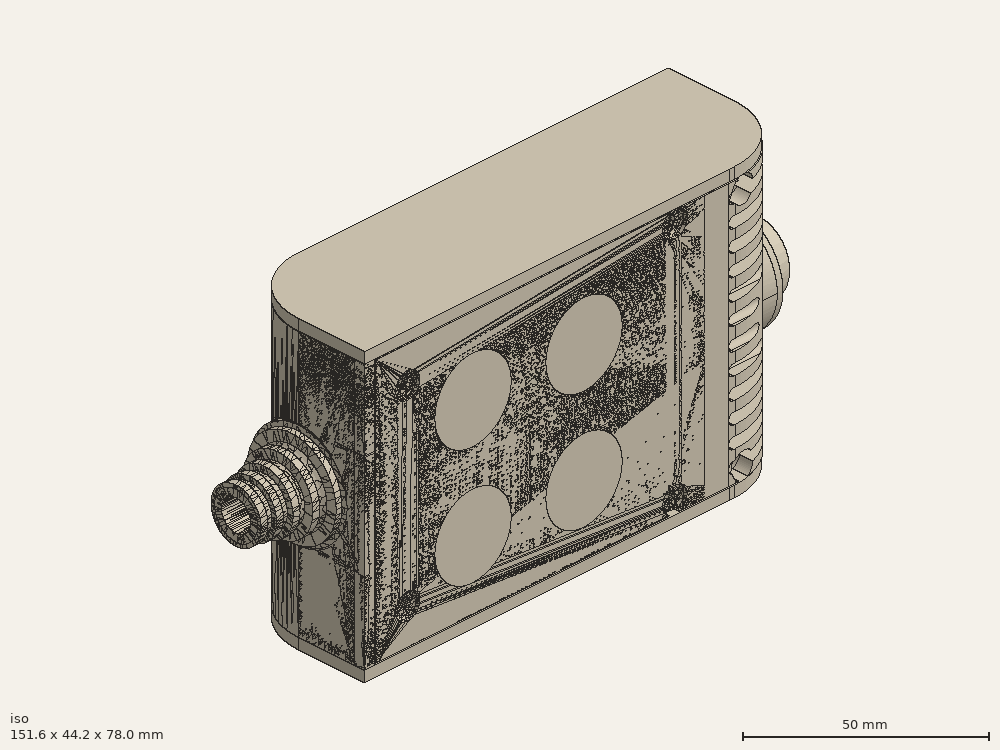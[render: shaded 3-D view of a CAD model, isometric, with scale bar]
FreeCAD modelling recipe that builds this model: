
FCSTD DOCUMENT  (FreeCAD 0.19R0.19.2)
Label: enclosure_196FCStd
License: All rights reserved
LicenseURL: http://en.wikipedia.org/wiki/All_rights_reserved
objects: Part::Revolution×152, Part::MultiFuse×146, Part::Feature×146, Sketcher::SketchObject×84, Part::Cut×70, Part::Cylinder×70, Part::Extrusion×67, Part::Fillet×58, Part::Box×36, App::MeasureDistance×4, PartDesign::Body×2, Image::ImagePlane×1
note: 831 computed .brp shape members not serialized (recipe doc carries the construction recipe); baked Part::Feature solids carry a one-line shape summary decoded from their .brp

FEATURE [Sketcher::SketchObject] Sketch  label="topSketch"
  FullyConstrained = true
  sketch-geometry (20):
    g0: LineSegment StartX=5.21097e-06 StartY=3 StartZ=0 EndX=5.21097e-06 EndY=19 EndZ=0
    g1: ArcOfCircle CenterX=19 CenterY=19 CenterZ=0 NormalX=0 NormalY=0 NormalZ=1 AngleXU=0 Radius=19 StartAngle=1.5708 EndAngle=3.14159
    g2: ArcOfCircle CenterX=19 CenterY=19 CenterZ=0 NormalX=0 NormalY=0 NormalZ=1 AngleXU=0 Radius=16 StartAngle=1.5708 EndAngle=3.14159
    g3: LineSegment StartX=114 StartY=35 StartZ=0 EndX=19 EndY=35 EndZ=0
    g4: LineSegment StartX=5.21097e-06 StartY=3 StartZ=0 EndX=5.21097e-06 EndY=0 EndZ=0
    g5: LineSegment StartX=3 StartY=0 StartZ=0 EndX=5.21097e-06 EndY=0 EndZ=0
    g6: LineSegment StartX=3 StartY=19 StartZ=0 EndX=3 EndY=0 EndZ=0
    g7: LineSegment StartX=19 StartY=38 StartZ=0 EndX=124 EndY=38 EndZ=0
    g8: Circle CenterX=119 CenterY=35 CenterZ=0 NormalX=0 NormalY=0 NormalZ=1 AngleXU=0 Radius=1
    g9: Circle CenterX=121 CenterY=35 CenterZ=0 NormalX=0 NormalY=0 NormalZ=1 AngleXU=0 Radius=1
    g10: Circle CenterX=121 CenterY=33 CenterZ=0 NormalX=0 NormalY=0 NormalZ=1 AngleXU=0 Radius=1
    g11: BSplineCurve PolesCount=3 KnotsCount=2 Degree=2 IsPeriodic=0
    g12: GeomPoint X=119 Y=35 Z=0
    g13: GeomPoint X=121 Y=33 Z=0
    g14: LineSegment StartX=119 StartY=35 StartZ=0 EndX=114 EndY=35 EndZ=0
    g15: ArcOfCircle CenterX=105 CenterY=19 CenterZ=0 NormalX=0 NormalY=0 NormalZ=1 AngleXU=0 Radius=19 StartAngle=5.7297 EndAngle=6.28319
    g16: ArcOfCircle CenterX=105 CenterY=19 CenterZ=0 NormalX=0 NormalY=0 NormalZ=1 AngleXU=0 Radius=16 StartAngle=5.60905 EndAngle=6.28319
    g17: LineSegment StartX=121 StartY=33 StartZ=0 EndX=121 EndY=19 EndZ=0
    g18: LineSegment StartX=124 StartY=38 StartZ=0 EndX=124 EndY=19 EndZ=0
    g19: LineSegment StartX=117.5 StartY=9.01251 StartZ=0 EndX=121.163 EndY=9.0125 EndZ=0
  constraints (46):
    c: Vertical(g0)
    c: Block(g0)
    c: Coincident(g1,g0)
    c: Block(g1)
    c: Coincident(g2,g1)
    c: Block(g2)
    c: Coincident(g3,g2)
    c: Horizontal(g3)
    c: Tangent(g3,g2)
    c: Coincident(g4,g0)
    c: Distance(g4) = 3
    c: Vertical(g4)
    c: Coincident(g5,g4)
    c: Horizontal(g5)
    c: Coincident(g6,g2)
    c: Coincident(g6,g5)
    c: Vertical(g6)
    c: Horizontal(g7)
    c: Distance(g7) = 105
    c: Coincident(g7,g1)
    c: Block(g3)
    c: Weight(g8) = 1
    c: Equal(g8,g9)
    c: Equal(g8,g10)
    c: InternalAlignment(g8,g11)
    c: InternalAlignment(g9,g11)
    c: InternalAlignment(g10,g11)
    c: InternalAlignment(g12,g11)
    c: InternalAlignment(g13,g11)
    c: Block(g11)
    c: Coincident(g14,g11)
    c: Coincident(g14,g3)
    c: Horizontal(g14)
    c: Block(g15)
    c: Coincident(g16,g15)
    c: Block(g16)
    c: Coincident(g17,g11)
    c: Coincident(g17,g16)
    c: Vertical(g17)
    c: Distance(g17) = 14
    c: Coincident(g18,g7)
    c: Coincident(g18,g15)
    c: Vertical(g18)
    c: Distance(g18) = 19
    c: Coincident(g19,g16)
    c: Coincident(g19,g15)
FEATURE [Sketcher::SketchObject] Sketch001  label="bottomSketch"
  FullyConstrained = true
  sketch-geometry (32):
    g0: LineSegment StartX=3.3 StartY=-6.03275e-07 StartZ=0 EndX=98 EndY=-6.03275e-07 EndZ=0
    g1: ArcOfCircle CenterX=98 CenterY=19 CenterZ=0 NormalX=0 NormalY=0 NormalZ=1 AngleXU=0 Radius=19 StartAngle=4.71239 EndAngle=5.71103
    g2: LineSegment StartX=6.3 StartY=8 StartZ=0 EndX=3.3 EndY=8 EndZ=0
    g3: LineSegment StartX=3.3 StartY=8 StartZ=0 EndX=3.3 EndY=-6.03275e-07 EndZ=0
    g4: ArcOfCircle CenterX=8.3 CenterY=5 CenterZ=0 NormalX=0 NormalY=0 NormalZ=1 AngleXU=0 Radius=2 StartAngle=3.14159 EndAngle=4.71239
    g5: LineSegment StartX=6.3 StartY=8 StartZ=0 EndX=6.3 EndY=5 EndZ=0
    g6: ArcOfCircle CenterX=98 CenterY=19 CenterZ=0 NormalX=0 NormalY=0 NormalZ=1 AngleXU=0 Radius=12.7 StartAngle=4.71239 EndAngle=6.28319
    g7: LineSegment StartX=94.7 StartY=3 StartZ=0 EndX=8.3 EndY=3 EndZ=0
    g8-g12: Circle x5 (B-spline internal-alignment scaffolding for g13; pole/knot coordinates omitted)
    g13: BSplineCurve PolesCount=5 KnotsCount=3 Degree=3 IsPeriodic=0
    g14: GeomPoint X=98 Y=6.3 Z=0
    g15: GeomPoint X=96.3938 Y=4.71946 Z=0
    g16: GeomPoint X=94.7 Y=3 Z=0
    g17-g23: Circle x7 (B-spline internal-alignment scaffolding for g24; pole/knot coordinates omitted)
    g24: BSplineCurve PolesCount=7 KnotsCount=5 Degree=3 IsPeriodic=0
    g25-g29: GeomPoint x5 (B-spline internal-alignment scaffolding for g24; pole/knot coordinates omitted)
    g30: ArcOfCircle CenterX=98 CenterY=19 CenterZ=0 NormalX=0 NormalY=0 NormalZ=1 AngleXU=0 Radius=15.7 StartAngle=5.81226 EndAngle=6.28319
    g31: LineSegment StartX=110.7 StartY=19 StartZ=0 EndX=113.7 EndY=19 EndZ=0
  constraints (41):
    c: Horizontal(g0)
    c: Coincident(g1,g0)
    c: Block(g1)
    c: Horizontal(g2)
    c: Distance(g2) = 3
    c: Coincident(g3,g2)
    c: Vertical(g3)
    c: Coincident(g3,g0)
    c: Block(g4)
    c: Block(g2)
    c: Coincident(g5,g2)
    c: Coincident(g5,g4)
    c: Vertical(g5)
    c: Coincident(g6,g1)
    c: Block(g6)
    c: Coincident(g7,g4)
    c: Horizontal(g7)
    c: Block(g0)
    c: Block(g7)
    c: Block(g3)
    c: Coincident(g13,g6)
    c: Weight(g8) = 1
    c: Equal(g8, g9-g12) x4
    c: Coincident(g13,g7)
    c: InternalAlignment(g8-g12 -> g13) x5
    c: InternalAlignment(g14,g13)
    c: InternalAlignment(g15,g13)
    c: InternalAlignment(g16,g13)
    c: Block(g13)
    c: Weight(g17) = 1
    c: Equal(g17, g18-g23) x6
    c: Coincident(g24,g1)
    c: InternalAlignment(g17-g23 -> g24) x7
    c: InternalAlignment(g25-g29 -> g24) x5
    c: Block(g24)
    c: Coincident(g30,g24)
    c: Coincident(g31,g6)
    c: Coincident(g31,g30)
    c: Horizontal(g31)
    c: Block(g31)
    c: Block(g30)
FEATURE [Part::Extrusion] Extrude  label="top"
  Base = -> Sketch
  Dir = (0,0,1)
  DirMode = 2
  FaceMakerClass = Part::FaceMakerBullseye
  LengthFwd = 72
  LengthRev = 0
  Solid = true
  Symmetric = false
FEATURE [Part::Extrusion] Extrude001  label="bottom"
  Base = -> Sketch001
  Dir = (0,0,1)
  DirMode = 2
  FaceMakerClass = Part::FaceMakerBullseye
  LengthFwd = 71.4
  LengthRev = 0
  Placement = pos=(0,0,0.3) rot=(0,0,1;0rad)
  Solid = true
  Symmetric = false
FEATURE [Sketcher::SketchObject] Sketch002  label="topSketch001"
  FullyConstrained = true
  sketch-geometry (8):
    g0: ArcOfCircle CenterX=19 CenterY=19.0975 CenterZ=0 NormalX=0 NormalY=0 NormalZ=1 AngleXU=0 Radius=18.9025 StartAngle=1.5708 EndAngle=3.14674
    g1: LineSegment StartX=0.0977805 StartY=19.0003 StartZ=0 EndX=0.0977805 EndY=0.000251602 EndZ=0
    g2: LineSegment StartX=19 StartY=38 StartZ=0 EndX=124 EndY=38 EndZ=0
    g3: LineSegment StartX=0.0977805 StartY=0.000251602 StartZ=0 EndX=105.098 EndY=0.000251602 EndZ=0
    g4: LineSegment StartX=124 StartY=38 StartZ=0 EndX=125.616 EndY=38 EndZ=0
    g5: LineSegment StartX=105.098 StartY=0.000251602 StartZ=0 EndX=106.713 EndY=0.000251602 EndZ=0
    g6: ArcOfCircle CenterX=106.616 CenterY=19 CenterZ=0 NormalX=0 NormalY=0 NormalZ=1 AngleXU=0 Radius=19 StartAngle=4.71754 EndAngle=6.28319
    g7: LineSegment StartX=125.616 StartY=38 StartZ=0 EndX=125.616 EndY=19 EndZ=0
  constraints (21):
    c: Block(g0)
    c: Coincident(g1,g0)
    c: Vertical(g1)
    c: Horizontal(g2)
    c: Distance(g2) = 105
    c: Coincident(g2,g0)
    c: Distance(g1) = 19
    c: Coincident(g3,g1)
    c: Horizontal(g3)
    c: Distance(g3) = 105
    c: Coincident(g4,g2)
    c: Horizontal(g4)
    c: Distance(g4) = 1.61553
    c: Horizontal(g5)
    c: Equal(g4,g5) = 1.61553
    c: Coincident(g5,g3)
    c: Block(g6)
    c: Coincident(g6,g5)
    c: Coincident(g7,g4)
    c: Coincident(g7,g6)
    c: Vertical(g7)
FEATURE [Part::Extrusion] Extrude002  label="sideA"
  Base = -> Sketch002
  Dir = (0,0,1)
  DirMode = 2
  FaceMakerClass = Part::FaceMakerBullseye
  LengthFwd = 3
  LengthRev = 0
  Placement = pos=(0,0,-3) rot=(0,0,1;0rad)
  Solid = true
  Symmetric = false
FEATURE [Sketcher::SketchObject] Sketch003  label="topSketch002"
  FullyConstrained = true
  sketch-geometry (6):
    g0: LineSegment StartX=19 StartY=38 StartZ=0 EndX=117 EndY=38 EndZ=0
    g1: ArcOfCircle CenterX=19 CenterY=19 CenterZ=0 NormalX=0 NormalY=0 NormalZ=1 AngleXU=0 Radius=19 StartAngle=1.5708 EndAngle=3.14159
    g2: LineSegment StartX=117 StartY=38 StartZ=0 EndX=117 EndY=19 EndZ=0
    g3: LineSegment StartX=98 StartY=1.0161e-12 StartZ=0 EndX=5.22862e-06 EndY=1.0161e-12 EndZ=0
    g4: LineSegment StartX=5.22862e-06 StartY=19 StartZ=0 EndX=5.22862e-06 EndY=1.0161e-12 EndZ=0
    g5: ArcOfCircle CenterX=98 CenterY=19 CenterZ=0 NormalX=0 NormalY=0 NormalZ=1 AngleXU=0 Radius=19 StartAngle=4.71239 EndAngle=6.28319
  constraints (16):
    c: Horizontal(g0)
    c: Distance(g0) = 98
    c: Coincident(g1,g0)
    c: Block(g1)
    c: Coincident(g2,g0)
    c: Vertical(g2)
    c: Distance(g2) = 19
    c: Horizontal(g3)
    c: Coincident(g4,g1)
    c: Vertical(g4)
    c: Coincident(g3,g4)
    c: Block(g3)
    c: Coincident(g5,g2)
    c: Coincident(g5,g3)
    c: Block(g0)
    c: Block(g5)
FEATURE [Sketcher::SketchObject] Sketch004
  FullyConstrained = true
  MapMode = 3
  Placement = pos=(0,0,0) rot=(1,0,0;1.5708rad)
  Support = -> [Extrude]
  sketch-geometry (8):
    g0: Circle CenterX=80.351 CenterY=-67.6202 CenterZ=0 NormalX=0 NormalY=0 NormalZ=1 AngleXU=0 Radius=2
    g1: Circle CenterX=80.351 CenterY=-67.6202 CenterZ=0 NormalX=0 NormalY=0 NormalZ=1 AngleXU=0 Radius=3
    g2: Circle CenterX=80.351 CenterY=-4.92017 CenterZ=0 NormalX=0 NormalY=0 NormalZ=1 AngleXU=0 Radius=2
    g3: Circle CenterX=80.351 CenterY=-4.92017 CenterZ=0 NormalX=0 NormalY=0 NormalZ=1 AngleXU=0 Radius=3
    g4: Circle CenterX=23.851 CenterY=-4.92017 CenterZ=0 NormalX=0 NormalY=0 NormalZ=1 AngleXU=0 Radius=2
    g5: Circle CenterX=23.851 CenterY=-4.92017 CenterZ=0 NormalX=0 NormalY=0 NormalZ=1 AngleXU=0 Radius=3
    g6: Circle CenterX=23.851 CenterY=-67.6202 CenterZ=0 NormalX=0 NormalY=0 NormalZ=1 AngleXU=0 Radius=2
    g7: Circle CenterX=23.851 CenterY=-67.6202 CenterZ=0 NormalX=0 NormalY=0 NormalZ=1 AngleXU=0 Radius=3
  constraints (8):
    c: Block(g3)
    c: Block(g2)
    c: Block(g1)
    c: Block(g0)
    c: Block(g6)
    c: Block(g7)
    c: Block(g4)
    c: Block(g5)
FEATURE [Part::Extrusion] Extrude004
  Base = -> Sketch004
  Dir = (0,-1,2e-16)
  DirMode = 2
  FaceMakerClass = Part::FaceMakerBullseye
  LengthFwd = 6
  LengthRev = 0
  Placement = pos=(0,9,0) rot=(0,0,1;0rad)
  Solid = true
  Symmetric = false
FEATURE [Sketcher::SketchObject] Sketch005
  FullyConstrained = true
  MapMode = 3
  Placement = pos=(0,0,0) rot=(1,0,0;1.5708rad)
  Support = -> [Extrude]
  sketch-geometry (8):
    g0: Circle CenterX=80.351 CenterY=-67.6202 CenterZ=0 NormalX=0 NormalY=0 NormalZ=1 AngleXU=0 Radius=3
    g1: Circle CenterX=80.351 CenterY=-4.92017 CenterZ=0 NormalX=0 NormalY=0 NormalZ=1 AngleXU=0 Radius=3
    g2: Circle CenterX=23.851 CenterY=-4.92017 CenterZ=0 NormalX=0 NormalY=0 NormalZ=1 AngleXU=0 Radius=3
    g3: Circle CenterX=23.851 CenterY=-67.6202 CenterZ=0 NormalX=0 NormalY=0 NormalZ=1 AngleXU=0 Radius=3
    g4: Circle CenterX=23.851 CenterY=-67.6202 CenterZ=0 NormalX=0 NormalY=0 NormalZ=1 AngleXU=0 Radius=5
    g5: Circle CenterX=80.351 CenterY=-67.6202 CenterZ=0 NormalX=0 NormalY=0 NormalZ=1 AngleXU=0 Radius=5
    g6: Circle CenterX=23.851 CenterY=-4.92017 CenterZ=0 NormalX=0 NormalY=0 NormalZ=1 AngleXU=0 Radius=5
    g7: Circle CenterX=80.351 CenterY=-4.92017 CenterZ=0 NormalX=0 NormalY=0 NormalZ=1 AngleXU=0 Radius=5
  constraints (8):
    c: Block(g1)
    c: Block(g0)
    c: Block(g3)
    c: Block(g2)
    c: Block(g5)
    c: Block(g4)
    c: Block(g6)
    c: Block(g7)
FEATURE [Part::Extrusion] Extrude005
  Base = -> Sketch005
  Dir = (0,-1,2e-16)
  DirMode = 2
  FaceMakerClass = Part::FaceMakerBullseye
  LengthFwd = 2
  LengthRev = 0
  Solid = true
  Symmetric = false
FEATURE [Sketcher::SketchObject] Sketch006
  FullyConstrained = true
  MapMode = 3
  Placement = pos=(0,0,0) rot=(1,0,0;1.5708rad)
  sketch-geometry (8):
    g0: Circle CenterX=80.351 CenterY=-67.6202 CenterZ=0 NormalX=0 NormalY=0 NormalZ=1 AngleXU=0 Radius=3
    g1: Circle CenterX=80.351 CenterY=-4.92017 CenterZ=0 NormalX=0 NormalY=0 NormalZ=1 AngleXU=0 Radius=3
    g2: Circle CenterX=23.851 CenterY=-4.92017 CenterZ=0 NormalX=0 NormalY=0 NormalZ=1 AngleXU=0 Radius=3
    g3: Circle CenterX=23.851 CenterY=-67.6202 CenterZ=0 NormalX=0 NormalY=0 NormalZ=1 AngleXU=0 Radius=3
    g4: Circle CenterX=23.851 CenterY=-67.6202 CenterZ=0 NormalX=0 NormalY=0 NormalZ=1 AngleXU=0 Radius=5
    g5: Circle CenterX=80.351 CenterY=-67.6202 CenterZ=0 NormalX=0 NormalY=0 NormalZ=1 AngleXU=0 Radius=5
    g6: Circle CenterX=23.851 CenterY=-4.92017 CenterZ=0 NormalX=0 NormalY=0 NormalZ=1 AngleXU=0 Radius=5
    g7: Circle CenterX=80.351 CenterY=-4.92017 CenterZ=0 NormalX=0 NormalY=0 NormalZ=1 AngleXU=0 Radius=5
  constraints (8):
    c: Block(g1)
    c: Block(g0)
    c: Block(g3)
    c: Block(g2)
    c: Block(g5)
    c: Block(g4)
    c: Block(g6)
    c: Block(g7)
FEATURE [Part::Extrusion] Extrude007
  Base = -> Sketch006
  Dir = (0,-1,2e-16)
  DirMode = 2
  FaceMakerClass = Part::FaceMakerBullseye
  LengthFwd = 2
  LengthRev = 0
  Solid = true
  Symmetric = false
FEATURE [Part::Fillet] Fillet
  Base = -> Extrude007
  Edges = 4 edges r=1.99: [Edge6,Edge12,Edge18,Edge24]
FEATURE [Part::Cut] Cut
  Base = -> Extrude005
  Placement = pos=(0,5,0) rot=(0,0,1;0rad)
  Tool = -> Fillet
FEATURE [Part::MultiFuse] Fusion  label="pCBScrews"
  Placement = pos=(-2.5,0,72.3) rot=(0,0,1;0rad)
  Shapes = -> [Extrude004,Cut]
FEATURE [App::MeasureDistance] Distance  label="Distance: 0.69 mm"
  Distance = 0.685967
  P1 = (24.0138,2.9647,0.3)
  P2 = (23.8901,3,-0.373787)
FEATURE [App::MeasureDistance] Distance001  label="Distance: 0.53 mm"
  Distance = 0.533607
  P1 = (80.2939,3,72.2334)
  P2 = (80.281,2.99661,71.7)
FEATURE [Part::Fillet] Fillet001
  Base = -> Extrude001
  Edges = 1 edges r=2.4: [Edge17]
FEATURE [Part::Fillet] Fillet002  label="bottom001"
  Base = -> Fillet001
  Edges = 1 edges r=2.4: [Edge36]
FEATURE [Part::Fillet] Fillet003  label="top001"
  Base = -> Extrude
  Edges = 1 edges r=2: [Edge1]
FEATURE [Sketcher::SketchObject] Sketch007
  FullyConstrained = true
  sketch-geometry (16):
    g0: LineSegment StartX=4 StartY=0 StartZ=0 EndX=4 EndY=2.4 EndZ=0
    g1: LineSegment StartX=4 StartY=2.4 StartZ=0 EndX=7 EndY=2.4 EndZ=0
    g2: LineSegment StartX=4 StartY=0 StartZ=0 EndX=5.7 EndY=0 EndZ=0
    g3: LineSegment StartX=5.7 StartY=0 StartZ=0 EndX=5.7 EndY=-5.6 EndZ=0
    g4-g8: Circle x5 (B-spline internal-alignment scaffolding for g9; pole/knot coordinates omitted)
    g9: BSplineCurve PolesCount=5 KnotsCount=3 Degree=3 IsPeriodic=0
    g10: GeomPoint X=7 Y=2.4 Z=0
    g11: GeomPoint X=10.4582 Y=-1.55472 Z=0
    g12: GeomPoint X=14 Y=-5.6 Z=0
    g13: LineSegment StartX=14 StartY=-5.6 StartZ=0 EndX=14 EndY=-14.1 EndZ=0
    g14: LineSegment StartX=14 StartY=-14.1 StartZ=0 EndX=6.5 EndY=-14.1 EndZ=0
    g15: LineSegment StartX=5.7 StartY=-5.6 StartZ=0 EndX=6.5 EndY=-14.1 EndZ=0
  constraints (28):
    c: Distance(g0) = 2.4
    c: Vertical(g0)
    c: Block(g0)
    c: Coincident(g1,g0)
    c: Horizontal(g1)
    c: Distance(g1) = 3
    c: Coincident(g2,g0)
    c: Horizontal(g2)
    c: Distance(g2) = 1.7
    c: Coincident(g3,g2)
    c: Vertical(g3)
    c: Distance(g3) = 5.6
    c: Coincident(g9,g1)
    c: Weight(g4) = 1
    c: Equal(g4, g5-g8) x4
    c: InternalAlignment(g4-g8 -> g9) x5
    c: InternalAlignment(g10,g9)
    c: InternalAlignment(g11,g9)
    c: InternalAlignment(g12,g9)
    c: Block(g9)
    c: Coincident(g13,g9)
    c: Vertical(g13)
    c: Distance(g13) = 8.5
    c: Coincident(g14,g13)
    c: Horizontal(g14)
    c: Distance(g14) = 7.5
    c: Coincident(g15,g3)
    c: Coincident(g15,g14)
FEATURE [Part::Feature] Face
  shape: bbox 10 x 16.5 x 2e-07 mm, 1 faces, 0 solids (baked)
FEATURE [Part::Revolution] Revolve  label="plugHousing"
  Angle = 360
  Axis = (0,1,0)
  Base = (0,0,0)
  FaceMakerClass = Part::FaceMakerBullseye
  Placement = pos=(0,0,36.15) rot=(0,0,1;0rad)
  Solid = false
  Source = -> Face
  Symmetric = false
FEATURE [Part::Feature] Face001
  shape: bbox 10 x 16.5 x 2e-07 mm, 1 faces, 0 solids (baked)
FEATURE [Part::Revolution] Revolve001  label="plugHousing001"
  Angle = 360
  Axis = (0,1,0)
  Base = (0,0,0)
  FaceMakerClass = Part::FaceMakerBullseye
  Placement = pos=(0,0,36.15) rot=(0,0,1;0rad)
  Solid = false
  Source = -> Face001
  Symmetric = false
FEATURE [Part::MultiFuse] Fusion001  label="plugHousing002"
  Placement = pos=(0,0,0) rot=(0,0,1;1.5708rad)
  Shapes = -> [Revolve001,Revolve]
FEATURE [Part::Feature] Face002
  shape: bbox 10 x 16.5 x 2e-07 mm, 1 faces, 0 solids (baked)
FEATURE [Part::Revolution] Revolve003  label="plugHousing005"
  Angle = 360
  Axis = (0,1,0)
  Base = (0,0,0)
  FaceMakerClass = Part::FaceMakerBullseye
  Placement = pos=(0,0,36.15) rot=(0,0,1;0rad)
  Solid = false
  Source = -> Face002
  Symmetric = false
FEATURE [Part::Feature] Face003
  shape: bbox 10 x 16.5 x 2e-07 mm, 1 faces, 0 solids (baked)
FEATURE [Part::Revolution] Revolve002  label="plugHousing003"
  Angle = 360
  Axis = (0,1,0)
  Base = (0,0,0)
  FaceMakerClass = Part::FaceMakerBullseye
  Placement = pos=(0,0,36.15) rot=(0,0,1;0rad)
  Solid = false
  Source = -> Face003
  Symmetric = false
FEATURE [Part::MultiFuse] Fusion002  label="plugHousing004"
  Placement = pos=(0,0,0) rot=(0,0,1;1.5708rad)
  Shapes = -> [Revolve002,Revolve003]
FEATURE [Part::MultiFuse] Fusion003  label="plugHousing006"
  Placement = pos=(0,19,0) rot=(0,0,1;3.14159rad)
  Shapes = -> [Fusion002,Fusion001]
FEATURE [Part::Feature] Face004
  shape: bbox 10 x 16.5 x 2e-07 mm, 1 faces, 0 solids (baked)
FEATURE [Part::Revolution] Revolve006  label="plugHousing010"
  Angle = 360
  Axis = (0,1,0)
  Base = (0,0,0)
  FaceMakerClass = Part::FaceMakerBullseye
  Placement = pos=(0,0,36.15) rot=(0,0,1;0rad)
  Solid = false
  Source = -> Face004
  Symmetric = false
FEATURE [Part::Feature] Face005
  shape: bbox 10 x 16.5 x 2e-07 mm, 1 faces, 0 solids (baked)
FEATURE [Part::Revolution] Revolve007  label="plugHousing011"
  Angle = 360
  Axis = (0,1,0)
  Base = (0,0,0)
  FaceMakerClass = Part::FaceMakerBullseye
  Placement = pos=(0,0,36.15) rot=(0,0,1;0rad)
  Solid = false
  Source = -> Face005
  Symmetric = false
FEATURE [Part::Feature] Face006
  shape: bbox 10 x 16.5 x 2e-07 mm, 1 faces, 0 solids (baked)
FEATURE [Part::Revolution] Revolve004  label="plugHousing007"
  Angle = 360
  Axis = (0,1,0)
  Base = (0,0,0)
  FaceMakerClass = Part::FaceMakerBullseye
  Placement = pos=(0,0,36.15) rot=(0,0,1;0rad)
  Solid = false
  Source = -> Face006
  Symmetric = false
FEATURE [Part::MultiFuse] Fusion004  label="plugHousing009"
  Placement = pos=(0,0,0) rot=(0,0,1;1.5708rad)
  Shapes = -> [Revolve004,Revolve007]
FEATURE [Part::Feature] Face007
  shape: bbox 10 x 16.5 x 2e-07 mm, 1 faces, 0 solids (baked)
FEATURE [Part::Revolution] Revolve005  label="plugHousing008"
  Angle = 360
  Axis = (0,1,0)
  Base = (0,0,0)
  FaceMakerClass = Part::FaceMakerBullseye
  Placement = pos=(0,0,36.15) rot=(0,0,1;0rad)
  Solid = false
  Source = -> Face007
  Symmetric = false
FEATURE [Part::MultiFuse] Fusion005  label="plugHousing012"
  Placement = pos=(0,0,0) rot=(0,0,1;1.5708rad)
  Shapes = -> [Revolve006,Revolve005]
FEATURE [Part::MultiFuse] Fusion006  label="plugHousing013"
  Placement = pos=(0,19,0) rot=(0,0,1;3.14159rad)
  Shapes = -> [Fusion005,Fusion004]
FEATURE [Part::MultiFuse] Fusion007  label="plugHousing014"
  Placement = pos=(122.621,0,-0.15) rot=(0,0,1;0rad)
  Shapes = -> [Fusion003,Fusion006]
FEATURE [Part::Cylinder] Cylinder002
  Angle = 360
  AttacherType = Attacher::AttachEngine3D
  Height = 20
  Placement = pos=(0,0,36.15) rot=(0,0,1;0rad)
  Radius = 4
FEATURE [Part::Cylinder] Cylinder003
  Angle = 360
  AttacherType = Attacher::AttachEngine3D
  Height = 10
  Placement = pos=(0,0,36.15) rot=(0,0,1;0rad)
  Radius = 4
FEATURE [Part::MultiFuse] Fusion009  label="removeToCreateHoleForPlugHousing"
  Placement = pos=(70,19,36.15) rot=(0,1,0;1.5708rad)
  Shapes = -> [Cylinder002,Cylinder003]
FEATURE [Part::Cylinder] Cylinder004
  Angle = 360
  AttacherType = Attacher::AttachEngine3D
  Height = 20
  Placement = pos=(0,0,36.15) rot=(0,0,1;0rad)
  Radius = 4
FEATURE [Part::Cylinder] Cylinder005
  Angle = 360
  AttacherType = Attacher::AttachEngine3D
  Height = 10
  Placement = pos=(0,0,36.15) rot=(0,0,1;0rad)
  Radius = 4
FEATURE [Part::MultiFuse] Fusion010  label="removeToCreateHoleForPlugHousing001"
  Placement = pos=(70,19,36.15) rot=(0,1,0;1.5708rad)
  Shapes = -> [Cylinder004,Cylinder005]
FEATURE [Part::Cut] Cut001
  Base = -> Fillet003
  Tool = -> Fusion010
FEATURE [Part::Cut] Cut002  label="Bottom"
  Base = -> Fillet002
  Tool = -> Fusion009
FEATURE [Part::Feature] Face008
  shape: bbox 10 x 16.5 x 2e-07 mm, 1 faces, 0 solids (baked)
FEATURE [Part::Revolution] Revolve011  label="plugHousing021"
  Angle = 360
  Axis = (0,1,0)
  Base = (0,0,0)
  FaceMakerClass = Part::FaceMakerBullseye
  Placement = pos=(0,0,36.15) rot=(0,0,1;0rad)
  Solid = false
  Source = -> Face008
  Symmetric = false
FEATURE [Part::Feature] Face009
  shape: bbox 10 x 16.5 x 2e-07 mm, 1 faces, 0 solids (baked)
FEATURE [Part::Revolution] Revolve012  label="plugHousing022"
  Angle = 360
  Axis = (0,1,0)
  Base = (0,0,0)
  FaceMakerClass = Part::FaceMakerBullseye
  Placement = pos=(0,0,36.15) rot=(0,0,1;0rad)
  Solid = false
  Source = -> Face009
  Symmetric = false
FEATURE [Part::Feature] Face010 .. Face013  x4 (patterned run collapsed; names and placements below)
  shape: bbox 10 x 16.5 x 2e-07 mm, 1 faces, 0 solids (baked)
FEATURE [Part::Revolution] Revolve015  label="plugHousing027"
  Angle = 360
  Axis = (0,1,0)
  Base = (0,0,0)
  FaceMakerClass = Part::FaceMakerBullseye
  Placement = pos=(0,0,36.15) rot=(0,0,1;0rad)
  Solid = false
  Source = -> Face013
  Symmetric = false
FEATURE [Part::Feature] Face014
  shape: bbox 10 x 16.5 x 2e-07 mm, 1 faces, 0 solids (baked)
FEATURE [Part::Feature] Face015
  shape: bbox 10 x 16.5 x 2e-07 mm, 1 faces, 0 solids (baked)
FEATURE [Part::Feature] Face016
  shape: bbox 10 x 16.5 x 2e-07 mm, 1 faces, 0 solids (baked)
FEATURE [Part::Revolution] Revolve019  label="plugHousing033"
  Angle = 360
  Axis = (0,1,0)
  Base = (0,0,0)
  FaceMakerClass = Part::FaceMakerBullseye
  Placement = pos=(0,0,36.15) rot=(0,0,1;0rad)
  Solid = false
  Source = -> Face016
  Symmetric = false
FEATURE [Part::Feature] Face017
  shape: bbox 10 x 16.5 x 2e-07 mm, 1 faces, 0 solids (baked)
FEATURE [Part::Revolution] Revolve020  label="plugHousing034"
  Angle = 360
  Axis = (0,1,0)
  Base = (0,0,0)
  FaceMakerClass = Part::FaceMakerBullseye
  Placement = pos=(0,0,36.15) rot=(0,0,1;0rad)
  Solid = false
  Source = -> Face017
  Symmetric = false
FEATURE [Part::Feature] Face018
  shape: bbox 10 x 16.5 x 2e-07 mm, 1 faces, 0 solids (baked)
FEATURE [Part::Revolution] Revolve016  label="plugHousing030"
  Angle = 360
  Axis = (0,1,0)
  Base = (0,0,0)
  FaceMakerClass = Part::FaceMakerBullseye
  Placement = pos=(0,0,36.15) rot=(0,0,1;0rad)
  Solid = false
  Source = -> Face018
  Symmetric = false
FEATURE [Part::MultiFuse] Fusion020  label="plugHousing038"
  Placement = pos=(0,0,0) rot=(0,0,1;1.5708rad)
  Shapes = -> [Revolve016,Revolve020]
FEATURE [Part::Feature] Face019
  shape: bbox 10 x 16.5 x 2e-07 mm, 1 faces, 0 solids (baked)
FEATURE [Part::Feature] Face020
  shape: bbox 10 x 16.5 x 2e-07 mm, 1 faces, 0 solids (baked)
FEATURE [Part::Revolution] Revolve017  label="plugHousing031"
  Angle = 360
  Axis = (0,1,0)
  Base = (0,0,0)
  FaceMakerClass = Part::FaceMakerBullseye
  Placement = pos=(0,0,36.15) rot=(0,0,1;0rad)
  Solid = false
  Source = -> Face020
  Symmetric = false
FEATURE [Part::MultiFuse] Fusion021  label="plugHousing039"
  Placement = pos=(0,0,0) rot=(0,0,1;1.5708rad)
  Shapes = -> [Revolve019,Revolve017]
FEATURE [Part::MultiFuse] Fusion023  label="plugHousing041"
  Placement = pos=(0,19,0) rot=(0,0,1;3.14159rad)
  Shapes = -> [Fusion021,Fusion020]
FEATURE [Part::Revolution] Revolve022  label="plugHousing043"
  Angle = 360
  Axis = (0,1,0)
  Base = (0,0,0)
  FaceMakerClass = Part::FaceMakerBullseye
  Placement = pos=(0,0,36.15) rot=(0,0,1;0rad)
  Solid = false
  Source = -> Face019
  Symmetric = false
FEATURE [Part::Feature] Face021
  shape: bbox 10 x 16.5 x 2e-07 mm, 1 faces, 0 solids (baked)
FEATURE [Part::Revolution] Revolve023  label="plugHousing044"
  Angle = 360
  Axis = (0,1,0)
  Base = (0,0,0)
  FaceMakerClass = Part::FaceMakerBullseye
  Placement = pos=(0,0,36.15) rot=(0,0,1;0rad)
  Solid = false
  Source = -> Face021
  Symmetric = false
FEATURE [Part::Feature] Face022
  shape: bbox 10 x 16.5 x 2e-07 mm, 1 faces, 0 solids (baked)
FEATURE [Part::Revolution] Revolve018  label="plugHousing032"
  Angle = 360
  Axis = (0,1,0)
  Base = (0,0,0)
  FaceMakerClass = Part::FaceMakerBullseye
  Placement = pos=(0,0,36.15) rot=(0,0,1;0rad)
  Solid = false
  Source = -> Face022
  Symmetric = false
FEATURE [Part::MultiFuse] Fusion022  label="plugHousing040"
  Placement = pos=(0,0,0) rot=(0,0,1;1.5708rad)
  Shapes = -> [Revolve018,Revolve023]
FEATURE [Part::Feature] Face023
  shape: bbox 10 x 16.5 x 2e-07 mm, 1 faces, 0 solids (baked)
FEATURE [Part::Revolution] Revolve021  label="plugHousing035"
  Angle = 360
  Axis = (0,1,0)
  Base = (0,0,0)
  FaceMakerClass = Part::FaceMakerBullseye
  Placement = pos=(0,0,36.15) rot=(0,0,1;0rad)
  Solid = false
  Source = -> Face023
  Symmetric = false
FEATURE [Part::MultiFuse] Fusion018  label="plugHousing036"
  Placement = pos=(0,0,0) rot=(0,0,1;1.5708rad)
  Shapes = -> [Revolve022,Revolve021]
FEATURE [Part::MultiFuse] Fusion019  label="plugHousing037"
  Placement = pos=(0,19,0) rot=(0,0,1;3.14159rad)
  Shapes = -> [Fusion018,Fusion022]
FEATURE [Part::MultiFuse] Fusion024  label="plugHousing042"
  Placement = pos=(122.621,0,-0.15) rot=(0,0,1;0rad)
  Shapes = -> [Fusion023,Fusion019]
FEATURE [Part::Cylinder] Cylinder006
  Angle = 360
  AttacherType = Attacher::AttachEngine3D
  Height = 20
  Placement = pos=(0,0,36.15) rot=(0,0,1;0rad)
  Radius = 14.3
FEATURE [Part::Cylinder] Cylinder007
  Angle = 360
  AttacherType = Attacher::AttachEngine3D
  Height = 10
  Placement = pos=(0,0,36.15) rot=(0,0,1;0rad)
  Radius = 4
FEATURE [Part::MultiFuse] Fusion026  label="removeToCreteHoleForPlugHousing"
  Placement = pos=(70,19,36) rot=(0,1,0;1.5708rad)
  Shapes = -> [Cylinder006,Cylinder007]
FEATURE [Part::Box] Box001  label="Cube001"
  AttacherType = Attacher::AttachEngine3D
  Height = 28
  Length = 3
  Placement = pos=(110.7,19,22) rot=(0,0,1;0rad)
  Width = 15.7
FEATURE [Part::Cut] Cut003  label="top002"
  Base = -> Cut001
  Tool = -> Fusion007
FEATURE [Part::Revolution] Revolve008  label="plugHousing015"
  Angle = 360
  Axis = (0,1,0)
  Base = (0,0,0)
  FaceMakerClass = Part::FaceMakerBullseye
  Placement = pos=(0,0,36.15) rot=(0,0,1;0rad)
  Solid = false
  Source = -> Face010
  Symmetric = false
FEATURE [Part::MultiFuse] Fusion013  label="plugHousing020"
  Placement = pos=(0,0,0) rot=(0,0,1;1.5708rad)
  Shapes = -> [Revolve008,Revolve012]
FEATURE [Part::Cut] Cut004  label="top003"
  Base = -> Cut003
  Placement = pos=(1,0,0) rot=(0,0,1;0rad)
  Tool = -> Fusion026
FEATURE [Part::Cylinder] Cylinder008
  Angle = 360
  AttacherType = Attacher::AttachEngine3D
  Height = 20
  Placement = pos=(0,0,36.15) rot=(0,0,1;0rad)
  Radius = 10.3
FEATURE [Part::Cylinder] Cylinder009
  Angle = 360
  AttacherType = Attacher::AttachEngine3D
  Height = 10
  Placement = pos=(0,0,36.15) rot=(0,0,1;0rad)
  Radius = 4
FEATURE [Part::MultiFuse] Fusion027  label="removeToCreteHoleForPlugHousing001"
  Placement = pos=(70,19,36) rot=(0,1,0;1.5708rad)
  Shapes = -> [Cylinder008,Cylinder009]
FEATURE [Part::Cut] Cut005  label="plugHousingTab"
  Base = -> Box001
  Tool = -> Fusion027
FEATURE [Part::MultiFuse] Fusion028  label="plugHousing045"
  Shapes = -> [Fusion024,Cut005]
FEATURE [Part::Box] Box002  label="Cube002"
  AttacherType = Attacher::AttachEngine3D
  Height = 28.8
  Length = 3
  Placement = pos=(107.3,28,21.6) rot=(0,0,1;0rad)
  Width = 7
FEATURE [Part::Box] Box003  label="Cube003"
  AttacherType = Attacher::AttachEngine3D
  Height = 3
  Length = 6.4
  Placement = pos=(107.3,28,18.6) rot=(0,0,1;0rad)
  Width = 7
FEATURE [Part::Box] Box004  label="Cube004"
  AttacherType = Attacher::AttachEngine3D
  Height = 3
  Length = 6.4
  Placement = pos=(107.3,28,50.4) rot=(0,0,1;0rad)
  Width = 7
FEATURE [Part::MultiFuse] Fusion029  label="plugHousingBracketHolder"
  Shapes = -> [Box004,Box002,Box003]
FEATURE [Part::Cylinder] Cylinder010
  Angle = 360
  AttacherType = Attacher::AttachEngine3D
  Height = 20
  Placement = pos=(0,0,36.15) rot=(0,0,1;0rad)
  Radius = 14.3
FEATURE [Part::Cylinder] Cylinder011
  Angle = 360
  AttacherType = Attacher::AttachEngine3D
  Height = 10
  Placement = pos=(0,0,36.15) rot=(0,0,1;0rad)
  Radius = 4
FEATURE [Part::MultiFuse] Fusion030  label="removeToCreteHoleForPlugHousing002"
  Placement = pos=(70,19,36) rot=(0,1,0;1.5708rad)
  Shapes = -> [Cylinder010,Cylinder011]
FEATURE [Part::Cut] Cut006  label="plugHousingBracketHolder001"
  Base = -> Fusion029
  Tool = -> Fusion030
FEATURE [Part::Cylinder] Cylinder012
  Angle = 360
  AttacherType = Attacher::AttachEngine3D
  Height = 20
  Placement = pos=(0,0,36.15) rot=(0,0,1;0rad)
  Radius = 7
FEATURE [Part::Cylinder] Cylinder013
  Angle = 360
  AttacherType = Attacher::AttachEngine3D
  Height = 10
  Placement = pos=(0,0,36.15) rot=(0,0,1;0rad)
  Radius = 4
FEATURE [Part::MultiFuse] Fusion032  label="removeToCreteHoleForPlugHousing003"
  Placement = pos=(70,19,36) rot=(0,1,0;1.5708rad)
  Shapes = -> [Cylinder012,Cylinder013]
FEATURE [Part::Cut] Cut007  label="bottom002"
  Base = -> Cut002
  Tool = -> Fusion032
FEATURE [Sketcher::SketchObject] Sketch008
  FullyConstrained = true
  sketch-geometry (54):
    g0: LineSegment StartX=-4.2 StartY=0 StartZ=0 EndX=-6.2 EndY=0 EndZ=0
    g1: LineSegment StartX=-14 StartY=-18 StartZ=0 EndX=-14 EndY=-26.5 EndZ=0
    g2: LineSegment StartX=-4.2 StartY=0 StartZ=0 EndX=-4.2 EndY=-13.4877 EndZ=0
    g3: Circle CenterX=-4.2 CenterY=-13.4877 CenterZ=0 NormalX=0 NormalY=0 NormalZ=1 AngleXU=0 Radius=1
    g4: Circle CenterX=-4.2 CenterY=-26.5 CenterZ=0 NormalX=0 NormalY=0 NormalZ=1 AngleXU=0 Radius=1
    g5: Circle CenterX=-8.2 CenterY=-26.5 CenterZ=0 NormalX=0 NormalY=0 NormalZ=1 AngleXU=0 Radius=1
    g6: BSplineCurve PolesCount=3 KnotsCount=2 Degree=2 IsPeriodic=0
    g7: GeomPoint X=-4.2 Y=-13.4877 Z=0
    g8: GeomPoint X=-8.2 Y=-26.5 Z=0
    g9: LineSegment StartX=-14 StartY=-26.5 StartZ=0 EndX=-8.2 EndY=-26.5 EndZ=0
    g10: LineSegment StartX=-10.15 StartY=-12 StartZ=0 EndX=-10.15 EndY=-14 EndZ=0
    g11: LineSegment StartX=-12.8401 StartY=-16 StartZ=0 EndX=-10.1571 EndY=-16 EndZ=0
    g12: LineSegment StartX=-10.15 StartY=-14 StartZ=0 EndX=-8.70761 EndY=-14 EndZ=0
    g13: LineSegment StartX=-12.8401 StartY=-16 StartZ=0 EndX=-12.8401 EndY=-17.6958 EndZ=0
    g14: LineSegment StartX=-10.15 StartY=-12 StartZ=0 EndX=-7.79258 EndY=-12 EndZ=0
    g15: Circle CenterX=-6.2215 CenterY=-2 CenterZ=0 NormalX=0 NormalY=0 NormalZ=1 AngleXU=0 Radius=1
    g16: Circle CenterX=-6.22762 CenterY=-2.58724 CenterZ=0 NormalX=0 NormalY=0 NormalZ=1 AngleXU=0 Radius=1
    g17: Circle CenterX=-6.32538 CenterY=-4 CenterZ=0 NormalX=0 NormalY=0 NormalZ=1 AngleXU=0 Radius=1
    g18: BSplineCurve PolesCount=3 KnotsCount=2 Degree=2 IsPeriodic=0
    g19: GeomPoint X=-6.2215 Y=-2 Z=0
    g20: GeomPoint X=-6.32538 Y=-4 Z=0
    g21: Circle CenterX=-6.48644 CenterY=-5.99526 CenterZ=0 NormalX=0 NormalY=0 NormalZ=1 AngleXU=0 Radius=1
    g22: Circle CenterX=-6.58486 CenterY=-6.99526 CenterZ=0 NormalX=0 NormalY=0 NormalZ=1 AngleXU=0 Radius=1
    g23: Circle CenterX=-6.77343 CenterY=-8 CenterZ=0 NormalX=0 NormalY=0 NormalZ=1 AngleXU=0 Radius=1
    g24: BSplineCurve PolesCount=3 KnotsCount=2 Degree=2 IsPeriodic=0
    g25: GeomPoint X=-6.48644 Y=-5.99526 Z=0
    g26: GeomPoint X=-6.77343 Y=-8 Z=0
    g27: Circle CenterX=-7.19003 CenterY=-10 CenterZ=0 NormalX=0 NormalY=0 NormalZ=1 AngleXU=0 Radius=1
    g28: Circle CenterX=-7.44407 CenterY=-11.0915 CenterZ=0 NormalX=0 NormalY=0 NormalZ=1 AngleXU=0 Radius=1
    g29: Circle CenterX=-7.79258 CenterY=-12 CenterZ=0 NormalX=0 NormalY=0 NormalZ=1 AngleXU=0 Radius=1
    g30: BSplineCurve PolesCount=3 KnotsCount=2 Degree=2 IsPeriodic=0
    g31: GeomPoint X=-7.19003 Y=-10 Z=0
    g32: GeomPoint X=-7.79258 Y=-12 Z=0
    g33: Circle CenterX=-8.70761 CenterY=-14 CenterZ=0 NormalX=0 NormalY=0 NormalZ=1 AngleXU=0 Radius=1
    g34: Circle CenterX=-9.33087 CenterY=-15.1837 CenterZ=0 NormalX=0 NormalY=0 NormalZ=1 AngleXU=0 Radius=1
    g35: Circle CenterX=-10.1571 CenterY=-16 CenterZ=0 NormalX=0 NormalY=0 NormalZ=1 AngleXU=0 Radius=1
    g36: BSplineCurve PolesCount=3 KnotsCount=2 Degree=2 IsPeriodic=0
    g37: GeomPoint X=-8.70761 Y=-14 Z=0
    g38: GeomPoint X=-10.1571 Y=-16 Z=0
    g39: Circle CenterX=-12.8401 CenterY=-17.6958 CenterZ=0 NormalX=0 NormalY=0 NormalZ=1 AngleXU=0 Radius=1
    g40: Circle CenterX=-13.3521 CenterY=-17.9027 CenterZ=0 NormalX=0 NormalY=0 NormalZ=1 AngleXU=0 Radius=1
    g41: Circle CenterX=-14 CenterY=-18 CenterZ=0 NormalX=0 NormalY=0 NormalZ=1 AngleXU=0 Radius=1
    g42: BSplineCurve PolesCount=3 KnotsCount=2 Degree=2 IsPeriodic=0
    g43: GeomPoint X=-12.8401 Y=-17.6958 Z=0
    g44: GeomPoint X=-14 Y=-18 Z=0
    g45: LineSegment StartX=-6.2 StartY=0 StartZ=0 EndX=-7.2 EndY=0 EndZ=0
    g46: LineSegment StartX=-7.2 StartY=0 StartZ=0 EndX=-7.2 EndY=-2 EndZ=0
    g47: LineSegment StartX=-7.2 StartY=-2 StartZ=0 EndX=-6.2215 EndY=-2 EndZ=0
    g48: LineSegment StartX=-6.32538 StartY=-4 StartZ=0 EndX=-7.65538 EndY=-4 EndZ=0
    g49: LineSegment StartX=-7.65538 StartY=-4 StartZ=0 EndX=-7.65538 EndY=-5.99526 EndZ=0
    g50: LineSegment StartX=-7.65538 StartY=-5.99526 StartZ=0 EndX=-6.48644 EndY=-5.99526 EndZ=0
    g51: LineSegment StartX=-6.77343 StartY=-8 StartZ=0 EndX=-8.43343 EndY=-8 EndZ=0
    g52: LineSegment StartX=-8.43343 StartY=-8 StartZ=0 EndX=-8.43343 EndY=-10 EndZ=0
    g53: LineSegment StartX=-8.43343 StartY=-10 StartZ=0 EndX=-7.19003 EndY=-10 EndZ=0
  constraints (112):
    c: Horizontal(g0)
    c: Distance(g0) = 2
    c: Block(g0)
    c: Vertical(g1)
    c: Coincident(g2,g0)
    c: Vertical(g2)
    c: Block(g2)
    c: Coincident(g6,g2)
    c: Weight(g3) = 1
    c: Equal(g3,g4)
    c: Equal(g3,g5)
    c: InternalAlignment(g3,g6)
    c: InternalAlignment(g4,g6)
    c: InternalAlignment(g5,g6)
    c: InternalAlignment(g7,g6)
    c: InternalAlignment(g8,g6)
    c: Block(g6)
    c: Coincident(g9,g1)
    c: Coincident(g9,g6)
    c: Horizontal(g9)
    c: Vertical(g10)
    c: Block(g10)
    c: Horizontal(g11)
    c: Block(g11)
    c: Coincident(g12,g10)
    c: Horizontal(g12)
    c: Block(g12)
    c: Coincident(g13,g11)
    c: Vertical(g13)
    c: Block(g13)
    c: Coincident(g14,g10)
    c: Horizontal(g14)
    c: Block(g14)
    c: Block(g9)
    c: Block(g1)
    c: Weight(g15) = 1
    c: Equal(g15,g16)
    c: Equal(g15,g17)
    c: InternalAlignment(g15,g18)
    c: InternalAlignment(g16,g18)
    c: InternalAlignment(g17,g18)
    c: InternalAlignment(g19,g18)
    c: InternalAlignment(g20,g18)
    c: Weight(g21) = 1
    c: Equal(g21,g22)
    c: Equal(g21,g23)
    c: InternalAlignment(g21,g24)
    c: InternalAlignment(g22,g24)
    c: InternalAlignment(g23,g24)
    c: InternalAlignment(g25,g24)
    c: InternalAlignment(g26,g24)
    c: Weight(g27) = 1
    c: Equal(g27,g28)
    c: Equal(g27,g29)
    c: Coincident(g30,g14)
    c: InternalAlignment(g27,g30)
    c: InternalAlignment(g28,g30)
    c: InternalAlignment(g29,g30)
    c: InternalAlignment(g31,g30)
    c: InternalAlignment(g32,g30)
    c: Coincident(g36,g12)
    c: Weight(g33) = 1
    c: Equal(g33,g34)
    c: Equal(g33,g35)
    c: Coincident(g36,g11)
    c: InternalAlignment(g33,g36)
    c: InternalAlignment(g34,g36)
    c: InternalAlignment(g35,g36)
    c: InternalAlignment(g37,g36)
    c: InternalAlignment(g38,g36)
    c: Coincident(g42,g13)
    c: Weight(g39) = 1
    c: Equal(g39,g40)
    c: Equal(g39,g41)
    c: Coincident(g42,g1)
    c: InternalAlignment(g39,g42)
    c: InternalAlignment(g40,g42)
    c: InternalAlignment(g41,g42)
    c: InternalAlignment(g43,g42)
    c: InternalAlignment(g44,g42)
    c: Block(g18)
    c: Block(g24)
    c: Block(g30)
    c: Block(g36)
    c: Block(g42)
    c: Horizontal(g45)
    c: Coincident(g45,g0)
    c: Vertical(g46)
    c: Coincident(g46,g45)
    c: Coincident(g47,g46)
    c: Coincident(g47,g18)
    c: Horizontal(g47)
    c: Block(g46)
    c: Coincident(g48,g18)
    c: Horizontal(g48)
    c: Distance(g48) = 1.33
    c: Vertical(g49)
    c: Coincident(g49,g48)
    c: Coincident(g50,g49)
    c: Coincident(g50,g24)
    c: Horizontal(g50)
    c: Tangent(g50,g22)
    c: Horizontal(g51)
    c: Coincident(g51,g24)
    c: Block(g51)
    c: Vertical(g52)
    c: Block(g52)
    c: Coincident(g52,g51)
    c: Coincident(g53,g52)
    c: Coincident(g53,g30)
    c: Horizontal(g53)
    c: Distance(g1) = 8.5
FEATURE [Part::Feature] Face024
  shape: bbox 9.8 x 26.5 x 2e-07 mm, 1 faces, 0 solids (baked)
FEATURE [Part::Revolution] Revolve024
  Angle = 360
  Axis = (0,1,0)
  Base = (0,0,0)
  FaceMakerClass = Part::FaceMakerBullseye
  Placement = pos=(0,0,0) rot=(0,0,1;1.5708rad)
  Solid = false
  Source = -> Face024
  Symmetric = false
FEATURE [Part::Feature] Face025
  shape: bbox 9.8 x 26.5 x 2e-07 mm, 1 faces, 0 solids (baked)
FEATURE [Part::Revolution] Revolve025
  Angle = 360
  Axis = (0,1,0)
  Base = (0,0,0)
  FaceMakerClass = Part::FaceMakerBullseye
  Placement = pos=(0,0,0) rot=(0,0,1;1.5708rad)
  Solid = false
  Source = -> Face025
  Symmetric = false
FEATURE [Part::MultiFuse] Fusion033
  Placement = pos=(-18,19,36) rot=(0,0,1;0rad)
  Shapes = -> [Revolve025,Revolve024]
FEATURE [Part::Cylinder] Cylinder014
  Angle = 360
  AttacherType = Attacher::AttachEngine3D
  Height = 20
  Placement = pos=(0,0,36.15) rot=(0,0,1;0rad)
  Radius = 14.3
FEATURE [Part::Cylinder] Cylinder015
  Angle = 360
  AttacherType = Attacher::AttachEngine3D
  Height = 10
  Placement = pos=(0,0,36.15) rot=(0,0,1;0rad)
  Radius = 4
FEATURE [Part::MultiFuse] Fusion034  label="removeToCreteHoleForPlugHousing004"
  Placement = pos=(-42,19,36) rot=(0,1,0;1.5708rad)
  Shapes = -> [Cylinder014,Cylinder015]
FEATURE [Part::Cut] Cut008  label="top004"
  Base = -> Cut004
  Placement = pos=(-1,0,0) rot=(0,0,1;0rad)
  Tool = -> Fusion034
FEATURE [Part::Box] Box005  label="Cube005"
  AttacherType = Attacher::AttachEngine3D
  Height = 28
  Length = 3
  Placement = pos=(110.7,19,22) rot=(0,0,1;0rad)
  Width = 15.7
FEATURE [Part::Cylinder] Cylinder016
  Angle = 360
  AttacherType = Attacher::AttachEngine3D
  Height = 10
  Placement = pos=(0,0,36.15) rot=(0,0,1;0rad)
  Radius = 4
FEATURE [Part::Cylinder] Cylinder017
  Angle = 360
  AttacherType = Attacher::AttachEngine3D
  Height = 20
  Placement = pos=(0,0,36.15) rot=(0,0,1;0rad)
  Radius = 10.3
FEATURE [Part::MultiFuse] Fusion035  label="removeToCreteHoleForPlugHousing005"
  Placement = pos=(70,19,36) rot=(0,1,0;1.5708rad)
  Shapes = -> [Cylinder017,Cylinder016]
FEATURE [Part::Cut] Cut009  label="plugHousingTab001"
  Base = -> Box005
  Placement = pos=(-107.4,-14,0) rot=(0,0,1;0rad)
  Tool = -> Fusion035
FEATURE [Part::Box] Box006  label="Cube006"
  AttacherType = Attacher::AttachEngine3D
  Height = 28
  Length = 3
  Placement = pos=(110.7,19,22) rot=(0,0,1;0rad)
  Width = 15.7
FEATURE [Part::Cylinder] Cylinder018
  Angle = 360
  AttacherType = Attacher::AttachEngine3D
  Height = 10
  Placement = pos=(0,0,36.15) rot=(0,0,1;0rad)
  Radius = 4
FEATURE [Part::Cylinder] Cylinder019
  Angle = 360
  AttacherType = Attacher::AttachEngine3D
  Height = 20
  Placement = pos=(0,0,36.15) rot=(0,0,1;0rad)
  Radius = 10.3
FEATURE [Part::MultiFuse] Fusion036  label="removeToCreteHoleForPlugHousing006"
  Placement = pos=(70,19,36) rot=(0,1,0;1.5708rad)
  Shapes = -> [Cylinder019,Cylinder018]
FEATURE [Part::Cut] Cut010  label="plugHousingTab002"
  Base = -> Box006
  Placement = pos=(-107.4,-14,0) rot=(0,0,1;0rad)
  Tool = -> Fusion036
FEATURE [Part::MultiFuse] Fusion037
  Placement = pos=(9.6,23,0) rot=(0,0,1;3.14159rad)
  Shapes = -> [Cut009,Cut010]
FEATURE [Part::Box] Box  label="Cube"
  AttacherType = Attacher::AttachEngine3D
  Height = 10
  Length = 3
  Placement = pos=(3.3,4,12) rot=(0,0,1;0rad)
  Width = 10
FEATURE [Part::Fillet] Fillet004
  Base = -> Fusion028
  Edges = 1 edges r=2: [Edge25]
FEATURE [Part::Fillet] Fillet005  label="plugHousing046"
  Base = -> Fillet004
  Edges = 1 edges r=2: [Edge8]
FEATURE [Part::Fillet] Fillet006
  Base = -> Box
  Edges = 1 edges r=2: [Edge11]
FEATURE [Part::Box] Box007  label="Cube007"
  AttacherType = Attacher::AttachEngine3D
  Height = 10
  Length = 3
  Placement = pos=(3.3,4,50) rot=(0,0,1;0rad)
  Width = 10
FEATURE [Part::Fillet] Fillet007
  Base = -> Box007
  Edges = 1 edges r=2: [Edge12]
FEATURE [Part::Box] Box008  label="Cube008"
  AttacherType = Attacher::AttachEngine3D
  Height = 28
  Length = 4
  Placement = pos=(5,0,22) rot=(0,0,1;0rad)
  Width = 10
FEATURE [Part::Fillet] Fillet008
  Base = -> Box008
  Edges = 1 edges r=1: [Edge7]
FEATURE [Part::Fillet] Fillet009
  Base = -> Fillet008
  Edges = 1 edges r=2: [Edge5]
FEATURE [Part::Fillet] Fillet010
  Base = -> Fillet009
  Edges = 1 edges r=2: [Edge2]
FEATURE [Sketcher::SketchObject] Sketch009  label="topSketch003"
  FullyConstrained = true
  sketch-geometry (4):
    g0: LineSegment StartX=16.8446 StartY=31.512 StartZ=0 EndX=16.3251 EndY=34.4666 EndZ=0
    g1: ArcOfCircle CenterX=19 CenterY=19.2524 CenterZ=0 NormalX=0 NormalY=0 NormalZ=1 AngleXU=0 Radius=15.4476 StartAngle=1.74483 EndAngle=2.72717
    g2: ArcOfCircle CenterX=19 CenterY=19.2524 CenterZ=0 NormalX=0 NormalY=0 NormalZ=1 AngleXU=0 Radius=12.4476 StartAngle=1.74483 EndAngle=2.73189
    g3: LineSegment StartX=4.86004 StartY=25.4725 StartZ=0 EndX=7.58253 EndY=24.2107 EndZ=0
  constraints (7):
    c: Block(g0)
    c: Coincident(g1,g0)
    c: Coincident(g2,g0)
    c: Coincident(g3,g1)
    c: Coincident(g3,g2)
    c: Block(g1)
    c: Block(g2)
FEATURE [Part::Extrusion] Extrude008
  Base = -> Sketch009
  Dir = (0,0,1)
  DirMode = 2
  FaceMakerClass = Part::FaceMakerBullseye
  LengthFwd = 10
  LengthRev = 0
  Placement = pos=(0,0,31) rot=(0,0,1;0rad)
  Solid = true
  Symmetric = false
FEATURE [Part::Cylinder] Cylinder020
  Angle = 360
  AttacherType = Attacher::AttachEngine3D
  Height = 20
  Placement = pos=(0,0,36.15) rot=(0,0,1;0rad)
  Radius = 8.2
FEATURE [Part::Cylinder] Cylinder021
  Angle = 360
  AttacherType = Attacher::AttachEngine3D
  Height = 10
  Placement = pos=(0,0,36.15) rot=(0,0,1;0rad)
  Radius = 4
FEATURE [Part::MultiFuse] Fusion038  label="removeToCreteHoleForPlugHousing007"
  Placement = pos=(-42,19,36) rot=(0,1,0;1.5708rad)
  Shapes = -> [Cylinder020,Cylinder021]
FEATURE [Part::Cut] Cut011
  Base = -> Extrude008
  Tool = -> Fusion038
FEATURE [Part::Fillet] Fillet011
  Base = -> Cut011
  Edges = 1 edges r=2: [Edge1]
FEATURE [Part::Fillet] Fillet012
  Base = -> Fillet011
  Edges = 1 edges r=2.5: [Edge1]
FEATURE [Part::Fillet] Fillet013
  Base = -> Fillet012
  Edges = 1 edges r=2.5: [Edge2]
FEATURE [Part::Box] Box010  label="Cube010"
  AttacherType = Attacher::AttachEngine3D
  Height = 16
  Length = 8
  Placement = pos=(12.7,31.52,28) rot=(0,0,1;0rad)
  Width = 4
FEATURE [Sketcher::SketchObject] Sketch010  label="topSketch004"
  FullyConstrained = true
  sketch-geometry (4):
    g0: LineSegment StartX=16.8446 StartY=31.512 StartZ=0 EndX=16.3251 EndY=34.4666 EndZ=0
    g1: ArcOfCircle CenterX=19 CenterY=19.2524 CenterZ=0 NormalX=0 NormalY=0 NormalZ=1 AngleXU=0 Radius=15.4476 StartAngle=1.74483 EndAngle=2.72717
    g2: ArcOfCircle CenterX=19 CenterY=19.2524 CenterZ=0 NormalX=0 NormalY=0 NormalZ=1 AngleXU=0 Radius=12.4476 StartAngle=1.74483 EndAngle=2.73189
    g3: LineSegment StartX=4.86004 StartY=25.4725 StartZ=0 EndX=7.58253 EndY=24.2107 EndZ=0
  constraints (7):
    c: Block(g0)
    c: Coincident(g1,g0)
    c: Coincident(g2,g0)
    c: Coincident(g3,g1)
    c: Coincident(g3,g2)
    c: Block(g1)
    c: Block(g2)
FEATURE [Part::Cylinder] Cylinder022
  Angle = 360
  AttacherType = Attacher::AttachEngine3D
  Height = 10
  Placement = pos=(0,0,36.15) rot=(0,0,1;0rad)
  Radius = 4
FEATURE [Sketcher::SketchObject] Sketch011  label="topSketch005"
  FullyConstrained = true
  sketch-geometry (4):
    g0: LineSegment StartX=16.8446 StartY=31.512 StartZ=0 EndX=16.3251 EndY=34.4666 EndZ=0
    g1: ArcOfCircle CenterX=19 CenterY=19.2524 CenterZ=0 NormalX=0 NormalY=0 NormalZ=1 AngleXU=0 Radius=15.4476 StartAngle=1.74483 EndAngle=2.72717
    g2: ArcOfCircle CenterX=19 CenterY=19.2524 CenterZ=0 NormalX=0 NormalY=0 NormalZ=1 AngleXU=0 Radius=12.4476 StartAngle=1.74483 EndAngle=2.73189
    g3: LineSegment StartX=4.86004 StartY=25.4725 StartZ=0 EndX=7.58253 EndY=24.2107 EndZ=0
  constraints (7):
    c: Block(g0)
    c: Coincident(g1,g0)
    c: Coincident(g2,g0)
    c: Coincident(g3,g1)
    c: Coincident(g3,g2)
    c: Block(g1)
    c: Block(g2)
FEATURE [Part::Extrusion] Extrude010
  Base = -> Sketch011
  Dir = (0,0,1)
  DirMode = 2
  FaceMakerClass = Part::FaceMakerBullseye
  LengthFwd = 10.6
  LengthRev = 0
  Placement = pos=(0,0,31) rot=(0,0,1;0rad)
  Solid = true
  Symmetric = false
FEATURE [Part::Cylinder] Cylinder023
  Angle = 360
  AttacherType = Attacher::AttachEngine3D
  Height = 20
  Placement = pos=(0,0,36.15) rot=(0,0,1;0rad)
  Radius = 8.2
FEATURE [Part::MultiFuse] Fusion039  label="removeToCreteHoleForPlugHousing008"
  Placement = pos=(-42,19,36) rot=(0,1,0;1.5708rad)
  Shapes = -> [Cylinder023,Cylinder022]
FEATURE [Part::Cut] Cut012
  Base = -> Extrude010
  Placement = pos=(0,0,-0.3) rot=(0,0,1;0rad)
  Tool = -> Fusion039
FEATURE [Part::Cut] Cut013
  Base = -> Box010
  Tool = -> Cut012
FEATURE [Part::Fillet] Fillet014
  Base = -> Cut013
  Edges = 1 edges r=0.7: [Edge13]
FEATURE [Part::Fillet] Fillet015
  Base = -> Fillet014
  Edges = 1 edges r=0.7: [Edge13]
FEATURE [Part::Fillet] Fillet016
  Base = -> Fillet015
  Edges = 1 edges r=0.7: [Edge16]
FEATURE [Part::Fillet] Fillet017
  Base = -> Fillet016
  Edges = 1 edges r=0.7: [Edge11]
FEATURE [Part::Fillet] Fillet018
  Base = -> Fillet017
  Edges = 1 edges r=0.7: [Edge10]
FEATURE [Part::Fillet] Fillet019
  Base = -> Fillet018
  Edges = 1 edges r=1.2: [Edge5]
FEATURE [Part::Fillet] Fillet020
  Base = -> Fillet019
  Edges = 1 edges r=1.2: [Edge12]
FEATURE [Part::Fillet] Fillet021
  Base = -> Fillet020
  Edges = 1 edges r=2: [Edge1]
  Placement = pos=(0.3,0,0) rot=(0,0,1;0rad)
FEATURE [Part::MultiFuse] Fusion040  label="top005"
  Shapes = -> [Cut008,Fillet021]
FEATURE [Part::MultiFuse] Fusion041  label="wireHolder"
  Shapes = -> [Fusion033,Fillet013]
FEATURE [Part::MultiFuse] Fusion042
  Shapes = -> [Fillet007,Fusion041]
FEATURE [Part::MultiFuse] Fusion043  label="wireHolder001"
  Shapes = -> [Fusion042,Fillet010]
FEATURE [Part::MultiFuse] Fusion044  label="wireHolder002"
  Shapes = -> [Fillet006,Fusion037,Fusion043]
FEATURE [Part::Feature] Face026
  shape: bbox 11 x 6 x 2e-07 mm, 1 faces, 0 solids (baked)
FEATURE [Part::Revolution] Revolve026
  Angle = 360
  Axis = (0,1,0)
  Base = (0,0,0)
  FaceMakerClass = Part::FaceMakerBullseye
  Placement = pos=(30.3,-1,19.7) rot=(0,0,1;0rad)
  Solid = false
  Source = -> Face026
  Symmetric = false
FEATURE [Sketcher::SketchObject] Sketch013  label="topSketch006"
  FullyConstrained = true
  sketch-geometry (13):
    g0: LineSegment StartX=117 StartY=19 StartZ=0 EndX=117 EndY=38 EndZ=0
    g1: ArcOfCircle CenterX=98 CenterY=19 CenterZ=0 NormalX=0 NormalY=0 NormalZ=1 AngleXU=0 Radius=19 StartAngle=5.7297 EndAngle=6.28319
    g2: LineSegment StartX=0 StartY=3 StartZ=0 EndX=0 EndY=19 EndZ=0
    g3: LineSegment StartX=19 StartY=38 StartZ=0 EndX=117 EndY=38 EndZ=0
    g4: ArcOfCircle CenterX=19 CenterY=19 CenterZ=0 NormalX=0 NormalY=0 NormalZ=1 AngleXU=0 Radius=19 StartAngle=1.5708 EndAngle=3.14159
    g5: ArcOfCircle CenterX=19 CenterY=19 CenterZ=0 NormalX=0 NormalY=0 NormalZ=1 AngleXU=0 Radius=16 StartAngle=1.5708 EndAngle=3.14159
    g6: ArcOfCircle CenterX=98 CenterY=19 CenterZ=0 NormalX=0 NormalY=0 NormalZ=1 AngleXU=0 Radius=16 StartAngle=5.60905 EndAngle=6.28319
    g7: LineSegment StartX=114 StartY=19 StartZ=0 EndX=114 EndY=35 EndZ=0
    g8: LineSegment StartX=110.5 StartY=9.01251 StartZ=0 EndX=114.163 EndY=9.01251 EndZ=0
    g9: LineSegment StartX=114 StartY=35 StartZ=0 EndX=19 EndY=35 EndZ=0
    g10: LineSegment StartX=0 StartY=3 StartZ=0 EndX=0 EndY=0 EndZ=0
    g11: LineSegment StartX=3 StartY=0 StartZ=0 EndX=0 EndY=0 EndZ=0
    g12: LineSegment StartX=3 StartY=19 StartZ=0 EndX=3 EndY=0 EndZ=0
  constraints (33):
    c: Vertical(g0)
    c: Distance(g0) = 19
    c: Block(g0)
    c: Coincident(g1,g0)
    c: Block(g1)
    c: Vertical(g2)
    c: Block(g2)
    c: Coincident(g3,g0)
    c: Horizontal(g3)
    c: Distance(g3) = 98
    c: Coincident(g4,g3)
    c: Coincident(g4,g2)
    c: Block(g4)
    c: Coincident(g5,g4)
    c: Coincident(g6,g1)
    c: Block(g6)
    c: Block(g5)
    c: Coincident(g7,g6)
    c: Vertical(g7)
    c: Coincident(g8,g6)
    c: Coincident(g8,g1)
    c: Coincident(g9,g7)
    c: Coincident(g9,g5)
    c: Horizontal(g9)
    c: Tangent(g9,g5)
    c: Coincident(g10,g2)
    c: Distance(g10) = 3
    c: Vertical(g10)
    c: Coincident(g11,g10)
    c: Horizontal(g11)
    c: Coincident(g12,g5)
    c: Coincident(g12,g11)
    c: Vertical(g12)
FEATURE [Part::Extrusion] Extrude011  label="top006"
  Base = -> Sketch013
  Dir = (0,0,1)
  DirMode = 2
  FaceMakerClass = Part::FaceMakerBullseye
  LengthFwd = 72
  LengthRev = 0
  Solid = true
  Symmetric = false
FEATURE [Sketcher::SketchObject] Sketch014
  FullyConstrained = true
  MapMode = 3
  Placement = pos=(0,0,0) rot=(1,0,0;1.5708rad)
  Support = -> [Extrude011]
  sketch-geometry (8):
    g0: Circle CenterX=80.351 CenterY=-67.6202 CenterZ=0 NormalX=0 NormalY=0 NormalZ=1 AngleXU=0 Radius=2
    g1: Circle CenterX=80.351 CenterY=-67.6202 CenterZ=0 NormalX=0 NormalY=0 NormalZ=1 AngleXU=0 Radius=3
    g2: Circle CenterX=80.351 CenterY=-4.92017 CenterZ=0 NormalX=0 NormalY=0 NormalZ=1 AngleXU=0 Radius=2
    g3: Circle CenterX=80.351 CenterY=-4.92017 CenterZ=0 NormalX=0 NormalY=0 NormalZ=1 AngleXU=0 Radius=3
    g4: Circle CenterX=23.851 CenterY=-4.92017 CenterZ=0 NormalX=0 NormalY=0 NormalZ=1 AngleXU=0 Radius=2
    g5: Circle CenterX=23.851 CenterY=-4.92017 CenterZ=0 NormalX=0 NormalY=0 NormalZ=1 AngleXU=0 Radius=3
    g6: Circle CenterX=23.851 CenterY=-67.6202 CenterZ=0 NormalX=0 NormalY=0 NormalZ=1 AngleXU=0 Radius=2
    g7: Circle CenterX=23.851 CenterY=-67.6202 CenterZ=0 NormalX=0 NormalY=0 NormalZ=1 AngleXU=0 Radius=3
  constraints (8):
    c: Block(g3)
    c: Block(g2)
    c: Block(g1)
    c: Block(g0)
    c: Block(g6)
    c: Block(g7)
    c: Block(g4)
    c: Block(g5)
FEATURE [Part::Feature] Face027
  shape: bbox 11 x 6 x 2e-07 mm, 1 faces, 0 solids (baked)
FEATURE [Part::Revolution] Revolve027
  Angle = 360
  Axis = (0,1,0)
  Base = (0,0,0)
  FaceMakerClass = Part::FaceMakerBullseye
  Placement = pos=(30.3,-1,51.7) rot=(0,0,1;0rad)
  Solid = false
  Source = -> Face027
  Symmetric = false
FEATURE [Part::Feature] Face028
  shape: bbox 11 x 6 x 2e-07 mm, 1 faces, 0 solids (baked)
FEATURE [Part::Revolution] Revolve028
  Angle = 360
  Axis = (0,1,0)
  Base = (0,0,0)
  FaceMakerClass = Part::FaceMakerBullseye
  Placement = pos=(62.3,-1,19.7) rot=(0,0,1;0rad)
  Solid = false
  Source = -> Face028
  Symmetric = false
FEATURE [Part::Feature] Face029
  shape: bbox 11 x 6 x 2e-07 mm, 1 faces, 0 solids (baked)
FEATURE [Part::Revolution] Revolve029
  Angle = 360
  Axis = (0,1,0)
  Base = (0,0,0)
  FaceMakerClass = Part::FaceMakerBullseye
  Placement = pos=(62.3,-1,51.7) rot=(0,0,1;0rad)
  Solid = false
  Source = -> Face029
  Symmetric = false
FEATURE [Part::Feature] Wire
  shape: bbox 11 x 5.2 x 2e-07 mm, 0 faces, 0 solids (baked)
FEATURE [Part::Revolution] Revolve030
  Angle = 360
  Axis = (0,1,0)
  Base = (0,0,0)
  FaceMakerClass = Part::FaceMakerBullseye
  Placement = pos=(30.3,38,19.7) rot=(0,0,1;0rad)
  Solid = true
  Source = -> Wire
  Symmetric = false
FEATURE [Part::Feature] Wire001
  shape: bbox 11 x 5.2 x 2e-07 mm, 0 faces, 0 solids (baked)
FEATURE [Part::Revolution] Revolve031
  Angle = 360
  Axis = (0,1,0)
  Base = (0,0,0)
  FaceMakerClass = Part::FaceMakerBullseye
  Placement = pos=(30.3,38,51.7) rot=(0,0,1;0rad)
  Solid = true
  Source = -> Wire001
  Symmetric = false
FEATURE [Part::Feature] Wire002
  shape: bbox 11 x 5.2 x 2e-07 mm, 0 faces, 0 solids (baked)
FEATURE [Part::Revolution] Revolve032
  Angle = 360
  Axis = (0,1,0)
  Base = (0,0,0)
  FaceMakerClass = Part::FaceMakerBullseye
  Placement = pos=(62.3,38,51.7) rot=(0,0,1;0rad)
  Solid = true
  Source = -> Wire002
  Symmetric = false
FEATURE [Part::Feature] Wire003
  shape: bbox 11 x 5.2 x 2e-07 mm, 0 faces, 0 solids (baked)
FEATURE [Part::Revolution] Revolve033
  Angle = 360
  Axis = (0,1,0)
  Base = (0,0,0)
  FaceMakerClass = Part::FaceMakerBullseye
  Placement = pos=(62.3,38,19.7) rot=(0,0,1;0rad)
  Solid = true
  Source = -> Wire003
  Symmetric = false
FEATURE [Part::MultiFuse] Fusion045  label="altRandScrewHousing"
  Shapes = -> [Revolve029,Revolve027,Revolve028,Revolve026]
FEATURE [Part::MultiFuse] Fusion046  label="fanScrewHousing"
  Shapes = -> [Revolve033,Revolve032,Revolve031,Revolve030]
FEATURE [Sketcher::SketchObject] Sketch015
  FullyConstrained = true
  sketch-geometry (17):
    g0: Circle CenterX=-3.5 CenterY=23.5 CenterZ=0 NormalX=0 NormalY=0 NormalZ=1 AngleXU=0 Radius=1
    g1: Circle CenterX=-1 CenterY=15.25 CenterZ=0 NormalX=0 NormalY=0 NormalZ=1 AngleXU=0 Radius=1
    g2: Circle CenterX=-3.5 CenterY=7 CenterZ=0 NormalX=0 NormalY=0 NormalZ=1 AngleXU=0 Radius=1
    g3: BSplineCurve PolesCount=3 KnotsCount=2 Degree=2 IsPeriodic=0
    g4: GeomPoint X=-3.5 Y=23.5 Z=0
    g5: GeomPoint X=-3.5 Y=7 Z=0
    g6: Circle CenterX=-4.8 CenterY=30.5 CenterZ=0 NormalX=0 NormalY=0 NormalZ=1 AngleXU=0 Radius=1
    g7: Circle CenterX=-3.5 CenterY=30.5 CenterZ=0 NormalX=0 NormalY=0 NormalZ=1 AngleXU=0 Radius=1
    g8: Circle CenterX=-3.5 CenterY=29.2 CenterZ=0 NormalX=0 NormalY=0 NormalZ=1 AngleXU=0 Radius=1
    g9: BSplineCurve PolesCount=3 KnotsCount=2 Degree=2 IsPeriodic=0
    g10: GeomPoint X=-4.8 Y=30.5 Z=0
    g11: GeomPoint X=-3.5 Y=29.2 Z=0
    g12: LineSegment StartX=-3.5 StartY=29.2 StartZ=0 EndX=-3.5 EndY=23.5 EndZ=0
    g13: LineSegment StartX=-4.8 StartY=30.5 StartZ=0 EndX=0 EndY=30.5 EndZ=0
    g14: LineSegment StartX=-3.5 StartY=0.3 StartZ=0 EndX=0 EndY=0.3 EndZ=0
    g15: LineSegment StartX=-3.5 StartY=0.3 StartZ=0 EndX=-3.5 EndY=7 EndZ=0
    g16: LineSegment StartX=0 StartY=0.3 StartZ=0 EndX=0 EndY=30.5 EndZ=0
  constraints (33):
    c: Weight(g0) = 1
    c: Equal(g0,g1)
    c: Equal(g0,g2)
    c: InternalAlignment(g0,g3)
    c: InternalAlignment(g1,g3)
    c: InternalAlignment(g2,g3)
    c: InternalAlignment(g4,g3)
    c: InternalAlignment(g5,g3)
    c: Block(g3)
    c: Weight(g6) = 1
    c: Equal(g6,g7)
    c: Equal(g6,g8)
    c: InternalAlignment(g6,g9)
    c: InternalAlignment(g7,g9)
    c: InternalAlignment(g8,g9)
    c: InternalAlignment(g10,g9)
    c: InternalAlignment(g11,g9)
    c: Block(g9)
    c: Coincident(g12,g9)
    c: Coincident(g12,g3)
    c: Vertical(g12)
    c: Coincident(g13,g9)
    c: Horizontal(g13)
    c: Distance(g13) = 4.8
    c: Horizontal(g14)
    c: Block(g14)
    c: Coincident(g15,g14)
    c: Coincident(g15,g3)
    c: Vertical(g15)
    c: Coincident(g16,g14)
    c: Coincident(g16,g13)
    c: Vertical(g16)
    c: Tangent(g16,g1)
FEATURE [Sketcher::SketchObject] Sketch016
  FullyConstrained = true
  sketch-geometry (16):
    g0: Circle CenterX=-3.5 CenterY=23.5 CenterZ=0 NormalX=0 NormalY=0 NormalZ=1 AngleXU=0 Radius=1
    g1: Circle CenterX=-1 CenterY=15.25 CenterZ=0 NormalX=0 NormalY=0 NormalZ=1 AngleXU=0 Radius=1
    g2: Circle CenterX=-3.5 CenterY=7 CenterZ=0 NormalX=0 NormalY=0 NormalZ=1 AngleXU=0 Radius=1
    g3: BSplineCurve PolesCount=3 KnotsCount=2 Degree=2 IsPeriodic=0
    g4: GeomPoint X=-3.5 Y=23.5 Z=0
    g5: GeomPoint X=-3.5 Y=7 Z=0
    g6: LineSegment StartX=-3.5 StartY=28.2 StartZ=0 EndX=-3.5 EndY=23.5 EndZ=0
    g7: LineSegment StartX=0 StartY=29.5 StartZ=0 EndX=0 EndY=30 EndZ=0
    g8: LineSegment StartX=-3.5 StartY=28.2 StartZ=0 EndX=-3.5 EndY=30 EndZ=0
    g9: LineSegment StartX=0 StartY=30 StartZ=0 EndX=0 EndY=30.5 EndZ=0
    g10: LineSegment StartX=0 StartY=30.5 StartZ=0 EndX=-3.5 EndY=30.5 EndZ=0
    g11: LineSegment StartX=-3.5 StartY=30.5 StartZ=0 EndX=-3.5 EndY=30 EndZ=0
    g12: LineSegment StartX=0 StartY=29.5 StartZ=0 EndX=0 EndY=5 EndZ=0
    g13: LineSegment StartX=-3.5 StartY=0.3 StartZ=0 EndX=-3.5 EndY=7 EndZ=0
    g14: LineSegment StartX=-3.5 StartY=0.3 StartZ=0 EndX=0 EndY=0.3 EndZ=0
    g15: LineSegment StartX=0 StartY=5 StartZ=0 EndX=0 EndY=0.3 EndZ=0
  constraints (39):
    c: Weight(g0) = 1
    c: Equal(g0,g1)
    c: Equal(g0,g2)
    c: InternalAlignment(g0,g3)
    c: InternalAlignment(g1,g3)
    c: InternalAlignment(g2,g3)
    c: InternalAlignment(g4,g3)
    c: InternalAlignment(g5,g3)
    c: Block(g3)
    c: Coincident(g6,g3)
    c: Vertical(g6)
    c: Vertical(g7)
    c: Distance(g7) = 0.5
    c: Coincident(g8,g6)
    c: Vertical(g8)
    c: Block(g6)
    c: Block(g7)
    c: Vertical(g9)
    c: Equal(g7,g9) = 0.5
    c: Block(g9)
    c: Coincident(g9,g7)
    c: Horizontal(g10)
    c: Coincident(g10,g9)
    c: Coincident(g11,g10)
    c: Coincident(g11,g8)
    c: Vertical(g11)
    c: Block(g11)
    c: Coincident(g12,g7)
    c: Vertical(g12)
    c: Coincident(g13,g3)
    c: Vertical(g13)
    c: Distance(g13) = 6.7
    c: Coincident(g14,g13)
    c: Horizontal(g14)
    c: Block(g14)
    c: Coincident(g15,g12)
    c: Coincident(g15,g14)
    c: Vertical(g15)
    c: Block(g15)
FEATURE [Sketcher::SketchObject] Sketch017
  FullyConstrained = true
  sketch-geometry (11):
    g0: LineSegment StartX=-3.5 StartY=1e-16 StartZ=0 EndX=-1.6 EndY=1e-16 EndZ=0
    g1: LineSegment StartX=-1.6 StartY=1e-16 StartZ=0 EndX=-1.6 EndY=1.5 EndZ=0
    g2: LineSegment StartX=-3.5 StartY=1.5 StartZ=0 EndX=-1.6 EndY=1.5 EndZ=0
    g3: LineSegment StartX=-3.5 StartY=1e-16 StartZ=0 EndX=-4.8 EndY=1e-16 EndZ=0
    g4: Circle CenterX=-3.5 CenterY=1.3 CenterZ=0 NormalX=0 NormalY=0 NormalZ=1 AngleXU=0 Radius=1
    g5: Circle CenterX=-3.5 CenterY=1e-16 CenterZ=0 NormalX=0 NormalY=0 NormalZ=1 AngleXU=0 Radius=1
    g6: Circle CenterX=-4.8 CenterY=1e-16 CenterZ=0 NormalX=0 NormalY=0 NormalZ=1 AngleXU=0 Radius=1
    g7: BSplineCurve PolesCount=3 KnotsCount=2 Degree=2 IsPeriodic=0
    g8: GeomPoint X=-3.5 Y=1.3 Z=0
    g9: GeomPoint X=-4.8 Y=1e-16 Z=0
    g10: LineSegment StartX=-3.5 StartY=1.3 StartZ=0 EndX=-3.5 EndY=1.5 EndZ=0
  constraints (24):
    c: Horizontal(g0)
    c: Distance(g0) = 1.9
    c: Block(g0)
    c: Coincident(g1,g0)
    c: Vertical(g1)
    c: Coincident(g2,g1)
    c: Horizontal(g2)
    c: Coincident(g3,g0)
    c: Horizontal(g3)
    c: Distance(g3) = 1.3
    c: Weight(g4) = 1
    c: Equal(g4,g5)
    c: Coincident(g5,g0)
    c: Equal(g4,g6)
    c: Coincident(g7,g3)
    c: InternalAlignment(g4,g7)
    c: InternalAlignment(g5,g7)
    c: InternalAlignment(g6,g7)
    c: InternalAlignment(g8,g7)
    c: InternalAlignment(g9,g7)
    c: Coincident(g10,g7)
    c: Coincident(g10,g2)
    c: Vertical(g10)
    c: Block(g10)
FEATURE [Part::Feature] Face035
  shape: bbox 3.2 x 1.5 x 2e-07 mm, 1 faces, 0 solids (baked)
FEATURE [Part::Revolution] Revolve039  label="backCaseScrewRetainer"
  Angle = 360
  Axis = (0,1,0)
  Base = (0,0,0)
  FaceMakerClass = Part::FaceMakerBullseye
  Placement = pos=(12.5,3,62) rot=(0,0,1;0rad)
  Solid = false
  Source = -> Face035
  Symmetric = false
FEATURE [Part::Feature] Face036
  shape: bbox 3.2 x 1.5 x 2e-07 mm, 1 faces, 0 solids (baked)
FEATURE [Part::Feature] Face039
  shape: bbox 4.8 x 30.2 x 2e-07 mm, 1 faces, 0 solids (baked)
FEATURE [Part::Revolution] Revolve043  label="frontCaseScrewPost002"
  Angle = 360
  Axis = (0,1,0)
  Base = (0,0,0)
  FaceMakerClass = Part::FaceMakerBullseye
  Placement = pos=(89.5,4.5,3.5) rot=(0,0,1;0rad)
  Solid = false
  Source = -> Face039
  Symmetric = false
FEATURE [Part::Feature] Face042
  shape: bbox 4.8 x 30.2 x 2e-07 mm, 1 faces, 0 solids (baked)
FEATURE [Part::Revolution] Revolve046  label="frontCaseScrewPost003"
  Angle = 360
  Axis = (0,1,0)
  Base = (0,0,0)
  FaceMakerClass = Part::FaceMakerBullseye
  Placement = pos=(89.5,4.5,68.5) rot=(0,0,1;0rad)
  Solid = false
  Source = -> Face042
  Symmetric = false
FEATURE [Part::Feature] Face043
  shape: bbox 3.2 x 1.5 x 2e-07 mm, 1 faces, 0 solids (baked)
FEATURE [Part::Revolution] Revolve047  label="frontCaseScrewRetainer002"
  Angle = 360
  Axis = (0,1,0)
  Base = (0,0,0)
  FaceMakerClass = Part::FaceMakerBullseye
  Placement = pos=(89.5,3,68.5) rot=(0,0,1;0rad)
  Solid = false
  Source = -> Face043
  Symmetric = false
FEATURE [Part::Feature] Face044
  shape: bbox 3.2 x 1.5 x 2e-07 mm, 1 faces, 0 solids (baked)
FEATURE [Part::Revolution] Revolve048  label="frontCaseScrewRetainer003"
  Angle = 360
  Axis = (0,1,0)
  Base = (0,0,0)
  FaceMakerClass = Part::FaceMakerBullseye
  Placement = pos=(89.5,3,3.5) rot=(0,0,1;0rad)
  Solid = false
  Source = -> Face044
  Symmetric = false
FEATURE [App::MeasureDistance] Distance002  label="Distance: 1.67 mm"
  Distance = 1.66921
  P1 = (99.2361,4.7524,71.7)
  P2 = (99.2347,6.42161,71.7)
FEATURE [Sketcher::SketchObject] Sketch018
  FullyConstrained = true
  sketch-geometry (7):
    g0: LineSegment StartX=0 StartY=0 StartZ=0 EndX=0 EndY=6 EndZ=0
    g1: Circle CenterX=0 CenterY=0 CenterZ=0 NormalX=0 NormalY=0 NormalZ=1 AngleXU=0 Radius=1
    g2: Circle CenterX=8 CenterY=6 CenterZ=0 NormalX=0 NormalY=0 NormalZ=1 AngleXU=0 Radius=1
    g3: BSplineCurve PolesCount=3 KnotsCount=2 Degree=2 IsPeriodic=0
    g4: GeomPoint X=0 Y=0 Z=0
    g5: GeomPoint X=8 Y=6 Z=0
    g6: LineSegment StartX=0 StartY=6 StartZ=0 EndX=8 EndY=6 EndZ=0
  constraints (14):
    c: Coincident(g0,g-1)
    c: Distance(g0) = 6
    c: Vertical(g0)
    c: Coincident(g3,g0)
    c: Weight(g1) = 1
    c: Equal(g1,g2)
    c: InternalAlignment(g1,g3)
    c: InternalAlignment(g2,g3)
    c: InternalAlignment(g4,g3)
    c: InternalAlignment(g5,g3)
    c: Block(g3)
    c: Coincident(g6,g0)
    c: Coincident(g6,g3)
    c: Horizontal(g6)
FEATURE [Part::Extrusion] Extrude012  label="caseScrewPillarBracket"
  Base = -> Sketch018
  Dir = (0,0,1)
  DirMode = 2
  FaceMakerClass = Part::FaceMakerBullseye
  LengthFwd = 2.4
  LengthRev = 0
  Placement = pos=(15.76,29,8.8) rot=(0,1,0;0rad)
  Solid = true
  Symmetric = false
FEATURE [Sketcher::SketchObject] Sketch019
  FullyConstrained = true
  sketch-geometry (7):
    g0: LineSegment StartX=0 StartY=0 StartZ=0 EndX=0 EndY=6 EndZ=0
    g1: Circle CenterX=0 CenterY=0 CenterZ=0 NormalX=0 NormalY=0 NormalZ=1 AngleXU=0 Radius=1
    g2: Circle CenterX=8 CenterY=6 CenterZ=0 NormalX=0 NormalY=0 NormalZ=1 AngleXU=0 Radius=1
    g3: BSplineCurve PolesCount=3 KnotsCount=2 Degree=2 IsPeriodic=0
    g4: GeomPoint X=0 Y=0 Z=0
    g5: GeomPoint X=8 Y=6 Z=0
    g6: LineSegment StartX=0 StartY=6 StartZ=0 EndX=8 EndY=6 EndZ=0
  constraints (14):
    c: Coincident(g0,g-1)
    c: Distance(g0) = 6
    c: Vertical(g0)
    c: Coincident(g3,g0)
    c: Weight(g1) = 1
    c: Equal(g1,g2)
    c: InternalAlignment(g1,g3)
    c: InternalAlignment(g2,g3)
    c: InternalAlignment(g4,g3)
    c: InternalAlignment(g5,g3)
    c: Block(g3)
    c: Coincident(g6,g0)
    c: Coincident(g6,g3)
    c: Horizontal(g6)
FEATURE [Part::Extrusion] Extrude013  label="caseScrewPillarBracket001"
  Base = -> Sketch019
  Dir = (0,0,1)
  DirMode = 2
  FaceMakerClass = Part::FaceMakerBullseye
  LengthFwd = 2.4
  LengthRev = 0
  Placement = pos=(15.76,29,60.8) rot=(0,0,1;0rad)
  Solid = true
  Symmetric = false
FEATURE [Sketcher::SketchObject] Sketch020
  FullyConstrained = true
  sketch-geometry (7):
    g0: LineSegment StartX=0 StartY=0 StartZ=0 EndX=0 EndY=6 EndZ=0
    g1: Circle CenterX=0 CenterY=0 CenterZ=0 NormalX=0 NormalY=0 NormalZ=1 AngleXU=0 Radius=1
    g2: Circle CenterX=8 CenterY=6 CenterZ=0 NormalX=0 NormalY=0 NormalZ=1 AngleXU=0 Radius=1
    g3: BSplineCurve PolesCount=3 KnotsCount=2 Degree=2 IsPeriodic=0
    g4: GeomPoint X=0 Y=0 Z=0
    g5: GeomPoint X=8 Y=6 Z=0
    g6: LineSegment StartX=0 StartY=6 StartZ=0 EndX=8 EndY=6 EndZ=0
  constraints (14):
    c: Coincident(g0,g-1)
    c: Distance(g0) = 6
    c: Vertical(g0)
    c: Coincident(g3,g0)
    c: Weight(g1) = 1
    c: Equal(g1,g2)
    c: InternalAlignment(g1,g3)
    c: InternalAlignment(g2,g3)
    c: InternalAlignment(g4,g3)
    c: InternalAlignment(g5,g3)
    c: Block(g3)
    c: Coincident(g6,g0)
    c: Coincident(g6,g3)
    c: Horizontal(g6)
FEATURE [Part::Extrusion] Extrude014  label="caseScrewPillarBracket002"
  Base = -> Sketch020
  Dir = (0,0,1)
  DirMode = 2
  FaceMakerClass = Part::FaceMakerBullseye
  LengthFwd = 2.4
  LengthRev = 0
  Placement = pos=(13.7,29,13.26) rot=(0,-1,0;1.5708rad)
  Solid = true
  Symmetric = false
FEATURE [Sketcher::SketchObject] Sketch021
  FullyConstrained = true
  sketch-geometry (7):
    g0: LineSegment StartX=0 StartY=0 StartZ=0 EndX=0 EndY=6 EndZ=0
    g1: Circle CenterX=0 CenterY=0 CenterZ=0 NormalX=0 NormalY=0 NormalZ=1 AngleXU=0 Radius=1
    g2: Circle CenterX=8 CenterY=6 CenterZ=0 NormalX=0 NormalY=0 NormalZ=1 AngleXU=0 Radius=1
    g3: BSplineCurve PolesCount=3 KnotsCount=2 Degree=2 IsPeriodic=0
    g4: GeomPoint X=0 Y=0 Z=0
    g5: GeomPoint X=8 Y=6 Z=0
    g6: LineSegment StartX=0 StartY=6 StartZ=0 EndX=8 EndY=6 EndZ=0
  constraints (14):
    c: Coincident(g0,g-1)
    c: Distance(g0) = 6
    c: Vertical(g0)
    c: Coincident(g3,g0)
    c: Weight(g1) = 1
    c: Equal(g1,g2)
    c: InternalAlignment(g1,g3)
    c: InternalAlignment(g2,g3)
    c: InternalAlignment(g4,g3)
    c: InternalAlignment(g5,g3)
    c: Block(g3)
    c: Coincident(g6,g0)
    c: Coincident(g6,g3)
    c: Horizontal(g6)
FEATURE [Part::Extrusion] Extrude015  label="caseScrewPillarBracket003"
  Base = -> Sketch021
  Dir = (0,0,1)
  DirMode = 2
  FaceMakerClass = Part::FaceMakerBullseye
  LengthFwd = 2.4
  LengthRev = 0
  Placement = pos=(11.3,29,58.74) rot=(0,1,0;1.5708rad)
  Solid = true
  Symmetric = false
FEATURE [Sketcher::SketchObject] Sketch022
  FullyConstrained = true
  sketch-geometry (7):
    g0: LineSegment StartX=0 StartY=0 StartZ=0 EndX=0 EndY=6 EndZ=0
    g1: Circle CenterX=0 CenterY=0 CenterZ=0 NormalX=0 NormalY=0 NormalZ=1 AngleXU=0 Radius=1
    g2: Circle CenterX=8 CenterY=6 CenterZ=0 NormalX=0 NormalY=0 NormalZ=1 AngleXU=0 Radius=1
    g3: BSplineCurve PolesCount=3 KnotsCount=2 Degree=2 IsPeriodic=0
    g4: GeomPoint X=0 Y=0 Z=0
    g5: GeomPoint X=8 Y=6 Z=0
    g6: LineSegment StartX=0 StartY=6 StartZ=0 EndX=8 EndY=6 EndZ=0
  constraints (14):
    c: Coincident(g0,g-1)
    c: Distance(g0) = 6
    c: Vertical(g0)
    c: Coincident(g3,g0)
    c: Weight(g1) = 1
    c: Equal(g1,g2)
    c: InternalAlignment(g1,g3)
    c: InternalAlignment(g2,g3)
    c: InternalAlignment(g4,g3)
    c: InternalAlignment(g5,g3)
    c: Block(g3)
    c: Coincident(g6,g0)
    c: Coincident(g6,g3)
    c: Horizontal(g6)
FEATURE [Part::Extrusion] Extrude016  label="caseScrewPillarBracket004"
  Base = -> Sketch022
  Dir = (0,0,1)
  DirMode = 2
  FaceMakerClass = Part::FaceMakerBullseye
  LengthFwd = 2.4
  LengthRev = 0
  Placement = pos=(88.3,29,65.23) rot=(0,1,0;1.5708rad)
  Solid = true
  Symmetric = false
FEATURE [Sketcher::SketchObject] Sketch023
  FullyConstrained = true
  sketch-geometry (7):
    g0: LineSegment StartX=0 StartY=0 StartZ=0 EndX=0 EndY=6 EndZ=0
    g1: Circle CenterX=0 CenterY=0 CenterZ=0 NormalX=0 NormalY=0 NormalZ=1 AngleXU=0 Radius=1
    g2: Circle CenterX=8 CenterY=6 CenterZ=0 NormalX=0 NormalY=0 NormalZ=1 AngleXU=0 Radius=1
    g3: BSplineCurve PolesCount=3 KnotsCount=2 Degree=2 IsPeriodic=0
    g4: GeomPoint X=0 Y=0 Z=0
    g5: GeomPoint X=8 Y=6 Z=0
    g6: LineSegment StartX=0 StartY=6 StartZ=0 EndX=8 EndY=6 EndZ=0
  constraints (14):
    c: Coincident(g0,g-1)
    c: Distance(g0) = 6
    c: Vertical(g0)
    c: Coincident(g3,g0)
    c: Weight(g1) = 1
    c: Equal(g1,g2)
    c: InternalAlignment(g1,g3)
    c: InternalAlignment(g2,g3)
    c: InternalAlignment(g4,g3)
    c: InternalAlignment(g5,g3)
    c: Block(g3)
    c: Coincident(g6,g0)
    c: Coincident(g6,g3)
    c: Horizontal(g6)
FEATURE [Part::Extrusion] Extrude017  label="caseScrewPillarBracket005"
  Base = -> Sketch023
  Dir = (0,0,1)
  DirMode = 2
  FaceMakerClass = Part::FaceMakerBullseye
  LengthFwd = 2.4
  LengthRev = 0
  Placement = pos=(90.7,29,6.77) rot=(0,-1,0;1.5708rad)
  Solid = true
  Symmetric = false
FEATURE [Sketcher::SketchObject] Sketch024
  FullyConstrained = true
  sketch-geometry (7):
    g0: LineSegment StartX=0 StartY=0 StartZ=0 EndX=0 EndY=6 EndZ=0
    g1: Circle CenterX=0 CenterY=0 CenterZ=0 NormalX=0 NormalY=0 NormalZ=1 AngleXU=0 Radius=1
    g2: Circle CenterX=8 CenterY=6 CenterZ=0 NormalX=0 NormalY=0 NormalZ=1 AngleXU=0 Radius=1
    g3: BSplineCurve PolesCount=3 KnotsCount=2 Degree=2 IsPeriodic=0
    g4: GeomPoint X=0 Y=0 Z=0
    g5: GeomPoint X=8 Y=6 Z=0
    g6: LineSegment StartX=0 StartY=6 StartZ=0 EndX=8 EndY=6 EndZ=0
  constraints (14):
    c: Coincident(g0,g-1)
    c: Distance(g0) = 6
    c: Vertical(g0)
    c: Coincident(g3,g0)
    c: Weight(g1) = 1
    c: Equal(g1,g2)
    c: InternalAlignment(g1,g3)
    c: InternalAlignment(g2,g3)
    c: InternalAlignment(g4,g3)
    c: InternalAlignment(g5,g3)
    c: Block(g3)
    c: Coincident(g6,g0)
    c: Coincident(g6,g3)
    c: Horizontal(g6)
FEATURE [Part::Extrusion] Extrude018  label="caseScrewPillarBracket006"
  Base = -> Sketch024
  Dir = (0,0,1)
  DirMode = 2
  FaceMakerClass = Part::FaceMakerBullseye
  LengthFwd = 2.4
  LengthRev = 0
  Placement = pos=(103.7,29,6.77) rot=(0,-1,0;1.5708rad)
  Solid = true
  Symmetric = false
FEATURE [Sketcher::SketchObject] Sketch025
  FullyConstrained = true
  sketch-geometry (7):
    g0: LineSegment StartX=0 StartY=0 StartZ=0 EndX=0 EndY=6 EndZ=0
    g1: Circle CenterX=0 CenterY=0 CenterZ=0 NormalX=0 NormalY=0 NormalZ=1 AngleXU=0 Radius=1
    g2: Circle CenterX=8 CenterY=6 CenterZ=0 NormalX=0 NormalY=0 NormalZ=1 AngleXU=0 Radius=1
    g3: BSplineCurve PolesCount=3 KnotsCount=2 Degree=2 IsPeriodic=0
    g4: GeomPoint X=0 Y=0 Z=0
    g5: GeomPoint X=8 Y=6 Z=0
    g6: LineSegment StartX=0 StartY=6 StartZ=0 EndX=8 EndY=6 EndZ=0
  constraints (14):
    c: Coincident(g0,g-1)
    c: Distance(g0) = 6
    c: Vertical(g0)
    c: Coincident(g3,g0)
    c: Weight(g1) = 1
    c: Equal(g1,g2)
    c: InternalAlignment(g1,g3)
    c: InternalAlignment(g2,g3)
    c: InternalAlignment(g4,g3)
    c: InternalAlignment(g5,g3)
    c: Block(g3)
    c: Coincident(g6,g0)
    c: Coincident(g6,g3)
    c: Horizontal(g6)
FEATURE [Part::Extrusion] Extrude019  label="caseScrewPillarBracket007"
  Base = -> Sketch025
  Dir = (0,0,1)
  DirMode = 2
  FaceMakerClass = Part::FaceMakerBullseye
  LengthFwd = 2.4
  LengthRev = 0
  Placement = pos=(101.3,29,65.23) rot=(0,1,0;1.5708rad)
  Solid = true
  Symmetric = false
FEATURE [Part::Box] Box011  label="frontCaseScrewPillarBracket"
  AttacherType = Attacher::AttachEngine3D
  Height = 2.4
  Length = 16
  Placement = pos=(87,28,2.3) rot=(0,0,1;0rad)
  Width = 7
FEATURE [Part::Box] Box012  label="frontCaseScrewPillarBracket001"
  AttacherType = Attacher::AttachEngine3D
  Height = 2.4
  Length = 16
  Placement = pos=(87,28,67.3) rot=(0,0,1;0rad)
  Width = 7
FEATURE [Sketcher::SketchObject] Sketch026
  FullyConstrained = true
  sketch-geometry (17):
    g0: Circle CenterX=-3.5 CenterY=23.5 CenterZ=0 NormalX=0 NormalY=0 NormalZ=1 AngleXU=0 Radius=1
    g1: Circle CenterX=-1 CenterY=15.25 CenterZ=0 NormalX=0 NormalY=0 NormalZ=1 AngleXU=0 Radius=1
    g2: Circle CenterX=-3.5 CenterY=7 CenterZ=0 NormalX=0 NormalY=0 NormalZ=1 AngleXU=0 Radius=1
    g3: BSplineCurve PolesCount=3 KnotsCount=2 Degree=2 IsPeriodic=0
    g4: GeomPoint X=-3.5 Y=23.5 Z=0
    g5: GeomPoint X=-3.5 Y=7 Z=0
    g6: Circle CenterX=-4.8 CenterY=30.5 CenterZ=0 NormalX=0 NormalY=0 NormalZ=1 AngleXU=0 Radius=1
    g7: Circle CenterX=-3.5 CenterY=30.5 CenterZ=0 NormalX=0 NormalY=0 NormalZ=1 AngleXU=0 Radius=1
    g8: Circle CenterX=-3.5 CenterY=29.2 CenterZ=0 NormalX=0 NormalY=0 NormalZ=1 AngleXU=0 Radius=1
    g9: BSplineCurve PolesCount=3 KnotsCount=2 Degree=2 IsPeriodic=0
    g10: GeomPoint X=-4.8 Y=30.5 Z=0
    g11: GeomPoint X=-3.5 Y=29.2 Z=0
    g12: LineSegment StartX=-3.5 StartY=29.2 StartZ=0 EndX=-3.5 EndY=23.5 EndZ=0
    g13: LineSegment StartX=-4.8 StartY=30.5 StartZ=0 EndX=0 EndY=30.5 EndZ=0
    g14: LineSegment StartX=-3.5 StartY=5 StartZ=0 EndX=-3.5 EndY=7 EndZ=0
    g15: LineSegment StartX=0 StartY=5 StartZ=0 EndX=0 EndY=30.5 EndZ=0
    g16: LineSegment StartX=-3.5 StartY=5 StartZ=0 EndX=0 EndY=5 EndZ=0
  constraints (33):
    c: Weight(g0) = 1
    c: Equal(g0,g1)
    c: Equal(g0,g2)
    c: InternalAlignment(g0,g3)
    c: InternalAlignment(g1,g3)
    c: InternalAlignment(g2,g3)
    c: InternalAlignment(g4,g3)
    c: InternalAlignment(g5,g3)
    c: Block(g3)
    c: Weight(g6) = 1
    c: Equal(g6,g7)
    c: Equal(g6,g8)
    c: InternalAlignment(g6,g9)
    c: InternalAlignment(g7,g9)
    c: InternalAlignment(g8,g9)
    c: InternalAlignment(g10,g9)
    c: InternalAlignment(g11,g9)
    c: Block(g9)
    c: Coincident(g12,g9)
    c: Coincident(g12,g3)
    c: Vertical(g12)
    c: Coincident(g13,g9)
    c: Horizontal(g13)
    c: Distance(g13) = 4.8
    c: Coincident(g14,g3)
    c: Vertical(g14)
    c: Coincident(g15,g13)
    c: Vertical(g15)
    c: Tangent(g15,g1)
    c: Distance(g14) = 2
    c: Coincident(g16,g14)
    c: Horizontal(g16)
    c: Coincident(g15,g16)
FEATURE [Part::Feature] Face050
  shape: bbox 4.8 x 25.5 x 2e-07 mm, 1 faces, 0 solids (baked)
FEATURE [Part::Revolution] Revolve054  label="moreFrontCaseScrewPost001"
  Angle = 360
  Axis = (0,1,0)
  Base = (0,0,0)
  FaceMakerClass = Part::FaceMakerBullseye
  Placement = pos=(102.5,4.5,3.5) rot=(0,0,1;0rad)
  Solid = false
  Source = -> Face050
  Symmetric = false
FEATURE [Part::Feature] Face051
  shape: bbox 4.8 x 25.5 x 2e-07 mm, 1 faces, 0 solids (baked)
FEATURE [Part::Revolution] Revolve055  label="moreFrontCaseScrewPost002"
  Angle = 360
  Axis = (0,1,0)
  Base = (0,0,0)
  FaceMakerClass = Part::FaceMakerBullseye
  Placement = pos=(102.5,4.5,68.5) rot=(0,0,1;0rad)
  Solid = false
  Source = -> Face051
  Symmetric = false
FEATURE [Sketcher::SketchObject] Sketch027
  FullyConstrained = true
  sketch-geometry (10):
    g0: LineSegment StartX=-1.6 StartY=4.7 StartZ=0 EndX=-1.6 EndY=1.7 EndZ=0
    g1: LineSegment StartX=-3.5 StartY=4.7 StartZ=0 EndX=-1.6 EndY=4.7 EndZ=0
    g2: LineSegment StartX=-1.6 StartY=1.7 StartZ=0 EndX=-1.6 EndY=1.5 EndZ=0
    g3: LineSegment StartX=-1.6 StartY=1.5 StartZ=0 EndX=-5.2 EndY=1.5 EndZ=0
    g4: Circle CenterX=-3.5 CenterY=4.7 CenterZ=0 NormalX=0 NormalY=0 NormalZ=1 AngleXU=0 Radius=1
    g5: Circle CenterX=-3.59627 CenterY=2.99743 CenterZ=0 NormalX=0 NormalY=0 NormalZ=1 AngleXU=0 Radius=1
    g6: Circle CenterX=-5.2 CenterY=1.5 CenterZ=0 NormalX=0 NormalY=0 NormalZ=1 AngleXU=0 Radius=1
    g7: BSplineCurve PolesCount=3 KnotsCount=2 Degree=2 IsPeriodic=0
    g8: GeomPoint X=-3.5 Y=4.7 Z=0
    g9: GeomPoint X=-5.2 Y=1.5 Z=0
  constraints (23):
    c: Vertical(g0)
    c: Distance(g0) = 3
    c: Coincident(g1,g0)
    c: Horizontal(g1)
    c: Block(g0)
    c: Block(g1)
    c: Coincident(g2,g0)
    c: Vertical(g2)
    c: Distance(g2) = 0.2
    c: Coincident(g3,g2)
    c: Horizontal(g3)
    c: Block(g3)
    c: Coincident(g7,g1)
    c: Weight(g4) = 1
    c: Equal(g4,g5)
    c: Equal(g4,g6)
    c: Coincident(g7,g3)
    c: InternalAlignment(g4,g7)
    c: InternalAlignment(g5,g7)
    c: InternalAlignment(g6,g7)
    c: InternalAlignment(g8,g7)
    c: InternalAlignment(g9,g7)
    c: Block(g7)
FEATURE [Sketcher::SketchObject] Sketch028
  FullyConstrained = true
  sketch-geometry (18):
    g0: LineSegment StartX=0 StartY=3e-16 StartZ=0 EndX=0 EndY=1.7 EndZ=0
    g1: LineSegment StartX=-3.5 StartY=0 StartZ=0 EndX=-3.5 EndY=0.9 EndZ=0
    g2: Circle CenterX=-2.7 CenterY=1.7 CenterZ=0 NormalX=0 NormalY=0 NormalZ=1 AngleXU=0 Radius=1
    g3: Circle CenterX=-3.5 CenterY=1.7 CenterZ=0 NormalX=0 NormalY=0 NormalZ=1 AngleXU=0 Radius=1
    g4: Circle CenterX=-3.5 CenterY=0.9 CenterZ=0 NormalX=0 NormalY=0 NormalZ=1 AngleXU=0 Radius=1
    g5: BSplineCurve PolesCount=3 KnotsCount=2 Degree=2 IsPeriodic=0
    g6: GeomPoint X=-2.7 Y=1.7 Z=0
    g7: GeomPoint X=-3.5 Y=0.9 Z=0
    g8: LineSegment StartX=-3.5 StartY=0 StartZ=0 EndX=-3.5 EndY=-7 EndZ=0
    g9: LineSegment StartX=0 StartY=3e-16 StartZ=0 EndX=0 EndY=-7 EndZ=0
    g10: LineSegment StartX=-3.5 StartY=-7 StartZ=0 EndX=0 EndY=-7 EndZ=0
    g11: LineSegment StartX=-2.7 StartY=1.7 StartZ=0 EndX=-1.6 EndY=1.7 EndZ=0
    g12: LineSegment StartX=0 StartY=1.7 StartZ=0 EndX=0 EndY=4.5 EndZ=0
    g13: LineSegment StartX=0 StartY=4.5 StartZ=0 EndX=0 EndY=10.8 EndZ=0
    g14: LineSegment StartX=0 StartY=10.8 StartZ=0 EndX=-2 EndY=10.8 EndZ=0
    g15: LineSegment StartX=-1.6 StartY=4.7 StartZ=0 EndX=-1.6 EndY=1.7 EndZ=0
    g16: LineSegment StartX=-1.6 StartY=4.7 StartZ=0 EndX=-2 EndY=4.7 EndZ=0
    g17: LineSegment StartX=-2 StartY=4.7 StartZ=0 EndX=-2 EndY=10.8 EndZ=0
  constraints (44):
    c: Vertical(g0)
    c: Vertical(g1)
    c: Distance(g1) = 0.9
    c: Block(g0)
    c: Distance(g0) = 1.7
    c: Weight(g2) = 1
    c: Equal(g2,g3)
    c: Equal(g2,g4)
    c: Coincident(g5,g1)
    c: InternalAlignment(g2,g5)
    c: InternalAlignment(g3,g5)
    c: InternalAlignment(g4,g5)
    c: InternalAlignment(g6,g5)
    c: InternalAlignment(g7,g5)
    c: Block(g5)
    c: Coincident(g8,g1)
    c: Vertical(g8)
    c: Distance(g8) = 7
    c: Vertical(g9)
    c: Equal(g8,g9) = 7
    c: Coincident(g9,g0)
    c: Coincident(g10,g8)
    c: Coincident(g10,g9)
    c: Horizontal(g10)
    c: Coincident(g11,g5)
    c: Horizontal(g11)
    c: Coincident(g12,g0)
    c: Vertical(g12)
    c: Distance(g12) = 2.8
    c: Coincident(g13,g12)
    c: Vertical(g13)
    c: Distance(g13) = 6.3
    c: Coincident(g14,g13)
    c: Horizontal(g14)
    c: Distance(g14) = 2
    c: Vertical(g15)
    c: Distance(g15) = 3
    c: Block(g11)
    c: Coincident(g15,g11)
    c: Coincident(g16,g15)
    c: Horizontal(g16)
    c: Coincident(g17,g16)
    c: Coincident(g17,g14)
    c: Vertical(g17)
FEATURE [Part::Revolution] Revolve040  label="backCaseScrewRetainer001"
  Angle = 360
  Axis = (0,1,0)
  Base = (0,0,0)
  FaceMakerClass = Part::FaceMakerBullseye
  Placement = pos=(12.5,3,10) rot=(0,0,1;0rad)
  Solid = false
  Source = -> Face036
  Symmetric = false
FEATURE [Part::Feature] Face055
  shape: bbox 3.5 x 30.2 x 2e-07 mm, 1 faces, 0 solids (baked)
FEATURE [Part::Revolution] Revolve059  label="backCaseScrewPost"
  Angle = 360
  Axis = (0,1,0)
  Base = (0,0,0)
  FaceMakerClass = Part::FaceMakerBullseye
  Placement = pos=(12.5,4.5,10) rot=(0,0,1;0rad)
  Solid = false
  Source = -> Face055
  Symmetric = false
FEATURE [Part::Feature] Face056
  shape: bbox 3.5 x 30.2 x 2e-07 mm, 1 faces, 0 solids (baked)
FEATURE [Part::Revolution] Revolve060  label="backCaseScrewPost001"
  Angle = 360
  Axis = (0,1,0)
  Base = (0,0,0)
  FaceMakerClass = Part::FaceMakerBullseye
  Placement = pos=(12.5,4.5,62) rot=(0,0,1;0rad)
  Solid = false
  Source = -> Face056
  Symmetric = false
FEATURE [Part::Feature] Face057
  shape: bbox 3.5 x 17.8 x 2e-07 mm, 1 faces, 0 solids (baked)
FEATURE [Part::Revolution] Revolve061  label="removeToCreateScrewAndThreadedInsertHole"
  Angle = 360
  Axis = (0,1,0)
  Base = (0,0,0)
  FaceMakerClass = Part::FaceMakerBullseye
  Placement = pos=(12.5,0,10) rot=(0,0,1;0rad)
  Solid = false
  Source = -> Face057
  Symmetric = false
FEATURE [Part::Feature] Face058
  shape: bbox 3.5 x 17.8 x 2e-07 mm, 1 faces, 0 solids (baked)
FEATURE [Part::Revolution] Revolve062  label="removeToCreateScrewAndThreadedInsertHole001"
  Angle = 360
  Axis = (0,1,0)
  Base = (0,0,0)
  FaceMakerClass = Part::FaceMakerBullseye
  Placement = pos=(12.5,0,62) rot=(0,0,1;0rad)
  Solid = false
  Source = -> Face058
  Symmetric = false
FEATURE [Part::Feature] Face059
  shape: bbox 3.5 x 17.8 x 2e-07 mm, 1 faces, 0 solids (baked)
FEATURE [Part::Revolution] Revolve063  label="removeToCreateScrewAndThreadedInsertHole002"
  Angle = 360
  Axis = (0,1,0)
  Base = (0,0,0)
  FaceMakerClass = Part::FaceMakerBullseye
  Placement = pos=(89.5,0,68.5) rot=(0,0,1;0rad)
  Solid = false
  Source = -> Face059
  Symmetric = false
FEATURE [Part::Feature] Face060
  shape: bbox 3.5 x 17.8 x 2e-07 mm, 1 faces, 0 solids (baked)
FEATURE [Part::Revolution] Revolve064  label="removeToCreateScrewAndThreadedInsertHole003"
  Angle = 360
  Axis = (0,1,0)
  Base = (0,0,0)
  FaceMakerClass = Part::FaceMakerBullseye
  Placement = pos=(89.5,0,3.5) rot=(0,0,1;0rad)
  Solid = false
  Source = -> Face060
  Symmetric = false
FEATURE [Part::Feature] Face061
  shape: bbox 3.5 x 17.8 x 2e-07 mm, 1 faces, 0 solids (baked)
FEATURE [Part::Revolution] Revolve065  label="removeToCreateScrewAndThreadedInsertHole004"
  Angle = 360
  Axis = (0,1,0)
  Base = (0,0,0)
  FaceMakerClass = Part::FaceMakerBullseye
  Placement = pos=(102.5,4.7,3.5) rot=(0,0,1;0rad)
  Solid = false
  Source = -> Face061
  Symmetric = false
FEATURE [Part::Feature] Face062
  shape: bbox 3.5 x 17.8 x 2e-07 mm, 1 faces, 0 solids (baked)
FEATURE [Part::Revolution] Revolve066  label="removeToCreateScrewAndThreadedInsertHole005"
  Angle = 360
  Axis = (0,1,0)
  Base = (0,0,0)
  FaceMakerClass = Part::FaceMakerBullseye
  Placement = pos=(102.5,4.7,68.5) rot=(0,0,1;0rad)
  Solid = false
  Source = -> Face062
  Symmetric = false
FEATURE [Part::MultiFuse] Fusion047  label="makeHoles"
  Shapes = -> [Revolve066,Revolve065,Revolve064,Revolve063,Revolve062,Revolve061]
FEATURE [Part::Feature] Face063
  shape: bbox 3.6 x 3.2 x 2e-07 mm, 1 faces, 0 solids (baked)
FEATURE [Part::Revolution] Revolve067  label="moreFrontCaseScrewRetainer002"
  Angle = 360
  Axis = (0,1,0)
  Base = (0,0,0)
  FaceMakerClass = Part::FaceMakerBullseye
  Placement = pos=(102.5,4.5,68.5) rot=(0,0,1;0rad)
  Solid = false
  Source = -> Face063
  Symmetric = false
FEATURE [Part::Feature] Face064
  shape: bbox 3.6 x 3.2 x 2e-07 mm, 1 faces, 0 solids (baked)
FEATURE [Part::Revolution] Revolve068  label="moreFrontCaseScrewRetainer003"
  Angle = 360
  Axis = (0,1,0)
  Base = (0,0,0)
  FaceMakerClass = Part::FaceMakerBullseye
  Placement = pos=(102.5,4.5,3.5) rot=(0,0,1;0rad)
  Solid = false
  Source = -> Face064
  Symmetric = false
FEATURE [Part::Feature] Face065
  shape: bbox 3.5 x 17.8 x 2e-07 mm, 1 faces, 0 solids (baked)
FEATURE [Part::Revolution] Revolve069  label="removeToCreateScrewAndThreadedInsertHole006"
  Angle = 360
  Axis = (0,1,0)
  Base = (0,0,0)
  FaceMakerClass = Part::FaceMakerBullseye
  Placement = pos=(12.5,0,10) rot=(0,0,1;0rad)
  Solid = false
  Source = -> Face065
  Symmetric = false
FEATURE [Part::Feature] Face066
  shape: bbox 3.5 x 17.8 x 2e-07 mm, 1 faces, 0 solids (baked)
FEATURE [Part::Revolution] Revolve070  label="removeToCreateScrewAndThreadedInsertHole007"
  Angle = 360
  Axis = (0,1,0)
  Base = (0,0,0)
  FaceMakerClass = Part::FaceMakerBullseye
  Placement = pos=(12.5,0,62) rot=(0,0,1;0rad)
  Solid = false
  Source = -> Face066
  Symmetric = false
FEATURE [Part::Feature] Face067
  shape: bbox 3.5 x 17.8 x 2e-07 mm, 1 faces, 0 solids (baked)
FEATURE [Part::Revolution] Revolve071  label="removeToCreateScrewAndThreadedInsertHole008"
  Angle = 360
  Axis = (0,1,0)
  Base = (0,0,0)
  FaceMakerClass = Part::FaceMakerBullseye
  Placement = pos=(89.5,0,68.5) rot=(0,0,1;0rad)
  Solid = false
  Source = -> Face067
  Symmetric = false
FEATURE [Part::Feature] Face068
  shape: bbox 3.5 x 17.8 x 2e-07 mm, 1 faces, 0 solids (baked)
FEATURE [Part::Revolution] Revolve072  label="removeToCreateScrewAndThreadedInsertHole009"
  Angle = 360
  Axis = (0,1,0)
  Base = (0,0,0)
  FaceMakerClass = Part::FaceMakerBullseye
  Placement = pos=(89.5,0,3.5) rot=(0,0,1;0rad)
  Solid = false
  Source = -> Face068
  Symmetric = false
FEATURE [Part::Feature] Face069
  shape: bbox 3.5 x 17.8 x 2e-07 mm, 1 faces, 0 solids (baked)
FEATURE [Part::Feature] Face070
  shape: bbox 3.5 x 17.8 x 2e-07 mm, 1 faces, 0 solids (baked)
FEATURE [Part::Revolution] Revolve073  label="removeToCreateScrewAndThreadedInsertHole010"
  Angle = 360
  Axis = (0,1,0)
  Base = (0,0,0)
  FaceMakerClass = Part::FaceMakerBullseye
  Placement = pos=(102.5,4.7,3.5) rot=(0,0,1;0rad)
  Solid = false
  Source = -> Face069
  Symmetric = false
FEATURE [Part::Revolution] Revolve074  label="removeToCreateScrewAndThreadedInsertHole011"
  Angle = 360
  Axis = (0,1,0)
  Base = (0,0,0)
  FaceMakerClass = Part::FaceMakerBullseye
  Placement = pos=(102.5,4.7,68.5) rot=(0,0,1;0rad)
  Solid = false
  Source = -> Face070
  Symmetric = false
FEATURE [Part::MultiFuse] Fusion048  label="makeHoles001"
  Shapes = -> [Revolve074,Revolve073,Revolve072,Revolve071,Revolve070,Revolve069]
FEATURE [Part::MultiFuse] Fusion049  label="caseScrewRetainers"
  Shapes = -> [Revolve067,Revolve068,Revolve048,Revolve047,Revolve039,Revolve040]
FEATURE [Part::Cut] Cut015  label="caseScrewRetainers001"
  Base = -> Fusion049
  Tool = -> Fusion048
FEATURE [Part::MultiFuse] Fusion050  label="casePillars"
  Shapes = -> [Revolve055,Revolve054,Revolve043,Revolve046,Revolve059,Revolve060]
FEATURE [Part::Feature] Face071 .. Face076  x6 (patterned run collapsed; names and placements below)
  shape: bbox 3.5 x 17.8 x 2e-07 mm, 1 faces, 0 solids (baked)
FEATURE [Part::Revolution] Revolve075  label="removeToCreateScrewAndThreadedInsertHole012"
  Angle = 360
  Axis = (0,1,0)
  Base = (0,0,0)
  FaceMakerClass = Part::FaceMakerBullseye
  Placement = pos=(12.5,0,10) rot=(0,0,1;0rad)
  Solid = false
  Source = -> Face071
  Symmetric = false
FEATURE [Part::Revolution] Revolve076  label="removeToCreateScrewAndThreadedInsertHole013"
  Angle = 360
  Axis = (0,1,0)
  Base = (0,0,0)
  FaceMakerClass = Part::FaceMakerBullseye
  Placement = pos=(12.5,0,62) rot=(0,0,1;0rad)
  Solid = false
  Source = -> Face072
  Symmetric = false
FEATURE [Part::Revolution] Revolve077  label="removeToCreateScrewAndThreadedInsertHole014"
  Angle = 360
  Axis = (0,1,0)
  Base = (0,0,0)
  FaceMakerClass = Part::FaceMakerBullseye
  Placement = pos=(89.5,0,68.5) rot=(0,0,1;0rad)
  Solid = false
  Source = -> Face073
  Symmetric = false
FEATURE [Part::Revolution] Revolve078  label="removeToCreateScrewAndThreadedInsertHole015"
  Angle = 360
  Axis = (0,1,0)
  Base = (0,0,0)
  FaceMakerClass = Part::FaceMakerBullseye
  Placement = pos=(89.5,0,3.5) rot=(0,0,1;0rad)
  Solid = false
  Source = -> Face074
  Symmetric = false
FEATURE [Part::Revolution] Revolve079  label="removeToCreateScrewAndThreadedInsertHole016"
  Angle = 360
  Axis = (0,1,0)
  Base = (0,0,0)
  FaceMakerClass = Part::FaceMakerBullseye
  Placement = pos=(102.5,4.7,3.5) rot=(0,0,1;0rad)
  Solid = false
  Source = -> Face075
  Symmetric = false
FEATURE [Part::Revolution] Revolve080  label="removeToCreateScrewAndThreadedInsertHole017"
  Angle = 360
  Axis = (0,1,0)
  Base = (0,0,0)
  FaceMakerClass = Part::FaceMakerBullseye
  Placement = pos=(102.5,4.7,68.5) rot=(0,0,1;0rad)
  Solid = false
  Source = -> Face076
  Symmetric = false
FEATURE [Part::MultiFuse] Fusion051  label="makeHoles002"
  Shapes = -> [Revolve080,Revolve079,Revolve078,Revolve077,Revolve076,Revolve075]
FEATURE [Part::Cut] Cut016  label="caesPillars"
  Base = -> Fusion050
  Tool = -> Fusion051
FEATURE [Part::Revolution] Revolve009  label="plugHousing016"
  Angle = 360
  Axis = (0,1,0)
  Base = (0,0,0)
  FaceMakerClass = Part::FaceMakerBullseye
  Placement = pos=(0,0,36.15) rot=(0,0,1;0rad)
  Solid = false
  Source = -> Face012
  Symmetric = false
FEATURE [Part::MultiFuse] Fusion014  label="plugHousing023"
  Placement = pos=(0,0,0) rot=(0,0,1;1.5708rad)
  Shapes = -> [Revolve011,Revolve009]
FEATURE [Part::Revolution] Revolve010  label="plugHousing017"
  Angle = 360
  Axis = (0,1,0)
  Base = (0,0,0)
  FaceMakerClass = Part::FaceMakerBullseye
  Placement = pos=(0,0,36.15) rot=(0,0,1;0rad)
  Solid = false
  Source = -> Face014
  Symmetric = false
FEATURE [Part::MultiFuse] Fusion015  label="plugHousing024"
  Placement = pos=(0,0,0) rot=(0,0,1;1.5708rad)
  Shapes = -> [Revolve010,Revolve015]
FEATURE [Part::Revolution] Revolve014  label="plugHousing026"
  Angle = 360
  Axis = (0,1,0)
  Base = (0,0,0)
  FaceMakerClass = Part::FaceMakerBullseye
  Placement = pos=(0,0,36.15) rot=(0,0,1;0rad)
  Solid = false
  Source = -> Face011
  Symmetric = false
FEATURE [Part::Revolution] Revolve013  label="plugHousing025"
  Angle = 360
  Axis = (0,1,0)
  Base = (0,0,0)
  FaceMakerClass = Part::FaceMakerBullseye
  Placement = pos=(0,0,36.15) rot=(0,0,1;0rad)
  Solid = false
  Source = -> Face015
  Symmetric = false
FEATURE [Part::MultiFuse] Fusion016  label="plugHousing028"
  Placement = pos=(0,19,0) rot=(0,0,1;3.14159rad)
  Shapes = -> [Fusion014,Fusion013]
FEATURE [Part::MultiFuse] Fusion011  label="plugHousing018"
  Placement = pos=(0,0,0) rot=(0,0,1;1.5708rad)
  Shapes = -> [Revolve014,Revolve013]
FEATURE [Part::MultiFuse] Fusion012  label="plugHousing019"
  Placement = pos=(0,19,0) rot=(0,0,1;3.14159rad)
  Shapes = -> [Fusion011,Fusion015]
FEATURE [Part::MultiFuse] Fusion017  label="plugHousing029"
  Placement = pos=(122.621,0,-0.15) rot=(0,0,1;0rad)
  Shapes = -> [Fusion016,Fusion012]
FEATURE [Part::MultiFuse] Fusion052  label="casePillarRetainers"
  Shapes = -> [Extrude012,Extrude013,Extrude014,Extrude015,Extrude016,Extrude017,Extrude018,Extrude019,Box011,Box012]
FEATURE [Part::Feature] Face077
  shape: bbox 3.5 x 17.8 x 2e-07 mm, 1 faces, 0 solids (baked)
FEATURE [Part::Revolution] Revolve081  label="removeToCreateScrewAndThreadedInsertHole018"
  Angle = 360
  Axis = (0,1,0)
  Base = (0,0,0)
  FaceMakerClass = Part::FaceMakerBullseye
  Placement = pos=(62.3,30.3,19.7) rot=(0,0,1;0rad)
  Solid = false
  Source = -> Face077
  Symmetric = false
FEATURE [Part::Feature] Face078
  shape: bbox 3.5 x 17.8 x 2e-07 mm, 1 faces, 0 solids (baked)
FEATURE [Part::Revolution] Revolve082  label="removeToCreateScrewAndThreadedInsertHole019"
  Angle = 360
  Axis = (0,1,0)
  Base = (0,0,0)
  FaceMakerClass = Part::FaceMakerBullseye
  Placement = pos=(62.3,30.3,51.7) rot=(0,0,1;0rad)
  Solid = false
  Source = -> Face078
  Symmetric = false
FEATURE [Part::Feature] Face079
  shape: bbox 3.5 x 17.8 x 2e-07 mm, 1 faces, 0 solids (baked)
FEATURE [Part::Revolution] Revolve083  label="removeToCreateScrewAndThreadedInsertHole020"
  Angle = 360
  Axis = (0,1,0)
  Base = (0,0,0)
  FaceMakerClass = Part::FaceMakerBullseye
  Placement = pos=(30.3,30.3,19.7) rot=(0,0,1;0rad)
  Solid = false
  Source = -> Face079
  Symmetric = false
FEATURE [Part::Feature] Face080
  shape: bbox 3.5 x 17.8 x 2e-07 mm, 1 faces, 0 solids (baked)
FEATURE [Part::Revolution] Revolve084  label="removeToCreateScrewAndThreadedInsertHole021"
  Angle = 360
  Axis = (0,1,0)
  Base = (0,0,0)
  FaceMakerClass = Part::FaceMakerBullseye
  Placement = pos=(30.3,30.3,51.7) rot=(0,0,1;0rad)
  Solid = false
  Source = -> Face080
  Symmetric = false
FEATURE [Part::MultiFuse] Fusion053  label="createThreadedInsertHolesForFan"
  Shapes = -> [Revolve081,Revolve082,Revolve083,Revolve084]
FEATURE [Part::Cut] Cut017  label="fanScrewHousing001"
  Base = -> Fusion046
  Tool = -> Fusion053
FEATURE [Part::Feature] Face081
  shape: bbox 3.5 x 17.8 x 2e-07 mm, 1 faces, 0 solids (baked)
FEATURE [Part::Revolution] Revolve085  label="removeToCreateScrewAndThreadedInsertHole022"
  Angle = 360
  Axis = (0,1,0)
  Base = (0,0,0)
  FaceMakerClass = Part::FaceMakerBullseye
  Placement = pos=(62.3,30.3,19.7) rot=(0,0,1;0rad)
  Solid = false
  Source = -> Face081
  Symmetric = false
FEATURE [Part::Feature] Face082
  shape: bbox 3.5 x 17.8 x 2e-07 mm, 1 faces, 0 solids (baked)
FEATURE [Part::Revolution] Revolve086  label="removeToCreateScrewAndThreadedInsertHole023"
  Angle = 360
  Axis = (0,1,0)
  Base = (0,0,0)
  FaceMakerClass = Part::FaceMakerBullseye
  Placement = pos=(62.3,30.3,51.7) rot=(0,0,1;0rad)
  Solid = false
  Source = -> Face082
  Symmetric = false
FEATURE [Part::Feature] Face083
  shape: bbox 3.5 x 17.8 x 2e-07 mm, 1 faces, 0 solids (baked)
FEATURE [Part::Revolution] Revolve087  label="removeToCreateScrewAndThreadedInsertHole024"
  Angle = 360
  Axis = (0,1,0)
  Base = (0,0,0)
  FaceMakerClass = Part::FaceMakerBullseye
  Placement = pos=(30.3,30.3,19.7) rot=(0,0,1;0rad)
  Solid = false
  Source = -> Face083
  Symmetric = false
FEATURE [Part::Feature] Face084
  shape: bbox 3.5 x 17.8 x 2e-07 mm, 1 faces, 0 solids (baked)
FEATURE [Part::Revolution] Revolve088  label="removeToCreateScrewAndThreadedInsertHole025"
  Angle = 360
  Axis = (0,1,0)
  Base = (0,0,0)
  FaceMakerClass = Part::FaceMakerBullseye
  Placement = pos=(30.3,30.3,51.7) rot=(0,0,1;0rad)
  Solid = false
  Source = -> Face084
  Symmetric = false
FEATURE [Part::MultiFuse] Fusion054  label="createThreadedInsertHolesForFan001"
  Shapes = -> [Revolve085,Revolve086,Revolve087,Revolve088]
FEATURE [Part::Cut] Cut018  label="top007"
  Base = -> Fusion040
  Tool = -> Fusion054
FEATURE [Sketcher::SketchObject] Sketch029
  FullyConstrained = false
  Placement = pos=(0,0,0) rot=(1,0,0;1.5708rad)
  sketch-geometry (24):
    g0: ArcOfCircle CenterX=-4 CenterY=-10.5 CenterZ=0 NormalX=0 NormalY=0 NormalZ=1 AngleXU=0 Radius=1.5 StartAngle=6e-16 EndAngle=3.14159
    g1: ArcOfCircle CenterX=-34.2 CenterY=-10.5 CenterZ=0 NormalX=0 NormalY=0 NormalZ=1 AngleXU=0 Radius=1.5 StartAngle=0 EndAngle=3.14159
    g2: ArcOfCircle CenterX=-34.2 CenterY=-27.7 CenterZ=0 NormalX=0 NormalY=0 NormalZ=1 AngleXU=0 Radius=1.5 StartAngle=3.14159 EndAngle=6.28319
    g3: ArcOfCircle CenterX=-4 CenterY=-27.7 CenterZ=0 NormalX=0 NormalY=0 NormalZ=1 AngleXU=0 Radius=1.5 StartAngle=3.1416 EndAngle=6.28319
    g4: ArcOfCircle CenterX=-10 CenterY=-4.3 CenterZ=0 NormalX=0 NormalY=0 NormalZ=1 AngleXU=0 Radius=1.5 StartAngle=2e-16 EndAngle=3.14159
    g5: ArcOfCircle CenterX=-16.1 CenterY=-1.8 CenterZ=0 NormalX=0 NormalY=0 NormalZ=1 AngleXU=0 Radius=1.5 StartAngle=5e-16 EndAngle=3.14159
    g6: ArcOfCircle CenterX=-22.1 CenterY=-1.8 CenterZ=0 NormalX=0 NormalY=0 NormalZ=1 AngleXU=0 Radius=1.5 StartAngle=5e-16 EndAngle=3.14159
    g7: ArcOfCircle CenterX=-28.2 CenterY=-4.3 CenterZ=0 NormalX=0 NormalY=0 NormalZ=1 AngleXU=0 Radius=1.5 StartAngle=2e-16 EndAngle=3.14159
    g8: ArcOfCircle CenterX=-10 CenterY=-33.9 CenterZ=0 NormalX=0 NormalY=0 NormalZ=1 AngleXU=0 Radius=1.5 StartAngle=3.14159 EndAngle=6.28319
    g9: ArcOfCircle CenterX=-16.1 CenterY=-36.4 CenterZ=0 NormalX=0 NormalY=0 NormalZ=1 AngleXU=0 Radius=1.5 StartAngle=3.14159 EndAngle=6.28319
    g10: ArcOfCircle CenterX=-22.1 CenterY=-36.4 CenterZ=0 NormalX=0 NormalY=0 NormalZ=1 AngleXU=0 Radius=1.5 StartAngle=3.14159 EndAngle=6.28319
    g11: ArcOfCircle CenterX=-28.2 CenterY=-33.9 CenterZ=0 NormalX=0 NormalY=0 NormalZ=1 AngleXU=0 Radius=1.5 StartAngle=3.14159 EndAngle=6.28319
    g12: LineSegment StartX=-35.7 StartY=-10.5 StartZ=0 EndX=-35.7 EndY=-27.7 EndZ=0
    g13: LineSegment StartX=-32.7 StartY=-10.5 StartZ=0 EndX=-32.7 EndY=-27.7 EndZ=0
    g14: LineSegment StartX=-29.7 StartY=-33.9 StartZ=0 EndX=-29.7 EndY=-4.3 EndZ=0
    g15: LineSegment StartX=-26.7 StartY=-33.9 StartZ=0 EndX=-26.7 EndY=-4.3 EndZ=0
    g16: LineSegment StartX=-2.5 StartY=-10.5 StartZ=0 EndX=-2.5 EndY=-27.7 EndZ=0
    g17: LineSegment StartX=-8.5 StartY=-4.3 StartZ=0 EndX=-8.5 EndY=-33.9 EndZ=0
    g18: LineSegment StartX=-5.5 StartY=-10.5 StartZ=0 EndX=-5.5 EndY=-27.7 EndZ=0
    g19: LineSegment StartX=-11.5 StartY=-4.3 StartZ=0 EndX=-11.5 EndY=-33.9 EndZ=0
    g20: LineSegment StartX=-14.6 StartY=-1.8 StartZ=0 EndX=-14.6 EndY=-36.4 EndZ=0
    g21: LineSegment StartX=-17.6 StartY=-1.8 StartZ=0 EndX=-17.6 EndY=-36.4 EndZ=0
    g22: LineSegment StartX=-20.6 StartY=-36.4 StartZ=0 EndX=-20.6 EndY=-1.8 EndZ=0
    g23: LineSegment StartX=-23.6 StartY=-1.8 StartZ=0 EndX=-23.6 EndY=-36.4 EndZ=0
  constraints (48):
    c: Block(g0)
    c: Block(g1)
    c: Block(g2)
    c: Block(g3)
    c: Block(g4)
    c: Block(g5)
    c: Block(g6)
    c: Block(g7)
    c: Block(g8)
    c: Block(g9)
    c: Block(g10)
    c: Block(g11)
    c: Coincident(g12,g1)
    c: Coincident(g12,g2)
    c: Vertical(g12)
    c: Coincident(g13,g1)
    c: Coincident(g13,g2)
    c: Vertical(g13)
    c: Coincident(g14,g11)
    c: Coincident(g14,g7)
    c: Vertical(g14)
    c: Coincident(g15,g11)
    c: Coincident(g15,g7)
    c: Vertical(g15)
    c: Coincident(g16,g0)
    c: Coincident(g16,g3)
    c: Vertical(g16)
    c: Coincident(g17,g4)
    c: Coincident(g17,g8)
    c: Vertical(g17)
    c: Coincident(g18,g0)
    c: Coincident(g18,g3)
    c: Vertical(g18)
    c: Coincident(g19,g4)
    c: Coincident(g19,g8)
    c: Vertical(g19)
    c: Coincident(g20,g5)
    c: Coincident(g20,g9)
    c: Vertical(g20)
    c: Coincident(g21,g5)
    c: Coincident(g21,g9)
    c: Vertical(g21)
    c: Coincident(g22,g10)
    c: Coincident(g22,g6)
    c: Vertical(g22)
    c: Coincident(g23,g6)
    c: Coincident(g23,g10)
    c: Vertical(g23)
FEATURE [Part::Extrusion] Extrude020  label="removeToCreateFanGrillHoles"
  Base = -> Sketch029
  Dir = (0,-1,6e-16)
  DirMode = 2
  FaceMakerClass = Part::FaceMakerBullseye
  LengthFwd = 10
  LengthRev = 0
  Placement = pos=(65.4,44,54.82) rot=(0,0,1;0rad)
  Solid = true
  Symmetric = false
FEATURE [Part::MultiFuse] Fusion055  label="top008"
  Shapes = -> [Cut017,Cut018]
FEATURE [Part::Cut] Cut019  label="top009"
  Base = -> Fusion055
  Tool = -> Extrude020
FEATURE [App::MeasureDistance] Distance003  label="Distance: 71.95 mm"
  Distance = 71.9513
  P1 = (117,38,72)
  P2 = (117,38,0.0487319)
FEATURE [Sketcher::SketchObject] Sketch030
  FullyConstrained = true
  Placement = pos=(117,19,0) rot=(0.57735,0.57735,0.57735;2.0944rad)
  sketch-geometry (48):
    g0: LineSegment StartX=-49.19 StartY=69.25 StartZ=0 EndX=-49.19 EndY=66.25 EndZ=0
    g1: LineSegment StartX=-49.19 StartY=63.5 StartZ=0 EndX=-49.19 EndY=60.5 EndZ=0
    g2: LineSegment StartX=-49.19 StartY=57.75 StartZ=0 EndX=-49.19 EndY=54.75 EndZ=0
    g3: LineSegment StartX=-49.19 StartY=52 StartZ=0 EndX=-49.19 EndY=49 EndZ=0
    g4: LineSegment StartX=-49.19 StartY=46.25 StartZ=0 EndX=-49.19 EndY=43.25 EndZ=0
    g5: LineSegment StartX=-49.19 StartY=40.5 StartZ=0 EndX=-49.19 EndY=37.5 EndZ=0
    g6: LineSegment StartX=-49.19 StartY=34.5 StartZ=0 EndX=-49.19 EndY=31.5 EndZ=0
    g7: LineSegment StartX=-49.19 StartY=28.75 StartZ=0 EndX=-49.19 EndY=25.75 EndZ=0
    g8: LineSegment StartX=-49.19 StartY=23 StartZ=0 EndX=-49.19 EndY=20 EndZ=0
    g9: LineSegment StartX=-49.19 StartY=17.25 StartZ=0 EndX=-49.19 EndY=14.25 EndZ=0
    g10: LineSegment StartX=-49.19 StartY=11.5 StartZ=0 EndX=-49.19 EndY=8.5 EndZ=0
    g11: LineSegment StartX=-49.19 StartY=5.75 StartZ=0 EndX=-49.19 EndY=2.75 EndZ=0
    g12: ArcOfCircle CenterX=-1.5 CenterY=67.75 CenterZ=0 NormalX=0 NormalY=0 NormalZ=1 AngleXU=0 Radius=1.5 StartAngle=4.71239 EndAngle=7.85398
    g13: ArcOfCircle CenterX=-1.5 CenterY=62 CenterZ=0 NormalX=0 NormalY=0 NormalZ=1 AngleXU=0 Radius=1.5 StartAngle=4.71239 EndAngle=7.85398
    g14: ArcOfCircle CenterX=-1.5 CenterY=56.25 CenterZ=0 NormalX=0 NormalY=0 NormalZ=1 AngleXU=0 Radius=1.5 StartAngle=4.71239 EndAngle=7.85398
    g15: ArcOfCircle CenterX=-11.49 CenterY=50.5 CenterZ=0 NormalX=0 NormalY=0 NormalZ=1 AngleXU=0 Radius=1.5 StartAngle=4.71239 EndAngle=7.85398
    g16: ArcOfCircle CenterX=-16.28 CenterY=44.75 CenterZ=0 NormalX=0 NormalY=0 NormalZ=1 AngleXU=0 Radius=1.5 StartAngle=4.71239 EndAngle=7.85398
    g17: ArcOfCircle CenterX=-18.2337 CenterY=39 CenterZ=0 NormalX=0 NormalY=0 NormalZ=1 AngleXU=0 Radius=1.5 StartAngle=4.71485 EndAngle=7.85398
    g18: ArcOfCircle CenterX=-16.2837 CenterY=27.25 CenterZ=0 NormalX=0 NormalY=0 NormalZ=1 AngleXU=0 Radius=1.5 StartAngle=4.71485 EndAngle=7.85398
    g19: ArcOfCircle CenterX=-18.2337 CenterY=33 CenterZ=0 NormalX=0 NormalY=0 NormalZ=1 AngleXU=0 Radius=1.5 StartAngle=4.71485 EndAngle=7.85398
    g20: ArcOfCircle CenterX=-11.49 CenterY=21.5 CenterZ=0 NormalX=0 NormalY=0 NormalZ=1 AngleXU=0 Radius=1.5 StartAngle=4.71239 EndAngle=7.85398
    g21: ArcOfCircle CenterX=-1.5 CenterY=4.25 CenterZ=0 NormalX=0 NormalY=0 NormalZ=1 AngleXU=0 Radius=1.5 StartAngle=4.71239 EndAngle=7.85398
    g22: ArcOfCircle CenterX=-1.5 CenterY=10 CenterZ=0 NormalX=0 NormalY=0 NormalZ=1 AngleXU=0 Radius=1.5 StartAngle=4.71239 EndAngle=7.85398
    g23: ArcOfCircle CenterX=-1.5 CenterY=15.75 CenterZ=0 NormalX=0 NormalY=0 NormalZ=1 AngleXU=0 Radius=1.5 StartAngle=4.71239 EndAngle=7.85398
    g24: LineSegment StartX=-49.19 StartY=69.25 StartZ=0 EndX=-1.5 EndY=69.25 EndZ=0
    g25: LineSegment StartX=-49.19 StartY=66.25 StartZ=0 EndX=-1.5 EndY=66.25 EndZ=0
    g26: LineSegment StartX=-49.19 StartY=63.5 StartZ=0 EndX=-1.5 EndY=63.5 EndZ=0
    g27: LineSegment StartX=-49.19 StartY=60.5 StartZ=0 EndX=-1.5 EndY=60.5 EndZ=0
    g28: LineSegment StartX=-49.19 StartY=57.75 StartZ=0 EndX=-1.5 EndY=57.75 EndZ=0
    g29: LineSegment StartX=-49.19 StartY=54.75 StartZ=0 EndX=-1.5 EndY=54.75 EndZ=0
    g30: LineSegment StartX=-49.19 StartY=52 StartZ=0 EndX=-11.49 EndY=52 EndZ=0
    g31: LineSegment StartX=-49.19 StartY=49 StartZ=0 EndX=-11.49 EndY=49 EndZ=0
    g32: LineSegment StartX=-49.19 StartY=46.25 StartZ=0 EndX=-16.28 EndY=46.25 EndZ=0
    g33: LineSegment StartX=-49.19 StartY=43.25 StartZ=0 EndX=-16.28 EndY=43.25 EndZ=0
    g34: LineSegment StartX=-49.19 StartY=40.5 StartZ=0 EndX=-18.2337 EndY=40.5 EndZ=0
    g35: LineSegment StartX=-49.19 StartY=37.5 StartZ=0 EndX=-18.23 EndY=37.5 EndZ=0
    g36: LineSegment StartX=-49.19 StartY=34.5 StartZ=0 EndX=-18.2337 EndY=34.5 EndZ=0
    g37: LineSegment StartX=-49.19 StartY=31.5 StartZ=0 EndX=-18.23 EndY=31.5 EndZ=0
    g38: LineSegment StartX=-49.19 StartY=28.75 StartZ=0 EndX=-16.2837 EndY=28.75 EndZ=0
    g39: LineSegment StartX=-49.19 StartY=25.75 StartZ=0 EndX=-16.28 EndY=25.75 EndZ=0
    g40: LineSegment StartX=-49.19 StartY=23 StartZ=0 EndX=-11.49 EndY=23 EndZ=0
    g41: LineSegment StartX=-49.19 StartY=20 StartZ=0 EndX=-11.49 EndY=20 EndZ=0
    g42: LineSegment StartX=-49.19 StartY=17.25 StartZ=0 EndX=-1.5 EndY=17.25 EndZ=0
    g43: LineSegment StartX=-49.19 StartY=14.25 StartZ=0 EndX=-1.5 EndY=14.25 EndZ=0
    g44: LineSegment StartX=-49.19 StartY=11.5 StartZ=0 EndX=-1.5 EndY=11.5 EndZ=0
    g45: LineSegment StartX=-49.19 StartY=8.5 StartZ=0 EndX=-1.5 EndY=8.5 EndZ=0
    g46: LineSegment StartX=-49.19 StartY=5.75 StartZ=0 EndX=-1.5 EndY=5.75 EndZ=0
    g47: LineSegment StartX=-49.19 StartY=2.75 StartZ=0 EndX=-1.5 EndY=2.75 EndZ=0
  constraints (120):
    c: Vertical(g0)
    c: Distance(g0) = 3
    c: Block(g0)
    c: Vertical(g1)
    c: Distance(g1) = 3
    c: Vertical(g2)
    c: Equal(g0,g2) = 3
    c: Block(g2)
    c: Vertical(g3)
    c: Equal(g1,g3) = 3
    c: Vertical(g4)
    c: Equal(g0,g4) = 3
    c: Block(g4)
    c: Vertical(g5)
    c: Equal(g1,g5) = 3
    c: Vertical(g6)
    c: Equal(g0,g6) = 3
    c: Block(g6)
    c: Vertical(g7)
    c: Equal(g1,g7) = 3
    c: Vertical(g8)
    c: Equal(g0,g8) = 3
    c: Block(g8)
    c: Vertical(g9)
    c: Equal(g1,g9) = 3
    c: Vertical(g10)
    c: Equal(g0,g10) = 3
    c: Block(g10)
    c: Vertical(g11)
    c: Equal(g1,g11) = 3
    c: Block(g12)
    c: Block(g13)
    c: Block(g14)
    c: Block(g15)
    c: Block(g16)
    c: Block(g17)
    c: Block(g18)
    c: Block(g19)
    c: Block(g20)
    c: Block(g21)
    c: Block(g22)
    c: Block(g23)
    c: Block(g11)
    c: Block(g9)
    c: Block(g7)
    c: Block(g5)
    c: Block(g3)
    c: Block(g1)
    c: Coincident(g24,g0)
    c: Coincident(g24,g12)
    c: Horizontal(g24)
    c: Coincident(g25,g0)
    c: Coincident(g25,g12)
    c: Horizontal(g25)
    c: Coincident(g26,g1)
    c: Coincident(g26,g13)
    c: Horizontal(g26)
    c: Coincident(g27,g1)
    c: Coincident(g27,g13)
    c: Horizontal(g27)
    c: Coincident(g28,g2)
    c: Coincident(g28,g14)
    c: Horizontal(g28)
    c: Coincident(g29,g2)
    c: Coincident(g29,g14)
    c: Horizontal(g29)
    c: Coincident(g30,g3)
    c: Coincident(g30,g15)
    c: Horizontal(g30)
    c: Coincident(g31,g3)
    c: Coincident(g31,g15)
    c: Horizontal(g31)
    c: Coincident(g32,g4)
    c: Coincident(g32,g16)
    c: Horizontal(g32)
    c: Coincident(g33,g4)
    c: Coincident(g33,g16)
    c: Horizontal(g33)
    c: Coincident(g34,g5)
    c: Coincident(g34,g17)
    c: Horizontal(g34)
    c: Coincident(g35,g5)
    c: Coincident(g35,g17)
    c: Horizontal(g35)
    c: Coincident(g36,g6)
    c: Coincident(g36,g19)
    c: Horizontal(g36)
    c: Coincident(g37,g6)
    c: Coincident(g37,g19)
    c: Horizontal(g37)
    c: Coincident(g38,g7)
    c: Coincident(g38,g18)
    c: Horizontal(g38)
    c: Coincident(g39,g7)
    c: Coincident(g39,g18)
    c: Horizontal(g39)
    c: Coincident(g40,g8)
    c: Coincident(g40,g20)
    c: Horizontal(g40)
    c: Coincident(g41,g8)
    c: Coincident(g41,g20)
    c: Horizontal(g41)
    c: Coincident(g42,g9)
    c: Coincident(g42,g23)
    c: Horizontal(g42)
    c: Coincident(g43,g9)
    c: Coincident(g43,g23)
    c: Horizontal(g43)
    c: Coincident(g44,g10)
    c: Coincident(g44,g22)
    c: Horizontal(g44)
    c: Coincident(g45,g10)
    c: Coincident(g45,g22)
    c: Horizontal(g45)
    c: Coincident(g46,g11)
    c: Coincident(g46,g21)
    c: Horizontal(g46)
    c: Coincident(g47,g11)
    c: Coincident(g47,g21)
    c: Horizontal(g47)
FEATURE [Sketcher::SketchObject] Sketch031
  FullyConstrained = true
  Placement = pos=(117,19,0) rot=(0.57735,0.57735,0.57735;2.0944rad)
  sketch-geometry (24):
    g0: ArcOfCircle CenterX=-49.19 CenterY=67.75 CenterZ=0 NormalX=0 NormalY=0 NormalZ=1 AngleXU=0 Radius=1.5 StartAngle=1.5708 EndAngle=4.71239
    g1: ArcOfCircle CenterX=-49.19 CenterY=62 CenterZ=0 NormalX=0 NormalY=0 NormalZ=1 AngleXU=0 Radius=1.5 StartAngle=1.5708 EndAngle=4.71239
    g2: ArcOfCircle CenterX=-49.19 CenterY=56.25 CenterZ=0 NormalX=0 NormalY=0 NormalZ=1 AngleXU=0 Radius=1.5 StartAngle=1.5708 EndAngle=4.71239
    g3: ArcOfCircle CenterX=-49.19 CenterY=50.5 CenterZ=0 NormalX=0 NormalY=0 NormalZ=1 AngleXU=0 Radius=1.5 StartAngle=1.5708 EndAngle=4.71239
    g4: ArcOfCircle CenterX=-49.19 CenterY=44.75 CenterZ=0 NormalX=0 NormalY=0 NormalZ=1 AngleXU=0 Radius=1.5 StartAngle=1.5708 EndAngle=4.71239
    g5: ArcOfCircle CenterX=-49.19 CenterY=39 CenterZ=0 NormalX=0 NormalY=0 NormalZ=1 AngleXU=0 Radius=1.5 StartAngle=1.5708 EndAngle=4.71239
    g6: ArcOfCircle CenterX=-49.19 CenterY=33 CenterZ=0 NormalX=0 NormalY=0 NormalZ=1 AngleXU=0 Radius=1.5 StartAngle=1.5708 EndAngle=4.71239
    g7: ArcOfCircle CenterX=-49.19 CenterY=27.25 CenterZ=0 NormalX=0 NormalY=0 NormalZ=1 AngleXU=0 Radius=1.5 StartAngle=1.5708 EndAngle=4.71239
    g8: ArcOfCircle CenterX=-49.19 CenterY=21.5 CenterZ=0 NormalX=0 NormalY=0 NormalZ=1 AngleXU=0 Radius=1.5 StartAngle=1.5708 EndAngle=4.71239
    g9: ArcOfCircle CenterX=-49.19 CenterY=15.75 CenterZ=0 NormalX=0 NormalY=0 NormalZ=1 AngleXU=0 Radius=1.5 StartAngle=1.5708 EndAngle=4.71239
    g10: ArcOfCircle CenterX=-49.19 CenterY=10 CenterZ=0 NormalX=0 NormalY=0 NormalZ=1 AngleXU=0 Radius=1.5 StartAngle=1.5708 EndAngle=4.71239
    g11: ArcOfCircle CenterX=-49.19 CenterY=4.25 CenterZ=0 NormalX=0 NormalY=0 NormalZ=1 AngleXU=0 Radius=1.5 StartAngle=1.5708 EndAngle=4.71239
    g12: LineSegment StartX=-49.19 StartY=69.25 StartZ=0 EndX=-49.19 EndY=66.25 EndZ=0
    g13: LineSegment StartX=-49.19 StartY=63.5 StartZ=0 EndX=-49.19 EndY=60.5 EndZ=0
    g14: LineSegment StartX=-49.19 StartY=57.75 StartZ=0 EndX=-49.19 EndY=54.75 EndZ=0
    g15: LineSegment StartX=-49.19 StartY=52 StartZ=0 EndX=-49.19 EndY=49 EndZ=0
    g16: LineSegment StartX=-49.19 StartY=46.25 StartZ=0 EndX=-49.19 EndY=43.25 EndZ=0
    g17: LineSegment StartX=-49.19 StartY=40.5 StartZ=0 EndX=-49.19 EndY=37.5 EndZ=0
    g18: LineSegment StartX=-49.19 StartY=34.5 StartZ=0 EndX=-49.19 EndY=31.5 EndZ=0
    g19: LineSegment StartX=-49.19 StartY=28.75 StartZ=0 EndX=-49.19 EndY=25.75 EndZ=0
    g20: LineSegment StartX=-49.19 StartY=23 StartZ=0 EndX=-49.19 EndY=20 EndZ=0
    g21: LineSegment StartX=-49.19 StartY=17.25 StartZ=0 EndX=-49.19 EndY=14.25 EndZ=0
    g22: LineSegment StartX=-49.19 StartY=11.5 StartZ=0 EndX=-49.19 EndY=8.5 EndZ=0
    g23: LineSegment StartX=-49.19 StartY=5.75 StartZ=0 EndX=-49.19 EndY=2.75 EndZ=0
  constraints (48):
    c: Block(g0)
    c: Block(g1)
    c: Block(g2)
    c: Block(g3)
    c: Block(g4)
    c: Block(g5)
    c: Block(g6)
    c: Block(g7)
    c: Block(g8)
    c: Block(g9)
    c: Block(g10)
    c: Block(g11)
    c: Coincident(g12,g0)
    c: Coincident(g12,g0)
    c: Vertical(g12)
    c: Vertical(g13)
    c: Coincident(g13,g1)
    c: Vertical(g14)
    c: Coincident(g14,g2)
    c: Vertical(g15)
    c: Coincident(g15,g3)
    c: Vertical(g16)
    c: Coincident(g16,g4)
    c: Vertical(g17)
    c: Coincident(g17,g5)
    c: Vertical(g18)
    c: Coincident(g18,g6)
    c: Vertical(g19)
    c: Coincident(g19,g7)
    c: Vertical(g20)
    c: Coincident(g20,g8)
    c: Vertical(g21)
    c: Coincident(g21,g9)
    c: Vertical(g22)
    c: Coincident(g22,g10)
    c: Vertical(g23)
    c: Coincident(g23,g11)
    c: Block(g23)
    c: Block(g22)
    c: Block(g21)
    c: Block(g20)
    c: Block(g13)
    c: Block(g14)
    c: Block(g15)
    c: Block(g16)
    c: Block(g17)
    c: Block(g18)
    c: Block(g19)
FEATURE [Part::Extrusion] Extrude022
  Base = -> Sketch030
  Dir = (1,-2e-16,2e-16)
  DirMode = 2
  FaceMakerClass = Part::FaceMakerBullseye
  LengthFwd = 19
  LengthRev = 0
  Placement = pos=(-19,0,0) rot=(0,0,1;0rad)
  Solid = true
  Symmetric = false
FEATURE [Part::Fillet] Fillet022
  Base = -> Extrude022
  Edges = 24 edges r=1.49: [Edge6,Edge11,Edge18,Edge23,Edge30,Edge35,Edge42,Edge47,Edge54,Edge59,Edge66,Edge71,Edge78,Edge83,Edge90,Edge95,Edge102,Edge107,Edge114,Edge119,Edge126,Edge131,Edge138,Edge143]
FEATURE [Part::Cut] Cut020  label="top010"
  Base = -> Cut019
  Tool = -> Fillet022
FEATURE [Sketcher::SketchObject] Sketch032
  FullyConstrained = true
  Placement = pos=(117,19,0) rot=(0.57735,0.57735,0.57735;2.0944rad)
  sketch-geometry (48):
    g0: LineSegment StartX=-49.19 StartY=69.25 StartZ=0 EndX=-49.19 EndY=66.25 EndZ=0
    g1: LineSegment StartX=-49.19 StartY=63.5 StartZ=0 EndX=-49.19 EndY=60.5 EndZ=0
    g2: LineSegment StartX=-49.19 StartY=57.75 StartZ=0 EndX=-49.19 EndY=54.75 EndZ=0
    g3: LineSegment StartX=-49.19 StartY=52 StartZ=0 EndX=-49.19 EndY=49 EndZ=0
    g4: LineSegment StartX=-49.19 StartY=46.25 StartZ=0 EndX=-49.19 EndY=43.25 EndZ=0
    g5: LineSegment StartX=-49.19 StartY=40.5 StartZ=0 EndX=-49.19 EndY=37.5 EndZ=0
    g6: LineSegment StartX=-49.19 StartY=34.5 StartZ=0 EndX=-49.19 EndY=31.5 EndZ=0
    g7: LineSegment StartX=-49.19 StartY=28.75 StartZ=0 EndX=-49.19 EndY=25.75 EndZ=0
    g8: LineSegment StartX=-49.19 StartY=23 StartZ=0 EndX=-49.19 EndY=20 EndZ=0
    g9: LineSegment StartX=-49.19 StartY=17.25 StartZ=0 EndX=-49.19 EndY=14.25 EndZ=0
    g10: LineSegment StartX=-49.19 StartY=11.5 StartZ=0 EndX=-49.19 EndY=8.5 EndZ=0
    g11: LineSegment StartX=-49.19 StartY=5.75 StartZ=0 EndX=-49.19 EndY=2.75 EndZ=0
    g12: ArcOfCircle CenterX=-1.5 CenterY=67.75 CenterZ=0 NormalX=0 NormalY=0 NormalZ=1 AngleXU=0 Radius=1.5 StartAngle=4.71239 EndAngle=7.85398
    g13: ArcOfCircle CenterX=-1.5 CenterY=62 CenterZ=0 NormalX=0 NormalY=0 NormalZ=1 AngleXU=0 Radius=1.5 StartAngle=4.71239 EndAngle=7.85398
    g14: ArcOfCircle CenterX=-1.5 CenterY=56.25 CenterZ=0 NormalX=0 NormalY=0 NormalZ=1 AngleXU=0 Radius=1.5 StartAngle=4.71239 EndAngle=7.85398
    g15: ArcOfCircle CenterX=-11.49 CenterY=50.5 CenterZ=0 NormalX=0 NormalY=0 NormalZ=1 AngleXU=0 Radius=1.5 StartAngle=4.71239 EndAngle=7.85398
    g16: ArcOfCircle CenterX=-16.28 CenterY=44.75 CenterZ=0 NormalX=0 NormalY=0 NormalZ=1 AngleXU=0 Radius=1.5 StartAngle=4.71239 EndAngle=7.85398
    g17: ArcOfCircle CenterX=-18.2337 CenterY=39 CenterZ=0 NormalX=0 NormalY=0 NormalZ=1 AngleXU=0 Radius=1.5 StartAngle=4.71485 EndAngle=7.85398
    g18: ArcOfCircle CenterX=-16.2837 CenterY=27.25 CenterZ=0 NormalX=0 NormalY=0 NormalZ=1 AngleXU=0 Radius=1.5 StartAngle=4.71485 EndAngle=7.85398
    g19: ArcOfCircle CenterX=-18.2337 CenterY=33 CenterZ=0 NormalX=0 NormalY=0 NormalZ=1 AngleXU=0 Radius=1.5 StartAngle=4.71485 EndAngle=7.85398
    g20: ArcOfCircle CenterX=-11.49 CenterY=21.5 CenterZ=0 NormalX=0 NormalY=0 NormalZ=1 AngleXU=0 Radius=1.5 StartAngle=4.71239 EndAngle=7.85398
    g21: ArcOfCircle CenterX=-1.5 CenterY=4.25 CenterZ=0 NormalX=0 NormalY=0 NormalZ=1 AngleXU=0 Radius=1.5 StartAngle=4.71239 EndAngle=7.85398
    g22: ArcOfCircle CenterX=-1.5 CenterY=10 CenterZ=0 NormalX=0 NormalY=0 NormalZ=1 AngleXU=0 Radius=1.5 StartAngle=4.71239 EndAngle=7.85398
    g23: ArcOfCircle CenterX=-1.5 CenterY=15.75 CenterZ=0 NormalX=0 NormalY=0 NormalZ=1 AngleXU=0 Radius=1.5 StartAngle=4.71239 EndAngle=7.85398
    g24: LineSegment StartX=-49.19 StartY=69.25 StartZ=0 EndX=-1.5 EndY=69.25 EndZ=0
    g25: LineSegment StartX=-49.19 StartY=66.25 StartZ=0 EndX=-1.5 EndY=66.25 EndZ=0
    g26: LineSegment StartX=-49.19 StartY=63.5 StartZ=0 EndX=-1.5 EndY=63.5 EndZ=0
    g27: LineSegment StartX=-49.19 StartY=60.5 StartZ=0 EndX=-1.5 EndY=60.5 EndZ=0
    g28: LineSegment StartX=-49.19 StartY=57.75 StartZ=0 EndX=-1.5 EndY=57.75 EndZ=0
    g29: LineSegment StartX=-49.19 StartY=54.75 StartZ=0 EndX=-1.5 EndY=54.75 EndZ=0
    g30: LineSegment StartX=-49.19 StartY=52 StartZ=0 EndX=-11.49 EndY=52 EndZ=0
    g31: LineSegment StartX=-49.19 StartY=49 StartZ=0 EndX=-11.49 EndY=49 EndZ=0
    g32: LineSegment StartX=-49.19 StartY=46.25 StartZ=0 EndX=-16.28 EndY=46.25 EndZ=0
    g33: LineSegment StartX=-49.19 StartY=43.25 StartZ=0 EndX=-16.28 EndY=43.25 EndZ=0
    g34: LineSegment StartX=-49.19 StartY=40.5 StartZ=0 EndX=-18.2337 EndY=40.5 EndZ=0
    g35: LineSegment StartX=-49.19 StartY=37.5 StartZ=0 EndX=-18.23 EndY=37.5 EndZ=0
    g36: LineSegment StartX=-49.19 StartY=34.5 StartZ=0 EndX=-18.2337 EndY=34.5 EndZ=0
    g37: LineSegment StartX=-49.19 StartY=31.5 StartZ=0 EndX=-18.23 EndY=31.5 EndZ=0
    g38: LineSegment StartX=-49.19 StartY=28.75 StartZ=0 EndX=-16.2837 EndY=28.75 EndZ=0
    g39: LineSegment StartX=-49.19 StartY=25.75 StartZ=0 EndX=-16.28 EndY=25.75 EndZ=0
    g40: LineSegment StartX=-49.19 StartY=23 StartZ=0 EndX=-11.49 EndY=23 EndZ=0
    g41: LineSegment StartX=-49.19 StartY=20 StartZ=0 EndX=-11.49 EndY=20 EndZ=0
    g42: LineSegment StartX=-49.19 StartY=17.25 StartZ=0 EndX=-1.5 EndY=17.25 EndZ=0
    g43: LineSegment StartX=-49.19 StartY=14.25 StartZ=0 EndX=-1.5 EndY=14.25 EndZ=0
    g44: LineSegment StartX=-49.19 StartY=11.5 StartZ=0 EndX=-1.5 EndY=11.5 EndZ=0
    g45: LineSegment StartX=-49.19 StartY=8.5 StartZ=0 EndX=-1.5 EndY=8.5 EndZ=0
    g46: LineSegment StartX=-49.19 StartY=5.75 StartZ=0 EndX=-1.5 EndY=5.75 EndZ=0
    g47: LineSegment StartX=-49.19 StartY=2.75 StartZ=0 EndX=-1.5 EndY=2.75 EndZ=0
  constraints (120):
    c: Vertical(g0)
    c: Distance(g0) = 3
    c: Block(g0)
    c: Vertical(g1)
    c: Distance(g1) = 3
    c: Vertical(g2)
    c: Equal(g0,g2) = 3
    c: Block(g2)
    c: Vertical(g3)
    c: Equal(g1,g3) = 3
    c: Vertical(g4)
    c: Equal(g0,g4) = 3
    c: Block(g4)
    c: Vertical(g5)
    c: Equal(g1,g5) = 3
    c: Vertical(g6)
    c: Equal(g0,g6) = 3
    c: Block(g6)
    c: Vertical(g7)
    c: Equal(g1,g7) = 3
    c: Vertical(g8)
    c: Equal(g0,g8) = 3
    c: Block(g8)
    c: Vertical(g9)
    c: Equal(g1,g9) = 3
    c: Vertical(g10)
    c: Equal(g0,g10) = 3
    c: Block(g10)
    c: Vertical(g11)
    c: Equal(g1,g11) = 3
    c: Block(g12)
    c: Block(g13)
    c: Block(g14)
    c: Block(g15)
    c: Block(g16)
    c: Block(g17)
    c: Block(g18)
    c: Block(g19)
    c: Block(g20)
    c: Block(g21)
    c: Block(g22)
    c: Block(g23)
    c: Block(g11)
    c: Block(g9)
    c: Block(g7)
    c: Block(g5)
    c: Block(g3)
    c: Block(g1)
    c: Coincident(g24,g0)
    c: Coincident(g24,g12)
    c: Horizontal(g24)
    c: Coincident(g25,g0)
    c: Coincident(g25,g12)
    c: Horizontal(g25)
    c: Coincident(g26,g1)
    c: Coincident(g26,g13)
    c: Horizontal(g26)
    c: Coincident(g27,g1)
    c: Coincident(g27,g13)
    c: Horizontal(g27)
    c: Coincident(g28,g2)
    c: Coincident(g28,g14)
    c: Horizontal(g28)
    c: Coincident(g29,g2)
    c: Coincident(g29,g14)
    c: Horizontal(g29)
    c: Coincident(g30,g3)
    c: Coincident(g30,g15)
    c: Horizontal(g30)
    c: Coincident(g31,g3)
    c: Coincident(g31,g15)
    c: Horizontal(g31)
    c: Coincident(g32,g4)
    c: Coincident(g32,g16)
    c: Horizontal(g32)
    c: Coincident(g33,g4)
    c: Coincident(g33,g16)
    c: Horizontal(g33)
    c: Coincident(g34,g5)
    c: Coincident(g34,g17)
    c: Horizontal(g34)
    c: Coincident(g35,g5)
    c: Coincident(g35,g17)
    c: Horizontal(g35)
    c: Coincident(g36,g6)
    c: Coincident(g36,g19)
    c: Horizontal(g36)
    c: Coincident(g37,g6)
    c: Coincident(g37,g19)
    c: Horizontal(g37)
    c: Coincident(g38,g7)
    c: Coincident(g38,g18)
    c: Horizontal(g38)
    c: Coincident(g39,g7)
    c: Coincident(g39,g18)
    c: Horizontal(g39)
    c: Coincident(g40,g8)
    c: Coincident(g40,g20)
    c: Horizontal(g40)
    c: Coincident(g41,g8)
    c: Coincident(g41,g20)
    c: Horizontal(g41)
    c: Coincident(g42,g9)
    c: Coincident(g42,g23)
    c: Horizontal(g42)
    c: Coincident(g43,g9)
    c: Coincident(g43,g23)
    c: Horizontal(g43)
    c: Coincident(g44,g10)
    c: Coincident(g44,g22)
    c: Horizontal(g44)
    c: Coincident(g45,g10)
    c: Coincident(g45,g22)
    c: Horizontal(g45)
    c: Coincident(g46,g11)
    c: Coincident(g46,g21)
    c: Horizontal(g46)
    c: Coincident(g47,g11)
    c: Coincident(g47,g21)
    c: Horizontal(g47)
FEATURE [Part::Extrusion] Extrude023
  Base = -> Sketch032
  Dir = (1,-2e-16,2e-16)
  DirMode = 2
  FaceMakerClass = Part::FaceMakerBullseye
  LengthFwd = 19
  LengthRev = 0
  Placement = pos=(-19,0,0) rot=(0,0,1;0rad)
  Solid = true
  Symmetric = false
FEATURE [Part::Fillet] Fillet023
  Base = -> Extrude023
  Edges = <same value as first occurrence — deduplicated (x6 in doc)>
  Placement = pos=(0,0.05,0) rot=(0,0,1;0rad)
FEATURE [Part::Cut] Cut014  label="bottom003"
  Base = -> Cut007
  Tool = -> Fusion047
FEATURE [Part::Cut] Cut021  label="bottom004"
  Base = -> Cut014
  Tool = -> Fillet023
FEATURE [Sketcher::SketchObject] Sketch033
  FullyConstrained = true
  Placement = pos=(117,19,0) rot=(0.57735,0.57735,0.57735;2.0944rad)
  sketch-geometry (8):
    g0: LineSegment StartX=-49.19 StartY=69.25 StartZ=0 EndX=-49.19 EndY=66.25 EndZ=0
    g1: LineSegment StartX=-49.19 StartY=5.75 StartZ=0 EndX=-49.19 EndY=2.75 EndZ=0
    g2: ArcOfCircle CenterX=-1.5 CenterY=67.75 CenterZ=0 NormalX=0 NormalY=0 NormalZ=1 AngleXU=0 Radius=1.5 StartAngle=4.71239 EndAngle=7.85398
    g3: ArcOfCircle CenterX=-1.5 CenterY=4.25 CenterZ=0 NormalX=0 NormalY=0 NormalZ=1 AngleXU=0 Radius=1.5 StartAngle=4.71239 EndAngle=7.85398
    g4: LineSegment StartX=-49.19 StartY=69.25 StartZ=0 EndX=-1.5 EndY=69.25 EndZ=0
    g5: LineSegment StartX=-49.19 StartY=66.25 StartZ=0 EndX=-1.5 EndY=66.25 EndZ=0
    g6: LineSegment StartX=-49.19 StartY=5.75 StartZ=0 EndX=-1.5 EndY=5.75 EndZ=0
    g7: LineSegment StartX=-49.19 StartY=2.75 StartZ=0 EndX=-1.5 EndY=2.75 EndZ=0
  constraints (19):
    c: Vertical(g0)
    c: Distance(g0) = 3
    c: Block(g0)
    c: Vertical(g1)
    c: Block(g2)
    c: Block(g3)
    c: Block(g1)
    c: Coincident(g4,g0)
    c: Coincident(g4,g2)
    c: Horizontal(g4)
    c: Coincident(g5,g0)
    c: Coincident(g5,g2)
    c: Horizontal(g5)
    c: Coincident(g6,g1)
    c: Coincident(g6,g3)
    c: Horizontal(g6)
    c: Coincident(g7,g1)
    c: Coincident(g7,g3)
    c: Horizontal(g7)
FEATURE [Sketcher::SketchObject] Sketch034
  FullyConstrained = true
  Placement = pos=(117,19,0) rot=(0.57735,0.57735,0.57735;2.0944rad)
  sketch-geometry (8):
    g0: LineSegment StartX=-49.19 StartY=63.5 StartZ=0 EndX=-49.19 EndY=60.5 EndZ=0
    g1: LineSegment StartX=-49.19 StartY=11.5 StartZ=0 EndX=-49.19 EndY=8.5 EndZ=0
    g2: ArcOfCircle CenterX=-1.5 CenterY=62 CenterZ=0 NormalX=0 NormalY=0 NormalZ=1 AngleXU=0 Radius=1.5 StartAngle=4.71239 EndAngle=7.85398
    g3: ArcOfCircle CenterX=-1.5 CenterY=10 CenterZ=0 NormalX=0 NormalY=0 NormalZ=1 AngleXU=0 Radius=1.5 StartAngle=4.71239 EndAngle=7.85398
    g4: LineSegment StartX=-49.19 StartY=63.5 StartZ=0 EndX=-1.5 EndY=63.5 EndZ=0
    g5: LineSegment StartX=-49.19 StartY=60.5 StartZ=0 EndX=-1.5 EndY=60.5 EndZ=0
    g6: LineSegment StartX=-49.19 StartY=11.5 StartZ=0 EndX=-1.5 EndY=11.5 EndZ=0
    g7: LineSegment StartX=-49.19 StartY=8.5 StartZ=0 EndX=-1.5 EndY=8.5 EndZ=0
  constraints (19):
    c: Vertical(g0)
    c: Distance(g0) = 3
    c: Vertical(g1)
    c: Block(g1)
    c: Block(g2)
    c: Block(g3)
    c: Block(g0)
    c: Coincident(g4,g0)
    c: Coincident(g4,g2)
    c: Horizontal(g4)
    c: Coincident(g5,g0)
    c: Coincident(g5,g2)
    c: Horizontal(g5)
    c: Coincident(g6,g1)
    c: Coincident(g6,g3)
    c: Horizontal(g6)
    c: Coincident(g7,g1)
    c: Coincident(g7,g3)
    c: Horizontal(g7)
FEATURE [Part::Extrusion] Extrude024
  Base = -> Sketch033
  Dir = (1,0,0)
  DirMode = 2
  FaceMakerClass = Part::FaceMakerBullseye
  LengthFwd = 10
  LengthRev = 0
  Solid = true
  Symmetric = false
FEATURE [Part::Extrusion] Extrude025
  Base = -> Sketch034
  Dir = (1,0,0)
  DirMode = 2
  FaceMakerClass = Part::FaceMakerBullseye
  LengthFwd = 10
  LengthRev = 0
  Solid = true
  Symmetric = false
FEATURE [Part::Fillet] Fillet024  label="removeFromtMoreFrontCaseScrewRetainers"
  Base = -> Extrude024
  Edges = 4 edges r=1.49: [Edge6,Edge11,Edge18,Edge23]
  Placement = pos=(-11,0,0) rot=(0,0,1;0rad)
FEATURE [Part::Fillet] Fillet025  label="removeFromtMoreFrontCaseScrewRetainers001"
  Base = -> Extrude025
  Edges = 4 edges r=1.49: [Edge6,Edge11,Edge18,Edge23]
  Placement = pos=(-19,0,0) rot=(0,0,1;0rad)
FEATURE [Part::Cut] Cut022
  Base = -> Cut015
  Tool = -> Fillet025
FEATURE [Part::Cut] Cut023  label="screwRetainers"
  Base = -> Cut022
  Tool = -> Fillet024
FEATURE [Part::MultiFuse] Fusion056  label="bottom005"
  Shapes = -> [Fusion044,Cut021]
FEATURE [Part::MultiFuse] Fusion057  label="casePillars001"
  Shapes = -> [Cut016,Fusion052]
FEATURE [Part::MultiFuse] Fusion058  label="bottom006"
  Shapes = -> [Fusion056,Cut023]
FEATURE [Part::MultiFuse] Fusion059  label="bottom007"
  Shapes = -> [Fusion058,Fillet005]
FEATURE [Part::MultiFuse] Fusion060  label="bottom008"
  Shapes = -> [Fusion059,Fusion]
FEATURE [Part::MultiFuse] Fusion061  label="top011"
  Shapes = -> [Cut006,Cut020]
FEATURE [Part::MultiFuse] Fusion062  label="top012"
  Shapes = -> [Fusion057,Fusion061]
FEATURE [Sketcher::SketchObject] Sketch035  label="topSketch007"
  FullyConstrained = true
  sketch-geometry (6):
    g0: LineSegment StartX=19 StartY=38 StartZ=0 EndX=117 EndY=38 EndZ=0
    g1: ArcOfCircle CenterX=19 CenterY=19 CenterZ=0 NormalX=0 NormalY=0 NormalZ=1 AngleXU=0 Radius=19 StartAngle=1.5708 EndAngle=3.14159
    g2: LineSegment StartX=117 StartY=38 StartZ=0 EndX=117 EndY=19 EndZ=0
    g3: LineSegment StartX=98 StartY=1.0161e-12 StartZ=0 EndX=5.22862e-06 EndY=1.0161e-12 EndZ=0
    g4: LineSegment StartX=5.22862e-06 StartY=19 StartZ=0 EndX=5.22862e-06 EndY=1.0161e-12 EndZ=0
    g5: ArcOfCircle CenterX=98 CenterY=19 CenterZ=0 NormalX=0 NormalY=0 NormalZ=1 AngleXU=0 Radius=19 StartAngle=4.71239 EndAngle=6.28319
  constraints (16):
    c: Horizontal(g0)
    c: Distance(g0) = 98
    c: Coincident(g1,g0)
    c: Block(g1)
    c: Coincident(g2,g0)
    c: Vertical(g2)
    c: Distance(g2) = 19
    c: Horizontal(g3)
    c: Coincident(g4,g1)
    c: Vertical(g4)
    c: Coincident(g3,g4)
    c: Block(g3)
    c: Coincident(g5,g2)
    c: Coincident(g5,g3)
    c: Block(g0)
    c: Block(g5)
FEATURE [Part::Extrusion] Extrude026  label="sideA001"
  Base = -> Sketch035
  Dir = (0,0,1)
  DirMode = 2
  FaceMakerClass = Part::FaceMakerBullseye
  LengthFwd = 3
  LengthRev = 0
  Placement = pos=(0,0,-2.7) rot=(0,0,1;0rad)
  Solid = true
  Symmetric = false
FEATURE [Sketcher::SketchObject] Sketch036  label="topSketch008"
  FullyConstrained = true
  sketch-geometry (6):
    g0: LineSegment StartX=19 StartY=38 StartZ=0 EndX=117 EndY=38 EndZ=0
    g1: ArcOfCircle CenterX=19 CenterY=19 CenterZ=0 NormalX=0 NormalY=0 NormalZ=1 AngleXU=0 Radius=19 StartAngle=1.5708 EndAngle=3.14159
    g2: LineSegment StartX=117 StartY=38 StartZ=0 EndX=117 EndY=19 EndZ=0
    g3: LineSegment StartX=98 StartY=1.0161e-12 StartZ=0 EndX=5.22862e-06 EndY=1.0161e-12 EndZ=0
    g4: LineSegment StartX=5.22862e-06 StartY=19 StartZ=0 EndX=5.22862e-06 EndY=1.0161e-12 EndZ=0
    g5: ArcOfCircle CenterX=98 CenterY=19 CenterZ=0 NormalX=0 NormalY=0 NormalZ=1 AngleXU=0 Radius=19 StartAngle=4.71239 EndAngle=6.28319
  constraints (16):
    c: Horizontal(g0)
    c: Distance(g0) = 98
    c: Coincident(g1,g0)
    c: Block(g1)
    c: Coincident(g2,g0)
    c: Vertical(g2)
    c: Distance(g2) = 19
    c: Horizontal(g3)
    c: Coincident(g4,g1)
    c: Vertical(g4)
    c: Coincident(g3,g4)
    c: Block(g3)
    c: Coincident(g5,g2)
    c: Coincident(g5,g3)
    c: Block(g0)
    c: Block(g5)
FEATURE [Part::Extrusion] Extrude027  label="sideB001"
  Base = -> Sketch036
  Dir = (0,0,1)
  DirMode = 2
  FaceMakerClass = Part::FaceMakerBullseye
  LengthFwd = 3
  LengthRev = 0
  Placement = pos=(0,0,71.7) rot=(0,0,1;0rad)
  Solid = true
  Symmetric = false
FEATURE [Part::MultiFuse] Fusion064  label="removeFromBottom"
  Shapes = -> [Extrude026,Extrude027]
FEATURE [Part::Cut] Cut024  label="bottom009"
  Base = -> Fusion060
  Tool = -> Fusion064
FEATURE [Sketcher::SketchObject] Sketch037  label="topSketch009"
  FullyConstrained = true
  sketch-geometry (8):
    g0: ArcOfCircle CenterX=19 CenterY=19.1201 CenterZ=0 NormalX=0 NormalY=0 NormalZ=1 AngleXU=0 Radius=18.8799 StartAngle=1.5708 EndAngle=3.14793
    g1: LineSegment StartX=0.120501 StartY=19.0004 StartZ=0 EndX=0.120501 EndY=0.000382114 EndZ=0
    g2: LineSegment StartX=19 StartY=38 StartZ=0 EndX=124 EndY=38 EndZ=0
    g3: LineSegment StartX=0.120501 StartY=0.000382114 StartZ=0 EndX=105.121 EndY=0.000382114 EndZ=0
    g4: LineSegment StartX=124 StartY=38 StartZ=0 EndX=125.616 EndY=38 EndZ=0
    g5: LineSegment StartX=105.121 StartY=0.000382114 StartZ=0 EndX=106.736 EndY=0.000382114 EndZ=0
    g6: ArcOfCircle CenterX=106.616 CenterY=19 CenterZ=0 NormalX=0 NormalY=0 NormalZ=1 AngleXU=0 Radius=19 StartAngle=4.71873 EndAngle=6.28319
    g7: LineSegment StartX=125.616 StartY=38 StartZ=0 EndX=125.616 EndY=19 EndZ=0
  constraints (21):
    c: Block(g0)
    c: Coincident(g1,g0)
    c: Vertical(g1)
    c: Horizontal(g2)
    c: Distance(g2) = 105
    c: Coincident(g2,g0)
    c: Distance(g1) = 19
    c: Coincident(g3,g1)
    c: Horizontal(g3)
    c: Distance(g3) = 105
    c: Coincident(g4,g2)
    c: Horizontal(g4)
    c: Distance(g4) = 1.61553
    c: Horizontal(g5)
    c: Equal(g4,g5) = 1.61553
    c: Coincident(g5,g3)
    c: Block(g6)
    c: Coincident(g6,g5)
    c: Coincident(g7,g4)
    c: Coincident(g7,g6)
    c: Vertical(g7)
FEATURE [Part::Extrusion] Extrude028  label="sideB"
  Base = -> Sketch037
  Dir = (0,0,1)
  DirMode = 2
  FaceMakerClass = Part::FaceMakerBullseye
  LengthFwd = 3
  LengthRev = 0
  Placement = pos=(0,0,72) rot=(0,0,1;0rad)
  Solid = true
  Symmetric = false
FEATURE [Sketcher::SketchObject] Sketch038  label="topSketch010"
  FullyConstrained = true
  sketch-geometry (22):
    g0: LineSegment StartX=5.21097e-06 StartY=3 StartZ=0 EndX=5.21097e-06 EndY=19 EndZ=0
    g1: ArcOfCircle CenterX=19 CenterY=19 CenterZ=0 NormalX=0 NormalY=0 NormalZ=1 AngleXU=0 Radius=19 StartAngle=1.5708 EndAngle=3.14159
    g2: ArcOfCircle CenterX=19 CenterY=19 CenterZ=0 NormalX=0 NormalY=0 NormalZ=1 AngleXU=0 Radius=16 StartAngle=1.5708 EndAngle=3.14159
    g3: LineSegment StartX=114 StartY=35 StartZ=0 EndX=19 EndY=35 EndZ=0
    g4: LineSegment StartX=5.21097e-06 StartY=3 StartZ=0 EndX=5.21097e-06 EndY=0 EndZ=0
    g5: LineSegment StartX=3 StartY=0 StartZ=0 EndX=5.21097e-06 EndY=0 EndZ=0
    g6: LineSegment StartX=3 StartY=19 StartZ=0 EndX=3 EndY=0 EndZ=0
    g7: LineSegment StartX=19 StartY=38 StartZ=0 EndX=124 EndY=38 EndZ=0
    g8: Circle CenterX=119 CenterY=35 CenterZ=0 NormalX=0 NormalY=0 NormalZ=1 AngleXU=0 Radius=1
    g9: Circle CenterX=121 CenterY=35 CenterZ=0 NormalX=0 NormalY=0 NormalZ=1 AngleXU=0 Radius=1
    g10: Circle CenterX=121 CenterY=33 CenterZ=0 NormalX=0 NormalY=0 NormalZ=1 AngleXU=0 Radius=1
    g11: BSplineCurve PolesCount=3 KnotsCount=2 Degree=2 IsPeriodic=0
    g12: GeomPoint X=119 Y=35 Z=0
    g13: GeomPoint X=121 Y=33 Z=0
    g14: LineSegment StartX=119 StartY=35 StartZ=0 EndX=114 EndY=35 EndZ=0
    g15: ArcOfCircle CenterX=105 CenterY=19 CenterZ=0 NormalX=0 NormalY=0 NormalZ=1 AngleXU=0 Radius=16 StartAngle=5.60905 EndAngle=6.28319
    g16: LineSegment StartX=121 StartY=33 StartZ=0 EndX=121 EndY=19 EndZ=0
    g17: LineSegment StartX=117.5 StartY=9.01251 StartZ=0 EndX=121.163 EndY=9.0125 EndZ=0
    g18: ArcOfCircle CenterX=105 CenterY=19 CenterZ=0 NormalX=0 NormalY=0 NormalZ=1 AngleXU=0 Radius=20.6155 StartAngle=5.7297 EndAngle=6.28319
    g19: LineSegment StartX=121.163 StartY=9.0125 StartZ=0 EndX=122.538 EndY=8.16329 EndZ=0
    g20: LineSegment StartX=124 StartY=38 StartZ=0 EndX=125.616 EndY=38 EndZ=0
    g21: LineSegment StartX=125.616 StartY=19 StartZ=0 EndX=125.616 EndY=38 EndZ=0
  constraints (49):
    c: Vertical(g0)
    c: Block(g0)
    c: Coincident(g1,g0)
    c: Block(g1)
    c: Coincident(g2,g1)
    c: Block(g2)
    c: Coincident(g3,g2)
    c: Horizontal(g3)
    c: Tangent(g3,g2)
    c: Coincident(g4,g0)
    c: Distance(g4) = 3
    c: Vertical(g4)
    c: Coincident(g5,g4)
    c: Horizontal(g5)
    c: Coincident(g6,g2)
    c: Coincident(g6,g5)
    c: Vertical(g6)
    c: Horizontal(g7)
    c: Distance(g7) = 105
    c: Coincident(g7,g1)
    c: Block(g3)
    c: Weight(g8) = 1
    c: Equal(g8,g9)
    c: Equal(g8,g10)
    c: InternalAlignment(g8,g11)
    c: InternalAlignment(g9,g11)
    c: InternalAlignment(g10,g11)
    c: InternalAlignment(g12,g11)
    c: InternalAlignment(g13,g11)
    c: Block(g11)
    c: Coincident(g14,g11)
    c: Coincident(g14,g3)
    c: Horizontal(g14)
    c: Block(g15)
    c: Coincident(g16,g11)
    c: Coincident(g16,g15)
    c: Vertical(g16)
    c: Distance(g16) = 14
    c: Coincident(g17,g15)
    c: Block(g18)
    c: Coincident(g19,g18)
    c: Coincident(g20,g7)
    c: Horizontal(g20)
    c: Vertical(g21)
    c: Coincident(g20,g21)
    c: Block(g20)
    c: Block(g21)
    c: Block(g19)
    c: Block(g17)
FEATURE [Part::Extrusion] Extrude029
  Base = -> Sketch038
  Dir = (0,0,1)
  DirMode = 2
  FaceMakerClass = Part::FaceMakerBullseye
  LengthFwd = 72
  LengthRev = 0
  Solid = true
  Symmetric = false
FEATURE [Part::Feature] Face085
  shape: bbox 4.8 x 25.5 x 2e-07 mm, 1 faces, 0 solids (baked)
FEATURE [Part::Revolution] Revolve089  label="moreFrontCaseScrewPost003"
  Angle = 360
  Axis = (0,1,0)
  Base = (0,0,0)
  FaceMakerClass = Part::FaceMakerBullseye
  Placement = pos=(109.5,4.5,3.5) rot=(0,0,1;0rad)
  Solid = false
  Source = -> Face085
  Symmetric = false
FEATURE [Part::Feature] Face086
  shape: bbox 4.8 x 25.5 x 2e-07 mm, 1 faces, 0 solids (baked)
FEATURE [Part::Revolution] Revolve090  label="moreFrontCaseScrewPost004"
  Angle = 360
  Axis = (0,1,0)
  Base = (0,0,0)
  FaceMakerClass = Part::FaceMakerBullseye
  Placement = pos=(109.5,4.5,68.5) rot=(0,0,1;0rad)
  Solid = false
  Source = -> Face086
  Symmetric = false
FEATURE [Part::Fillet] Fillet026  label="top013"
  Base = -> Extrude029
  Edges = 1 edges r=2: [Edge35]
FEATURE [Sketcher::SketchObject] Sketch039
  FullyConstrained = true
  sketch-geometry (7):
    g0: LineSegment StartX=0 StartY=0 StartZ=0 EndX=0 EndY=6 EndZ=0
    g1: Circle CenterX=0 CenterY=0 CenterZ=0 NormalX=0 NormalY=0 NormalZ=1 AngleXU=0 Radius=1
    g2: Circle CenterX=8 CenterY=6 CenterZ=0 NormalX=0 NormalY=0 NormalZ=1 AngleXU=0 Radius=1
    g3: BSplineCurve PolesCount=3 KnotsCount=2 Degree=2 IsPeriodic=0
    g4: GeomPoint X=0 Y=0 Z=0
    g5: GeomPoint X=8 Y=6 Z=0
    g6: LineSegment StartX=0 StartY=6 StartZ=0 EndX=8 EndY=6 EndZ=0
  constraints (14):
    c: Coincident(g0,g-1)
    c: Distance(g0) = 6
    c: Vertical(g0)
    c: Coincident(g3,g0)
    c: Weight(g1) = 1
    c: Equal(g1,g2)
    c: InternalAlignment(g1,g3)
    c: InternalAlignment(g2,g3)
    c: InternalAlignment(g4,g3)
    c: InternalAlignment(g5,g3)
    c: Block(g3)
    c: Coincident(g6,g0)
    c: Coincident(g6,g3)
    c: Horizontal(g6)
FEATURE [Sketcher::SketchObject] Sketch040
  FullyConstrained = true
  sketch-geometry (7):
    g0: LineSegment StartX=0 StartY=0 StartZ=0 EndX=0 EndY=6 EndZ=0
    g1: Circle CenterX=0 CenterY=0 CenterZ=0 NormalX=0 NormalY=0 NormalZ=1 AngleXU=0 Radius=1
    g2: Circle CenterX=8 CenterY=6 CenterZ=0 NormalX=0 NormalY=0 NormalZ=1 AngleXU=0 Radius=1
    g3: BSplineCurve PolesCount=3 KnotsCount=2 Degree=2 IsPeriodic=0
    g4: GeomPoint X=0 Y=0 Z=0
    g5: GeomPoint X=8 Y=6 Z=0
    g6: LineSegment StartX=0 StartY=6 StartZ=0 EndX=8 EndY=6 EndZ=0
  constraints (14):
    c: Coincident(g0,g-1)
    c: Distance(g0) = 6
    c: Vertical(g0)
    c: Coincident(g3,g0)
    c: Weight(g1) = 1
    c: Equal(g1,g2)
    c: InternalAlignment(g1,g3)
    c: InternalAlignment(g2,g3)
    c: InternalAlignment(g4,g3)
    c: InternalAlignment(g5,g3)
    c: Block(g3)
    c: Coincident(g6,g0)
    c: Coincident(g6,g3)
    c: Horizontal(g6)
FEATURE [Sketcher::SketchObject] Sketch041
  FullyConstrained = true
  sketch-geometry (7):
    g0: LineSegment StartX=0 StartY=0 StartZ=0 EndX=0 EndY=6 EndZ=0
    g1: Circle CenterX=0 CenterY=0 CenterZ=0 NormalX=0 NormalY=0 NormalZ=1 AngleXU=0 Radius=1
    g2: Circle CenterX=8 CenterY=6 CenterZ=0 NormalX=0 NormalY=0 NormalZ=1 AngleXU=0 Radius=1
    g3: BSplineCurve PolesCount=3 KnotsCount=2 Degree=2 IsPeriodic=0
    g4: GeomPoint X=0 Y=0 Z=0
    g5: GeomPoint X=8 Y=6 Z=0
    g6: LineSegment StartX=0 StartY=6 StartZ=0 EndX=8 EndY=6 EndZ=0
  constraints (14):
    c: Coincident(g0,g-1)
    c: Distance(g0) = 6
    c: Vertical(g0)
    c: Coincident(g3,g0)
    c: Weight(g1) = 1
    c: Equal(g1,g2)
    c: InternalAlignment(g1,g3)
    c: InternalAlignment(g2,g3)
    c: InternalAlignment(g4,g3)
    c: InternalAlignment(g5,g3)
    c: Block(g3)
    c: Coincident(g6,g0)
    c: Coincident(g6,g3)
    c: Horizontal(g6)
FEATURE [Sketcher::SketchObject] Sketch042
  FullyConstrained = true
  sketch-geometry (7):
    g0: LineSegment StartX=0 StartY=0 StartZ=0 EndX=0 EndY=6 EndZ=0
    g1: Circle CenterX=0 CenterY=0 CenterZ=0 NormalX=0 NormalY=0 NormalZ=1 AngleXU=0 Radius=1
    g2: Circle CenterX=8 CenterY=6 CenterZ=0 NormalX=0 NormalY=0 NormalZ=1 AngleXU=0 Radius=1
    g3: BSplineCurve PolesCount=3 KnotsCount=2 Degree=2 IsPeriodic=0
    g4: GeomPoint X=0 Y=0 Z=0
    g5: GeomPoint X=8 Y=6 Z=0
    g6: LineSegment StartX=0 StartY=6 StartZ=0 EndX=8 EndY=6 EndZ=0
  constraints (14):
    c: Coincident(g0,g-1)
    c: Distance(g0) = 6
    c: Vertical(g0)
    c: Coincident(g3,g0)
    c: Weight(g1) = 1
    c: Equal(g1,g2)
    c: InternalAlignment(g1,g3)
    c: InternalAlignment(g2,g3)
    c: InternalAlignment(g4,g3)
    c: InternalAlignment(g5,g3)
    c: Block(g3)
    c: Coincident(g6,g0)
    c: Coincident(g6,g3)
    c: Horizontal(g6)
FEATURE [Part::Extrusion] Extrude030  label="caseScrewPillarBracket008"
  Base = -> Sketch039
  Dir = (0,0,1)
  DirMode = 2
  FaceMakerClass = Part::FaceMakerBullseye
  LengthFwd = 2.4
  LengthRev = 0
  Placement = pos=(15.76,29,8.8) rot=(0,1,0;0rad)
  Solid = true
  Symmetric = false
FEATURE [Part::Extrusion] Extrude031  label="caseScrewPillarBracket009"
  Base = -> Sketch040
  Dir = (0,0,1)
  DirMode = 2
  FaceMakerClass = Part::FaceMakerBullseye
  LengthFwd = 2.4
  LengthRev = 0
  Placement = pos=(15.76,29,60.8) rot=(0,0,1;0rad)
  Solid = true
  Symmetric = false
FEATURE [Part::Extrusion] Extrude032  label="caseScrewPillarBracket010"
  Base = -> Sketch041
  Dir = (0,0,1)
  DirMode = 2
  FaceMakerClass = Part::FaceMakerBullseye
  LengthFwd = 2.4
  LengthRev = 0
  Placement = pos=(13.7,29,13.26) rot=(0,-1,0;1.5708rad)
  Solid = true
  Symmetric = false
FEATURE [Part::Extrusion] Extrude033  label="caseScrewPillarBracket011"
  Base = -> Sketch042
  Dir = (0,0,1)
  DirMode = 2
  FaceMakerClass = Part::FaceMakerBullseye
  LengthFwd = 2.4
  LengthRev = 0
  Placement = pos=(11.3,29,58.74) rot=(0,1,0;1.5708rad)
  Solid = true
  Symmetric = false
FEATURE [Sketcher::SketchObject] Sketch043
  FullyConstrained = true
  sketch-geometry (7):
    g0: LineSegment StartX=0 StartY=0 StartZ=0 EndX=0 EndY=6 EndZ=0
    g1: Circle CenterX=0 CenterY=0 CenterZ=0 NormalX=0 NormalY=0 NormalZ=1 AngleXU=0 Radius=1
    g2: Circle CenterX=8 CenterY=6 CenterZ=0 NormalX=0 NormalY=0 NormalZ=1 AngleXU=0 Radius=1
    g3: BSplineCurve PolesCount=3 KnotsCount=2 Degree=2 IsPeriodic=0
    g4: GeomPoint X=0 Y=0 Z=0
    g5: GeomPoint X=8 Y=6 Z=0
    g6: LineSegment StartX=0 StartY=6 StartZ=0 EndX=8 EndY=6 EndZ=0
  constraints (14):
    c: Coincident(g0,g-1)
    c: Distance(g0) = 6
    c: Vertical(g0)
    c: Coincident(g3,g0)
    c: Weight(g1) = 1
    c: Equal(g1,g2)
    c: InternalAlignment(g1,g3)
    c: InternalAlignment(g2,g3)
    c: InternalAlignment(g4,g3)
    c: InternalAlignment(g5,g3)
    c: Block(g3)
    c: Coincident(g6,g0)
    c: Coincident(g6,g3)
    c: Horizontal(g6)
FEATURE [Part::Extrusion] Extrude034  label="caseScrewPillarBracket012"
  Base = -> Sketch043
  Dir = (0,0,1)
  DirMode = 2
  FaceMakerClass = Part::FaceMakerBullseye
  LengthFwd = 2.4
  LengthRev = 0
  Placement = pos=(88.3,29,65.23) rot=(0,1,0;1.5708rad)
  Solid = true
  Symmetric = false
FEATURE [Sketcher::SketchObject] Sketch044
  FullyConstrained = true
  sketch-geometry (7):
    g0: LineSegment StartX=0 StartY=0 StartZ=0 EndX=0 EndY=6 EndZ=0
    g1: Circle CenterX=0 CenterY=0 CenterZ=0 NormalX=0 NormalY=0 NormalZ=1 AngleXU=0 Radius=1
    g2: Circle CenterX=8 CenterY=6 CenterZ=0 NormalX=0 NormalY=0 NormalZ=1 AngleXU=0 Radius=1
    g3: BSplineCurve PolesCount=3 KnotsCount=2 Degree=2 IsPeriodic=0
    g4: GeomPoint X=0 Y=0 Z=0
    g5: GeomPoint X=8 Y=6 Z=0
    g6: LineSegment StartX=0 StartY=6 StartZ=0 EndX=8 EndY=6 EndZ=0
  constraints (14):
    c: Coincident(g0,g-1)
    c: Distance(g0) = 6
    c: Vertical(g0)
    c: Coincident(g3,g0)
    c: Weight(g1) = 1
    c: Equal(g1,g2)
    c: InternalAlignment(g1,g3)
    c: InternalAlignment(g2,g3)
    c: InternalAlignment(g4,g3)
    c: InternalAlignment(g5,g3)
    c: Block(g3)
    c: Coincident(g6,g0)
    c: Coincident(g6,g3)
    c: Horizontal(g6)
FEATURE [Part::Extrusion] Extrude035  label="caseScrewPillarBracket013"
  Base = -> Sketch044
  Dir = (0,0,1)
  DirMode = 2
  FaceMakerClass = Part::FaceMakerBullseye
  LengthFwd = 2.4
  LengthRev = 0
  Placement = pos=(90.7,29,6.77) rot=(0,-1,0;1.5708rad)
  Solid = true
  Symmetric = false
FEATURE [Sketcher::SketchObject] Sketch045
  FullyConstrained = true
  sketch-geometry (7):
    g0: LineSegment StartX=0 StartY=0 StartZ=0 EndX=0 EndY=6 EndZ=0
    g1: Circle CenterX=0 CenterY=0 CenterZ=0 NormalX=0 NormalY=0 NormalZ=1 AngleXU=0 Radius=1
    g2: Circle CenterX=8 CenterY=6 CenterZ=0 NormalX=0 NormalY=0 NormalZ=1 AngleXU=0 Radius=1
    g3: BSplineCurve PolesCount=3 KnotsCount=2 Degree=2 IsPeriodic=0
    g4: GeomPoint X=0 Y=0 Z=0
    g5: GeomPoint X=8 Y=6 Z=0
    g6: LineSegment StartX=0 StartY=6 StartZ=0 EndX=8 EndY=6 EndZ=0
  constraints (14):
    c: Coincident(g0,g-1)
    c: Distance(g0) = 6
    c: Vertical(g0)
    c: Coincident(g3,g0)
    c: Weight(g1) = 1
    c: Equal(g1,g2)
    c: InternalAlignment(g1,g3)
    c: InternalAlignment(g2,g3)
    c: InternalAlignment(g4,g3)
    c: InternalAlignment(g5,g3)
    c: Block(g3)
    c: Coincident(g6,g0)
    c: Coincident(g6,g3)
    c: Horizontal(g6)
FEATURE [Sketcher::SketchObject] Sketch046
  FullyConstrained = true
  sketch-geometry (7):
    g0: LineSegment StartX=0 StartY=0 StartZ=0 EndX=0 EndY=6 EndZ=0
    g1: Circle CenterX=0 CenterY=0 CenterZ=0 NormalX=0 NormalY=0 NormalZ=1 AngleXU=0 Radius=1
    g2: Circle CenterX=8 CenterY=6 CenterZ=0 NormalX=0 NormalY=0 NormalZ=1 AngleXU=0 Radius=1
    g3: BSplineCurve PolesCount=3 KnotsCount=2 Degree=2 IsPeriodic=0
    g4: GeomPoint X=0 Y=0 Z=0
    g5: GeomPoint X=8 Y=6 Z=0
    g6: LineSegment StartX=0 StartY=6 StartZ=0 EndX=8 EndY=6 EndZ=0
  constraints (14):
    c: Coincident(g0,g-1)
    c: Distance(g0) = 6
    c: Vertical(g0)
    c: Coincident(g3,g0)
    c: Weight(g1) = 1
    c: Equal(g1,g2)
    c: InternalAlignment(g1,g3)
    c: InternalAlignment(g2,g3)
    c: InternalAlignment(g4,g3)
    c: InternalAlignment(g5,g3)
    c: Block(g3)
    c: Coincident(g6,g0)
    c: Coincident(g6,g3)
    c: Horizontal(g6)
FEATURE [Part::Extrusion] Extrude036  label="caseScrewPillarBracket014"
  Base = -> Sketch045
  Dir = (0,0,1)
  DirMode = 2
  FaceMakerClass = Part::FaceMakerBullseye
  LengthFwd = 2.4
  LengthRev = 0
  Placement = pos=(110.7,29,6.77) rot=(0,-1,0;1.5708rad)
  Solid = true
  Symmetric = false
FEATURE [Part::Extrusion] Extrude037  label="caseScrewPillarBracket015"
  Base = -> Sketch046
  Dir = (0,0,1)
  DirMode = 2
  FaceMakerClass = Part::FaceMakerBullseye
  LengthFwd = 2.4
  LengthRev = 0
  Placement = pos=(108.3,29,65.23) rot=(0,1,0;1.5708rad)
  Solid = true
  Symmetric = false
FEATURE [Part::Box] Box013  label="frontCaseScrewPillarBracket002"
  AttacherType = Attacher::AttachEngine3D
  Height = 2.4
  Length = 22
  Placement = pos=(87,28,2.3) rot=(0,0,1;0rad)
  Width = 7
FEATURE [Part::Box] Box014  label="frontCaseScrewPillarBracket003"
  AttacherType = Attacher::AttachEngine3D
  Height = 2.4
  Length = 22
  Placement = pos=(87,28,67.3) rot=(0,0,1;0rad)
  Width = 7
FEATURE [Part::Feature] Face087
  shape: bbox 4.8 x 30.2 x 2e-07 mm, 1 faces, 0 solids (baked)
FEATURE [Part::Revolution] Revolve091  label="frontCaseScrewPost004"
  Angle = 360
  Axis = (0,1,0)
  Base = (0,0,0)
  FaceMakerClass = Part::FaceMakerBullseye
  Placement = pos=(89.5,4.5,3.5) rot=(0,0,1;0rad)
  Solid = false
  Source = -> Face087
  Symmetric = false
FEATURE [Part::Feature] Face088
  shape: bbox 4.8 x 30.2 x 2e-07 mm, 1 faces, 0 solids (baked)
FEATURE [Part::Revolution] Revolve092  label="frontCaseScrewPost005"
  Angle = 360
  Axis = (0,1,0)
  Base = (0,0,0)
  FaceMakerClass = Part::FaceMakerBullseye
  Placement = pos=(89.5,4.5,68.5) rot=(0,0,1;0rad)
  Solid = false
  Source = -> Face088
  Symmetric = false
FEATURE [Part::Feature] Face089
  shape: bbox 3.5 x 30.2 x 2e-07 mm, 1 faces, 0 solids (baked)
FEATURE [Part::Revolution] Revolve093  label="backCaseScrewPost002"
  Angle = 360
  Axis = (0,1,0)
  Base = (0,0,0)
  FaceMakerClass = Part::FaceMakerBullseye
  Placement = pos=(12.5,4.5,10) rot=(0,0,1;0rad)
  Solid = false
  Source = -> Face089
  Symmetric = false
FEATURE [Part::Feature] Face090
  shape: bbox 3.5 x 30.2 x 2e-07 mm, 1 faces, 0 solids (baked)
FEATURE [Part::Revolution] Revolve094  label="backCaseScrewPost003"
  Angle = 360
  Axis = (0,1,0)
  Base = (0,0,0)
  FaceMakerClass = Part::FaceMakerBullseye
  Placement = pos=(12.5,4.5,62) rot=(0,0,1;0rad)
  Solid = false
  Source = -> Face090
  Symmetric = false
FEATURE [Part::Box] Box015  label="Cube011"
  AttacherType = Attacher::AttachEngine3D
  Height = 28.8
  Length = 3
  Placement = pos=(107.3,28,21.6) rot=(0,0,1;0rad)
  Width = 7
FEATURE [Part::Box] Box016  label="Cube012"
  AttacherType = Attacher::AttachEngine3D
  Height = 3
  Length = 7.4
  Placement = pos=(107.3,28,18.6) rot=(0,0,1;0rad)
  Width = 7
FEATURE [Part::Box] Box017  label="Cube013"
  AttacherType = Attacher::AttachEngine3D
  Height = 3
  Length = 7.4
  Placement = pos=(107.3,28,50.4) rot=(0,0,1;0rad)
  Width = 7
FEATURE [Part::Cylinder] Cylinder024
  Angle = 360
  AttacherType = Attacher::AttachEngine3D
  Height = 20
  Placement = pos=(0,0,36.15) rot=(0,0,1;0rad)
  Radius = 14.3
FEATURE [Part::Cylinder] Cylinder025
  Angle = 360
  AttacherType = Attacher::AttachEngine3D
  Height = 10
  Placement = pos=(0,0,36.15) rot=(0,0,1;0rad)
  Radius = 4
FEATURE [Part::MultiFuse] Fusion066  label="removeToCreteHoleForPlugHousing009"
  Placement = pos=(70,19,36) rot=(0,1,0;1.5708rad)
  Shapes = -> [Cylinder024,Cylinder025]
FEATURE [Part::MultiFuse] Fusion065  label="plugHousingBracketHolder002"
  Shapes = -> [Box017,Box015,Box016]
FEATURE [Part::Cut] Cut025  label="plugHousingBracketHolder003"
  Base = -> Fusion065
  Placement = pos=(7,0,0) rot=(0,0,1;0rad)
  Tool = -> Fusion066
FEATURE [Sketcher::SketchObject] Sketch047
  FullyConstrained = false
  Placement = pos=(0,0,0) rot=(1,0,0;1.5708rad)
  sketch-geometry (24):
    g0: ArcOfCircle CenterX=-4 CenterY=-10.5 CenterZ=0 NormalX=0 NormalY=0 NormalZ=1 AngleXU=0 Radius=1.5 StartAngle=6e-16 EndAngle=3.14159
    g1: ArcOfCircle CenterX=-34.2 CenterY=-10.5 CenterZ=0 NormalX=0 NormalY=0 NormalZ=1 AngleXU=0 Radius=1.5 StartAngle=0 EndAngle=3.14159
    g2: ArcOfCircle CenterX=-34.2 CenterY=-27.7 CenterZ=0 NormalX=0 NormalY=0 NormalZ=1 AngleXU=0 Radius=1.5 StartAngle=3.14159 EndAngle=6.28319
    g3: ArcOfCircle CenterX=-4 CenterY=-27.7 CenterZ=0 NormalX=0 NormalY=0 NormalZ=1 AngleXU=0 Radius=1.5 StartAngle=3.1416 EndAngle=6.28319
    g4: ArcOfCircle CenterX=-10 CenterY=-4.3 CenterZ=0 NormalX=0 NormalY=0 NormalZ=1 AngleXU=0 Radius=1.5 StartAngle=2e-16 EndAngle=3.14159
    g5: ArcOfCircle CenterX=-16.1 CenterY=-1.8 CenterZ=0 NormalX=0 NormalY=0 NormalZ=1 AngleXU=0 Radius=1.5 StartAngle=5e-16 EndAngle=3.14159
    g6: ArcOfCircle CenterX=-22.1 CenterY=-1.8 CenterZ=0 NormalX=0 NormalY=0 NormalZ=1 AngleXU=0 Radius=1.5 StartAngle=5e-16 EndAngle=3.14159
    g7: ArcOfCircle CenterX=-28.2 CenterY=-4.3 CenterZ=0 NormalX=0 NormalY=0 NormalZ=1 AngleXU=0 Radius=1.5 StartAngle=2e-16 EndAngle=3.14159
    g8: ArcOfCircle CenterX=-10 CenterY=-33.9 CenterZ=0 NormalX=0 NormalY=0 NormalZ=1 AngleXU=0 Radius=1.5 StartAngle=3.14159 EndAngle=6.28319
    g9: ArcOfCircle CenterX=-16.1 CenterY=-36.4 CenterZ=0 NormalX=0 NormalY=0 NormalZ=1 AngleXU=0 Radius=1.5 StartAngle=3.14159 EndAngle=6.28319
    g10: ArcOfCircle CenterX=-22.1 CenterY=-36.4 CenterZ=0 NormalX=0 NormalY=0 NormalZ=1 AngleXU=0 Radius=1.5 StartAngle=3.14159 EndAngle=6.28319
    g11: ArcOfCircle CenterX=-28.2 CenterY=-33.9 CenterZ=0 NormalX=0 NormalY=0 NormalZ=1 AngleXU=0 Radius=1.5 StartAngle=3.14159 EndAngle=6.28319
    g12: LineSegment StartX=-35.7 StartY=-10.5 StartZ=0 EndX=-35.7 EndY=-27.7 EndZ=0
    g13: LineSegment StartX=-32.7 StartY=-10.5 StartZ=0 EndX=-32.7 EndY=-27.7 EndZ=0
    g14: LineSegment StartX=-29.7 StartY=-33.9 StartZ=0 EndX=-29.7 EndY=-4.3 EndZ=0
    g15: LineSegment StartX=-26.7 StartY=-33.9 StartZ=0 EndX=-26.7 EndY=-4.3 EndZ=0
    g16: LineSegment StartX=-2.5 StartY=-10.5 StartZ=0 EndX=-2.5 EndY=-27.7 EndZ=0
    g17: LineSegment StartX=-8.5 StartY=-4.3 StartZ=0 EndX=-8.5 EndY=-33.9 EndZ=0
    g18: LineSegment StartX=-5.5 StartY=-10.5 StartZ=0 EndX=-5.5 EndY=-27.7 EndZ=0
    g19: LineSegment StartX=-11.5 StartY=-4.3 StartZ=0 EndX=-11.5 EndY=-33.9 EndZ=0
    g20: LineSegment StartX=-14.6 StartY=-1.8 StartZ=0 EndX=-14.6 EndY=-36.4 EndZ=0
    g21: LineSegment StartX=-17.6 StartY=-1.8 StartZ=0 EndX=-17.6 EndY=-36.4 EndZ=0
    g22: LineSegment StartX=-20.6 StartY=-36.4 StartZ=0 EndX=-20.6 EndY=-1.8 EndZ=0
    g23: LineSegment StartX=-23.6 StartY=-1.8 StartZ=0 EndX=-23.6 EndY=-36.4 EndZ=0
  constraints (48):
    c: Block(g0)
    c: Block(g1)
    c: Block(g2)
    c: Block(g3)
    c: Block(g4)
    c: Block(g5)
    c: Block(g6)
    c: Block(g7)
    c: Block(g8)
    c: Block(g9)
    c: Block(g10)
    c: Block(g11)
    c: Coincident(g12,g1)
    c: Coincident(g12,g2)
    c: Vertical(g12)
    c: Coincident(g13,g1)
    c: Coincident(g13,g2)
    c: Vertical(g13)
    c: Coincident(g14,g11)
    c: Coincident(g14,g7)
    c: Vertical(g14)
    c: Coincident(g15,g11)
    c: Coincident(g15,g7)
    c: Vertical(g15)
    c: Coincident(g16,g0)
    c: Coincident(g16,g3)
    c: Vertical(g16)
    c: Coincident(g17,g4)
    c: Coincident(g17,g8)
    c: Vertical(g17)
    c: Coincident(g18,g0)
    c: Coincident(g18,g3)
    c: Vertical(g18)
    c: Coincident(g19,g4)
    c: Coincident(g19,g8)
    c: Vertical(g19)
    c: Coincident(g20,g5)
    c: Coincident(g20,g9)
    c: Vertical(g20)
    c: Coincident(g21,g5)
    c: Coincident(g21,g9)
    c: Vertical(g21)
    c: Coincident(g22,g10)
    c: Coincident(g22,g6)
    c: Vertical(g22)
    c: Coincident(g23,g6)
    c: Coincident(g23,g10)
    c: Vertical(g23)
FEATURE [Part::Extrusion] Extrude038  label="removeToCreateFanGrillHoles001"
  Base = -> Sketch047
  Dir = (0,-1,6e-16)
  DirMode = 2
  FaceMakerClass = Part::FaceMakerBullseye
  LengthFwd = 10
  LengthRev = 0
  Placement = pos=(65.4,44,54.82) rot=(0,0,1;0rad)
  Solid = true
  Symmetric = false
FEATURE [Part::Feature] Wire004
  shape: bbox 11 x 5.2 x 2e-07 mm, 0 faces, 0 solids (baked)
FEATURE [Part::Revolution] Revolve095
  Angle = 360
  Axis = (0,1,0)
  Base = (0,0,0)
  FaceMakerClass = Part::FaceMakerBullseye
  Placement = pos=(30.3,38,19.7) rot=(0,0,1;0rad)
  Solid = true
  Source = -> Wire004
  Symmetric = false
FEATURE [Part::Feature] Wire005
  shape: bbox 11 x 5.2 x 2e-07 mm, 0 faces, 0 solids (baked)
FEATURE [Part::Revolution] Revolve096
  Angle = 360
  Axis = (0,1,0)
  Base = (0,0,0)
  FaceMakerClass = Part::FaceMakerBullseye
  Placement = pos=(30.3,38,51.7) rot=(0,0,1;0rad)
  Solid = true
  Source = -> Wire005
  Symmetric = false
FEATURE [Part::Feature] Wire006
  shape: bbox 11 x 5.2 x 2e-07 mm, 0 faces, 0 solids (baked)
FEATURE [Part::Revolution] Revolve097
  Angle = 360
  Axis = (0,1,0)
  Base = (0,0,0)
  FaceMakerClass = Part::FaceMakerBullseye
  Placement = pos=(62.3,38,51.7) rot=(0,0,1;0rad)
  Solid = true
  Source = -> Wire006
  Symmetric = false
FEATURE [Part::Feature] Wire007
  shape: bbox 11 x 5.2 x 2e-07 mm, 0 faces, 0 solids (baked)
FEATURE [Part::Revolution] Revolve098
  Angle = 360
  Axis = (0,1,0)
  Base = (0,0,0)
  FaceMakerClass = Part::FaceMakerBullseye
  Placement = pos=(62.3,38,19.7) rot=(0,0,1;0rad)
  Solid = true
  Source = -> Wire007
  Symmetric = false
FEATURE [Part::MultiFuse] Fusion067  label="fanScrewHousing002"
  Shapes = -> [Revolve098,Revolve097,Revolve096,Revolve095]
FEATURE [Part::Feature] Face091 .. Face094  x4 (patterned run collapsed; names and placements below)
  shape: bbox 3.5 x 17.8 x 2e-07 mm, 1 faces, 0 solids (baked)
FEATURE [Part::Revolution] Revolve099  label="removeToCreateScrewAndThreadedInsertHole026"
  Angle = 360
  Axis = (0,1,0)
  Base = (0,0,0)
  FaceMakerClass = Part::FaceMakerBullseye
  Placement = pos=(62.3,30.3,19.7) rot=(0,0,1;0rad)
  Solid = false
  Source = -> Face091
  Symmetric = false
FEATURE [Part::Revolution] Revolve100  label="removeToCreateScrewAndThreadedInsertHole027"
  Angle = 360
  Axis = (0,1,0)
  Base = (0,0,0)
  FaceMakerClass = Part::FaceMakerBullseye
  Placement = pos=(62.3,30.3,51.7) rot=(0,0,1;0rad)
  Solid = false
  Source = -> Face092
  Symmetric = false
FEATURE [Part::Revolution] Revolve101  label="removeToCreateScrewAndThreadedInsertHole028"
  Angle = 360
  Axis = (0,1,0)
  Base = (0,0,0)
  FaceMakerClass = Part::FaceMakerBullseye
  Placement = pos=(30.3,30.3,19.7) rot=(0,0,1;0rad)
  Solid = false
  Source = -> Face093
  Symmetric = false
FEATURE [Part::Revolution] Revolve102  label="removeToCreateScrewAndThreadedInsertHole029"
  Angle = 360
  Axis = (0,1,0)
  Base = (0,0,0)
  FaceMakerClass = Part::FaceMakerBullseye
  Placement = pos=(30.3,30.3,51.7) rot=(0,0,1;0rad)
  Solid = false
  Source = -> Face094
  Symmetric = false
FEATURE [Part::MultiFuse] Fusion068  label="createThreadedInsertHolesForFan002"
  Shapes = -> [Revolve099,Revolve100,Revolve101,Revolve102]
FEATURE [Part::Cut] Cut026  label="fanScrewHousing003"
  Base = -> Fusion067
  Tool = -> Fusion068
FEATURE [Sketcher::SketchObject] Sketch048
  FullyConstrained = false
  Placement = pos=(0,0,0) rot=(1,0,0;1.5708rad)
  sketch-geometry (24):
    g0: ArcOfCircle CenterX=-4 CenterY=-10.5 CenterZ=0 NormalX=0 NormalY=0 NormalZ=1 AngleXU=0 Radius=1.5 StartAngle=6e-16 EndAngle=3.14159
    g1: ArcOfCircle CenterX=-34.2 CenterY=-10.5 CenterZ=0 NormalX=0 NormalY=0 NormalZ=1 AngleXU=0 Radius=1.5 StartAngle=0 EndAngle=3.14159
    g2: ArcOfCircle CenterX=-34.2 CenterY=-27.7 CenterZ=0 NormalX=0 NormalY=0 NormalZ=1 AngleXU=0 Radius=1.5 StartAngle=3.14159 EndAngle=6.28319
    g3: ArcOfCircle CenterX=-4 CenterY=-27.7 CenterZ=0 NormalX=0 NormalY=0 NormalZ=1 AngleXU=0 Radius=1.5 StartAngle=3.1416 EndAngle=6.28319
    g4: ArcOfCircle CenterX=-10 CenterY=-4.3 CenterZ=0 NormalX=0 NormalY=0 NormalZ=1 AngleXU=0 Radius=1.5 StartAngle=2e-16 EndAngle=3.14159
    g5: ArcOfCircle CenterX=-16.1 CenterY=-1.8 CenterZ=0 NormalX=0 NormalY=0 NormalZ=1 AngleXU=0 Radius=1.5 StartAngle=5e-16 EndAngle=3.14159
    g6: ArcOfCircle CenterX=-22.1 CenterY=-1.8 CenterZ=0 NormalX=0 NormalY=0 NormalZ=1 AngleXU=0 Radius=1.5 StartAngle=5e-16 EndAngle=3.14159
    g7: ArcOfCircle CenterX=-28.2 CenterY=-4.3 CenterZ=0 NormalX=0 NormalY=0 NormalZ=1 AngleXU=0 Radius=1.5 StartAngle=2e-16 EndAngle=3.14159
    g8: ArcOfCircle CenterX=-10 CenterY=-33.9 CenterZ=0 NormalX=0 NormalY=0 NormalZ=1 AngleXU=0 Radius=1.5 StartAngle=3.14159 EndAngle=6.28319
    g9: ArcOfCircle CenterX=-16.1 CenterY=-36.4 CenterZ=0 NormalX=0 NormalY=0 NormalZ=1 AngleXU=0 Radius=1.5 StartAngle=3.14159 EndAngle=6.28319
    g10: ArcOfCircle CenterX=-22.1 CenterY=-36.4 CenterZ=0 NormalX=0 NormalY=0 NormalZ=1 AngleXU=0 Radius=1.5 StartAngle=3.14159 EndAngle=6.28319
    g11: ArcOfCircle CenterX=-28.2 CenterY=-33.9 CenterZ=0 NormalX=0 NormalY=0 NormalZ=1 AngleXU=0 Radius=1.5 StartAngle=3.14159 EndAngle=6.28319
    g12: LineSegment StartX=-35.7 StartY=-10.5 StartZ=0 EndX=-35.7 EndY=-27.7 EndZ=0
    g13: LineSegment StartX=-32.7 StartY=-10.5 StartZ=0 EndX=-32.7 EndY=-27.7 EndZ=0
    g14: LineSegment StartX=-29.7 StartY=-33.9 StartZ=0 EndX=-29.7 EndY=-4.3 EndZ=0
    g15: LineSegment StartX=-26.7 StartY=-33.9 StartZ=0 EndX=-26.7 EndY=-4.3 EndZ=0
    g16: LineSegment StartX=-2.5 StartY=-10.5 StartZ=0 EndX=-2.5 EndY=-27.7 EndZ=0
    g17: LineSegment StartX=-8.5 StartY=-4.3 StartZ=0 EndX=-8.5 EndY=-33.9 EndZ=0
    g18: LineSegment StartX=-5.5 StartY=-10.5 StartZ=0 EndX=-5.5 EndY=-27.7 EndZ=0
    g19: LineSegment StartX=-11.5 StartY=-4.3 StartZ=0 EndX=-11.5 EndY=-33.9 EndZ=0
    g20: LineSegment StartX=-14.6 StartY=-1.8 StartZ=0 EndX=-14.6 EndY=-36.4 EndZ=0
    g21: LineSegment StartX=-17.6 StartY=-1.8 StartZ=0 EndX=-17.6 EndY=-36.4 EndZ=0
    g22: LineSegment StartX=-20.6 StartY=-36.4 StartZ=0 EndX=-20.6 EndY=-1.8 EndZ=0
    g23: LineSegment StartX=-23.6 StartY=-1.8 StartZ=0 EndX=-23.6 EndY=-36.4 EndZ=0
  constraints (48):
    c: Block(g0)
    c: Block(g1)
    c: Block(g2)
    c: Block(g3)
    c: Block(g4)
    c: Block(g5)
    c: Block(g6)
    c: Block(g7)
    c: Block(g8)
    c: Block(g9)
    c: Block(g10)
    c: Block(g11)
    c: Coincident(g12,g1)
    c: Coincident(g12,g2)
    c: Vertical(g12)
    c: Coincident(g13,g1)
    c: Coincident(g13,g2)
    c: Vertical(g13)
    c: Coincident(g14,g11)
    c: Coincident(g14,g7)
    c: Vertical(g14)
    c: Coincident(g15,g11)
    c: Coincident(g15,g7)
    c: Vertical(g15)
    c: Coincident(g16,g0)
    c: Coincident(g16,g3)
    c: Vertical(g16)
    c: Coincident(g17,g4)
    c: Coincident(g17,g8)
    c: Vertical(g17)
    c: Coincident(g18,g0)
    c: Coincident(g18,g3)
    c: Vertical(g18)
    c: Coincident(g19,g4)
    c: Coincident(g19,g8)
    c: Vertical(g19)
    c: Coincident(g20,g5)
    c: Coincident(g20,g9)
    c: Vertical(g20)
    c: Coincident(g21,g5)
    c: Coincident(g21,g9)
    c: Vertical(g21)
    c: Coincident(g22,g10)
    c: Coincident(g22,g6)
    c: Vertical(g22)
    c: Coincident(g23,g6)
    c: Coincident(g23,g10)
    c: Vertical(g23)
FEATURE [Part::Extrusion] Extrude039  label="removeToCreateFanGrillHoles002"
  Base = -> Sketch048
  Dir = (0,-1,6e-16)
  DirMode = 2
  FaceMakerClass = Part::FaceMakerBullseye
  LengthFwd = 10
  LengthRev = 0
  Placement = pos=(65.4,44,54.82) rot=(0,0,1;0rad)
  Solid = true
  Symmetric = false
FEATURE [Part::Cut] Cut027  label="fanScrewHousing004"
  Base = -> Cut026
  Tool = -> Extrude038
FEATURE [Part::Cut] Cut028  label="top014"
  Base = -> Fillet026
  Tool = -> Extrude039
FEATURE [Part::Feature] Face095 .. Face098  x4 (patterned run collapsed; names and placements below)
  shape: bbox 3.5 x 17.8 x 2e-07 mm, 1 faces, 0 solids (baked)
FEATURE [Part::Revolution] Revolve103  label="removeToCreateScrewAndThreadedInsertHole030"
  Angle = 360
  Axis = (0,1,0)
  Base = (0,0,0)
  FaceMakerClass = Part::FaceMakerBullseye
  Placement = pos=(62.3,30.3,19.7) rot=(0,0,1;0rad)
  Solid = false
  Source = -> Face095
  Symmetric = false
FEATURE [Part::Revolution] Revolve104  label="removeToCreateScrewAndThreadedInsertHole031"
  Angle = 360
  Axis = (0,1,0)
  Base = (0,0,0)
  FaceMakerClass = Part::FaceMakerBullseye
  Placement = pos=(62.3,30.3,51.7) rot=(0,0,1;0rad)
  Solid = false
  Source = -> Face096
  Symmetric = false
FEATURE [Part::Revolution] Revolve105  label="removeToCreateScrewAndThreadedInsertHole032"
  Angle = 360
  Axis = (0,1,0)
  Base = (0,0,0)
  FaceMakerClass = Part::FaceMakerBullseye
  Placement = pos=(30.3,30.3,19.7) rot=(0,0,1;0rad)
  Solid = false
  Source = -> Face097
  Symmetric = false
FEATURE [Part::Revolution] Revolve106  label="removeToCreateScrewAndThreadedInsertHole033"
  Angle = 360
  Axis = (0,1,0)
  Base = (0,0,0)
  FaceMakerClass = Part::FaceMakerBullseye
  Placement = pos=(30.3,30.3,51.7) rot=(0,0,1;0rad)
  Solid = false
  Source = -> Face098
  Symmetric = false
FEATURE [Part::MultiFuse] Fusion069  label="createThreadedInsertHolesForFan003"
  Shapes = -> [Revolve103,Revolve104,Revolve105,Revolve106]
FEATURE [Part::Cut] Cut029  label="top015"
  Base = -> Cut028
  Tool = -> Fusion054
FEATURE [Part::Cut] Cut030  label="fanScrewHousing005"
  Base = -> Cut027
  Tool = -> Fusion069
FEATURE [Part::Cylinder] Cylinder026  label="removeToCreteHoleForPlugHousing010"
  Angle = 360
  AttacherType = Attacher::AttachEngine3D
  Height = 20
  Placement = pos=(-2,19,36) rot=(0,1,0;1.5708rad)
  Radius = 14.3
FEATURE [Part::Box] Box018  label="removeToCreteHoleForPlugHousing011"
  AttacherType = Attacher::AttachEngine3D
  Height = 28.6
  Length = 10
  Placement = pos=(-2,0,21.7) rot=(0,0,1;0rad)
  Width = 19
FEATURE [Part::Box] Box019  label="wireHolderBottomCaseBit"
  AttacherType = Attacher::AttachEngine3D
  Height = 28
  Length = 3
  Placement = pos=(0,0,22) rot=(0,0,1;0rad)
  Width = 21
FEATURE [Part::Cylinder] Cylinder027  label="removeToCreteHoleForPlugHousing012"
  Angle = 360
  AttacherType = Attacher::AttachEngine3D
  Height = 20
  Placement = pos=(-2,19,36) rot=(0,1,0;1.5708rad)
  Radius = 14.3
FEATURE [Part::Cut] Cut031  label="wireHolderBottomCaseBit001"
  Base = -> Box019
  Tool = -> Cylinder027
FEATURE [Part::MultiFuse] Fusion070  label="removeToCreteHoleForPlugHousing013"
  Shapes = -> [Box018,Cylinder026]
FEATURE [Part::Cut] Cut032  label="top016"
  Base = -> Cut029
  Tool = -> Fusion070
FEATURE [Part::Cylinder] Cylinder028
  Angle = 360
  AttacherType = Attacher::AttachEngine3D
  Height = 20
  Placement = pos=(0,0,36.15) rot=(0,0,1;0rad)
  Radius = 14.3
FEATURE [Part::Cylinder] Cylinder029
  Angle = 360
  AttacherType = Attacher::AttachEngine3D
  Height = 10
  Placement = pos=(0,0,36.15) rot=(0,0,1;0rad)
  Radius = 4
FEATURE [Part::MultiFuse] Fusion071  label="removeToCreteHoleForPlugHousing014"
  Placement = pos=(70,19,36) rot=(0,1,0;1.5708rad)
  Shapes = -> [Cylinder028,Cylinder029]
FEATURE [Sketcher::SketchObject] Sketch049  label="topSketch011"
  FullyConstrained = true
  sketch-geometry (4):
    g0: ArcOfCircle CenterX=105 CenterY=19 CenterZ=0 NormalX=0 NormalY=0 NormalZ=1 AngleXU=0 Radius=20.6155 StartAngle=5.54125 EndAngle=6.28319
    g1: ArcOfCircle CenterX=105 CenterY=19 CenterZ=0 NormalX=0 NormalY=0 NormalZ=1 AngleXU=0 Radius=13 StartAngle=5.54125 EndAngle=6.28319
    g2: LineSegment StartX=118 StartY=19 StartZ=0 EndX=125.616 EndY=19 EndZ=0
    g3: LineSegment StartX=114.583 StartY=10.2157 StartZ=0 EndX=120.197 EndY=5.06982 EndZ=0
  constraints (7):
    c: Block(g0)
    c: Block(g1)
    c: Coincident(g2,g1)
    c: Coincident(g2,g0)
    c: Horizontal(g2)
    c: Coincident(g3,g1)
    c: Coincident(g3,g0)
FEATURE [Part::Box] Box020  label="removeToCreteHoleForPlugHousing015"
  AttacherType = Attacher::AttachEngine3D
  Height = 28.6
  Length = 20
  Placement = pos=(106.15,0,21.7) rot=(0,0,1;0rad)
  Width = 19
FEATURE [Part::MultiFuse] Fusion072  label="removeToCreteHoleForPlugHousing016"
  Shapes = -> [Box020,Fusion071]
FEATURE [Part::Cut] Cut033  label="removeToCreteHoleForPlugHousing017"
  Base = -> Cut032
  Tool = -> Fusion072
FEATURE [Part::Cylinder] Cylinder030
  Angle = 360
  AttacherType = Attacher::AttachEngine3D
  Height = 20
  Placement = pos=(0,0,36.15) rot=(0,0,1;0rad)
  Radius = 14.3
FEATURE [Part::Cylinder] Cylinder031
  Angle = 360
  AttacherType = Attacher::AttachEngine3D
  Height = 10
  Placement = pos=(0,0,36.15) rot=(0,0,1;0rad)
  Radius = 4
FEATURE [Part::Box] Box021  label="removeToCreteHoleForPlugHousing019"
  AttacherType = Attacher::AttachEngine3D
  Height = 28.6
  Length = 20
  Placement = pos=(106.15,0,21.7) rot=(0,0,1;0rad)
  Width = 19
FEATURE [Part::MultiFuse] Fusion074  label="removeToCreteHoleForPlugHousing020"
  Placement = pos=(70,19,36) rot=(0,1,0;1.5708rad)
  Shapes = -> [Cylinder030,Cylinder031]
FEATURE [Part::MultiFuse] Fusion073  label="removeToCreteHoleForPlugHousing018"
  Placement = pos=(0,0,28.3) rot=(0,0,1;0rad)
  Shapes = -> [Box021,Fusion074]
FEATURE [Part::Cylinder] Cylinder032
  Angle = 360
  AttacherType = Attacher::AttachEngine3D
  Height = 20
  Placement = pos=(0,0,36.15) rot=(0,0,1;0rad)
  Radius = 14.3
FEATURE [Part::Cylinder] Cylinder033
  Angle = 360
  AttacherType = Attacher::AttachEngine3D
  Height = 10
  Placement = pos=(0,0,36.15) rot=(0,0,1;0rad)
  Radius = 4
FEATURE [Part::Box] Box022  label="removeToCreteHoleForPlugHousing021"
  AttacherType = Attacher::AttachEngine3D
  Height = 28.6
  Length = 20
  Placement = pos=(106.15,0,21.7) rot=(0,0,1;0rad)
  Width = 19
FEATURE [Part::MultiFuse] Fusion076  label="removeToCreteHoleForPlugHousing023"
  Placement = pos=(70,19,36) rot=(0,1,0;1.5708rad)
  Shapes = -> [Cylinder032,Cylinder033]
FEATURE [Part::MultiFuse] Fusion075  label="removeToCreteHoleForPlugHousing022"
  Placement = pos=(0,0,-28.3) rot=(0,0,1;0rad)
  Shapes = -> [Box022,Fusion076]
FEATURE [Part::MultiFuse] Fusion077  label="removeToCreatePlugHousingBottomBit"
  Shapes = -> [Fusion075,Fusion073]
FEATURE [Part::Cylinder] Cylinder034
  Angle = 360
  AttacherType = Attacher::AttachEngine3D
  Height = 20
  Placement = pos=(0,0,36.15) rot=(0,0,1;0rad)
  Radius = 14
FEATURE [Part::Cylinder] Cylinder035
  Angle = 360
  AttacherType = Attacher::AttachEngine3D
  Height = 10
  Placement = pos=(0,0,36.15) rot=(0,0,1;0rad)
  Radius = 4
FEATURE [Part::MultiFuse] Fusion078  label="removeToCreteHoleForPlugHousing024"
  Placement = pos=(70,19,36) rot=(0,1,0;1.5708rad)
  Shapes = -> [Cylinder034,Cylinder035]
FEATURE [Part::MultiFuse] Fusion079  label="removeToCreatePlugHousingBottomBit001"
  Shapes = -> [Fusion078,Fusion077]
FEATURE [Part::Extrusion] Extrude040  label="bottomPlugHousingBit"
  Base = -> Sketch049
  Dir = (0,0,1)
  DirMode = 2
  FaceMakerClass = Part::FaceMakerBullseye
  LengthFwd = 72
  LengthRev = 0
  Solid = true
  Symmetric = false
FEATURE [Part::Cut] Cut034  label="bottomPlugHousingBit001"
  Base = -> Extrude040
  Placement = pos=(-0.09,0,0) rot=(0,0,1;0rad)
  Tool = -> Fusion079
FEATURE [Part::Box] Box023  label="Cube014"
  AttacherType = Attacher::AttachEngine3D
  Height = 16
  Length = 8
  Placement = pos=(12.7,31.52,28) rot=(0,0,1;0rad)
  Width = 4
FEATURE [Part::Cylinder] Cylinder036
  Angle = 360
  AttacherType = Attacher::AttachEngine3D
  Height = 10
  Placement = pos=(0,0,36.15) rot=(0,0,1;0rad)
  Radius = 4
FEATURE [Part::Cylinder] Cylinder037
  Angle = 360
  AttacherType = Attacher::AttachEngine3D
  Height = 20
  Placement = pos=(0,0,36.15) rot=(0,0,1;0rad)
  Radius = 8.2
FEATURE [Part::MultiFuse] Fusion080  label="removeToCreteHoleForPlugHousing025"
  Placement = pos=(-42,19,36) rot=(0,1,0;1.5708rad)
  Shapes = -> [Cylinder037,Cylinder036]
FEATURE [Sketcher::SketchObject] Sketch050  label="topSketch012"
  FullyConstrained = true
  sketch-geometry (4):
    g0: LineSegment StartX=16.8446 StartY=31.512 StartZ=0 EndX=16.3251 EndY=34.4666 EndZ=0
    g1: ArcOfCircle CenterX=19 CenterY=19.2524 CenterZ=0 NormalX=0 NormalY=0 NormalZ=1 AngleXU=0 Radius=15.4476 StartAngle=1.74483 EndAngle=2.72717
    g2: ArcOfCircle CenterX=19 CenterY=19.2524 CenterZ=0 NormalX=0 NormalY=0 NormalZ=1 AngleXU=0 Radius=12.4476 StartAngle=1.74483 EndAngle=2.73189
    g3: LineSegment StartX=4.86004 StartY=25.4725 StartZ=0 EndX=7.58253 EndY=24.2107 EndZ=0
  constraints (7):
    c: Block(g0)
    c: Coincident(g1,g0)
    c: Coincident(g2,g0)
    c: Coincident(g3,g1)
    c: Coincident(g3,g2)
    c: Block(g1)
    c: Block(g2)
FEATURE [Part::Extrusion] Extrude041
  Base = -> Sketch050
  Dir = (0,0,1)
  DirMode = 2
  FaceMakerClass = Part::FaceMakerBullseye
  LengthFwd = 10.6
  LengthRev = 0
  Placement = pos=(0,0,31) rot=(0,0,1;0rad)
  Solid = true
  Symmetric = false
FEATURE [Part::Cut] Cut035
  Base = -> Extrude041
  Placement = pos=(0,0,-0.3) rot=(0,0,1;0rad)
  Tool = -> Fusion080
FEATURE [Part::Cut] Cut036
  Base = -> Box023
  Tool = -> Cut035
FEATURE [Part::Fillet] Fillet027
  Base = -> Cut036
  Edges = 1 edges r=0.7: [Edge13]
FEATURE [Part::Fillet] Fillet028
  Base = -> Fillet027
  Edges = 1 edges r=0.7: [Edge13]
FEATURE [Part::Fillet] Fillet029
  Base = -> Fillet028
  Edges = 1 edges r=0.7: [Edge16]
FEATURE [Part::Fillet] Fillet030
  Base = -> Fillet029
  Edges = 1 edges r=0.7: [Edge11]
FEATURE [Part::Fillet] Fillet031
  Base = -> Fillet030
  Edges = 1 edges r=0.7: [Edge10]
FEATURE [Part::Fillet] Fillet032
  Base = -> Fillet031
  Edges = 1 edges r=1.2: [Edge5]
FEATURE [Part::Fillet] Fillet033
  Base = -> Fillet032
  Edges = 1 edges r=1.2: [Edge12]
FEATURE [Part::Fillet] Fillet034  label="wireHousingRetainer"
  Base = -> Fillet033
  Edges = 1 edges r=2: [Edge1]
  Placement = pos=(0.3,0,0) rot=(0,0,1;0rad)
FEATURE [Part::Feature] Face099
  shape: bbox 3.5 x 17.8 x 2e-07 mm, 1 faces, 0 solids (baked)
FEATURE [Part::Revolution] Revolve107  label="removeToCreateScrewAndThreadedInsertHole034"
  Angle = 360
  Axis = (0,1,0)
  Base = (0,0,0)
  FaceMakerClass = Part::FaceMakerBullseye
  Placement = pos=(12.5,0,10) rot=(0,0,1;0rad)
  Solid = false
  Source = -> Face099
  Symmetric = false
FEATURE [Part::Feature] Face100
  shape: bbox 3.5 x 17.8 x 2e-07 mm, 1 faces, 0 solids (baked)
FEATURE [Part::Revolution] Revolve108  label="removeToCreateScrewAndThreadedInsertHole035"
  Angle = 360
  Axis = (0,1,0)
  Base = (0,0,0)
  FaceMakerClass = Part::FaceMakerBullseye
  Placement = pos=(12.5,0,62) rot=(0,0,1;0rad)
  Solid = false
  Source = -> Face100
  Symmetric = false
FEATURE [Part::Feature] Face101
  shape: bbox 3.5 x 17.8 x 2e-07 mm, 1 faces, 0 solids (baked)
FEATURE [Part::Revolution] Revolve109  label="removeToCreateScrewAndThreadedInsertHole036"
  Angle = 360
  Axis = (0,1,0)
  Base = (0,0,0)
  FaceMakerClass = Part::FaceMakerBullseye
  Placement = pos=(89.5,0,68.5) rot=(0,0,1;0rad)
  Solid = false
  Source = -> Face101
  Symmetric = false
FEATURE [Part::Feature] Face102
  shape: bbox 3.5 x 17.8 x 2e-07 mm, 1 faces, 0 solids (baked)
FEATURE [Part::Revolution] Revolve110  label="removeToCreateScrewAndThreadedInsertHole037"
  Angle = 360
  Axis = (0,1,0)
  Base = (0,0,0)
  FaceMakerClass = Part::FaceMakerBullseye
  Placement = pos=(89.5,0,3.5) rot=(0,0,1;0rad)
  Solid = false
  Source = -> Face102
  Symmetric = false
FEATURE [Part::Feature] Face103
  shape: bbox 3.5 x 17.8 x 2e-07 mm, 1 faces, 0 solids (baked)
FEATURE [Part::Revolution] Revolve111  label="removeToCreateScrewAndThreadedInsertHole038"
  Angle = 360
  Axis = (0,1,0)
  Base = (0,0,0)
  FaceMakerClass = Part::FaceMakerBullseye
  Placement = pos=(109.5,4.7,3.5) rot=(0,0,1;0rad)
  Solid = false
  Source = -> Face103
  Symmetric = false
FEATURE [Part::Feature] Face104
  shape: bbox 3.5 x 17.8 x 2e-07 mm, 1 faces, 0 solids (baked)
FEATURE [Part::Revolution] Revolve112  label="removeToCreateScrewAndThreadedInsertHole039"
  Angle = 360
  Axis = (0,1,0)
  Base = (0,0,0)
  FaceMakerClass = Part::FaceMakerBullseye
  Placement = pos=(109.5,4.7,68.5) rot=(0,0,1;0rad)
  Solid = false
  Source = -> Face104
  Symmetric = false
FEATURE [Part::MultiFuse] Fusion081  label="removeToCreateScrewAndThreadedInsertHole040"
  Shapes = -> [Revolve107,Revolve108,Revolve109,Revolve110,Revolve111,Revolve112]
FEATURE [Part::MultiFuse] Fusion082  label="casePillars002"
  Shapes = -> [Revolve094,Revolve092,Revolve090,Revolve089,Revolve091,Revolve093]
FEATURE [Part::Cut] Cut037  label="casePillars003"
  Base = -> Fusion082
  Tool = -> Fusion081
FEATURE [Sketcher::SketchObject] Sketch051
  FullyConstrained = true
  Placement = pos=(117,19,0) rot=(0.57735,0.57735,0.57735;2.0944rad)
  sketch-geometry (48):
    g0: LineSegment StartX=-49.19 StartY=69.25 StartZ=0 EndX=-49.19 EndY=66.25 EndZ=0
    g1: LineSegment StartX=-49.19 StartY=63.5 StartZ=0 EndX=-49.19 EndY=60.5 EndZ=0
    g2: LineSegment StartX=-49.19 StartY=57.75 StartZ=0 EndX=-49.19 EndY=54.75 EndZ=0
    g3: LineSegment StartX=-49.19 StartY=52 StartZ=0 EndX=-49.19 EndY=49 EndZ=0
    g4: LineSegment StartX=-49.19 StartY=46.25 StartZ=0 EndX=-49.19 EndY=43.25 EndZ=0
    g5: LineSegment StartX=-49.19 StartY=40.5 StartZ=0 EndX=-49.19 EndY=37.5 EndZ=0
    g6: LineSegment StartX=-49.19 StartY=34.5 StartZ=0 EndX=-49.19 EndY=31.5 EndZ=0
    g7: LineSegment StartX=-49.19 StartY=28.75 StartZ=0 EndX=-49.19 EndY=25.75 EndZ=0
    g8: LineSegment StartX=-49.19 StartY=23 StartZ=0 EndX=-49.19 EndY=20 EndZ=0
    g9: LineSegment StartX=-49.19 StartY=17.25 StartZ=0 EndX=-49.19 EndY=14.25 EndZ=0
    g10: LineSegment StartX=-49.19 StartY=11.5 StartZ=0 EndX=-49.19 EndY=8.5 EndZ=0
    g11: LineSegment StartX=-49.19 StartY=5.75 StartZ=0 EndX=-49.19 EndY=2.75 EndZ=0
    g12: ArcOfCircle CenterX=-1.5 CenterY=67.75 CenterZ=0 NormalX=0 NormalY=0 NormalZ=1 AngleXU=0 Radius=1.5 StartAngle=4.71239 EndAngle=7.85398
    g13: ArcOfCircle CenterX=-1.5 CenterY=62 CenterZ=0 NormalX=0 NormalY=0 NormalZ=1 AngleXU=0 Radius=1.5 StartAngle=4.71239 EndAngle=7.85398
    g14: ArcOfCircle CenterX=-1.5 CenterY=56.25 CenterZ=0 NormalX=0 NormalY=0 NormalZ=1 AngleXU=0 Radius=1.5 StartAngle=4.71239 EndAngle=7.85398
    g15: ArcOfCircle CenterX=-11.49 CenterY=50.5 CenterZ=0 NormalX=0 NormalY=0 NormalZ=1 AngleXU=0 Radius=1.5 StartAngle=4.71239 EndAngle=7.85398
    g16: ArcOfCircle CenterX=-16.28 CenterY=44.75 CenterZ=0 NormalX=0 NormalY=0 NormalZ=1 AngleXU=0 Radius=1.5 StartAngle=4.71239 EndAngle=7.85398
    g17: ArcOfCircle CenterX=-18.2337 CenterY=39 CenterZ=0 NormalX=0 NormalY=0 NormalZ=1 AngleXU=0 Radius=1.5 StartAngle=4.71485 EndAngle=7.85398
    g18: ArcOfCircle CenterX=-16.2837 CenterY=27.25 CenterZ=0 NormalX=0 NormalY=0 NormalZ=1 AngleXU=0 Radius=1.5 StartAngle=4.71485 EndAngle=7.85398
    g19: ArcOfCircle CenterX=-18.2337 CenterY=33 CenterZ=0 NormalX=0 NormalY=0 NormalZ=1 AngleXU=0 Radius=1.5 StartAngle=4.71485 EndAngle=7.85398
    g20: ArcOfCircle CenterX=-11.49 CenterY=21.5 CenterZ=0 NormalX=0 NormalY=0 NormalZ=1 AngleXU=0 Radius=1.5 StartAngle=4.71239 EndAngle=7.85398
    g21: ArcOfCircle CenterX=-1.5 CenterY=4.25 CenterZ=0 NormalX=0 NormalY=0 NormalZ=1 AngleXU=0 Radius=1.5 StartAngle=4.71239 EndAngle=7.85398
    g22: ArcOfCircle CenterX=-1.5 CenterY=10 CenterZ=0 NormalX=0 NormalY=0 NormalZ=1 AngleXU=0 Radius=1.5 StartAngle=4.71239 EndAngle=7.85398
    g23: ArcOfCircle CenterX=-1.5 CenterY=15.75 CenterZ=0 NormalX=0 NormalY=0 NormalZ=1 AngleXU=0 Radius=1.5 StartAngle=4.71239 EndAngle=7.85398
    g24: LineSegment StartX=-49.19 StartY=69.25 StartZ=0 EndX=-1.5 EndY=69.25 EndZ=0
    g25: LineSegment StartX=-49.19 StartY=66.25 StartZ=0 EndX=-1.5 EndY=66.25 EndZ=0
    g26: LineSegment StartX=-49.19 StartY=63.5 StartZ=0 EndX=-1.5 EndY=63.5 EndZ=0
    g27: LineSegment StartX=-49.19 StartY=60.5 StartZ=0 EndX=-1.5 EndY=60.5 EndZ=0
    g28: LineSegment StartX=-49.19 StartY=57.75 StartZ=0 EndX=-1.5 EndY=57.75 EndZ=0
    g29: LineSegment StartX=-49.19 StartY=54.75 StartZ=0 EndX=-1.5 EndY=54.75 EndZ=0
    g30: LineSegment StartX=-49.19 StartY=52 StartZ=0 EndX=-11.49 EndY=52 EndZ=0
    g31: LineSegment StartX=-49.19 StartY=49 StartZ=0 EndX=-11.49 EndY=49 EndZ=0
    g32: LineSegment StartX=-49.19 StartY=46.25 StartZ=0 EndX=-16.28 EndY=46.25 EndZ=0
    g33: LineSegment StartX=-49.19 StartY=43.25 StartZ=0 EndX=-16.28 EndY=43.25 EndZ=0
    g34: LineSegment StartX=-49.19 StartY=40.5 StartZ=0 EndX=-18.2337 EndY=40.5 EndZ=0
    g35: LineSegment StartX=-49.19 StartY=37.5 StartZ=0 EndX=-18.23 EndY=37.5 EndZ=0
    g36: LineSegment StartX=-49.19 StartY=34.5 StartZ=0 EndX=-18.2337 EndY=34.5 EndZ=0
    g37: LineSegment StartX=-49.19 StartY=31.5 StartZ=0 EndX=-18.23 EndY=31.5 EndZ=0
    g38: LineSegment StartX=-49.19 StartY=28.75 StartZ=0 EndX=-16.2837 EndY=28.75 EndZ=0
    g39: LineSegment StartX=-49.19 StartY=25.75 StartZ=0 EndX=-16.28 EndY=25.75 EndZ=0
    g40: LineSegment StartX=-49.19 StartY=23 StartZ=0 EndX=-11.49 EndY=23 EndZ=0
    g41: LineSegment StartX=-49.19 StartY=20 StartZ=0 EndX=-11.49 EndY=20 EndZ=0
    g42: LineSegment StartX=-49.19 StartY=17.25 StartZ=0 EndX=-1.5 EndY=17.25 EndZ=0
    g43: LineSegment StartX=-49.19 StartY=14.25 StartZ=0 EndX=-1.5 EndY=14.25 EndZ=0
    g44: LineSegment StartX=-49.19 StartY=11.5 StartZ=0 EndX=-1.5 EndY=11.5 EndZ=0
    g45: LineSegment StartX=-49.19 StartY=8.5 StartZ=0 EndX=-1.5 EndY=8.5 EndZ=0
    g46: LineSegment StartX=-49.19 StartY=5.75 StartZ=0 EndX=-1.5 EndY=5.75 EndZ=0
    g47: LineSegment StartX=-49.19 StartY=2.75 StartZ=0 EndX=-1.5 EndY=2.75 EndZ=0
  constraints (120):
    c: Vertical(g0)
    c: Distance(g0) = 3
    c: Block(g0)
    c: Vertical(g1)
    c: Distance(g1) = 3
    c: Vertical(g2)
    c: Equal(g0,g2) = 3
    c: Block(g2)
    c: Vertical(g3)
    c: Equal(g1,g3) = 3
    c: Vertical(g4)
    c: Equal(g0,g4) = 3
    c: Block(g4)
    c: Vertical(g5)
    c: Equal(g1,g5) = 3
    c: Vertical(g6)
    c: Equal(g0,g6) = 3
    c: Block(g6)
    c: Vertical(g7)
    c: Equal(g1,g7) = 3
    c: Vertical(g8)
    c: Equal(g0,g8) = 3
    c: Block(g8)
    c: Vertical(g9)
    c: Equal(g1,g9) = 3
    c: Vertical(g10)
    c: Equal(g0,g10) = 3
    c: Block(g10)
    c: Vertical(g11)
    c: Equal(g1,g11) = 3
    c: Block(g12)
    c: Block(g13)
    c: Block(g14)
    c: Block(g15)
    c: Block(g16)
    c: Block(g17)
    c: Block(g18)
    c: Block(g19)
    c: Block(g20)
    c: Block(g21)
    c: Block(g22)
    c: Block(g23)
    c: Block(g11)
    c: Block(g9)
    c: Block(g7)
    c: Block(g5)
    c: Block(g3)
    c: Block(g1)
    c: Coincident(g24,g0)
    c: Coincident(g24,g12)
    c: Horizontal(g24)
    c: Coincident(g25,g0)
    c: Coincident(g25,g12)
    c: Horizontal(g25)
    c: Coincident(g26,g1)
    c: Coincident(g26,g13)
    c: Horizontal(g26)
    c: Coincident(g27,g1)
    c: Coincident(g27,g13)
    c: Horizontal(g27)
    c: Coincident(g28,g2)
    c: Coincident(g28,g14)
    c: Horizontal(g28)
    c: Coincident(g29,g2)
    c: Coincident(g29,g14)
    c: Horizontal(g29)
    c: Coincident(g30,g3)
    c: Coincident(g30,g15)
    c: Horizontal(g30)
    c: Coincident(g31,g3)
    c: Coincident(g31,g15)
    c: Horizontal(g31)
    c: Coincident(g32,g4)
    c: Coincident(g32,g16)
    c: Horizontal(g32)
    c: Coincident(g33,g4)
    c: Coincident(g33,g16)
    c: Horizontal(g33)
    c: Coincident(g34,g5)
    c: Coincident(g34,g17)
    c: Horizontal(g34)
    c: Coincident(g35,g5)
    c: Coincident(g35,g17)
    c: Horizontal(g35)
    c: Coincident(g36,g6)
    c: Coincident(g36,g19)
    c: Horizontal(g36)
    c: Coincident(g37,g6)
    c: Coincident(g37,g19)
    c: Horizontal(g37)
    c: Coincident(g38,g7)
    c: Coincident(g38,g18)
    c: Horizontal(g38)
    c: Coincident(g39,g7)
    c: Coincident(g39,g18)
    c: Horizontal(g39)
    c: Coincident(g40,g8)
    c: Coincident(g40,g20)
    c: Horizontal(g40)
    c: Coincident(g41,g8)
    c: Coincident(g41,g20)
    c: Horizontal(g41)
    c: Coincident(g42,g9)
    c: Coincident(g42,g23)
    c: Horizontal(g42)
    c: Coincident(g43,g9)
    c: Coincident(g43,g23)
    c: Horizontal(g43)
    c: Coincident(g44,g10)
    c: Coincident(g44,g22)
    c: Horizontal(g44)
    c: Coincident(g45,g10)
    c: Coincident(g45,g22)
    c: Horizontal(g45)
    c: Coincident(g46,g11)
    c: Coincident(g46,g21)
    c: Horizontal(g46)
    c: Coincident(g47,g11)
    c: Coincident(g47,g21)
    c: Horizontal(g47)
FEATURE [Part::Extrusion] Extrude042
  Base = -> Sketch051
  Dir = (1,-2e-16,2e-16)
  DirMode = 2
  FaceMakerClass = Part::FaceMakerBullseye
  LengthFwd = 19
  LengthRev = 0
  Placement = pos=(-19,0,0) rot=(0,0,1;0rad)
  Solid = true
  Symmetric = false
FEATURE [Part::Fillet] Fillet035  label="removeToCreateVentalationHoles"
  Base = -> Extrude042
  Edges = <same value as first occurrence — deduplicated (x6 in doc)>
  Placement = pos=(7,0,0) rot=(0,0,1;0rad)
FEATURE [Part::Cut] Cut038  label="top017"
  Base = -> Cut033
  Tool = -> Fillet035
FEATURE [Sketcher::SketchObject] Sketch052  label="bottomSketch001"
  FullyConstrained = true
  sketch-geometry (45):
    g0: LineSegment StartX=6.29999 StartY=8 StartZ=0 EndX=3.29999 EndY=8 EndZ=0
    g1: LineSegment StartX=3.29999 StartY=8 StartZ=0 EndX=3.29999 EndY=-6.03275e-07 EndZ=0
    g2: ArcOfCircle CenterX=8.29999 CenterY=5 CenterZ=0 NormalX=0 NormalY=0 NormalZ=1 AngleXU=0 Radius=2 StartAngle=3.14159 EndAngle=4.71239
    g3: LineSegment StartX=6.29999 StartY=8 StartZ=0 EndX=6.29999 EndY=5 EndZ=0
    g4: ArcOfCircle CenterX=105 CenterY=19 CenterZ=0 NormalX=0 NormalY=0 NormalZ=1 AngleXU=0 Radius=12.7 StartAngle=4.71239 EndAngle=5.94289
    g5-g11: Circle x7 (B-spline internal-alignment scaffolding for g12; pole/knot coordinates omitted)
    g12: BSplineCurve PolesCount=7 KnotsCount=5 Degree=3 IsPeriodic=0
    g13-g17: GeomPoint x5 (B-spline internal-alignment scaffolding for g12; pole/knot coordinates omitted)
    g18: ArcOfCircle CenterX=105 CenterY=19 CenterZ=0 NormalX=0 NormalY=0 NormalZ=1 AngleXU=0 Radius=15.7 StartAngle=5.81226 EndAngle=6.28319
    g19: BSplineCurve PolesCount=5 KnotsCount=3 Degree=3 IsPeriodic=0
    g20: LineSegment StartX=8.29999 StartY=3 StartZ=0 EndX=101.7 EndY=3 EndZ=0
    g21: LineSegment StartX=3.29999 StartY=-6.03275e-07 StartZ=0 EndX=105 EndY=-6.03275e-07 EndZ=0
    g22: LineSegment StartX=120.974 StartY=8.71251 StartZ=0 EndX=122.332 EndY=7.83778 EndZ=0
    g23: LineSegment StartX=105 StartY=-6.03274e-07 StartZ=0 EndX=113 EndY=-6.03274e-07 EndZ=0
    g24: ArcOfCircle CenterX=105 CenterY=19 CenterZ=0 NormalX=0 NormalY=0 NormalZ=1 AngleXU=0 Radius=20.6155 StartAngle=5.11091 EndAngle=5.71103
    g25: ArcOfCircle CenterX=117.7 CenterY=19 CenterZ=0 NormalX=0 NormalY=0 NormalZ=1 AngleXU=0 Radius=3 StartAngle=1.2e-15 EndAngle=2.10468
    g26: Circle CenterX=116.345 CenterY=16.3232 CenterZ=0 NormalX=0 NormalY=0 NormalZ=1 AngleXU=0 Radius=1
    g27: Circle CenterX=117.24 CenterY=15.7584 CenterZ=0 NormalX=0 NormalY=0 NormalZ=1 AngleXU=0 Radius=1
    g28: Circle CenterX=116.972 CenterY=14.7612 CenterZ=0 NormalX=0 NormalY=0 NormalZ=1 AngleXU=0 Radius=1
    g29: BSplineCurve PolesCount=3 KnotsCount=2 Degree=2 IsPeriodic=0
    g30: GeomPoint X=116.345 Y=16.3232 Z=0
    g31: GeomPoint X=116.972 Y=14.7612 Z=0
    g32: Circle CenterX=115.828 CenterY=17.157 CenterZ=0 NormalX=0 NormalY=0 NormalZ=1 AngleXU=0 Radius=1
    g33: Circle CenterX=115.841 CenterY=16.639 CenterZ=0 NormalX=0 NormalY=0 NormalZ=1 AngleXU=0 Radius=1
    g34: Circle CenterX=116.345 CenterY=16.3232 CenterZ=0 NormalX=0 NormalY=0 NormalZ=1 AngleXU=0 Radius=1
    g35: BSplineCurve PolesCount=3 KnotsCount=2 Degree=2 IsPeriodic=0
    g36: GeomPoint X=115.828 Y=17.157 Z=0
    g37: GeomPoint X=116.345 Y=16.3232 Z=0
    g38: LineSegment StartX=115.828 StartY=17.157 StartZ=0 EndX=115.828 EndY=20.8307 EndZ=0
    g39: Circle CenterX=115.828 CenterY=20.8307 CenterZ=0 NormalX=0 NormalY=0 NormalZ=1 AngleXU=0 Radius=1
    g40: Circle CenterX=115.831 CenterY=21.3396 CenterZ=0 NormalX=0 NormalY=0 NormalZ=1 AngleXU=0 Radius=1
    g41: Circle CenterX=116.173 CenterY=21.5825 CenterZ=0 NormalX=0 NormalY=0 NormalZ=1 AngleXU=0 Radius=1
    g42: BSplineCurve PolesCount=3 KnotsCount=2 Degree=2 IsPeriodic=0
    g43: GeomPoint X=115.828 Y=20.8307 Z=0
    g44: GeomPoint X=116.173 Y=21.5825 Z=0
  constraints (70):
    c: Horizontal(g0)
    c: Distance(g0) = 3
    c: Coincident(g1,g0)
    c: Vertical(g1)
    c: Block(g2)
    c: Block(g0)
    c: Coincident(g3,g0)
    c: Coincident(g3,g2)
    c: Vertical(g3)
    c: Block(g1)
    c: Block(g4)
    c: Coincident(g19,g4)
    c: Block(g19)
    c: Equal(g5, g6-g11) x6
    c: InternalAlignment(g5-g11 -> g12) x7
    c: InternalAlignment(g13-g17 -> g12) x5
    c: Block(g12)
    c: Coincident(g18,g12)
    c: Block(g18)
    c: Coincident(g20,g2)
    c: Coincident(g20,g19)
    c: Horizontal(g20)
    c: Distance(g20) = 93.4
    c: Coincident(g21,g1)
    c: Horizontal(g21)
    c: Distance(g21) = 101.7
    c: Horizontal(g23)
    c: Distance(g23) = 8
    c: Coincident(g24,g23)
    c: Block(g23)
    c: Coincident(g22,g24)
    c: Block(g24)
    c: Block(g22)
    c: Distance(g22) = 1.61553
    c: Coincident(g25,g18)
    c: Block(g25)
    c: Weight(g26) = 1
    c: Equal(g26,g27)
    c: Equal(g26,g28)
    c: Coincident(g29,g4)
    c: InternalAlignment(g26,g29)
    c: InternalAlignment(g27,g29)
    c: InternalAlignment(g28,g29)
    c: InternalAlignment(g30,g29)
    c: InternalAlignment(g31,g29)
    c: Block(g29)
    c: Weight(g32) = 1
    c: Equal(g32,g33)
    c: Equal(g32,g34)
    c: Coincident(g35,g29)
    c: InternalAlignment(g32,g35)
    c: InternalAlignment(g33,g35)
    c: InternalAlignment(g34,g35)
    c: InternalAlignment(g36,g35)
    c: InternalAlignment(g37,g35)
    c: Block(g35)
    c: Coincident(g38,g35)
    c: Vertical(g38)
    c: Block(g38)
    c: Coincident(g42,g38)
    c: Weight(g39) = 1
    c: Equal(g39,g40)
    c: Equal(g39,g41)
    c: Coincident(g42,g25)
    c: InternalAlignment(g39,g42)
    c: InternalAlignment(g40,g42)
    c: InternalAlignment(g41,g42)
    c: InternalAlignment(g43,g42)
    c: InternalAlignment(g44,g42)
    c: Block(g42)
FEATURE [Part::Extrusion] Extrude043  label="bottom010"
  Base = -> Sketch052
  Dir = (0,0,1)
  DirMode = 2
  FaceMakerClass = Part::FaceMakerBullseye
  LengthFwd = 71.4
  LengthRev = 0
  Placement = pos=(0,0,0.3) rot=(0,0,1;0rad)
  Solid = true
  Symmetric = false
FEATURE [Sketcher::SketchObject] Sketch053  label="topSketch013"
  FullyConstrained = true
  sketch-geometry (22):
    g0: LineSegment StartX=5.21097e-06 StartY=3 StartZ=0 EndX=5.21097e-06 EndY=19 EndZ=0
    g1: ArcOfCircle CenterX=19 CenterY=19 CenterZ=0 NormalX=0 NormalY=0 NormalZ=1 AngleXU=0 Radius=19 StartAngle=1.5708 EndAngle=3.14159
    g2: ArcOfCircle CenterX=19 CenterY=19 CenterZ=0 NormalX=0 NormalY=0 NormalZ=1 AngleXU=0 Radius=16 StartAngle=1.5708 EndAngle=3.14159
    g3: LineSegment StartX=114 StartY=35 StartZ=0 EndX=19 EndY=35 EndZ=0
    g4: LineSegment StartX=5.21097e-06 StartY=3 StartZ=0 EndX=5.21097e-06 EndY=0 EndZ=0
    g5: LineSegment StartX=3 StartY=0 StartZ=0 EndX=5.21097e-06 EndY=0 EndZ=0
    g6: LineSegment StartX=3 StartY=19 StartZ=0 EndX=3 EndY=0 EndZ=0
    g7: LineSegment StartX=19 StartY=38 StartZ=0 EndX=124 EndY=38 EndZ=0
    g8: Circle CenterX=119 CenterY=35 CenterZ=0 NormalX=0 NormalY=0 NormalZ=1 AngleXU=0 Radius=1
    g9: Circle CenterX=121 CenterY=35 CenterZ=0 NormalX=0 NormalY=0 NormalZ=1 AngleXU=0 Radius=1
    g10: Circle CenterX=121 CenterY=33 CenterZ=0 NormalX=0 NormalY=0 NormalZ=1 AngleXU=0 Radius=1
    g11: BSplineCurve PolesCount=3 KnotsCount=2 Degree=2 IsPeriodic=0
    g12: GeomPoint X=119 Y=35 Z=0
    g13: GeomPoint X=121 Y=33 Z=0
    g14: LineSegment StartX=119 StartY=35 StartZ=0 EndX=114 EndY=35 EndZ=0
    g15: ArcOfCircle CenterX=105 CenterY=19 CenterZ=0 NormalX=0 NormalY=0 NormalZ=1 AngleXU=0 Radius=16 StartAngle=5.60905 EndAngle=6.28319
    g16: LineSegment StartX=121 StartY=33 StartZ=0 EndX=121 EndY=19 EndZ=0
    g17: LineSegment StartX=117.5 StartY=9.01251 StartZ=0 EndX=121.163 EndY=9.0125 EndZ=0
    g18: ArcOfCircle CenterX=105 CenterY=19 CenterZ=0 NormalX=0 NormalY=0 NormalZ=1 AngleXU=0 Radius=20.6155 StartAngle=5.7297 EndAngle=6.28319
    g19: LineSegment StartX=121.163 StartY=9.0125 StartZ=0 EndX=122.538 EndY=8.16329 EndZ=0
    g20: LineSegment StartX=124 StartY=38 StartZ=0 EndX=125.616 EndY=38 EndZ=0
    g21: LineSegment StartX=125.616 StartY=19 StartZ=0 EndX=125.616 EndY=38 EndZ=0
  constraints (50):
    c: Vertical(g0)
    c: Block(g0)
    c: Coincident(g1,g0)
    c: Block(g1)
    c: Coincident(g2,g1)
    c: Block(g2)
    c: Coincident(g3,g2)
    c: Horizontal(g3)
    c: Tangent(g3,g2)
    c: Coincident(g4,g0)
    c: Distance(g4) = 3
    c: Vertical(g4)
    c: Coincident(g5,g4)
    c: Horizontal(g5)
    c: Coincident(g6,g2)
    c: Coincident(g6,g5)
    c: Vertical(g6)
    c: Horizontal(g7)
    c: Distance(g7) = 105
    c: Coincident(g7,g1)
    c: Block(g3)
    c: Weight(g8) = 1
    c: Equal(g8,g9)
    c: Equal(g8,g10)
    c: InternalAlignment(g8,g11)
    c: InternalAlignment(g9,g11)
    c: InternalAlignment(g10,g11)
    c: InternalAlignment(g12,g11)
    c: InternalAlignment(g13,g11)
    c: Block(g11)
    c: Coincident(g14,g11)
    c: Coincident(g14,g3)
    c: Horizontal(g14)
    c: Block(g15)
    c: Coincident(g16,g11)
    c: Coincident(g16,g15)
    c: Vertical(g16)
    c: Distance(g16) = 14
    c: Coincident(g17,g15)
    c: Block(g18)
    c: Coincident(g19,g18)
    c: Coincident(g20,g7)
    c: Horizontal(g20)
    c: Vertical(g21)
    c: Coincident(g20,g21)
    c: Block(g20)
    c: Block(g21)
    c: Block(g19)
    c: Block(g17)
    c: Distance(g20) = 1.61553
FEATURE [Part::Extrusion] Extrude044
  Base = -> Sketch053
  Dir = (0,0,1)
  DirMode = 2
  FaceMakerClass = Part::FaceMakerBullseye
  LengthFwd = 72
  LengthRev = 0
  Solid = true
  Symmetric = false
FEATURE [Part::Fillet] Fillet036  label="top018"
  Base = -> Extrude044
  Edges = 1 edges r=2: [Edge41]
FEATURE [Sketcher::SketchObject] Sketch054
  FullyConstrained = false
  Placement = pos=(0,0,0) rot=(1,0,0;1.5708rad)
  sketch-geometry (24):
    g0: ArcOfCircle CenterX=-4 CenterY=-10.5 CenterZ=0 NormalX=0 NormalY=0 NormalZ=1 AngleXU=0 Radius=1.5 StartAngle=6e-16 EndAngle=3.14159
    g1: ArcOfCircle CenterX=-34.2 CenterY=-10.5 CenterZ=0 NormalX=0 NormalY=0 NormalZ=1 AngleXU=0 Radius=1.5 StartAngle=0 EndAngle=3.14159
    g2: ArcOfCircle CenterX=-34.2 CenterY=-27.7 CenterZ=0 NormalX=0 NormalY=0 NormalZ=1 AngleXU=0 Radius=1.5 StartAngle=3.14159 EndAngle=6.28319
    g3: ArcOfCircle CenterX=-4 CenterY=-27.7 CenterZ=0 NormalX=0 NormalY=0 NormalZ=1 AngleXU=0 Radius=1.5 StartAngle=3.1416 EndAngle=6.28319
    g4: ArcOfCircle CenterX=-10 CenterY=-4.3 CenterZ=0 NormalX=0 NormalY=0 NormalZ=1 AngleXU=0 Radius=1.5 StartAngle=2e-16 EndAngle=3.14159
    g5: ArcOfCircle CenterX=-16.1 CenterY=-1.8 CenterZ=0 NormalX=0 NormalY=0 NormalZ=1 AngleXU=0 Radius=1.5 StartAngle=5e-16 EndAngle=3.14159
    g6: ArcOfCircle CenterX=-22.1 CenterY=-1.8 CenterZ=0 NormalX=0 NormalY=0 NormalZ=1 AngleXU=0 Radius=1.5 StartAngle=5e-16 EndAngle=3.14159
    g7: ArcOfCircle CenterX=-28.2 CenterY=-4.3 CenterZ=0 NormalX=0 NormalY=0 NormalZ=1 AngleXU=0 Radius=1.5 StartAngle=2e-16 EndAngle=3.14159
    g8: ArcOfCircle CenterX=-10 CenterY=-33.9 CenterZ=0 NormalX=0 NormalY=0 NormalZ=1 AngleXU=0 Radius=1.5 StartAngle=3.14159 EndAngle=6.28319
    g9: ArcOfCircle CenterX=-16.1 CenterY=-36.4 CenterZ=0 NormalX=0 NormalY=0 NormalZ=1 AngleXU=0 Radius=1.5 StartAngle=3.14159 EndAngle=6.28319
    g10: ArcOfCircle CenterX=-22.1 CenterY=-36.4 CenterZ=0 NormalX=0 NormalY=0 NormalZ=1 AngleXU=0 Radius=1.5 StartAngle=3.14159 EndAngle=6.28319
    g11: ArcOfCircle CenterX=-28.2 CenterY=-33.9 CenterZ=0 NormalX=0 NormalY=0 NormalZ=1 AngleXU=0 Radius=1.5 StartAngle=3.14159 EndAngle=6.28319
    g12: LineSegment StartX=-35.7 StartY=-10.5 StartZ=0 EndX=-35.7 EndY=-27.7 EndZ=0
    g13: LineSegment StartX=-32.7 StartY=-10.5 StartZ=0 EndX=-32.7 EndY=-27.7 EndZ=0
    g14: LineSegment StartX=-29.7 StartY=-33.9 StartZ=0 EndX=-29.7 EndY=-4.3 EndZ=0
    g15: LineSegment StartX=-26.7 StartY=-33.9 StartZ=0 EndX=-26.7 EndY=-4.3 EndZ=0
    g16: LineSegment StartX=-2.5 StartY=-10.5 StartZ=0 EndX=-2.5 EndY=-27.7 EndZ=0
    g17: LineSegment StartX=-8.5 StartY=-4.3 StartZ=0 EndX=-8.5 EndY=-33.9 EndZ=0
    g18: LineSegment StartX=-5.5 StartY=-10.5 StartZ=0 EndX=-5.5 EndY=-27.7 EndZ=0
    g19: LineSegment StartX=-11.5 StartY=-4.3 StartZ=0 EndX=-11.5 EndY=-33.9 EndZ=0
    g20: LineSegment StartX=-14.6 StartY=-1.8 StartZ=0 EndX=-14.6 EndY=-36.4 EndZ=0
    g21: LineSegment StartX=-17.6 StartY=-1.8 StartZ=0 EndX=-17.6 EndY=-36.4 EndZ=0
    g22: LineSegment StartX=-20.6 StartY=-36.4 StartZ=0 EndX=-20.6 EndY=-1.8 EndZ=0
    g23: LineSegment StartX=-23.6 StartY=-1.8 StartZ=0 EndX=-23.6 EndY=-36.4 EndZ=0
  constraints (48):
    c: Block(g0)
    c: Block(g1)
    c: Block(g2)
    c: Block(g3)
    c: Block(g4)
    c: Block(g5)
    c: Block(g6)
    c: Block(g7)
    c: Block(g8)
    c: Block(g9)
    c: Block(g10)
    c: Block(g11)
    c: Coincident(g12,g1)
    c: Coincident(g12,g2)
    c: Vertical(g12)
    c: Coincident(g13,g1)
    c: Coincident(g13,g2)
    c: Vertical(g13)
    c: Coincident(g14,g11)
    c: Coincident(g14,g7)
    c: Vertical(g14)
    c: Coincident(g15,g11)
    c: Coincident(g15,g7)
    c: Vertical(g15)
    c: Coincident(g16,g0)
    c: Coincident(g16,g3)
    c: Vertical(g16)
    c: Coincident(g17,g4)
    c: Coincident(g17,g8)
    c: Vertical(g17)
    c: Coincident(g18,g0)
    c: Coincident(g18,g3)
    c: Vertical(g18)
    c: Coincident(g19,g4)
    c: Coincident(g19,g8)
    c: Vertical(g19)
    c: Coincident(g20,g5)
    c: Coincident(g20,g9)
    c: Vertical(g20)
    c: Coincident(g21,g5)
    c: Coincident(g21,g9)
    c: Vertical(g21)
    c: Coincident(g22,g10)
    c: Coincident(g22,g6)
    c: Vertical(g22)
    c: Coincident(g23,g6)
    c: Coincident(g23,g10)
    c: Vertical(g23)
FEATURE [Part::Extrusion] Extrude045  label="removeToCreateFanGrillHoles003"
  Base = -> Sketch054
  Dir = (0,-1,6e-16)
  DirMode = 2
  FaceMakerClass = Part::FaceMakerBullseye
  LengthFwd = 10
  LengthRev = 0
  Placement = pos=(65.4,44,54.82) rot=(0,0,1;0rad)
  Solid = true
  Symmetric = false
FEATURE [Part::Feature] Face105 .. Face108  x4 (patterned run collapsed; names and placements below)
  shape: bbox 3.5 x 17.8 x 2e-07 mm, 1 faces, 0 solids (baked)
FEATURE [Part::Revolution] Revolve113  label="removeToCreateScrewAndThreadedInsertHole041"
  Angle = 360
  Axis = (0,1,0)
  Base = (0,0,0)
  FaceMakerClass = Part::FaceMakerBullseye
  Placement = pos=(62.3,30.3,19.7) rot=(0,0,1;0rad)
  Solid = false
  Source = -> Face105
  Symmetric = false
FEATURE [Part::Revolution] Revolve114  label="removeToCreateScrewAndThreadedInsertHole042"
  Angle = 360
  Axis = (0,1,0)
  Base = (0,0,0)
  FaceMakerClass = Part::FaceMakerBullseye
  Placement = pos=(62.3,30.3,51.7) rot=(0,0,1;0rad)
  Solid = false
  Source = -> Face106
  Symmetric = false
FEATURE [Part::Revolution] Revolve115  label="removeToCreateScrewAndThreadedInsertHole043"
  Angle = 360
  Axis = (0,1,0)
  Base = (0,0,0)
  FaceMakerClass = Part::FaceMakerBullseye
  Placement = pos=(30.3,30.3,19.7) rot=(0,0,1;0rad)
  Solid = false
  Source = -> Face107
  Symmetric = false
FEATURE [Part::Revolution] Revolve116  label="removeToCreateScrewAndThreadedInsertHole044"
  Angle = 360
  Axis = (0,1,0)
  Base = (0,0,0)
  FaceMakerClass = Part::FaceMakerBullseye
  Placement = pos=(30.3,30.3,51.7) rot=(0,0,1;0rad)
  Solid = false
  Source = -> Face108
  Symmetric = false
FEATURE [Part::MultiFuse] Fusion083  label="createThreadedInsertHolesForFan004"
  Shapes = -> [Revolve113,Revolve114,Revolve115,Revolve116]
FEATURE [Part::Box] Box024  label="removeToCreteHoleForPlugHousing026"
  AttacherType = Attacher::AttachEngine3D
  Height = 28.6
  Length = 10
  Placement = pos=(-2,0,21.7) rot=(0,0,1;0rad)
  Width = 19
FEATURE [Part::Cylinder] Cylinder038  label="removeToCreteHoleForPlugHousing027"
  Angle = 360
  AttacherType = Attacher::AttachEngine3D
  Height = 20
  Placement = pos=(-2,19,36) rot=(0,1,0;1.5708rad)
  Radius = 14.3
FEATURE [Part::MultiFuse] Fusion084  label="removeToCreteHoleForPlugHousing028"
  Shapes = -> [Box024,Cylinder038]
FEATURE [Part::Cylinder] Cylinder039
  Angle = 360
  AttacherType = Attacher::AttachEngine3D
  Height = 20
  Placement = pos=(0,0,36.15) rot=(0,0,1;0rad)
  Radius = 14.3
FEATURE [Part::Cylinder] Cylinder040
  Angle = 360
  AttacherType = Attacher::AttachEngine3D
  Height = 10
  Placement = pos=(0,0,36.15) rot=(0,0,1;0rad)
  Radius = 4
FEATURE [Part::Box] Box025  label="removeToCreteHoleForPlugHousing030"
  AttacherType = Attacher::AttachEngine3D
  Height = 28.6
  Length = 20
  Placement = pos=(106.15,0,21.7) rot=(0,0,1;0rad)
  Width = 19
FEATURE [Part::MultiFuse] Fusion086  label="removeToCreteHoleForPlugHousing031"
  Placement = pos=(70,19,36) rot=(0,1,0;1.5708rad)
  Shapes = -> [Cylinder039,Cylinder040]
FEATURE [Part::MultiFuse] Fusion085  label="removeToCreteHoleForPlugHousing029"
  Shapes = -> [Box025,Fusion086]
FEATURE [Sketcher::SketchObject] Sketch055
  FullyConstrained = true
  Placement = pos=(117,19,0) rot=(0.57735,0.57735,0.57735;2.0944rad)
  sketch-geometry (48):
    g0: LineSegment StartX=-49.19 StartY=69.25 StartZ=0 EndX=-49.19 EndY=66.25 EndZ=0
    g1: LineSegment StartX=-49.19 StartY=63.5 StartZ=0 EndX=-49.19 EndY=60.5 EndZ=0
    g2: LineSegment StartX=-49.19 StartY=57.75 StartZ=0 EndX=-49.19 EndY=54.75 EndZ=0
    g3: LineSegment StartX=-49.19 StartY=52 StartZ=0 EndX=-49.19 EndY=49 EndZ=0
    g4: LineSegment StartX=-49.19 StartY=46.25 StartZ=0 EndX=-49.19 EndY=43.25 EndZ=0
    g5: LineSegment StartX=-49.19 StartY=40.5 StartZ=0 EndX=-49.19 EndY=37.5 EndZ=0
    g6: LineSegment StartX=-49.19 StartY=34.5 StartZ=0 EndX=-49.19 EndY=31.5 EndZ=0
    g7: LineSegment StartX=-49.19 StartY=28.75 StartZ=0 EndX=-49.19 EndY=25.75 EndZ=0
    g8: LineSegment StartX=-49.19 StartY=23 StartZ=0 EndX=-49.19 EndY=20 EndZ=0
    g9: LineSegment StartX=-49.19 StartY=17.25 StartZ=0 EndX=-49.19 EndY=14.25 EndZ=0
    g10: LineSegment StartX=-49.19 StartY=11.5 StartZ=0 EndX=-49.19 EndY=8.5 EndZ=0
    g11: LineSegment StartX=-49.19 StartY=5.75 StartZ=0 EndX=-49.19 EndY=2.75 EndZ=0
    g12: ArcOfCircle CenterX=-1.5 CenterY=67.75 CenterZ=0 NormalX=0 NormalY=0 NormalZ=1 AngleXU=0 Radius=1.5 StartAngle=4.71239 EndAngle=7.85398
    g13: ArcOfCircle CenterX=-1.5 CenterY=62 CenterZ=0 NormalX=0 NormalY=0 NormalZ=1 AngleXU=0 Radius=1.5 StartAngle=4.71239 EndAngle=7.85398
    g14: ArcOfCircle CenterX=-1.5 CenterY=56.25 CenterZ=0 NormalX=0 NormalY=0 NormalZ=1 AngleXU=0 Radius=1.5 StartAngle=4.71239 EndAngle=7.85398
    g15: ArcOfCircle CenterX=-11.49 CenterY=50.5 CenterZ=0 NormalX=0 NormalY=0 NormalZ=1 AngleXU=0 Radius=1.5 StartAngle=4.71239 EndAngle=7.85398
    g16: ArcOfCircle CenterX=-16.28 CenterY=44.75 CenterZ=0 NormalX=0 NormalY=0 NormalZ=1 AngleXU=0 Radius=1.5 StartAngle=4.71239 EndAngle=7.85398
    g17: ArcOfCircle CenterX=-18.2337 CenterY=39 CenterZ=0 NormalX=0 NormalY=0 NormalZ=1 AngleXU=0 Radius=1.5 StartAngle=4.71485 EndAngle=7.85398
    g18: ArcOfCircle CenterX=-16.2837 CenterY=27.25 CenterZ=0 NormalX=0 NormalY=0 NormalZ=1 AngleXU=0 Radius=1.5 StartAngle=4.71485 EndAngle=7.85398
    g19: ArcOfCircle CenterX=-18.2337 CenterY=33 CenterZ=0 NormalX=0 NormalY=0 NormalZ=1 AngleXU=0 Radius=1.5 StartAngle=4.71485 EndAngle=7.85398
    g20: ArcOfCircle CenterX=-11.49 CenterY=21.5 CenterZ=0 NormalX=0 NormalY=0 NormalZ=1 AngleXU=0 Radius=1.5 StartAngle=4.71239 EndAngle=7.85398
    g21: ArcOfCircle CenterX=-1.5 CenterY=4.25 CenterZ=0 NormalX=0 NormalY=0 NormalZ=1 AngleXU=0 Radius=1.5 StartAngle=4.71239 EndAngle=7.85398
    g22: ArcOfCircle CenterX=-1.5 CenterY=10 CenterZ=0 NormalX=0 NormalY=0 NormalZ=1 AngleXU=0 Radius=1.5 StartAngle=4.71239 EndAngle=7.85398
    g23: ArcOfCircle CenterX=-1.5 CenterY=15.75 CenterZ=0 NormalX=0 NormalY=0 NormalZ=1 AngleXU=0 Radius=1.5 StartAngle=4.71239 EndAngle=7.85398
    g24: LineSegment StartX=-49.19 StartY=69.25 StartZ=0 EndX=-1.5 EndY=69.25 EndZ=0
    g25: LineSegment StartX=-49.19 StartY=66.25 StartZ=0 EndX=-1.5 EndY=66.25 EndZ=0
    g26: LineSegment StartX=-49.19 StartY=63.5 StartZ=0 EndX=-1.5 EndY=63.5 EndZ=0
    g27: LineSegment StartX=-49.19 StartY=60.5 StartZ=0 EndX=-1.5 EndY=60.5 EndZ=0
    g28: LineSegment StartX=-49.19 StartY=57.75 StartZ=0 EndX=-1.5 EndY=57.75 EndZ=0
    g29: LineSegment StartX=-49.19 StartY=54.75 StartZ=0 EndX=-1.5 EndY=54.75 EndZ=0
    g30: LineSegment StartX=-49.19 StartY=52 StartZ=0 EndX=-11.49 EndY=52 EndZ=0
    g31: LineSegment StartX=-49.19 StartY=49 StartZ=0 EndX=-11.49 EndY=49 EndZ=0
    g32: LineSegment StartX=-49.19 StartY=46.25 StartZ=0 EndX=-16.28 EndY=46.25 EndZ=0
    g33: LineSegment StartX=-49.19 StartY=43.25 StartZ=0 EndX=-16.28 EndY=43.25 EndZ=0
    g34: LineSegment StartX=-49.19 StartY=40.5 StartZ=0 EndX=-18.2337 EndY=40.5 EndZ=0
    g35: LineSegment StartX=-49.19 StartY=37.5 StartZ=0 EndX=-18.23 EndY=37.5 EndZ=0
    g36: LineSegment StartX=-49.19 StartY=34.5 StartZ=0 EndX=-18.2337 EndY=34.5 EndZ=0
    g37: LineSegment StartX=-49.19 StartY=31.5 StartZ=0 EndX=-18.23 EndY=31.5 EndZ=0
    g38: LineSegment StartX=-49.19 StartY=28.75 StartZ=0 EndX=-16.2837 EndY=28.75 EndZ=0
    g39: LineSegment StartX=-49.19 StartY=25.75 StartZ=0 EndX=-16.28 EndY=25.75 EndZ=0
    g40: LineSegment StartX=-49.19 StartY=23 StartZ=0 EndX=-11.49 EndY=23 EndZ=0
    g41: LineSegment StartX=-49.19 StartY=20 StartZ=0 EndX=-11.49 EndY=20 EndZ=0
    g42: LineSegment StartX=-49.19 StartY=17.25 StartZ=0 EndX=-1.5 EndY=17.25 EndZ=0
    g43: LineSegment StartX=-49.19 StartY=14.25 StartZ=0 EndX=-1.5 EndY=14.25 EndZ=0
    g44: LineSegment StartX=-49.19 StartY=11.5 StartZ=0 EndX=-1.5 EndY=11.5 EndZ=0
    g45: LineSegment StartX=-49.19 StartY=8.5 StartZ=0 EndX=-1.5 EndY=8.5 EndZ=0
    g46: LineSegment StartX=-49.19 StartY=5.75 StartZ=0 EndX=-1.5 EndY=5.75 EndZ=0
    g47: LineSegment StartX=-49.19 StartY=2.75 StartZ=0 EndX=-1.5 EndY=2.75 EndZ=0
  constraints (120):
    c: Vertical(g0)
    c: Distance(g0) = 3
    c: Block(g0)
    c: Vertical(g1)
    c: Distance(g1) = 3
    c: Vertical(g2)
    c: Equal(g0,g2) = 3
    c: Block(g2)
    c: Vertical(g3)
    c: Equal(g1,g3) = 3
    c: Vertical(g4)
    c: Equal(g0,g4) = 3
    c: Block(g4)
    c: Vertical(g5)
    c: Equal(g1,g5) = 3
    c: Vertical(g6)
    c: Equal(g0,g6) = 3
    c: Block(g6)
    c: Vertical(g7)
    c: Equal(g1,g7) = 3
    c: Vertical(g8)
    c: Equal(g0,g8) = 3
    c: Block(g8)
    c: Vertical(g9)
    c: Equal(g1,g9) = 3
    c: Vertical(g10)
    c: Equal(g0,g10) = 3
    c: Block(g10)
    c: Vertical(g11)
    c: Equal(g1,g11) = 3
    c: Block(g12)
    c: Block(g13)
    c: Block(g14)
    c: Block(g15)
    c: Block(g16)
    c: Block(g17)
    c: Block(g18)
    c: Block(g19)
    c: Block(g20)
    c: Block(g21)
    c: Block(g22)
    c: Block(g23)
    c: Block(g11)
    c: Block(g9)
    c: Block(g7)
    c: Block(g5)
    c: Block(g3)
    c: Block(g1)
    c: Coincident(g24,g0)
    c: Coincident(g24,g12)
    c: Horizontal(g24)
    c: Coincident(g25,g0)
    c: Coincident(g25,g12)
    c: Horizontal(g25)
    c: Coincident(g26,g1)
    c: Coincident(g26,g13)
    c: Horizontal(g26)
    c: Coincident(g27,g1)
    c: Coincident(g27,g13)
    c: Horizontal(g27)
    c: Coincident(g28,g2)
    c: Coincident(g28,g14)
    c: Horizontal(g28)
    c: Coincident(g29,g2)
    c: Coincident(g29,g14)
    c: Horizontal(g29)
    c: Coincident(g30,g3)
    c: Coincident(g30,g15)
    c: Horizontal(g30)
    c: Coincident(g31,g3)
    c: Coincident(g31,g15)
    c: Horizontal(g31)
    c: Coincident(g32,g4)
    c: Coincident(g32,g16)
    c: Horizontal(g32)
    c: Coincident(g33,g4)
    c: Coincident(g33,g16)
    c: Horizontal(g33)
    c: Coincident(g34,g5)
    c: Coincident(g34,g17)
    c: Horizontal(g34)
    c: Coincident(g35,g5)
    c: Coincident(g35,g17)
    c: Horizontal(g35)
    c: Coincident(g36,g6)
    c: Coincident(g36,g19)
    c: Horizontal(g36)
    c: Coincident(g37,g6)
    c: Coincident(g37,g19)
    c: Horizontal(g37)
    c: Coincident(g38,g7)
    c: Coincident(g38,g18)
    c: Horizontal(g38)
    c: Coincident(g39,g7)
    c: Coincident(g39,g18)
    c: Horizontal(g39)
    c: Coincident(g40,g8)
    c: Coincident(g40,g20)
    c: Horizontal(g40)
    c: Coincident(g41,g8)
    c: Coincident(g41,g20)
    c: Horizontal(g41)
    c: Coincident(g42,g9)
    c: Coincident(g42,g23)
    c: Horizontal(g42)
    c: Coincident(g43,g9)
    c: Coincident(g43,g23)
    c: Horizontal(g43)
    c: Coincident(g44,g10)
    c: Coincident(g44,g22)
    c: Horizontal(g44)
    c: Coincident(g45,g10)
    c: Coincident(g45,g22)
    c: Horizontal(g45)
    c: Coincident(g46,g11)
    c: Coincident(g46,g21)
    c: Horizontal(g46)
    c: Coincident(g47,g11)
    c: Coincident(g47,g21)
    c: Horizontal(g47)
FEATURE [Part::Extrusion] Extrude046
  Base = -> Sketch055
  Dir = (1,0,0)
  DirMode = 2
  FaceMakerClass = Part::FaceMakerBullseye
  LengthFwd = 23
  LengthRev = 0
  Placement = pos=(-19,0,0) rot=(0,0,1;0rad)
  Solid = true
  Symmetric = false
FEATURE [Part::Fillet] Fillet038  label="removeToCreateVentalationHoles001"
  Base = -> Extrude046
  Edges = <same value as first occurrence — deduplicated (x6 in doc)>
  Placement = pos=(7,0,0) rot=(0,0,1;0rad)
FEATURE [Sketcher::SketchObject] Sketch056  label="topSketch014"
  FullyConstrained = true
  sketch-geometry (22):
    g0: LineSegment StartX=5.21097e-06 StartY=3 StartZ=0 EndX=5.21097e-06 EndY=19 EndZ=0
    g1: ArcOfCircle CenterX=19 CenterY=19 CenterZ=0 NormalX=0 NormalY=0 NormalZ=1 AngleXU=0 Radius=19 StartAngle=1.5708 EndAngle=3.14159
    g2: ArcOfCircle CenterX=19 CenterY=19 CenterZ=0 NormalX=0 NormalY=0 NormalZ=1 AngleXU=0 Radius=16 StartAngle=1.5708 EndAngle=3.14159
    g3: LineSegment StartX=114 StartY=35 StartZ=0 EndX=19 EndY=35 EndZ=0
    g4: LineSegment StartX=5.21097e-06 StartY=3 StartZ=0 EndX=5.21097e-06 EndY=0 EndZ=0
    g5: LineSegment StartX=3 StartY=0 StartZ=0 EndX=5.21097e-06 EndY=0 EndZ=0
    g6: LineSegment StartX=3 StartY=19 StartZ=0 EndX=3 EndY=0 EndZ=0
    g7: LineSegment StartX=19 StartY=38 StartZ=0 EndX=124 EndY=38 EndZ=0
    g8: Circle CenterX=119 CenterY=35 CenterZ=0 NormalX=0 NormalY=0 NormalZ=1 AngleXU=0 Radius=1
    g9: Circle CenterX=121 CenterY=35 CenterZ=0 NormalX=0 NormalY=0 NormalZ=1 AngleXU=0 Radius=1
    g10: Circle CenterX=121 CenterY=33 CenterZ=0 NormalX=0 NormalY=0 NormalZ=1 AngleXU=0 Radius=1
    g11: BSplineCurve PolesCount=3 KnotsCount=2 Degree=2 IsPeriodic=0
    g12: GeomPoint X=119 Y=35 Z=0
    g13: GeomPoint X=121 Y=33 Z=0
    g14: LineSegment StartX=119 StartY=35 StartZ=0 EndX=114 EndY=35 EndZ=0
    g15: ArcOfCircle CenterX=105 CenterY=19 CenterZ=0 NormalX=0 NormalY=0 NormalZ=1 AngleXU=0 Radius=16 StartAngle=5.60905 EndAngle=6.28319
    g16: LineSegment StartX=121 StartY=33 StartZ=0 EndX=121 EndY=19 EndZ=0
    g17: LineSegment StartX=117.5 StartY=9.01251 StartZ=0 EndX=121.163 EndY=9.0125 EndZ=0
    g18: ArcOfCircle CenterX=105 CenterY=19 CenterZ=0 NormalX=0 NormalY=0 NormalZ=1 AngleXU=0 Radius=20.6155 StartAngle=5.7297 EndAngle=6.28319
    g19: LineSegment StartX=121.163 StartY=9.0125 StartZ=0 EndX=122.538 EndY=8.16329 EndZ=0
    g20: LineSegment StartX=124 StartY=38 StartZ=0 EndX=125.616 EndY=38 EndZ=0
    g21: LineSegment StartX=125.616 StartY=19 StartZ=0 EndX=125.616 EndY=38 EndZ=0
  constraints (49):
    c: Vertical(g0)
    c: Block(g0)
    c: Coincident(g1,g0)
    c: Block(g1)
    c: Coincident(g2,g1)
    c: Block(g2)
    c: Coincident(g3,g2)
    c: Horizontal(g3)
    c: Tangent(g3,g2)
    c: Coincident(g4,g0)
    c: Distance(g4) = 3
    c: Vertical(g4)
    c: Coincident(g5,g4)
    c: Horizontal(g5)
    c: Coincident(g6,g2)
    c: Coincident(g6,g5)
    c: Vertical(g6)
    c: Horizontal(g7)
    c: Distance(g7) = 105
    c: Coincident(g7,g1)
    c: Block(g3)
    c: Weight(g8) = 1
    c: Equal(g8,g9)
    c: Equal(g8,g10)
    c: InternalAlignment(g8,g11)
    c: InternalAlignment(g9,g11)
    c: InternalAlignment(g10,g11)
    c: InternalAlignment(g12,g11)
    c: InternalAlignment(g13,g11)
    c: Block(g11)
    c: Coincident(g14,g11)
    c: Coincident(g14,g3)
    c: Horizontal(g14)
    c: Block(g15)
    c: Coincident(g16,g11)
    c: Coincident(g16,g15)
    c: Vertical(g16)
    c: Distance(g16) = 14
    c: Coincident(g17,g15)
    c: Block(g18)
    c: Coincident(g19,g18)
    c: Coincident(g20,g7)
    c: Horizontal(g20)
    c: Vertical(g21)
    c: Coincident(g20,g21)
    c: Block(g20)
    c: Block(g21)
    c: Block(g19)
    c: Block(g17)
FEATURE [Part::Box] Box026  label="removeToCreteHoleForPlugHousing032"
  AttacherType = Attacher::AttachEngine3D
  Height = 28.6
  Length = 10
  Placement = pos=(-2,0,21.7) rot=(0,0,1;0rad)
  Width = 19
FEATURE [Part::Feature] Face109 .. Face112  x4 (patterned run collapsed; names and placements below)
  shape: bbox 3.5 x 17.8 x 2e-07 mm, 1 faces, 0 solids (baked)
FEATURE [Part::Revolution] Revolve117  label="removeToCreateScrewAndThreadedInsertHole045"
  Angle = 360
  Axis = (0,1,0)
  Base = (0,0,0)
  FaceMakerClass = Part::FaceMakerBullseye
  Placement = pos=(62.3,30.3,19.7) rot=(0,0,1;0rad)
  Solid = false
  Source = -> Face109
  Symmetric = false
FEATURE [Part::Revolution] Revolve118  label="removeToCreateScrewAndThreadedInsertHole046"
  Angle = 360
  Axis = (0,1,0)
  Base = (0,0,0)
  FaceMakerClass = Part::FaceMakerBullseye
  Placement = pos=(62.3,30.3,51.7) rot=(0,0,1;0rad)
  Solid = false
  Source = -> Face110
  Symmetric = false
FEATURE [Part::Revolution] Revolve119  label="removeToCreateScrewAndThreadedInsertHole047"
  Angle = 360
  Axis = (0,1,0)
  Base = (0,0,0)
  FaceMakerClass = Part::FaceMakerBullseye
  Placement = pos=(30.3,30.3,19.7) rot=(0,0,1;0rad)
  Solid = false
  Source = -> Face111
  Symmetric = false
FEATURE [Part::Revolution] Revolve120  label="removeToCreateScrewAndThreadedInsertHole048"
  Angle = 360
  Axis = (0,1,0)
  Base = (0,0,0)
  FaceMakerClass = Part::FaceMakerBullseye
  Placement = pos=(30.3,30.3,51.7) rot=(0,0,1;0rad)
  Solid = false
  Source = -> Face112
  Symmetric = false
FEATURE [Part::MultiFuse] Fusion087  label="createThreadedInsertHolesForFan005"
  Shapes = -> [Revolve117,Revolve118,Revolve119,Revolve120]
FEATURE [Part::Extrusion] Extrude047
  Base = -> Sketch056
  Dir = (0,0,1)
  DirMode = 2
  FaceMakerClass = Part::FaceMakerBullseye
  LengthFwd = 72
  LengthRev = 0
  Solid = true
  Symmetric = false
FEATURE [Part::Fillet] Fillet039  label="top019"
  Base = -> Extrude047
  Edges = 1 edges r=2: [Edge35]
FEATURE [Sketcher::SketchObject] Sketch057
  FullyConstrained = false
  Placement = pos=(0,0,0) rot=(1,0,0;1.5708rad)
  sketch-geometry (24):
    g0: ArcOfCircle CenterX=-4 CenterY=-10.5 CenterZ=0 NormalX=0 NormalY=0 NormalZ=1 AngleXU=0 Radius=1.5 StartAngle=6e-16 EndAngle=3.14159
    g1: ArcOfCircle CenterX=-34.2 CenterY=-10.5 CenterZ=0 NormalX=0 NormalY=0 NormalZ=1 AngleXU=0 Radius=1.5 StartAngle=0 EndAngle=3.14159
    g2: ArcOfCircle CenterX=-34.2 CenterY=-27.7 CenterZ=0 NormalX=0 NormalY=0 NormalZ=1 AngleXU=0 Radius=1.5 StartAngle=3.14159 EndAngle=6.28319
    g3: ArcOfCircle CenterX=-4 CenterY=-27.7 CenterZ=0 NormalX=0 NormalY=0 NormalZ=1 AngleXU=0 Radius=1.5 StartAngle=3.1416 EndAngle=6.28319
    g4: ArcOfCircle CenterX=-10 CenterY=-4.3 CenterZ=0 NormalX=0 NormalY=0 NormalZ=1 AngleXU=0 Radius=1.5 StartAngle=2e-16 EndAngle=3.14159
    g5: ArcOfCircle CenterX=-16.1 CenterY=-1.8 CenterZ=0 NormalX=0 NormalY=0 NormalZ=1 AngleXU=0 Radius=1.5 StartAngle=5e-16 EndAngle=3.14159
    g6: ArcOfCircle CenterX=-22.1 CenterY=-1.8 CenterZ=0 NormalX=0 NormalY=0 NormalZ=1 AngleXU=0 Radius=1.5 StartAngle=5e-16 EndAngle=3.14159
    g7: ArcOfCircle CenterX=-28.2 CenterY=-4.3 CenterZ=0 NormalX=0 NormalY=0 NormalZ=1 AngleXU=0 Radius=1.5 StartAngle=2e-16 EndAngle=3.14159
    g8: ArcOfCircle CenterX=-10 CenterY=-33.9 CenterZ=0 NormalX=0 NormalY=0 NormalZ=1 AngleXU=0 Radius=1.5 StartAngle=3.14159 EndAngle=6.28319
    g9: ArcOfCircle CenterX=-16.1 CenterY=-36.4 CenterZ=0 NormalX=0 NormalY=0 NormalZ=1 AngleXU=0 Radius=1.5 StartAngle=3.14159 EndAngle=6.28319
    g10: ArcOfCircle CenterX=-22.1 CenterY=-36.4 CenterZ=0 NormalX=0 NormalY=0 NormalZ=1 AngleXU=0 Radius=1.5 StartAngle=3.14159 EndAngle=6.28319
    g11: ArcOfCircle CenterX=-28.2 CenterY=-33.9 CenterZ=0 NormalX=0 NormalY=0 NormalZ=1 AngleXU=0 Radius=1.5 StartAngle=3.14159 EndAngle=6.28319
    g12: LineSegment StartX=-35.7 StartY=-10.5 StartZ=0 EndX=-35.7 EndY=-27.7 EndZ=0
    g13: LineSegment StartX=-32.7 StartY=-10.5 StartZ=0 EndX=-32.7 EndY=-27.7 EndZ=0
    g14: LineSegment StartX=-29.7 StartY=-33.9 StartZ=0 EndX=-29.7 EndY=-4.3 EndZ=0
    g15: LineSegment StartX=-26.7 StartY=-33.9 StartZ=0 EndX=-26.7 EndY=-4.3 EndZ=0
    g16: LineSegment StartX=-2.5 StartY=-10.5 StartZ=0 EndX=-2.5 EndY=-27.7 EndZ=0
    g17: LineSegment StartX=-8.5 StartY=-4.3 StartZ=0 EndX=-8.5 EndY=-33.9 EndZ=0
    g18: LineSegment StartX=-5.5 StartY=-10.5 StartZ=0 EndX=-5.5 EndY=-27.7 EndZ=0
    g19: LineSegment StartX=-11.5 StartY=-4.3 StartZ=0 EndX=-11.5 EndY=-33.9 EndZ=0
    g20: LineSegment StartX=-14.6 StartY=-1.8 StartZ=0 EndX=-14.6 EndY=-36.4 EndZ=0
    g21: LineSegment StartX=-17.6 StartY=-1.8 StartZ=0 EndX=-17.6 EndY=-36.4 EndZ=0
    g22: LineSegment StartX=-20.6 StartY=-36.4 StartZ=0 EndX=-20.6 EndY=-1.8 EndZ=0
    g23: LineSegment StartX=-23.6 StartY=-1.8 StartZ=0 EndX=-23.6 EndY=-36.4 EndZ=0
  constraints (48):
    c: Block(g0)
    c: Block(g1)
    c: Block(g2)
    c: Block(g3)
    c: Block(g4)
    c: Block(g5)
    c: Block(g6)
    c: Block(g7)
    c: Block(g8)
    c: Block(g9)
    c: Block(g10)
    c: Block(g11)
    c: Coincident(g12,g1)
    c: Coincident(g12,g2)
    c: Vertical(g12)
    c: Coincident(g13,g1)
    c: Coincident(g13,g2)
    c: Vertical(g13)
    c: Coincident(g14,g11)
    c: Coincident(g14,g7)
    c: Vertical(g14)
    c: Coincident(g15,g11)
    c: Coincident(g15,g7)
    c: Vertical(g15)
    c: Coincident(g16,g0)
    c: Coincident(g16,g3)
    c: Vertical(g16)
    c: Coincident(g17,g4)
    c: Coincident(g17,g8)
    c: Vertical(g17)
    c: Coincident(g18,g0)
    c: Coincident(g18,g3)
    c: Vertical(g18)
    c: Coincident(g19,g4)
    c: Coincident(g19,g8)
    c: Vertical(g19)
    c: Coincident(g20,g5)
    c: Coincident(g20,g9)
    c: Vertical(g20)
    c: Coincident(g21,g5)
    c: Coincident(g21,g9)
    c: Vertical(g21)
    c: Coincident(g22,g10)
    c: Coincident(g22,g6)
    c: Vertical(g22)
    c: Coincident(g23,g6)
    c: Coincident(g23,g10)
    c: Vertical(g23)
FEATURE [Part::Extrusion] Extrude048  label="removeToCreateFanGrillHoles004"
  Base = -> Sketch057
  Dir = (0,-1,6e-16)
  DirMode = 2
  FaceMakerClass = Part::FaceMakerBullseye
  LengthFwd = 10
  LengthRev = 0
  Placement = pos=(65.4,44,54.82) rot=(0,0,1;0rad)
  Solid = true
  Symmetric = false
FEATURE [Part::Cut] Cut040  label="top021"
  Base = -> Fillet039
  Tool = -> Extrude048
FEATURE [Part::Cylinder] Cylinder041  label="removeToCreteHoleForPlugHousing034"
  Angle = 360
  AttacherType = Attacher::AttachEngine3D
  Height = 20
  Placement = pos=(-2,19,36) rot=(0,1,0;1.5708rad)
  Radius = 14.3
FEATURE [Part::MultiFuse] Fusion089  label="removeToCreteHoleForPlugHousing035"
  Shapes = -> [Box026,Cylinder041]
FEATURE [Part::Cylinder] Cylinder042
  Angle = 360
  AttacherType = Attacher::AttachEngine3D
  Height = 20
  Placement = pos=(0,0,36.15) rot=(0,0,1;0rad)
  Radius = 14.3
FEATURE [Part::Cylinder] Cylinder043
  Angle = 360
  AttacherType = Attacher::AttachEngine3D
  Height = 10
  Placement = pos=(0,0,36.15) rot=(0,0,1;0rad)
  Radius = 4
FEATURE [Part::Box] Box027  label="removeToCreteHoleForPlugHousing036"
  AttacherType = Attacher::AttachEngine3D
  Height = 28.6
  Length = 20
  Placement = pos=(106.15,0,21.7) rot=(0,0,1;0rad)
  Width = 19
FEATURE [Part::Cut] Cut041  label="top022"
  Base = -> Cut040
  Tool = -> Fusion087
FEATURE [Part::Cut] Cut039  label="top020"
  Base = -> Cut041
  Tool = -> Fusion089
FEATURE [Part::MultiFuse] Fusion090  label="removeToCreteHoleForPlugHousing037"
  Placement = pos=(70,19,36) rot=(0,1,0;1.5708rad)
  Shapes = -> [Cylinder042,Cylinder043]
FEATURE [Part::MultiFuse] Fusion088  label="removeToCreteHoleForPlugHousing033"
  Shapes = -> [Box027,Fusion090]
FEATURE [Part::Cut] Cut042  label="removeToCreteHoleForPlugHousing038"
  Base = -> Cut039
  Tool = -> Fusion088
FEATURE [Part::MultiFuse] Fusion091  label="removeFromTop"
  Shapes = -> [Fillet038,Fusion085,Fusion084,Fusion083,Extrude045]
FEATURE [Part::Cut] Cut043  label="REAL TOP ====="
  Base = -> Fillet036
  Tool = -> Fusion091
FEATURE [Part::MultiFuse] Fusion092  label="caseScrewPillarBracket016"
  Shapes = -> [Extrude030,Extrude031,Extrude032,Extrude033,Extrude034,Extrude035,Extrude036,Extrude037,Box013,Box014]
FEATURE [Sketcher::SketchObject] Sketch058  label="topSketch015"
  FullyConstrained = true
  sketch-geometry (20):
    g0: LineSegment StartX=5.21097e-06 StartY=3 StartZ=0 EndX=5.21097e-06 EndY=19 EndZ=0
    g1: ArcOfCircle CenterX=19 CenterY=19 CenterZ=0 NormalX=0 NormalY=0 NormalZ=1 AngleXU=0 Radius=19 StartAngle=1.5708 EndAngle=3.14159
    g2: ArcOfCircle CenterX=19 CenterY=19 CenterZ=0 NormalX=0 NormalY=0 NormalZ=1 AngleXU=0 Radius=16 StartAngle=1.5708 EndAngle=3.14159
    g3: LineSegment StartX=114 StartY=35 StartZ=0 EndX=19 EndY=35 EndZ=0
    g4: LineSegment StartX=5.21097e-06 StartY=3 StartZ=0 EndX=5.21097e-06 EndY=0 EndZ=0
    g5: LineSegment StartX=3 StartY=0 StartZ=0 EndX=5.21097e-06 EndY=0 EndZ=0
    g6: LineSegment StartX=3 StartY=19 StartZ=0 EndX=3 EndY=0 EndZ=0
    g7: LineSegment StartX=19 StartY=38 StartZ=0 EndX=124 EndY=38 EndZ=0
    g8: Circle CenterX=119 CenterY=35 CenterZ=0 NormalX=0 NormalY=0 NormalZ=1 AngleXU=0 Radius=1
    g9: Circle CenterX=121 CenterY=35 CenterZ=0 NormalX=0 NormalY=0 NormalZ=1 AngleXU=0 Radius=1
    g10: Circle CenterX=121 CenterY=33 CenterZ=0 NormalX=0 NormalY=0 NormalZ=1 AngleXU=0 Radius=1
    g11: BSplineCurve PolesCount=3 KnotsCount=2 Degree=2 IsPeriodic=0
    g12: GeomPoint X=119 Y=35 Z=0
    g13: GeomPoint X=121 Y=33 Z=0
    g14: LineSegment StartX=119 StartY=35 StartZ=0 EndX=114 EndY=35 EndZ=0
    g15: ArcOfCircle CenterX=105 CenterY=19 CenterZ=0 NormalX=0 NormalY=0 NormalZ=1 AngleXU=0 Radius=19 StartAngle=5.7297 EndAngle=6.28319
    g16: ArcOfCircle CenterX=105 CenterY=19 CenterZ=0 NormalX=0 NormalY=0 NormalZ=1 AngleXU=0 Radius=16 StartAngle=5.60905 EndAngle=6.28319
    g17: LineSegment StartX=121 StartY=33 StartZ=0 EndX=121 EndY=19 EndZ=0
    g18: LineSegment StartX=124 StartY=38 StartZ=0 EndX=124 EndY=19 EndZ=0
    g19: LineSegment StartX=117.5 StartY=9.01251 StartZ=0 EndX=121.163 EndY=9.0125 EndZ=0
  constraints (46):
    c: Vertical(g0)
    c: Block(g0)
    c: Coincident(g1,g0)
    c: Block(g1)
    c: Coincident(g2,g1)
    c: Block(g2)
    c: Coincident(g3,g2)
    c: Horizontal(g3)
    c: Tangent(g3,g2)
    c: Coincident(g4,g0)
    c: Distance(g4) = 3
    c: Vertical(g4)
    c: Coincident(g5,g4)
    c: Horizontal(g5)
    c: Coincident(g6,g2)
    c: Coincident(g6,g5)
    c: Vertical(g6)
    c: Horizontal(g7)
    c: Distance(g7) = 105
    c: Coincident(g7,g1)
    c: Block(g3)
    c: Weight(g8) = 1
    c: Equal(g8,g9)
    c: Equal(g8,g10)
    c: InternalAlignment(g8,g11)
    c: InternalAlignment(g9,g11)
    c: InternalAlignment(g10,g11)
    c: InternalAlignment(g12,g11)
    c: InternalAlignment(g13,g11)
    c: Block(g11)
    c: Coincident(g14,g11)
    c: Coincident(g14,g3)
    c: Horizontal(g14)
    c: Block(g15)
    c: Coincident(g16,g15)
    c: Block(g16)
    c: Coincident(g17,g11)
    c: Coincident(g17,g16)
    c: Vertical(g17)
    c: Distance(g17) = 14
    c: Coincident(g18,g7)
    c: Coincident(g18,g15)
    c: Vertical(g18)
    c: Distance(g18) = 19
    c: Coincident(g19,g16)
    c: Coincident(g19,g15)
FEATURE [Part::Extrusion] Extrude049  label="top023"
  Base = -> Sketch058
  Dir = (0,0,1)
  DirMode = 2
  FaceMakerClass = Part::FaceMakerBullseye
  LengthFwd = 72
  LengthRev = 0
  Solid = true
  Symmetric = false
FEATURE [Sketcher::SketchObject] Sketch059
  FullyConstrained = true
  MapMode = 3
  Placement = pos=(0,0,0) rot=(1,0,0;1.5708rad)
  Support = -> [Extrude049]
  sketch-geometry (8):
    g0: Circle CenterX=80.351 CenterY=-67.6202 CenterZ=0 NormalX=0 NormalY=0 NormalZ=1 AngleXU=0 Radius=2
    g1: Circle CenterX=80.351 CenterY=-67.6202 CenterZ=0 NormalX=0 NormalY=0 NormalZ=1 AngleXU=0 Radius=3
    g2: Circle CenterX=80.351 CenterY=-4.92017 CenterZ=0 NormalX=0 NormalY=0 NormalZ=1 AngleXU=0 Radius=2
    g3: Circle CenterX=80.351 CenterY=-4.92017 CenterZ=0 NormalX=0 NormalY=0 NormalZ=1 AngleXU=0 Radius=3
    g4: Circle CenterX=23.851 CenterY=-4.92017 CenterZ=0 NormalX=0 NormalY=0 NormalZ=1 AngleXU=0 Radius=2
    g5: Circle CenterX=23.851 CenterY=-4.92017 CenterZ=0 NormalX=0 NormalY=0 NormalZ=1 AngleXU=0 Radius=3
    g6: Circle CenterX=23.851 CenterY=-67.6202 CenterZ=0 NormalX=0 NormalY=0 NormalZ=1 AngleXU=0 Radius=2
    g7: Circle CenterX=23.851 CenterY=-67.6202 CenterZ=0 NormalX=0 NormalY=0 NormalZ=1 AngleXU=0 Radius=3
  constraints (8):
    c: Block(g3)
    c: Block(g2)
    c: Block(g1)
    c: Block(g0)
    c: Block(g6)
    c: Block(g7)
    c: Block(g4)
    c: Block(g5)
FEATURE [Sketcher::SketchObject] Sketch060
  FullyConstrained = true
  MapMode = 3
  Placement = pos=(0,0,0) rot=(1,0,0;1.5708rad)
  Support = -> [Extrude049]
  sketch-geometry (8):
    g0: Circle CenterX=80.351 CenterY=-67.6202 CenterZ=0 NormalX=0 NormalY=0 NormalZ=1 AngleXU=0 Radius=3
    g1: Circle CenterX=80.351 CenterY=-4.92017 CenterZ=0 NormalX=0 NormalY=0 NormalZ=1 AngleXU=0 Radius=3
    g2: Circle CenterX=23.851 CenterY=-4.92017 CenterZ=0 NormalX=0 NormalY=0 NormalZ=1 AngleXU=0 Radius=3
    g3: Circle CenterX=23.851 CenterY=-67.6202 CenterZ=0 NormalX=0 NormalY=0 NormalZ=1 AngleXU=0 Radius=3
    g4: Circle CenterX=23.851 CenterY=-67.6202 CenterZ=0 NormalX=0 NormalY=0 NormalZ=1 AngleXU=0 Radius=5
    g5: Circle CenterX=80.351 CenterY=-67.6202 CenterZ=0 NormalX=0 NormalY=0 NormalZ=1 AngleXU=0 Radius=5
    g6: Circle CenterX=23.851 CenterY=-4.92017 CenterZ=0 NormalX=0 NormalY=0 NormalZ=1 AngleXU=0 Radius=5
    g7: Circle CenterX=80.351 CenterY=-4.92017 CenterZ=0 NormalX=0 NormalY=0 NormalZ=1 AngleXU=0 Radius=5
  constraints (8):
    c: Block(g1)
    c: Block(g0)
    c: Block(g3)
    c: Block(g2)
    c: Block(g5)
    c: Block(g4)
    c: Block(g6)
    c: Block(g7)
FEATURE [Sketcher::SketchObject] Sketch061
  FullyConstrained = true
  MapMode = 3
  Placement = pos=(0,0,0) rot=(1,0,0;1.5708rad)
  sketch-geometry (8):
    g0: Circle CenterX=80.351 CenterY=-67.6202 CenterZ=0 NormalX=0 NormalY=0 NormalZ=1 AngleXU=0 Radius=3
    g1: Circle CenterX=80.351 CenterY=-4.92017 CenterZ=0 NormalX=0 NormalY=0 NormalZ=1 AngleXU=0 Radius=3
    g2: Circle CenterX=23.851 CenterY=-4.92017 CenterZ=0 NormalX=0 NormalY=0 NormalZ=1 AngleXU=0 Radius=3
    g3: Circle CenterX=23.851 CenterY=-67.6202 CenterZ=0 NormalX=0 NormalY=0 NormalZ=1 AngleXU=0 Radius=3
    g4: Circle CenterX=23.851 CenterY=-67.6202 CenterZ=0 NormalX=0 NormalY=0 NormalZ=1 AngleXU=0 Radius=5
    g5: Circle CenterX=80.351 CenterY=-67.6202 CenterZ=0 NormalX=0 NormalY=0 NormalZ=1 AngleXU=0 Radius=5
    g6: Circle CenterX=23.851 CenterY=-4.92017 CenterZ=0 NormalX=0 NormalY=0 NormalZ=1 AngleXU=0 Radius=5
    g7: Circle CenterX=80.351 CenterY=-4.92017 CenterZ=0 NormalX=0 NormalY=0 NormalZ=1 AngleXU=0 Radius=5
  constraints (8):
    c: Block(g1)
    c: Block(g0)
    c: Block(g3)
    c: Block(g2)
    c: Block(g5)
    c: Block(g4)
    c: Block(g6)
    c: Block(g7)
FEATURE [Sketcher::SketchObject] Sketch062  label="topSketch016"
  FullyConstrained = true
  sketch-geometry (20):
    g0: LineSegment StartX=5.21097e-06 StartY=3 StartZ=0 EndX=5.21097e-06 EndY=19 EndZ=0
    g1: ArcOfCircle CenterX=19 CenterY=19 CenterZ=0 NormalX=0 NormalY=0 NormalZ=1 AngleXU=0 Radius=19 StartAngle=1.5708 EndAngle=3.14159
    g2: ArcOfCircle CenterX=19 CenterY=19 CenterZ=0 NormalX=0 NormalY=0 NormalZ=1 AngleXU=0 Radius=16 StartAngle=1.5708 EndAngle=3.14159
    g3: LineSegment StartX=114 StartY=35 StartZ=0 EndX=19 EndY=35 EndZ=0
    g4: LineSegment StartX=5.21097e-06 StartY=3 StartZ=0 EndX=5.21097e-06 EndY=0 EndZ=0
    g5: LineSegment StartX=3 StartY=0 StartZ=0 EndX=5.21097e-06 EndY=0 EndZ=0
    g6: LineSegment StartX=3 StartY=19 StartZ=0 EndX=3 EndY=0 EndZ=0
    g7: LineSegment StartX=19 StartY=38 StartZ=0 EndX=124 EndY=38 EndZ=0
    g8: Circle CenterX=119 CenterY=35 CenterZ=0 NormalX=0 NormalY=0 NormalZ=1 AngleXU=0 Radius=1
    g9: Circle CenterX=121 CenterY=35 CenterZ=0 NormalX=0 NormalY=0 NormalZ=1 AngleXU=0 Radius=1
    g10: Circle CenterX=121 CenterY=33 CenterZ=0 NormalX=0 NormalY=0 NormalZ=1 AngleXU=0 Radius=1
    g11: BSplineCurve PolesCount=3 KnotsCount=2 Degree=2 IsPeriodic=0
    g12: GeomPoint X=119 Y=35 Z=0
    g13: GeomPoint X=121 Y=33 Z=0
    g14: LineSegment StartX=119 StartY=35 StartZ=0 EndX=114 EndY=35 EndZ=0
    g15: ArcOfCircle CenterX=105 CenterY=19 CenterZ=0 NormalX=0 NormalY=0 NormalZ=1 AngleXU=0 Radius=19 StartAngle=5.7297 EndAngle=6.28319
    g16: ArcOfCircle CenterX=105 CenterY=19 CenterZ=0 NormalX=0 NormalY=0 NormalZ=1 AngleXU=0 Radius=16 StartAngle=5.60905 EndAngle=6.28319
    g17: LineSegment StartX=121 StartY=33 StartZ=0 EndX=121 EndY=19 EndZ=0
    g18: LineSegment StartX=124 StartY=38 StartZ=0 EndX=124 EndY=19 EndZ=0
    g19: LineSegment StartX=117.5 StartY=9.01251 StartZ=0 EndX=121.163 EndY=9.0125 EndZ=0
  constraints (46):
    c: Vertical(g0)
    c: Block(g0)
    c: Coincident(g1,g0)
    c: Block(g1)
    c: Coincident(g2,g1)
    c: Block(g2)
    c: Coincident(g3,g2)
    c: Horizontal(g3)
    c: Tangent(g3,g2)
    c: Coincident(g4,g0)
    c: Distance(g4) = 3
    c: Vertical(g4)
    c: Coincident(g5,g4)
    c: Horizontal(g5)
    c: Coincident(g6,g2)
    c: Coincident(g6,g5)
    c: Vertical(g6)
    c: Horizontal(g7)
    c: Distance(g7) = 105
    c: Coincident(g7,g1)
    c: Block(g3)
    c: Weight(g8) = 1
    c: Equal(g8,g9)
    c: Equal(g8,g10)
    c: InternalAlignment(g8,g11)
    c: InternalAlignment(g9,g11)
    c: InternalAlignment(g10,g11)
    c: InternalAlignment(g12,g11)
    c: InternalAlignment(g13,g11)
    c: Block(g11)
    c: Coincident(g14,g11)
    c: Coincident(g14,g3)
    c: Horizontal(g14)
    c: Block(g15)
    c: Coincident(g16,g15)
    c: Block(g16)
    c: Coincident(g17,g11)
    c: Coincident(g17,g16)
    c: Vertical(g17)
    c: Distance(g17) = 14
    c: Coincident(g18,g7)
    c: Coincident(g18,g15)
    c: Vertical(g18)
    c: Distance(g18) = 19
    c: Coincident(g19,g16)
    c: Coincident(g19,g15)
FEATURE [Part::Extrusion] Extrude053  label="top024"
  Base = -> Sketch062
  Dir = (0,0,1)
  DirMode = 2
  FaceMakerClass = Part::FaceMakerBullseye
  LengthFwd = 72
  LengthRev = 0
  Solid = true
  Symmetric = false
FEATURE [Sketcher::SketchObject] Sketch063
  FullyConstrained = true
  MapMode = 3
  Placement = pos=(0,0,0) rot=(1,0,0;1.5708rad)
  Support = -> [Extrude053]
  sketch-geometry (8):
    g0: Circle CenterX=80.351 CenterY=-67.6202 CenterZ=0 NormalX=0 NormalY=0 NormalZ=1 AngleXU=0 Radius=2
    g1: Circle CenterX=80.351 CenterY=-67.6202 CenterZ=0 NormalX=0 NormalY=0 NormalZ=1 AngleXU=0 Radius=3
    g2: Circle CenterX=80.351 CenterY=-4.92017 CenterZ=0 NormalX=0 NormalY=0 NormalZ=1 AngleXU=0 Radius=2
    g3: Circle CenterX=80.351 CenterY=-4.92017 CenterZ=0 NormalX=0 NormalY=0 NormalZ=1 AngleXU=0 Radius=3
    g4: Circle CenterX=23.851 CenterY=-4.92017 CenterZ=0 NormalX=0 NormalY=0 NormalZ=1 AngleXU=0 Radius=2
    g5: Circle CenterX=23.851 CenterY=-4.92017 CenterZ=0 NormalX=0 NormalY=0 NormalZ=1 AngleXU=0 Radius=3
    g6: Circle CenterX=23.851 CenterY=-67.6202 CenterZ=0 NormalX=0 NormalY=0 NormalZ=1 AngleXU=0 Radius=2
    g7: Circle CenterX=23.851 CenterY=-67.6202 CenterZ=0 NormalX=0 NormalY=0 NormalZ=1 AngleXU=0 Radius=3
  constraints (8):
    c: Block(g3)
    c: Block(g2)
    c: Block(g1)
    c: Block(g0)
    c: Block(g6)
    c: Block(g7)
    c: Block(g4)
    c: Block(g5)
FEATURE [Part::Extrusion] Extrude054
  Base = -> Sketch063
  Dir = (0,-1,2e-16)
  DirMode = 2
  FaceMakerClass = Part::FaceMakerBullseye
  LengthFwd = 6
  LengthRev = 0
  Placement = pos=(0,9,0) rot=(0,0,1;0rad)
  Solid = true
  Symmetric = false
FEATURE [Sketcher::SketchObject] Sketch064  label="topSketch017"
  FullyConstrained = true
  sketch-geometry (20):
    g0: LineSegment StartX=5.21097e-06 StartY=3 StartZ=0 EndX=5.21097e-06 EndY=19 EndZ=0
    g1: ArcOfCircle CenterX=19 CenterY=19 CenterZ=0 NormalX=0 NormalY=0 NormalZ=1 AngleXU=0 Radius=19 StartAngle=1.5708 EndAngle=3.14159
    g2: ArcOfCircle CenterX=19 CenterY=19 CenterZ=0 NormalX=0 NormalY=0 NormalZ=1 AngleXU=0 Radius=16 StartAngle=1.5708 EndAngle=3.14159
    g3: LineSegment StartX=114 StartY=35 StartZ=0 EndX=19 EndY=35 EndZ=0
    g4: LineSegment StartX=5.21097e-06 StartY=3 StartZ=0 EndX=5.21097e-06 EndY=0 EndZ=0
    g5: LineSegment StartX=3 StartY=0 StartZ=0 EndX=5.21097e-06 EndY=0 EndZ=0
    g6: LineSegment StartX=3 StartY=19 StartZ=0 EndX=3 EndY=0 EndZ=0
    g7: LineSegment StartX=19 StartY=38 StartZ=0 EndX=124 EndY=38 EndZ=0
    g8: Circle CenterX=119 CenterY=35 CenterZ=0 NormalX=0 NormalY=0 NormalZ=1 AngleXU=0 Radius=1
    g9: Circle CenterX=121 CenterY=35 CenterZ=0 NormalX=0 NormalY=0 NormalZ=1 AngleXU=0 Radius=1
    g10: Circle CenterX=121 CenterY=33 CenterZ=0 NormalX=0 NormalY=0 NormalZ=1 AngleXU=0 Radius=1
    g11: BSplineCurve PolesCount=3 KnotsCount=2 Degree=2 IsPeriodic=0
    g12: GeomPoint X=119 Y=35 Z=0
    g13: GeomPoint X=121 Y=33 Z=0
    g14: LineSegment StartX=119 StartY=35 StartZ=0 EndX=114 EndY=35 EndZ=0
    g15: ArcOfCircle CenterX=105 CenterY=19 CenterZ=0 NormalX=0 NormalY=0 NormalZ=1 AngleXU=0 Radius=19 StartAngle=5.7297 EndAngle=6.28319
    g16: ArcOfCircle CenterX=105 CenterY=19 CenterZ=0 NormalX=0 NormalY=0 NormalZ=1 AngleXU=0 Radius=16 StartAngle=5.60905 EndAngle=6.28319
    g17: LineSegment StartX=121 StartY=33 StartZ=0 EndX=121 EndY=19 EndZ=0
    g18: LineSegment StartX=124 StartY=38 StartZ=0 EndX=124 EndY=19 EndZ=0
    g19: LineSegment StartX=117.5 StartY=9.01251 StartZ=0 EndX=121.163 EndY=9.0125 EndZ=0
  constraints (46):
    c: Vertical(g0)
    c: Block(g0)
    c: Coincident(g1,g0)
    c: Block(g1)
    c: Coincident(g2,g1)
    c: Block(g2)
    c: Coincident(g3,g2)
    c: Horizontal(g3)
    c: Tangent(g3,g2)
    c: Coincident(g4,g0)
    c: Distance(g4) = 3
    c: Vertical(g4)
    c: Coincident(g5,g4)
    c: Horizontal(g5)
    c: Coincident(g6,g2)
    c: Coincident(g6,g5)
    c: Vertical(g6)
    c: Horizontal(g7)
    c: Distance(g7) = 105
    c: Coincident(g7,g1)
    c: Block(g3)
    c: Weight(g8) = 1
    c: Equal(g8,g9)
    c: Equal(g8,g10)
    c: InternalAlignment(g8,g11)
    c: InternalAlignment(g9,g11)
    c: InternalAlignment(g10,g11)
    c: InternalAlignment(g12,g11)
    c: InternalAlignment(g13,g11)
    c: Block(g11)
    c: Coincident(g14,g11)
    c: Coincident(g14,g3)
    c: Horizontal(g14)
    c: Block(g15)
    c: Coincident(g16,g15)
    c: Block(g16)
    c: Coincident(g17,g11)
    c: Coincident(g17,g16)
    c: Vertical(g17)
    c: Distance(g17) = 14
    c: Coincident(g18,g7)
    c: Coincident(g18,g15)
    c: Vertical(g18)
    c: Distance(g18) = 19
    c: Coincident(g19,g16)
    c: Coincident(g19,g15)
FEATURE [Sketcher::SketchObject] Sketch065
  FullyConstrained = true
  MapMode = 3
  Placement = pos=(0,0,0) rot=(1,0,0;1.5708rad)
  sketch-geometry (8):
    g0: Circle CenterX=80.351 CenterY=-67.6202 CenterZ=0 NormalX=0 NormalY=0 NormalZ=1 AngleXU=0 Radius=3
    g1: Circle CenterX=80.351 CenterY=-4.92017 CenterZ=0 NormalX=0 NormalY=0 NormalZ=1 AngleXU=0 Radius=3
    g2: Circle CenterX=23.851 CenterY=-4.92017 CenterZ=0 NormalX=0 NormalY=0 NormalZ=1 AngleXU=0 Radius=3
    g3: Circle CenterX=23.851 CenterY=-67.6202 CenterZ=0 NormalX=0 NormalY=0 NormalZ=1 AngleXU=0 Radius=3
    g4: Circle CenterX=23.851 CenterY=-67.6202 CenterZ=0 NormalX=0 NormalY=0 NormalZ=1 AngleXU=0 Radius=5
    g5: Circle CenterX=80.351 CenterY=-67.6202 CenterZ=0 NormalX=0 NormalY=0 NormalZ=1 AngleXU=0 Radius=5
    g6: Circle CenterX=23.851 CenterY=-4.92017 CenterZ=0 NormalX=0 NormalY=0 NormalZ=1 AngleXU=0 Radius=5
    g7: Circle CenterX=80.351 CenterY=-4.92017 CenterZ=0 NormalX=0 NormalY=0 NormalZ=1 AngleXU=0 Radius=5
  constraints (8):
    c: Block(g1)
    c: Block(g0)
    c: Block(g3)
    c: Block(g2)
    c: Block(g5)
    c: Block(g4)
    c: Block(g6)
    c: Block(g7)
FEATURE [Part::Extrusion] Extrude056
  Base = -> Sketch065
  Dir = (0,-1,2e-16)
  DirMode = 2
  FaceMakerClass = Part::FaceMakerBullseye
  LengthFwd = 2
  LengthRev = 0
  Solid = true
  Symmetric = false
FEATURE [Part::Extrusion] Extrude057  label="top025"
  Base = -> Sketch064
  Dir = (0,0,1)
  DirMode = 2
  FaceMakerClass = Part::FaceMakerBullseye
  LengthFwd = 72
  LengthRev = 0
  Solid = true
  Symmetric = false
FEATURE [Sketcher::SketchObject] Sketch066
  FullyConstrained = true
  MapMode = 3
  Placement = pos=(0,0,0) rot=(1,0,0;1.5708rad)
  Support = -> [Extrude057]
  sketch-geometry (8):
    g0: Circle CenterX=80.351 CenterY=-67.6202 CenterZ=0 NormalX=0 NormalY=0 NormalZ=1 AngleXU=0 Radius=3
    g1: Circle CenterX=80.351 CenterY=-4.92017 CenterZ=0 NormalX=0 NormalY=0 NormalZ=1 AngleXU=0 Radius=3
    g2: Circle CenterX=23.851 CenterY=-4.92017 CenterZ=0 NormalX=0 NormalY=0 NormalZ=1 AngleXU=0 Radius=3
    g3: Circle CenterX=23.851 CenterY=-67.6202 CenterZ=0 NormalX=0 NormalY=0 NormalZ=1 AngleXU=0 Radius=3
    g4: Circle CenterX=23.851 CenterY=-67.6202 CenterZ=0 NormalX=0 NormalY=0 NormalZ=1 AngleXU=0 Radius=5
    g5: Circle CenterX=80.351 CenterY=-67.6202 CenterZ=0 NormalX=0 NormalY=0 NormalZ=1 AngleXU=0 Radius=5
    g6: Circle CenterX=23.851 CenterY=-4.92017 CenterZ=0 NormalX=0 NormalY=0 NormalZ=1 AngleXU=0 Radius=5
    g7: Circle CenterX=80.351 CenterY=-4.92017 CenterZ=0 NormalX=0 NormalY=0 NormalZ=1 AngleXU=0 Radius=5
  constraints (8):
    c: Block(g1)
    c: Block(g0)
    c: Block(g3)
    c: Block(g2)
    c: Block(g5)
    c: Block(g4)
    c: Block(g6)
    c: Block(g7)
FEATURE [Part::Extrusion] Extrude055
  Base = -> Sketch066
  Dir = (0,-1,2e-16)
  DirMode = 2
  FaceMakerClass = Part::FaceMakerBullseye
  LengthFwd = 2
  LengthRev = 0
  Solid = true
  Symmetric = false
FEATURE [Part::Fillet] Fillet041
  Base = -> Extrude056
  Edges = 4 edges r=1.99: [Edge6,Edge12,Edge18,Edge24]
FEATURE [Part::Cut] Cut045
  Base = -> Extrude055
  Placement = pos=(0,6,0) rot=(0,0,1;0rad)
  Tool = -> Fillet041
FEATURE [Part::MultiFuse] Fusion095  label="pcbScrewPillars"
  Placement = pos=(-3.2,-1,72.3) rot=(0,0,1;0rad)
  Shapes = -> [Cut045,Extrude054]
FEATURE [Part::Feature] Face113
  shape: bbox 3.2 x 1.5 x 2e-07 mm, 1 faces, 0 solids (baked)
FEATURE [Part::Revolution] Revolve121  label="backCaseScrewRetainer002"
  Angle = 360
  Axis = (0,1,0)
  Base = (0,0,0)
  FaceMakerClass = Part::FaceMakerBullseye
  Placement = pos=(12.5,3,62) rot=(0,0,1;0rad)
  Solid = false
  Source = -> Face113
  Symmetric = false
FEATURE [Part::Feature] Face114
  shape: bbox 3.2 x 1.5 x 2e-07 mm, 1 faces, 0 solids (baked)
FEATURE [Part::Feature] Face115
  shape: bbox 3.2 x 1.5 x 2e-07 mm, 1 faces, 0 solids (baked)
FEATURE [Part::Feature] Face116
  shape: bbox 3.2 x 1.5 x 2e-07 mm, 1 faces, 0 solids (baked)
FEATURE [Part::Revolution] Revolve122  label="frontCaseScrewRetainer004"
  Angle = 360
  Axis = (0,1,0)
  Base = (0,0,0)
  FaceMakerClass = Part::FaceMakerBullseye
  Placement = pos=(89.5,3,68.5) rot=(0,0,1;0rad)
  Solid = false
  Source = -> Face115
  Symmetric = false
FEATURE [Part::Revolution] Revolve123  label="frontCaseScrewRetainer005"
  Angle = 360
  Axis = (0,1,0)
  Base = (0,0,0)
  FaceMakerClass = Part::FaceMakerBullseye
  Placement = pos=(89.5,3,3.5) rot=(0,0,1;0rad)
  Solid = false
  Source = -> Face116
  Symmetric = false
FEATURE [Part::Revolution] Revolve124  label="backCaseScrewRetainer003"
  Angle = 360
  Axis = (0,1,0)
  Base = (0,0,0)
  FaceMakerClass = Part::FaceMakerBullseye
  Placement = pos=(12.5,3,10) rot=(0,0,1;0rad)
  Solid = false
  Source = -> Face114
  Symmetric = false
FEATURE [Part::Feature] Face117
  shape: bbox 3.6 x 3.2 x 2e-07 mm, 1 faces, 0 solids (baked)
FEATURE [Part::Revolution] Revolve125  label="moreFrontCaseScrewRetainer004"
  Angle = 360
  Axis = (0,1,0)
  Base = (0,0,0)
  FaceMakerClass = Part::FaceMakerBullseye
  Placement = pos=(109.5,4.5,68.5) rot=(0,0,1;0rad)
  Solid = false
  Source = -> Face117
  Symmetric = false
FEATURE [Part::Feature] Face118
  shape: bbox 3.6 x 3.2 x 2e-07 mm, 1 faces, 0 solids (baked)
FEATURE [Part::Revolution] Revolve126  label="moreFrontCaseScrewRetainer005"
  Angle = 360
  Axis = (0,1,0)
  Base = (0,0,0)
  FaceMakerClass = Part::FaceMakerBullseye
  Placement = pos=(109.5,4.5,3.5) rot=(0,0,1;0rad)
  Solid = false
  Source = -> Face118
  Symmetric = false
FEATURE [Part::MultiFuse] Fusion096  label="screwRetainers001"
  Shapes = -> [Revolve126,Revolve125,Revolve124,Revolve123,Revolve122,Revolve121]
FEATURE [Part::Feature] Face119
  shape: bbox 10 x 16.5 x 2e-07 mm, 1 faces, 0 solids (baked)
FEATURE [Part::Revolution] Revolve130  label="plugHousing050"
  Angle = 360
  Axis = (0,1,0)
  Base = (0,0,0)
  FaceMakerClass = Part::FaceMakerBullseye
  Placement = pos=(0,0,36.15) rot=(0,0,1;0rad)
  Solid = false
  Source = -> Face119
  Symmetric = false
FEATURE [Part::Feature] Face120
  shape: bbox 10 x 16.5 x 2e-07 mm, 1 faces, 0 solids (baked)
FEATURE [Part::Feature] Face121
  shape: bbox 10 x 16.5 x 2e-07 mm, 1 faces, 0 solids (baked)
FEATURE [Part::Revolution] Revolve127  label="plugHousing047"
  Angle = 360
  Axis = (0,1,0)
  Base = (0,0,0)
  FaceMakerClass = Part::FaceMakerBullseye
  Placement = pos=(0,0,36.15) rot=(0,0,1;0rad)
  Solid = false
  Source = -> Face121
  Symmetric = false
FEATURE [Part::Feature] Face122
  shape: bbox 10 x 16.5 x 2e-07 mm, 1 faces, 0 solids (baked)
FEATURE [Part::Feature] Face123
  shape: bbox 10 x 16.5 x 2e-07 mm, 1 faces, 0 solids (baked)
FEATURE [Part::Revolution] Revolve128  label="plugHousing048"
  Angle = 360
  Axis = (0,1,0)
  Base = (0,0,0)
  FaceMakerClass = Part::FaceMakerBullseye
  Placement = pos=(0,0,36.15) rot=(0,0,1;0rad)
  Solid = false
  Source = -> Face123
  Symmetric = false
FEATURE [Part::MultiFuse] Fusion100  label="plugHousing054"
  Placement = pos=(0,0,0) rot=(0,0,1;1.5708rad)
  Shapes = -> [Revolve130,Revolve128]
FEATURE [Part::Feature] Face124
  shape: bbox 10 x 16.5 x 2e-07 mm, 1 faces, 0 solids (baked)
FEATURE [Part::Feature] Face125
  shape: bbox 10 x 16.5 x 2e-07 mm, 1 faces, 0 solids (baked)
FEATURE [Part::Revolution] Revolve129  label="plugHousing049"
  Angle = 360
  Axis = (0,1,0)
  Base = (0,0,0)
  FaceMakerClass = Part::FaceMakerBullseye
  Placement = pos=(0,0,36.15) rot=(0,0,1;0rad)
  Solid = false
  Source = -> Face125
  Symmetric = false
FEATURE [Part::Feature] Face126
  shape: bbox 10 x 16.5 x 2e-07 mm, 1 faces, 0 solids (baked)
FEATURE [Part::Revolution] Revolve131  label="plugHousing058"
  Angle = 360
  Axis = (0,1,0)
  Base = (0,0,0)
  FaceMakerClass = Part::FaceMakerBullseye
  Placement = pos=(0,0,36.15) rot=(0,0,1;0rad)
  Solid = false
  Source = -> Face120
  Symmetric = false
FEATURE [Part::MultiFuse] Fusion099  label="plugHousing053"
  Placement = pos=(0,0,0) rot=(0,0,1;1.5708rad)
  Shapes = -> [Revolve127,Revolve131]
FEATURE [Part::MultiFuse] Fusion102  label="plugHousing056"
  Placement = pos=(0,19,0) rot=(0,0,1;3.14159rad)
  Shapes = -> [Fusion100,Fusion099]
FEATURE [Part::Revolution] Revolve132  label="plugHousing059"
  Angle = 360
  Axis = (0,1,0)
  Base = (0,0,0)
  FaceMakerClass = Part::FaceMakerBullseye
  Placement = pos=(0,0,36.15) rot=(0,0,1;0rad)
  Solid = false
  Source = -> Face126
  Symmetric = false
FEATURE [Part::Revolution] Revolve133  label="plugHousing060"
  Angle = 360
  Axis = (0,1,0)
  Base = (0,0,0)
  FaceMakerClass = Part::FaceMakerBullseye
  Placement = pos=(0,0,36.15) rot=(0,0,1;0rad)
  Solid = false
  Source = -> Face122
  Symmetric = false
FEATURE [Part::MultiFuse] Fusion097  label="plugHousing051"
  Placement = pos=(0,0,0) rot=(0,0,1;1.5708rad)
  Shapes = -> [Revolve133,Revolve132]
FEATURE [Part::Revolution] Revolve134  label="plugHousing061"
  Angle = 360
  Axis = (0,1,0)
  Base = (0,0,0)
  FaceMakerClass = Part::FaceMakerBullseye
  Placement = pos=(0,0,36.15) rot=(0,0,1;0rad)
  Solid = false
  Source = -> Face124
  Symmetric = false
FEATURE [Part::MultiFuse] Fusion101  label="plugHousing055"
  Placement = pos=(0,0,0) rot=(0,0,1;1.5708rad)
  Shapes = -> [Revolve129,Revolve134]
FEATURE [Part::MultiFuse] Fusion098  label="plugHousing052"
  Placement = pos=(0,19,0) rot=(0,0,1;3.14159rad)
  Shapes = -> [Fusion097,Fusion101]
FEATURE [Part::MultiFuse] Fusion103  label="plugHousing057"
  Placement = pos=(122.621,0,-0.15) rot=(0,0,1;0rad)
  Shapes = -> [Fusion102,Fusion098]
FEATURE [Part::Box] Box028  label="Cube015"
  AttacherType = Attacher::AttachEngine3D
  Height = 28
  Length = 3
  Placement = pos=(110.7,19,22) rot=(0,0,1;0rad)
  Width = 15.7
FEATURE [Part::Cylinder] Cylinder044
  Angle = 360
  AttacherType = Attacher::AttachEngine3D
  Height = 20
  Placement = pos=(0,0,36.15) rot=(0,0,1;0rad)
  Radius = 10.3
FEATURE [Part::Cylinder] Cylinder045
  Angle = 360
  AttacherType = Attacher::AttachEngine3D
  Height = 10
  Placement = pos=(0,0,36.15) rot=(0,0,1;0rad)
  Radius = 4
FEATURE [Part::MultiFuse] Fusion104  label="removeToCreteHoleForPlugHousing040"
  Placement = pos=(70,19,36) rot=(0,1,0;1.5708rad)
  Shapes = -> [Cylinder044,Cylinder045]
FEATURE [Part::Cut] Cut046  label="plugHousingTab003"
  Base = -> Box028
  Tool = -> Fusion104
FEATURE [Part::MultiFuse] Fusion105  label="plugHousing062"
  Shapes = -> [Fusion103,Cut046]
FEATURE [Part::Fillet] Fillet042
  Base = -> Fusion105
  Edges = 1 edges r=2: [Edge25]
FEATURE [Part::Fillet] Fillet043  label="plugHousing063"
  Base = -> Fillet042
  Edges = 1 edges r=2: [Edge8]
  Placement = pos=(7,0,0) rot=(0,0,1;0rad)
FEATURE [Part::Feature] Face127
  shape: bbox 10 x 16.5 x 2e-07 mm, 1 faces, 0 solids (baked)
FEATURE [Part::Feature] Face128
  shape: bbox 10 x 16.5 x 2e-07 mm, 1 faces, 0 solids (baked)
FEATURE [Part::Revolution] Revolve137  label="plugHousing070"
  Angle = 360
  Axis = (0,1,0)
  Base = (0,0,0)
  FaceMakerClass = Part::FaceMakerBullseye
  Placement = pos=(0,0,36.15) rot=(0,0,1;0rad)
  Solid = false
  Source = -> Face127
  Symmetric = false
FEATURE [Part::Revolution] Revolve140  label="plugHousing073"
  Angle = 360
  Axis = (0,1,0)
  Base = (0,0,0)
  FaceMakerClass = Part::FaceMakerBullseye
  Placement = pos=(0,0,36.15) rot=(0,0,1;0rad)
  Solid = false
  Source = -> Face128
  Symmetric = false
FEATURE [Part::Feature] Face129
  shape: bbox 10 x 16.5 x 2e-07 mm, 1 faces, 0 solids (baked)
FEATURE [Part::Revolution] Revolve138  label="plugHousing071"
  Angle = 360
  Axis = (0,1,0)
  Base = (0,0,0)
  FaceMakerClass = Part::FaceMakerBullseye
  Placement = pos=(0,0,36.15) rot=(0,0,1;0rad)
  Solid = false
  Source = -> Face129
  Symmetric = false
FEATURE [Part::Feature] Face130
  shape: bbox 10 x 16.5 x 2e-07 mm, 1 faces, 0 solids (baked)
FEATURE [Part::Revolution] Revolve139  label="plugHousing072"
  Angle = 360
  Axis = (0,1,0)
  Base = (0,0,0)
  FaceMakerClass = Part::FaceMakerBullseye
  Placement = pos=(0,0,36.15) rot=(0,0,1;0rad)
  Solid = false
  Source = -> Face130
  Symmetric = false
FEATURE [Part::Feature] Face131
  shape: bbox 10 x 16.5 x 2e-07 mm, 1 faces, 0 solids (baked)
FEATURE [Part::Revolution] Revolve135  label="plugHousing068"
  Angle = 360
  Axis = (0,1,0)
  Base = (0,0,0)
  FaceMakerClass = Part::FaceMakerBullseye
  Placement = pos=(0,0,36.15) rot=(0,0,1;0rad)
  Solid = false
  Source = -> Face131
  Symmetric = false
FEATURE [Part::MultiFuse] Fusion112  label="plugHousing078"
  Placement = pos=(0,0,0) rot=(0,0,1;1.5708rad)
  Shapes = -> [Revolve135,Revolve139]
FEATURE [Part::Feature] Face132
  shape: bbox 10 x 16.5 x 2e-07 mm, 1 faces, 0 solids (baked)
FEATURE [Part::Revolution] Revolve141  label="plugHousing074"
  Angle = 360
  Axis = (0,1,0)
  Base = (0,0,0)
  FaceMakerClass = Part::FaceMakerBullseye
  Placement = pos=(0,0,36.15) rot=(0,0,1;0rad)
  Solid = false
  Source = -> Face132
  Symmetric = false
FEATURE [Part::MultiFuse] Fusion110  label="plugHousing076"
  Placement = pos=(0,0,0) rot=(0,0,1;1.5708rad)
  Shapes = -> [Revolve141,Revolve140]
FEATURE [Part::Feature] Face133
  shape: bbox 10 x 16.5 x 2e-07 mm, 1 faces, 0 solids (baked)
FEATURE [Part::Revolution] Revolve136  label="plugHousing069"
  Angle = 360
  Axis = (0,1,0)
  Base = (0,0,0)
  FaceMakerClass = Part::FaceMakerBullseye
  Placement = pos=(0,0,36.15) rot=(0,0,1;0rad)
  Solid = false
  Source = -> Face133
  Symmetric = false
FEATURE [Part::MultiFuse] Fusion106  label="plugHousing064"
  Placement = pos=(0,0,0) rot=(0,0,1;1.5708rad)
  Shapes = -> [Revolve138,Revolve136]
FEATURE [Part::MultiFuse] Fusion108  label="plugHousing066"
  Placement = pos=(0,19,0) rot=(0,0,1;3.14159rad)
  Shapes = -> [Fusion106,Fusion112]
FEATURE [Part::Feature] Face134
  shape: bbox 10 x 16.5 x 2e-07 mm, 1 faces, 0 solids (baked)
FEATURE [Part::Revolution] Revolve142  label="plugHousing075"
  Angle = 360
  Axis = (0,1,0)
  Base = (0,0,0)
  FaceMakerClass = Part::FaceMakerBullseye
  Placement = pos=(0,0,36.15) rot=(0,0,1;0rad)
  Solid = false
  Source = -> Face134
  Symmetric = false
FEATURE [Part::MultiFuse] Fusion107  label="plugHousing065"
  Placement = pos=(0,0,0) rot=(0,0,1;1.5708rad)
  Shapes = -> [Revolve137,Revolve142]
FEATURE [Part::MultiFuse] Fusion111  label="plugHousing077"
  Placement = pos=(0,19,0) rot=(0,0,1;3.14159rad)
  Shapes = -> [Fusion110,Fusion107]
FEATURE [Part::MultiFuse] Fusion109  label="plugHousing067"
  Placement = pos=(131.236,0,-0.15) rot=(0,0,1;0rad)
  Shapes = -> [Fusion108,Fusion111]
FEATURE [Part::MultiFuse] Fusion113  label="plugHousing079"
  Shapes = -> [Fillet043,Fusion109]
FEATURE [Part::Feature] Face135
  shape: bbox 3.5 x 17.8 x 2e-07 mm, 1 faces, 0 solids (baked)
FEATURE [Part::Revolution] Revolve143  label="removeToCreateScrewAndThreadedInsertHole049"
  Angle = 360
  Axis = (0,1,0)
  Base = (0,0,0)
  FaceMakerClass = Part::FaceMakerBullseye
  Placement = pos=(12.5,0,10) rot=(0,0,1;0rad)
  Solid = false
  Source = -> Face135
  Symmetric = false
FEATURE [Part::Feature] Face136
  shape: bbox 3.5 x 17.8 x 2e-07 mm, 1 faces, 0 solids (baked)
FEATURE [Part::Revolution] Revolve144  label="removeToCreateScrewAndThreadedInsertHole050"
  Angle = 360
  Axis = (0,1,0)
  Base = (0,0,0)
  FaceMakerClass = Part::FaceMakerBullseye
  Placement = pos=(12.5,0,62) rot=(0,0,1;0rad)
  Solid = false
  Source = -> Face136
  Symmetric = false
FEATURE [Part::Feature] Face137
  shape: bbox 3.5 x 17.8 x 2e-07 mm, 1 faces, 0 solids (baked)
FEATURE [Part::Revolution] Revolve145  label="removeToCreateScrewAndThreadedInsertHole051"
  Angle = 360
  Axis = (0,1,0)
  Base = (0,0,0)
  FaceMakerClass = Part::FaceMakerBullseye
  Placement = pos=(89.5,0,68.5) rot=(0,0,1;0rad)
  Solid = false
  Source = -> Face137
  Symmetric = false
FEATURE [Part::Feature] Face138
  shape: bbox 3.5 x 17.8 x 2e-07 mm, 1 faces, 0 solids (baked)
FEATURE [Part::Revolution] Revolve146  label="removeToCreateScrewAndThreadedInsertHole052"
  Angle = 360
  Axis = (0,1,0)
  Base = (0,0,0)
  FaceMakerClass = Part::FaceMakerBullseye
  Placement = pos=(89.5,0,3.5) rot=(0,0,1;0rad)
  Solid = false
  Source = -> Face138
  Symmetric = false
FEATURE [Part::Feature] Face139
  shape: bbox 3.5 x 17.8 x 2e-07 mm, 1 faces, 0 solids (baked)
FEATURE [Part::Revolution] Revolve147  label="removeToCreateScrewAndThreadedInsertHole053"
  Angle = 360
  Axis = (0,1,0)
  Base = (0,0,0)
  FaceMakerClass = Part::FaceMakerBullseye
  Placement = pos=(109.5,4.7,3.5) rot=(0,0,1;0rad)
  Solid = false
  Source = -> Face139
  Symmetric = false
FEATURE [Part::Feature] Face140
  shape: bbox 3.5 x 17.8 x 2e-07 mm, 1 faces, 0 solids (baked)
FEATURE [Part::Revolution] Revolve148  label="removeToCreateScrewAndThreadedInsertHole054"
  Angle = 360
  Axis = (0,1,0)
  Base = (0,0,0)
  FaceMakerClass = Part::FaceMakerBullseye
  Placement = pos=(109.5,4.7,68.5) rot=(0,0,1;0rad)
  Solid = false
  Source = -> Face140
  Symmetric = false
FEATURE [Part::MultiFuse] Fusion114  label="removeToCreateScrewAndThreadedInsertHole055"
  Shapes = -> [Revolve148,Revolve147,Revolve146,Revolve145,Revolve144,Revolve143]
FEATURE [Part::Cut] Cut047  label="casePillars004"
  Base = -> Cut037
  Tool = -> Fusion114
FEATURE [Part::Feature] Face141
  shape: bbox 3.5 x 17.8 x 2e-07 mm, 1 faces, 0 solids (baked)
FEATURE [Part::Feature] Face142
  shape: bbox 3.5 x 17.8 x 2e-07 mm, 1 faces, 0 solids (baked)
FEATURE [Part::Feature] Face143
  shape: bbox 3.5 x 17.8 x 2e-07 mm, 1 faces, 0 solids (baked)
FEATURE [Part::Revolution] Revolve149  label="removeToCreateScrewAndThreadedInsertHole057"
  Angle = 360
  Axis = (0,1,0)
  Base = (0,0,0)
  FaceMakerClass = Part::FaceMakerBullseye
  Placement = pos=(12.5,0,10) rot=(0,0,1;0rad)
  Solid = false
  Source = -> Face141
  Symmetric = false
FEATURE [Part::Feature] Face144
  shape: bbox 3.5 x 17.8 x 2e-07 mm, 1 faces, 0 solids (baked)
FEATURE [Part::Feature] Face145
  shape: bbox 3.5 x 17.8 x 2e-07 mm, 1 faces, 0 solids (baked)
FEATURE [Part::Feature] Face146
  shape: bbox 3.5 x 17.8 x 2e-07 mm, 1 faces, 0 solids (baked)
FEATURE [Part::Revolution] Revolve150  label="removeToCreateScrewAndThreadedInsertHole058"
  Angle = 360
  Axis = (0,1,0)
  Base = (0,0,0)
  FaceMakerClass = Part::FaceMakerBullseye
  Placement = pos=(12.5,0,62) rot=(0,0,1;0rad)
  Solid = false
  Source = -> Face146
  Symmetric = false
FEATURE [Part::Revolution] Revolve151  label="removeToCreateScrewAndThreadedInsertHole059"
  Angle = 360
  Axis = (0,1,0)
  Base = (0,0,0)
  FaceMakerClass = Part::FaceMakerBullseye
  Placement = pos=(89.5,0,68.5) rot=(0,0,1;0rad)
  Solid = false
  Source = -> Face143
  Symmetric = false
FEATURE [Part::Revolution] Revolve152  label="removeToCreateScrewAndThreadedInsertHole060"
  Angle = 360
  Axis = (0,1,0)
  Base = (0,0,0)
  FaceMakerClass = Part::FaceMakerBullseye
  Placement = pos=(89.5,0,3.5) rot=(0,0,1;0rad)
  Solid = false
  Source = -> Face142
  Symmetric = false
FEATURE [Part::Revolution] Revolve153  label="removeToCreateScrewAndThreadedInsertHole061"
  Angle = 360
  Axis = (0,1,0)
  Base = (0,0,0)
  FaceMakerClass = Part::FaceMakerBullseye
  Placement = pos=(109.5,4.7,3.5) rot=(0,0,1;0rad)
  Solid = false
  Source = -> Face145
  Symmetric = false
FEATURE [Part::Revolution] Revolve154  label="removeToCreateScrewAndThreadedInsertHole062"
  Angle = 360
  Axis = (0,1,0)
  Base = (0,0,0)
  FaceMakerClass = Part::FaceMakerBullseye
  Placement = pos=(109.5,4.7,68.5) rot=(0,0,1;0rad)
  Solid = false
  Source = -> Face144
  Symmetric = false
FEATURE [Part::MultiFuse] Fusion115  label="removeToCreateScrewAndThreadedInsertHole056"
  Shapes = -> [Revolve154,Revolve153,Revolve152,Revolve151,Revolve150,Revolve149]
FEATURE [Part::Feature] Face147
  shape: bbox 9.8 x 26.5 x 2e-07 mm, 1 faces, 0 solids (baked)
FEATURE [Part::Revolution] Revolve155
  Angle = 360
  Axis = (0,1,0)
  Base = (0,0,0)
  FaceMakerClass = Part::FaceMakerBullseye
  Placement = pos=(0,0,0) rot=(0,0,1;1.5708rad)
  Solid = false
  Source = -> Face147
  Symmetric = false
FEATURE [Part::Feature] Face148
  shape: bbox 9.8 x 26.5 x 2e-07 mm, 1 faces, 0 solids (baked)
FEATURE [Part::Revolution] Revolve156
  Angle = 360
  Axis = (0,1,0)
  Base = (0,0,0)
  FaceMakerClass = Part::FaceMakerBullseye
  Placement = pos=(0,0,0) rot=(0,0,1;1.5708rad)
  Solid = false
  Source = -> Face148
  Symmetric = false
FEATURE [Part::MultiFuse] Fusion116
  Placement = pos=(-18,19,36) rot=(0,0,1;0rad)
  Shapes = -> [Revolve156,Revolve155]
FEATURE [Part::Box] Box029  label="Cube016"
  AttacherType = Attacher::AttachEngine3D
  Height = 28
  Length = 3
  Placement = pos=(110.7,19,22) rot=(0,0,1;0rad)
  Width = 15.7
FEATURE [Part::Cylinder] Cylinder046
  Angle = 360
  AttacherType = Attacher::AttachEngine3D
  Height = 10
  Placement = pos=(0,0,36.15) rot=(0,0,1;0rad)
  Radius = 4
FEATURE [Part::Cylinder] Cylinder047
  Angle = 360
  AttacherType = Attacher::AttachEngine3D
  Height = 20
  Placement = pos=(0,0,36.15) rot=(0,0,1;0rad)
  Radius = 10.3
FEATURE [Part::MultiFuse] Fusion117  label="removeToCreteHoleForPlugHousing041"
  Placement = pos=(70,19,36) rot=(0,1,0;1.5708rad)
  Shapes = -> [Cylinder047,Cylinder046]
FEATURE [Part::Cut] Cut049  label="plugHousingTab004"
  Base = -> Box029
  Placement = pos=(-107.4,-14,0) rot=(0,0,1;0rad)
  Tool = -> Fusion117
FEATURE [Part::Box] Box030  label="Cube017"
  AttacherType = Attacher::AttachEngine3D
  Height = 28
  Length = 3
  Placement = pos=(110.7,19,22) rot=(0,0,1;0rad)
  Width = 15.7
FEATURE [Part::Cylinder] Cylinder048
  Angle = 360
  AttacherType = Attacher::AttachEngine3D
  Height = 10
  Placement = pos=(0,0,36.15) rot=(0,0,1;0rad)
  Radius = 4
FEATURE [Part::Cylinder] Cylinder049
  Angle = 360
  AttacherType = Attacher::AttachEngine3D
  Height = 20
  Placement = pos=(0,0,36.15) rot=(0,0,1;0rad)
  Radius = 10.3
FEATURE [Part::MultiFuse] Fusion118  label="removeToCreteHoleForPlugHousing042"
  Placement = pos=(70,19,36) rot=(0,1,0;1.5708rad)
  Shapes = -> [Cylinder049,Cylinder048]
FEATURE [Part::Cut] Cut050  label="plugHousingTab005"
  Base = -> Box030
  Placement = pos=(-107.4,-14,0) rot=(0,0,1;0rad)
  Tool = -> Fusion118
FEATURE [Part::MultiFuse] Fusion119
  Placement = pos=(9.6,23,0) rot=(0,0,1;3.14159rad)
  Shapes = -> [Cut049,Cut050]
FEATURE [Part::Box] Box031  label="Cube018"
  AttacherType = Attacher::AttachEngine3D
  Height = 10
  Length = 3
  Placement = pos=(3.3,4,12) rot=(0,0,1;0rad)
  Width = 10
FEATURE [Part::Fillet] Fillet044
  Base = -> Box031
  Edges = 1 edges r=2: [Edge11]
FEATURE [Part::Box] Box032  label="Cube019"
  AttacherType = Attacher::AttachEngine3D
  Height = 10
  Length = 3
  Placement = pos=(3.3,4,50) rot=(0,0,1;0rad)
  Width = 10
FEATURE [Part::Fillet] Fillet045
  Base = -> Box032
  Edges = 1 edges r=2: [Edge12]
FEATURE [Part::Box] Box033  label="Cube020"
  AttacherType = Attacher::AttachEngine3D
  Height = 28
  Length = 4
  Placement = pos=(5,0,22) rot=(0,0,1;0rad)
  Width = 10
FEATURE [Part::Fillet] Fillet046
  Base = -> Box033
  Edges = 1 edges r=1: [Edge7]
FEATURE [Part::Fillet] Fillet047
  Base = -> Fillet046
  Edges = 1 edges r=2: [Edge5]
FEATURE [Part::Fillet] Fillet048
  Base = -> Fillet047
  Edges = 1 edges r=2: [Edge2]
FEATURE [Part::Cylinder] Cylinder050
  Angle = 360
  AttacherType = Attacher::AttachEngine3D
  Height = 20
  Placement = pos=(0,0,36.15) rot=(0,0,1;0rad)
  Radius = 8.2
FEATURE [Part::Cylinder] Cylinder051
  Angle = 360
  AttacherType = Attacher::AttachEngine3D
  Height = 10
  Placement = pos=(0,0,36.15) rot=(0,0,1;0rad)
  Radius = 4
FEATURE [Part::MultiFuse] Fusion120  label="removeToCreteHoleForPlugHousing043"
  Placement = pos=(-42,19,36) rot=(0,1,0;1.5708rad)
  Shapes = -> [Cylinder050,Cylinder051]
FEATURE [Sketcher::SketchObject] Sketch067  label="topSketch018"
  FullyConstrained = true
  sketch-geometry (4):
    g0: LineSegment StartX=16.8446 StartY=31.512 StartZ=0 EndX=16.3251 EndY=34.4666 EndZ=0
    g1: ArcOfCircle CenterX=19 CenterY=19.2524 CenterZ=0 NormalX=0 NormalY=0 NormalZ=1 AngleXU=0 Radius=15.4476 StartAngle=1.74483 EndAngle=2.72717
    g2: ArcOfCircle CenterX=19 CenterY=19.2524 CenterZ=0 NormalX=0 NormalY=0 NormalZ=1 AngleXU=0 Radius=12.4476 StartAngle=1.74483 EndAngle=2.73189
    g3: LineSegment StartX=4.86004 StartY=25.4725 StartZ=0 EndX=7.58253 EndY=24.2107 EndZ=0
  constraints (7):
    c: Block(g0)
    c: Coincident(g1,g0)
    c: Coincident(g2,g0)
    c: Coincident(g3,g1)
    c: Coincident(g3,g2)
    c: Block(g1)
    c: Block(g2)
FEATURE [Part::Extrusion] Extrude058
  Base = -> Sketch067
  Dir = (0,0,1)
  DirMode = 2
  FaceMakerClass = Part::FaceMakerBullseye
  LengthFwd = 10
  LengthRev = 0
  Placement = pos=(0,0,31) rot=(0,0,1;0rad)
  Solid = true
  Symmetric = false
FEATURE [Part::Cut] Cut051
  Base = -> Extrude058
  Tool = -> Fusion120
FEATURE [Part::Fillet] Fillet049
  Base = -> Cut051
  Edges = 1 edges r=2: [Edge1]
FEATURE [Part::Fillet] Fillet050
  Base = -> Fillet049
  Edges = 1 edges r=2.5: [Edge1]
FEATURE [Part::Fillet] Fillet051
  Base = -> Fillet050
  Edges = 1 edges r=2.5: [Edge2]
FEATURE [Part::MultiFuse] Fusion121  label="wireHolder003"
  Shapes = -> [Fusion116,Fillet051]
FEATURE [Part::MultiFuse] Fusion122
  Shapes = -> [Fillet045,Fusion121]
FEATURE [Part::MultiFuse] Fusion123  label="wireHolder004"
  Shapes = -> [Fusion122,Fillet048]
FEATURE [Part::MultiFuse] Fusion124  label="wireHolder005"
  Shapes = -> [Fillet044,Fusion119,Fusion123]
FEATURE [Sketcher::SketchObject] Sketch068  label="topSketch019"
  FullyConstrained = true
  sketch-geometry (6):
    g0: LineSegment StartX=19 StartY=38 StartZ=0 EndX=117 EndY=38 EndZ=0
    g1: ArcOfCircle CenterX=19 CenterY=19 CenterZ=0 NormalX=0 NormalY=0 NormalZ=1 AngleXU=0 Radius=19 StartAngle=1.5708 EndAngle=3.14159
    g2: LineSegment StartX=117 StartY=38 StartZ=0 EndX=117 EndY=19 EndZ=0
    g3: LineSegment StartX=98 StartY=1.0161e-12 StartZ=0 EndX=5.22862e-06 EndY=1.0161e-12 EndZ=0
    g4: LineSegment StartX=5.22862e-06 StartY=19 StartZ=0 EndX=5.22862e-06 EndY=1.0161e-12 EndZ=0
    g5: ArcOfCircle CenterX=98 CenterY=19 CenterZ=0 NormalX=0 NormalY=0 NormalZ=1 AngleXU=0 Radius=19 StartAngle=4.71239 EndAngle=6.28319
  constraints (16):
    c: Horizontal(g0)
    c: Distance(g0) = 98
    c: Coincident(g1,g0)
    c: Block(g1)
    c: Coincident(g2,g0)
    c: Vertical(g2)
    c: Distance(g2) = 19
    c: Horizontal(g3)
    c: Coincident(g4,g1)
    c: Vertical(g4)
    c: Coincident(g3,g4)
    c: Block(g3)
    c: Coincident(g5,g2)
    c: Coincident(g5,g3)
    c: Block(g0)
    c: Block(g5)
FEATURE [Part::Extrusion] Extrude059  label="sideA002"
  Base = -> Sketch068
  Dir = (0,0,1)
  DirMode = 2
  FaceMakerClass = Part::FaceMakerBullseye
  LengthFwd = 3
  LengthRev = 0
  Placement = pos=(0,0,-2.7) rot=(0,0,1;0rad)
  Solid = true
  Symmetric = false
FEATURE [Sketcher::SketchObject] Sketch069  label="topSketch020"
  FullyConstrained = true
  sketch-geometry (6):
    g0: LineSegment StartX=19 StartY=38 StartZ=0 EndX=117 EndY=38 EndZ=0
    g1: ArcOfCircle CenterX=19 CenterY=19 CenterZ=0 NormalX=0 NormalY=0 NormalZ=1 AngleXU=0 Radius=19 StartAngle=1.5708 EndAngle=3.14159
    g2: LineSegment StartX=117 StartY=38 StartZ=0 EndX=117 EndY=19 EndZ=0
    g3: LineSegment StartX=98 StartY=1.0161e-12 StartZ=0 EndX=5.22862e-06 EndY=1.0161e-12 EndZ=0
    g4: LineSegment StartX=5.22862e-06 StartY=19 StartZ=0 EndX=5.22862e-06 EndY=1.0161e-12 EndZ=0
    g5: ArcOfCircle CenterX=98 CenterY=19 CenterZ=0 NormalX=0 NormalY=0 NormalZ=1 AngleXU=0 Radius=19 StartAngle=4.71239 EndAngle=6.28319
  constraints (16):
    c: Horizontal(g0)
    c: Distance(g0) = 98
    c: Coincident(g1,g0)
    c: Block(g1)
    c: Coincident(g2,g0)
    c: Vertical(g2)
    c: Distance(g2) = 19
    c: Horizontal(g3)
    c: Coincident(g4,g1)
    c: Vertical(g4)
    c: Coincident(g3,g4)
    c: Block(g3)
    c: Coincident(g5,g2)
    c: Coincident(g5,g3)
    c: Block(g0)
    c: Block(g5)
FEATURE [Part::Extrusion] Extrude060  label="sideB002"
  Base = -> Sketch069
  Dir = (0,0,1)
  DirMode = 2
  FaceMakerClass = Part::FaceMakerBullseye
  LengthFwd = 3
  LengthRev = 0
  Placement = pos=(0,0,71.7) rot=(0,0,1;0rad)
  Solid = true
  Symmetric = false
FEATURE [Part::MultiFuse] Fusion127  label="removeFromBottom001"
  Placement = pos=(2,0,0) rot=(0,0,1;0rad)
  Shapes = -> [Extrude059,Extrude060]
FEATURE [Part::Cylinder] Cylinder052
  Angle = 360
  AttacherType = Attacher::AttachEngine3D
  Height = 20
  Placement = pos=(0,0,36.15) rot=(0,0,1;0rad)
  Radius = 14
FEATURE [Part::Cylinder] Cylinder053
  Angle = 360
  AttacherType = Attacher::AttachEngine3D
  Height = 10
  Placement = pos=(0,0,36.15) rot=(0,0,1;0rad)
  Radius = 4
FEATURE [Part::MultiFuse] Fusion128  label="removeToCreteHoleForPlugHousing044"
  Placement = pos=(70,19,36) rot=(0,1,0;1.5708rad)
  Shapes = -> [Cylinder052,Cylinder053]
FEATURE [Part::Cut] Cut052  label="bottom011"
  Base = -> Extrude043
  Tool = -> Fusion128
FEATURE [Part::Cut] Cut054  label="bottom012"
  Base = -> Cut052
  Tool = -> Fusion115
FEATURE [Sketcher::SketchObject] Sketch070
  FullyConstrained = true
  Placement = pos=(117,19,0) rot=(0.57735,0.57735,0.57735;2.0944rad)
  sketch-geometry (48):
    g0: LineSegment StartX=-49.19 StartY=69.25 StartZ=0 EndX=-49.19 EndY=66.25 EndZ=0
    g1: LineSegment StartX=-49.19 StartY=63.5 StartZ=0 EndX=-49.19 EndY=60.5 EndZ=0
    g2: LineSegment StartX=-49.19 StartY=57.75 StartZ=0 EndX=-49.19 EndY=54.75 EndZ=0
    g3: LineSegment StartX=-49.19 StartY=52 StartZ=0 EndX=-49.19 EndY=49 EndZ=0
    g4: LineSegment StartX=-49.19 StartY=46.25 StartZ=0 EndX=-49.19 EndY=43.25 EndZ=0
    g5: LineSegment StartX=-49.19 StartY=40.5 StartZ=0 EndX=-49.19 EndY=37.5 EndZ=0
    g6: LineSegment StartX=-49.19 StartY=34.5 StartZ=0 EndX=-49.19 EndY=31.5 EndZ=0
    g7: LineSegment StartX=-49.19 StartY=28.75 StartZ=0 EndX=-49.19 EndY=25.75 EndZ=0
    g8: LineSegment StartX=-49.19 StartY=23 StartZ=0 EndX=-49.19 EndY=20 EndZ=0
    g9: LineSegment StartX=-49.19 StartY=17.25 StartZ=0 EndX=-49.19 EndY=14.25 EndZ=0
    g10: LineSegment StartX=-49.19 StartY=11.5 StartZ=0 EndX=-49.19 EndY=8.5 EndZ=0
    g11: LineSegment StartX=-49.19 StartY=5.75 StartZ=0 EndX=-49.19 EndY=2.75 EndZ=0
    g12: ArcOfCircle CenterX=-1.5 CenterY=67.75 CenterZ=0 NormalX=0 NormalY=0 NormalZ=1 AngleXU=0 Radius=1.5 StartAngle=4.71239 EndAngle=7.85398
    g13: ArcOfCircle CenterX=-1.5 CenterY=62 CenterZ=0 NormalX=0 NormalY=0 NormalZ=1 AngleXU=0 Radius=1.5 StartAngle=4.71239 EndAngle=7.85398
    g14: ArcOfCircle CenterX=-1.5 CenterY=56.25 CenterZ=0 NormalX=0 NormalY=0 NormalZ=1 AngleXU=0 Radius=1.5 StartAngle=4.71239 EndAngle=7.85398
    g15: ArcOfCircle CenterX=-11.49 CenterY=50.5 CenterZ=0 NormalX=0 NormalY=0 NormalZ=1 AngleXU=0 Radius=1.5 StartAngle=4.71239 EndAngle=7.85398
    g16: ArcOfCircle CenterX=-16.28 CenterY=44.75 CenterZ=0 NormalX=0 NormalY=0 NormalZ=1 AngleXU=0 Radius=1.5 StartAngle=4.71239 EndAngle=7.85398
    g17: ArcOfCircle CenterX=-18.2337 CenterY=39 CenterZ=0 NormalX=0 NormalY=0 NormalZ=1 AngleXU=0 Radius=1.5 StartAngle=4.71485 EndAngle=7.85398
    g18: ArcOfCircle CenterX=-16.2837 CenterY=27.25 CenterZ=0 NormalX=0 NormalY=0 NormalZ=1 AngleXU=0 Radius=1.5 StartAngle=4.71485 EndAngle=7.85398
    g19: ArcOfCircle CenterX=-18.2337 CenterY=33 CenterZ=0 NormalX=0 NormalY=0 NormalZ=1 AngleXU=0 Radius=1.5 StartAngle=4.71485 EndAngle=7.85398
    g20: ArcOfCircle CenterX=-11.49 CenterY=21.5 CenterZ=0 NormalX=0 NormalY=0 NormalZ=1 AngleXU=0 Radius=1.5 StartAngle=4.71239 EndAngle=7.85398
    g21: ArcOfCircle CenterX=-1.5 CenterY=4.25 CenterZ=0 NormalX=0 NormalY=0 NormalZ=1 AngleXU=0 Radius=1.5 StartAngle=4.71239 EndAngle=7.85398
    g22: ArcOfCircle CenterX=-1.5 CenterY=10 CenterZ=0 NormalX=0 NormalY=0 NormalZ=1 AngleXU=0 Radius=1.5 StartAngle=4.71239 EndAngle=7.85398
    g23: ArcOfCircle CenterX=-1.5 CenterY=15.75 CenterZ=0 NormalX=0 NormalY=0 NormalZ=1 AngleXU=0 Radius=1.5 StartAngle=4.71239 EndAngle=7.85398
    g24: LineSegment StartX=-49.19 StartY=69.25 StartZ=0 EndX=-1.5 EndY=69.25 EndZ=0
    g25: LineSegment StartX=-49.19 StartY=66.25 StartZ=0 EndX=-1.5 EndY=66.25 EndZ=0
    g26: LineSegment StartX=-49.19 StartY=63.5 StartZ=0 EndX=-1.5 EndY=63.5 EndZ=0
    g27: LineSegment StartX=-49.19 StartY=60.5 StartZ=0 EndX=-1.5 EndY=60.5 EndZ=0
    g28: LineSegment StartX=-49.19 StartY=57.75 StartZ=0 EndX=-1.5 EndY=57.75 EndZ=0
    g29: LineSegment StartX=-49.19 StartY=54.75 StartZ=0 EndX=-1.5 EndY=54.75 EndZ=0
    g30: LineSegment StartX=-49.19 StartY=52 StartZ=0 EndX=-11.49 EndY=52 EndZ=0
    g31: LineSegment StartX=-49.19 StartY=49 StartZ=0 EndX=-11.49 EndY=49 EndZ=0
    g32: LineSegment StartX=-49.19 StartY=46.25 StartZ=0 EndX=-16.28 EndY=46.25 EndZ=0
    g33: LineSegment StartX=-49.19 StartY=43.25 StartZ=0 EndX=-16.28 EndY=43.25 EndZ=0
    g34: LineSegment StartX=-49.19 StartY=40.5 StartZ=0 EndX=-18.2337 EndY=40.5 EndZ=0
    g35: LineSegment StartX=-49.19 StartY=37.5 StartZ=0 EndX=-18.23 EndY=37.5 EndZ=0
    g36: LineSegment StartX=-49.19 StartY=34.5 StartZ=0 EndX=-18.2337 EndY=34.5 EndZ=0
    g37: LineSegment StartX=-49.19 StartY=31.5 StartZ=0 EndX=-18.23 EndY=31.5 EndZ=0
    g38: LineSegment StartX=-49.19 StartY=28.75 StartZ=0 EndX=-16.2837 EndY=28.75 EndZ=0
    g39: LineSegment StartX=-49.19 StartY=25.75 StartZ=0 EndX=-16.28 EndY=25.75 EndZ=0
    g40: LineSegment StartX=-49.19 StartY=23 StartZ=0 EndX=-11.49 EndY=23 EndZ=0
    g41: LineSegment StartX=-49.19 StartY=20 StartZ=0 EndX=-11.49 EndY=20 EndZ=0
    g42: LineSegment StartX=-49.19 StartY=17.25 StartZ=0 EndX=-1.5 EndY=17.25 EndZ=0
    g43: LineSegment StartX=-49.19 StartY=14.25 StartZ=0 EndX=-1.5 EndY=14.25 EndZ=0
    g44: LineSegment StartX=-49.19 StartY=11.5 StartZ=0 EndX=-1.5 EndY=11.5 EndZ=0
    g45: LineSegment StartX=-49.19 StartY=8.5 StartZ=0 EndX=-1.5 EndY=8.5 EndZ=0
    g46: LineSegment StartX=-49.19 StartY=5.75 StartZ=0 EndX=-1.5 EndY=5.75 EndZ=0
    g47: LineSegment StartX=-49.19 StartY=2.75 StartZ=0 EndX=-1.5 EndY=2.75 EndZ=0
  constraints (120):
    c: Vertical(g0)
    c: Distance(g0) = 3
    c: Block(g0)
    c: Vertical(g1)
    c: Distance(g1) = 3
    c: Vertical(g2)
    c: Equal(g0,g2) = 3
    c: Block(g2)
    c: Vertical(g3)
    c: Equal(g1,g3) = 3
    c: Vertical(g4)
    c: Equal(g0,g4) = 3
    c: Block(g4)
    c: Vertical(g5)
    c: Equal(g1,g5) = 3
    c: Vertical(g6)
    c: Equal(g0,g6) = 3
    c: Block(g6)
    c: Vertical(g7)
    c: Equal(g1,g7) = 3
    c: Vertical(g8)
    c: Equal(g0,g8) = 3
    c: Block(g8)
    c: Vertical(g9)
    c: Equal(g1,g9) = 3
    c: Vertical(g10)
    c: Equal(g0,g10) = 3
    c: Block(g10)
    c: Vertical(g11)
    c: Equal(g1,g11) = 3
    c: Block(g12)
    c: Block(g13)
    c: Block(g14)
    c: Block(g15)
    c: Block(g16)
    c: Block(g17)
    c: Block(g18)
    c: Block(g19)
    c: Block(g20)
    c: Block(g21)
    c: Block(g22)
    c: Block(g23)
    c: Block(g11)
    c: Block(g9)
    c: Block(g7)
    c: Block(g5)
    c: Block(g3)
    c: Block(g1)
    c: Coincident(g24,g0)
    c: Coincident(g24,g12)
    c: Horizontal(g24)
    c: Coincident(g25,g0)
    c: Coincident(g25,g12)
    c: Horizontal(g25)
    c: Coincident(g26,g1)
    c: Coincident(g26,g13)
    c: Horizontal(g26)
    c: Coincident(g27,g1)
    c: Coincident(g27,g13)
    c: Horizontal(g27)
    c: Coincident(g28,g2)
    c: Coincident(g28,g14)
    c: Horizontal(g28)
    c: Coincident(g29,g2)
    c: Coincident(g29,g14)
    c: Horizontal(g29)
    c: Coincident(g30,g3)
    c: Coincident(g30,g15)
    c: Horizontal(g30)
    c: Coincident(g31,g3)
    c: Coincident(g31,g15)
    c: Horizontal(g31)
    c: Coincident(g32,g4)
    c: Coincident(g32,g16)
    c: Horizontal(g32)
    c: Coincident(g33,g4)
    c: Coincident(g33,g16)
    c: Horizontal(g33)
    c: Coincident(g34,g5)
    c: Coincident(g34,g17)
    c: Horizontal(g34)
    c: Coincident(g35,g5)
    c: Coincident(g35,g17)
    c: Horizontal(g35)
    c: Coincident(g36,g6)
    c: Coincident(g36,g19)
    c: Horizontal(g36)
    c: Coincident(g37,g6)
    c: Coincident(g37,g19)
    c: Horizontal(g37)
    c: Coincident(g38,g7)
    c: Coincident(g38,g18)
    c: Horizontal(g38)
    c: Coincident(g39,g7)
    c: Coincident(g39,g18)
    c: Horizontal(g39)
    c: Coincident(g40,g8)
    c: Coincident(g40,g20)
    c: Horizontal(g40)
    c: Coincident(g41,g8)
    c: Coincident(g41,g20)
    c: Horizontal(g41)
    c: Coincident(g42,g9)
    c: Coincident(g42,g23)
    c: Horizontal(g42)
    c: Coincident(g43,g9)
    c: Coincident(g43,g23)
    c: Horizontal(g43)
    c: Coincident(g44,g10)
    c: Coincident(g44,g22)
    c: Horizontal(g44)
    c: Coincident(g45,g10)
    c: Coincident(g45,g22)
    c: Horizontal(g45)
    c: Coincident(g46,g11)
    c: Coincident(g46,g21)
    c: Horizontal(g46)
    c: Coincident(g47,g11)
    c: Coincident(g47,g21)
    c: Horizontal(g47)
FEATURE [Part::Extrusion] Extrude061
  Base = -> Sketch070
  Dir = (1,0,0)
  DirMode = 2
  FaceMakerClass = Part::FaceMakerBullseye
  LengthFwd = 23
  LengthRev = 0
  Placement = pos=(-19,0,0) rot=(0,0,1;0rad)
  Solid = true
  Symmetric = false
FEATURE [Part::Fillet] Fillet052  label="removeToCreateVentalationHoles002"
  Base = -> Extrude061
  Edges = <same value as first occurrence — deduplicated (x6 in doc)>
  Placement = pos=(7,0.02,0) rot=(0,0,1;0rad)
FEATURE [Part::MultiFuse] Fusion130  label="bottom013"
  Shapes = -> [Cut054,Cut034]
FEATURE [Part::Cut] Cut055
  Base = -> Fusion130
  Tool = -> Fillet052
FEATURE [Part::Cylinder] Cylinder054
  Angle = 360
  AttacherType = Attacher::AttachEngine3D
  Height = 20
  Placement = pos=(0,0,36.15) rot=(0,0,1;0rad)
  Radius = 4
FEATURE [Sketcher::SketchObject] Sketch071  label="bottomSketch002"
  FullyConstrained = true
  sketch-geometry (32):
    g0: LineSegment StartX=3.3 StartY=-6.03275e-07 StartZ=0 EndX=98 EndY=-6.03275e-07 EndZ=0
    g1: ArcOfCircle CenterX=98 CenterY=19 CenterZ=0 NormalX=0 NormalY=0 NormalZ=1 AngleXU=0 Radius=19 StartAngle=4.71239 EndAngle=5.71103
    g2: LineSegment StartX=6.3 StartY=8 StartZ=0 EndX=3.3 EndY=8 EndZ=0
    g3: LineSegment StartX=3.3 StartY=8 StartZ=0 EndX=3.3 EndY=-6.03275e-07 EndZ=0
    g4: ArcOfCircle CenterX=8.3 CenterY=5 CenterZ=0 NormalX=0 NormalY=0 NormalZ=1 AngleXU=0 Radius=2 StartAngle=3.14159 EndAngle=4.71239
    g5: LineSegment StartX=6.3 StartY=8 StartZ=0 EndX=6.3 EndY=5 EndZ=0
    g6: ArcOfCircle CenterX=98 CenterY=19 CenterZ=0 NormalX=0 NormalY=0 NormalZ=1 AngleXU=0 Radius=12.7 StartAngle=4.71239 EndAngle=6.28319
    g7: LineSegment StartX=94.7 StartY=3 StartZ=0 EndX=8.3 EndY=3 EndZ=0
    g8-g12: Circle x5 (B-spline internal-alignment scaffolding for g13; pole/knot coordinates omitted)
    g13: BSplineCurve PolesCount=5 KnotsCount=3 Degree=3 IsPeriodic=0
    g14: GeomPoint X=98 Y=6.3 Z=0
    g15: GeomPoint X=96.3938 Y=4.71946 Z=0
    g16: GeomPoint X=94.7 Y=3 Z=0
    g17-g23: Circle x7 (B-spline internal-alignment scaffolding for g24; pole/knot coordinates omitted)
    g24: BSplineCurve PolesCount=7 KnotsCount=5 Degree=3 IsPeriodic=0
    g25-g29: GeomPoint x5 (B-spline internal-alignment scaffolding for g24; pole/knot coordinates omitted)
    g30: ArcOfCircle CenterX=98 CenterY=19 CenterZ=0 NormalX=0 NormalY=0 NormalZ=1 AngleXU=0 Radius=15.7 StartAngle=5.81226 EndAngle=6.28319
    g31: LineSegment StartX=110.7 StartY=19 StartZ=0 EndX=113.7 EndY=19 EndZ=0
  constraints (41):
    c: Horizontal(g0)
    c: Coincident(g1,g0)
    c: Block(g1)
    c: Horizontal(g2)
    c: Distance(g2) = 3
    c: Coincident(g3,g2)
    c: Vertical(g3)
    c: Coincident(g3,g0)
    c: Block(g4)
    c: Block(g2)
    c: Coincident(g5,g2)
    c: Coincident(g5,g4)
    c: Vertical(g5)
    c: Coincident(g6,g1)
    c: Block(g6)
    c: Coincident(g7,g4)
    c: Horizontal(g7)
    c: Block(g0)
    c: Block(g7)
    c: Block(g3)
    c: Coincident(g13,g6)
    c: Weight(g8) = 1
    c: Equal(g8, g9-g12) x4
    c: Coincident(g13,g7)
    c: InternalAlignment(g8-g12 -> g13) x5
    c: InternalAlignment(g14,g13)
    c: InternalAlignment(g15,g13)
    c: InternalAlignment(g16,g13)
    c: Block(g13)
    c: Weight(g17) = 1
    c: Equal(g17, g18-g23) x6
    c: Coincident(g24,g1)
    c: InternalAlignment(g17-g23 -> g24) x7
    c: InternalAlignment(g25-g29 -> g24) x5
    c: Block(g24)
    c: Coincident(g30,g24)
    c: Coincident(g31,g6)
    c: Coincident(g31,g30)
    c: Horizontal(g31)
    c: Block(g31)
    c: Block(g30)
FEATURE [Part::Extrusion] Extrude062  label="bottom014"
  Base = -> Sketch071
  Dir = (0,0,1)
  DirMode = 2
  FaceMakerClass = Part::FaceMakerBullseye
  LengthFwd = 71.4
  LengthRev = 0
  Placement = pos=(0,0,0.3) rot=(0,0,1;0rad)
  Solid = true
  Symmetric = false
FEATURE [Part::Fillet] Fillet054
  Base = -> Extrude062
  Edges = 1 edges r=2.4: [Edge17]
FEATURE [Part::Fillet] Fillet055  label="bottom015"
  Base = -> Fillet054
  Edges = 1 edges r=2.4: [Edge36]
FEATURE [Part::Cylinder] Cylinder055
  Angle = 360
  AttacherType = Attacher::AttachEngine3D
  Height = 10
  Placement = pos=(0,0,36.15) rot=(0,0,1;0rad)
  Radius = 4
FEATURE [Part::MultiFuse] Fusion131  label="removeToCreateHoleForPlugHousing002"
  Placement = pos=(70,19,36.15) rot=(0,1,0;1.5708rad)
  Shapes = -> [Cylinder054,Cylinder055]
FEATURE [Part::Cut] Cut056  label="Bottom001"
  Base = -> Fillet055
  Placement = pos=(9,0,0) rot=(0,0,1;0rad)
  Tool = -> Fusion131
FEATURE [Part::Cut] Cut057
  Base = -> Cut055
  Tool = -> Cut056
FEATURE [Sketcher::SketchObject] Sketch072  label="topSketch021"
  FullyConstrained = true
  sketch-geometry (4):
    g0: ArcOfCircle CenterX=105 CenterY=19 CenterZ=0 NormalX=0 NormalY=0 NormalZ=1 AngleXU=0 Radius=20.6155 StartAngle=5.54125 EndAngle=6.28319
    g1: ArcOfCircle CenterX=105 CenterY=19 CenterZ=0 NormalX=0 NormalY=0 NormalZ=1 AngleXU=0 Radius=13 StartAngle=5.54125 EndAngle=6.28319
    g2: LineSegment StartX=118 StartY=19 StartZ=0 EndX=125.616 EndY=19 EndZ=0
    g3: LineSegment StartX=114.583 StartY=10.2157 StartZ=0 EndX=120.197 EndY=5.06982 EndZ=0
  constraints (7):
    c: Block(g0)
    c: Block(g1)
    c: Coincident(g2,g1)
    c: Coincident(g2,g0)
    c: Horizontal(g2)
    c: Coincident(g3,g1)
    c: Coincident(g3,g0)
FEATURE [Part::Extrusion] Extrude063  label="bottomPlugHousingBit003"
  Base = -> Sketch072
  Dir = (0,0,1)
  DirMode = 2
  FaceMakerClass = Part::FaceMakerBullseye
  LengthFwd = 72
  LengthRev = 0
  Solid = true
  Symmetric = false
FEATURE [Part::Cylinder] Cylinder056
  Angle = 360
  AttacherType = Attacher::AttachEngine3D
  Height = 20
  Placement = pos=(0,0,36.15) rot=(0,0,1;0rad)
  Radius = 14.3
FEATURE [Part::Cylinder] Cylinder057
  Angle = 360
  AttacherType = Attacher::AttachEngine3D
  Height = 10
  Placement = pos=(0,0,36.15) rot=(0,0,1;0rad)
  Radius = 4
FEATURE [Part::Box] Box034  label="removeToCreteHoleForPlugHousing047"
  AttacherType = Attacher::AttachEngine3D
  Height = 28.6
  Length = 20
  Placement = pos=(106.15,0,21.7) rot=(0,0,1;0rad)
  Width = 19
FEATURE [Part::Cylinder] Cylinder058
  Angle = 360
  AttacherType = Attacher::AttachEngine3D
  Height = 20
  Placement = pos=(0,0,36.15) rot=(0,0,1;0rad)
  Radius = 14.3
FEATURE [Part::Cylinder] Cylinder059
  Angle = 360
  AttacherType = Attacher::AttachEngine3D
  Height = 10
  Placement = pos=(0,0,36.15) rot=(0,0,1;0rad)
  Radius = 4
FEATURE [Part::MultiFuse] Fusion134  label="removeToCreteHoleForPlugHousing046"
  Placement = pos=(70,19,36) rot=(0,1,0;1.5708rad)
  Shapes = -> [Cylinder058,Cylinder059]
FEATURE [Part::Cylinder] Cylinder060
  Angle = 360
  AttacherType = Attacher::AttachEngine3D
  Height = 20
  Placement = pos=(0,0,36.15) rot=(0,0,1;0rad)
  Radius = 14
FEATURE [Part::Cylinder] Cylinder061
  Angle = 360
  AttacherType = Attacher::AttachEngine3D
  Height = 10
  Placement = pos=(0,0,36.15) rot=(0,0,1;0rad)
  Radius = 4
FEATURE [Part::MultiFuse] Fusion135  label="removeToCreteHoleForPlugHousing048"
  Placement = pos=(70,19,36) rot=(0,1,0;1.5708rad)
  Shapes = -> [Cylinder060,Cylinder061]
FEATURE [Part::Box] Box035  label="removeToCreteHoleForPlugHousing049"
  AttacherType = Attacher::AttachEngine3D
  Height = 28.6
  Length = 20
  Placement = pos=(106.15,0,21.7) rot=(0,0,1;0rad)
  Width = 19
FEATURE [Part::MultiFuse] Fusion133  label="removeToCreteHoleForPlugHousing045"
  Placement = pos=(0,0,-28.3) rot=(0,0,1;0rad)
  Shapes = -> [Box035,Fusion134]
FEATURE [Part::MultiFuse] Fusion138  label="removeToCreteHoleForPlugHousing051"
  Placement = pos=(70,19,36) rot=(0,1,0;1.5708rad)
  Shapes = -> [Cylinder056,Cylinder057]
FEATURE [Part::MultiFuse] Fusion137  label="removeToCreteHoleForPlugHousing050"
  Placement = pos=(0,0,28.3) rot=(0,0,1;0rad)
  Shapes = -> [Box034,Fusion138]
FEATURE [Part::MultiFuse] Fusion132  label="removeToCreatePlugHousingBottomBit002"
  Shapes = -> [Fusion133,Fusion137]
FEATURE [Part::MultiFuse] Fusion136  label="removeToCreatePlugHousingBottomBit003"
  Shapes = -> [Fusion135,Fusion132]
FEATURE [Part::Cut] Cut058  label="bottomPlugHousingBit002"
  Base = -> Extrude063
  Placement = pos=(-0.09,0,0) rot=(0,0,1;0rad)
  Tool = -> Fusion136
FEATURE [Sketcher::SketchObject] Sketch073  label="bottomSketch003"
  FullyConstrained = true
  sketch-geometry (45):
    g0: LineSegment StartX=6.29999 StartY=8 StartZ=0 EndX=3.29999 EndY=8 EndZ=0
    g1: LineSegment StartX=3.29999 StartY=8 StartZ=0 EndX=3.29999 EndY=-6.03275e-07 EndZ=0
    g2: ArcOfCircle CenterX=8.29999 CenterY=5 CenterZ=0 NormalX=0 NormalY=0 NormalZ=1 AngleXU=0 Radius=2 StartAngle=3.14159 EndAngle=4.71239
    g3: LineSegment StartX=6.29999 StartY=8 StartZ=0 EndX=6.29999 EndY=5 EndZ=0
    g4: ArcOfCircle CenterX=105 CenterY=19 CenterZ=0 NormalX=0 NormalY=0 NormalZ=1 AngleXU=0 Radius=12.7 StartAngle=4.71239 EndAngle=5.94289
    g5-g11: Circle x7 (B-spline internal-alignment scaffolding for g12; pole/knot coordinates omitted)
    g12: BSplineCurve PolesCount=7 KnotsCount=5 Degree=3 IsPeriodic=0
    g13-g17: GeomPoint x5 (B-spline internal-alignment scaffolding for g12; pole/knot coordinates omitted)
    g18: ArcOfCircle CenterX=105 CenterY=19 CenterZ=0 NormalX=0 NormalY=0 NormalZ=1 AngleXU=0 Radius=15.7 StartAngle=5.81226 EndAngle=6.28319
    g19: BSplineCurve PolesCount=5 KnotsCount=3 Degree=3 IsPeriodic=0
    g20: LineSegment StartX=8.29999 StartY=3 StartZ=0 EndX=101.7 EndY=3 EndZ=0
    g21: LineSegment StartX=3.29999 StartY=-6.03275e-07 StartZ=0 EndX=105 EndY=-6.03275e-07 EndZ=0
    g22: LineSegment StartX=120.974 StartY=8.71251 StartZ=0 EndX=122.332 EndY=7.83778 EndZ=0
    g23: LineSegment StartX=105 StartY=-6.03274e-07 StartZ=0 EndX=113 EndY=-6.03274e-07 EndZ=0
    g24: ArcOfCircle CenterX=105 CenterY=19 CenterZ=0 NormalX=0 NormalY=0 NormalZ=1 AngleXU=0 Radius=20.6155 StartAngle=5.11091 EndAngle=5.71103
    g25: ArcOfCircle CenterX=117.7 CenterY=19 CenterZ=0 NormalX=0 NormalY=0 NormalZ=1 AngleXU=0 Radius=3 StartAngle=1.2e-15 EndAngle=2.10468
    g26: Circle CenterX=116.345 CenterY=16.3232 CenterZ=0 NormalX=0 NormalY=0 NormalZ=1 AngleXU=0 Radius=1
    g27: Circle CenterX=117.24 CenterY=15.7584 CenterZ=0 NormalX=0 NormalY=0 NormalZ=1 AngleXU=0 Radius=1
    g28: Circle CenterX=116.972 CenterY=14.7612 CenterZ=0 NormalX=0 NormalY=0 NormalZ=1 AngleXU=0 Radius=1
    g29: BSplineCurve PolesCount=3 KnotsCount=2 Degree=2 IsPeriodic=0
    g30: GeomPoint X=116.345 Y=16.3232 Z=0
    g31: GeomPoint X=116.972 Y=14.7612 Z=0
    g32: Circle CenterX=115.828 CenterY=17.157 CenterZ=0 NormalX=0 NormalY=0 NormalZ=1 AngleXU=0 Radius=1
    g33: Circle CenterX=115.841 CenterY=16.639 CenterZ=0 NormalX=0 NormalY=0 NormalZ=1 AngleXU=0 Radius=1
    g34: Circle CenterX=116.345 CenterY=16.3232 CenterZ=0 NormalX=0 NormalY=0 NormalZ=1 AngleXU=0 Radius=1
    g35: BSplineCurve PolesCount=3 KnotsCount=2 Degree=2 IsPeriodic=0
    g36: GeomPoint X=115.828 Y=17.157 Z=0
    g37: GeomPoint X=116.345 Y=16.3232 Z=0
    g38: LineSegment StartX=115.828 StartY=17.157 StartZ=0 EndX=115.828 EndY=20.8307 EndZ=0
    g39: Circle CenterX=115.828 CenterY=20.8307 CenterZ=0 NormalX=0 NormalY=0 NormalZ=1 AngleXU=0 Radius=1
    g40: Circle CenterX=115.831 CenterY=21.3396 CenterZ=0 NormalX=0 NormalY=0 NormalZ=1 AngleXU=0 Radius=1
    g41: Circle CenterX=116.173 CenterY=21.5825 CenterZ=0 NormalX=0 NormalY=0 NormalZ=1 AngleXU=0 Radius=1
    g42: BSplineCurve PolesCount=3 KnotsCount=2 Degree=2 IsPeriodic=0
    g43: GeomPoint X=115.828 Y=20.8307 Z=0
    g44: GeomPoint X=116.173 Y=21.5825 Z=0
  constraints (70):
    c: Horizontal(g0)
    c: Distance(g0) = 3
    c: Coincident(g1,g0)
    c: Vertical(g1)
    c: Block(g2)
    c: Block(g0)
    c: Coincident(g3,g0)
    c: Coincident(g3,g2)
    c: Vertical(g3)
    c: Block(g1)
    c: Block(g4)
    c: Coincident(g19,g4)
    c: Block(g19)
    c: Equal(g5, g6-g11) x6
    c: InternalAlignment(g5-g11 -> g12) x7
    c: InternalAlignment(g13-g17 -> g12) x5
    c: Block(g12)
    c: Coincident(g18,g12)
    c: Block(g18)
    c: Coincident(g20,g2)
    c: Coincident(g20,g19)
    c: Horizontal(g20)
    c: Distance(g20) = 93.4
    c: Coincident(g21,g1)
    c: Horizontal(g21)
    c: Distance(g21) = 101.7
    c: Horizontal(g23)
    c: Distance(g23) = 8
    c: Coincident(g24,g23)
    c: Block(g23)
    c: Coincident(g22,g24)
    c: Block(g24)
    c: Block(g22)
    c: Distance(g22) = 1.61553
    c: Coincident(g25,g18)
    c: Block(g25)
    c: Weight(g26) = 1
    c: Equal(g26,g27)
    c: Equal(g26,g28)
    c: Coincident(g29,g4)
    c: InternalAlignment(g26,g29)
    c: InternalAlignment(g27,g29)
    c: InternalAlignment(g28,g29)
    c: InternalAlignment(g30,g29)
    c: InternalAlignment(g31,g29)
    c: Block(g29)
    c: Weight(g32) = 1
    c: Equal(g32,g33)
    c: Equal(g32,g34)
    c: Coincident(g35,g29)
    c: InternalAlignment(g32,g35)
    c: InternalAlignment(g33,g35)
    c: InternalAlignment(g34,g35)
    c: InternalAlignment(g36,g35)
    c: InternalAlignment(g37,g35)
    c: Block(g35)
    c: Coincident(g38,g35)
    c: Vertical(g38)
    c: Block(g38)
    c: Coincident(g42,g38)
    c: Weight(g39) = 1
    c: Equal(g39,g40)
    c: Equal(g39,g41)
    c: Coincident(g42,g25)
    c: InternalAlignment(g39,g42)
    c: InternalAlignment(g40,g42)
    c: InternalAlignment(g41,g42)
    c: InternalAlignment(g43,g42)
    c: InternalAlignment(g44,g42)
    c: Block(g42)
FEATURE [Part::Extrusion] Extrude064  label="bottom016"
  Base = -> Sketch073
  Dir = (0,0,1)
  DirMode = 2
  FaceMakerClass = Part::FaceMakerBullseye
  LengthFwd = 71.4
  LengthRev = 0
  Placement = pos=(0,0,0.3) rot=(0,0,1;0rad)
  Solid = true
  Symmetric = false
FEATURE [Part::Revolution] Revolve157  label="removeToCreateScrewAndThreadedInsertHole063"
  Angle = 360
  Axis = (0,1,0)
  Base = (0,0,0)
  FaceMakerClass = Part::FaceMakerBullseye
  Placement = pos=(12.5,0,10) rot=(0,0,1;0rad)
  Solid = false
  Source = -> Face141
  Symmetric = false
FEATURE [Sketcher::SketchObject] Sketch074
  FullyConstrained = true
  Placement = pos=(117,19,0) rot=(0.57735,0.57735,0.57735;2.0944rad)
  sketch-geometry (48):
    g0: LineSegment StartX=-49.19 StartY=69.25 StartZ=0 EndX=-49.19 EndY=66.25 EndZ=0
    g1: LineSegment StartX=-49.19 StartY=63.5 StartZ=0 EndX=-49.19 EndY=60.5 EndZ=0
    g2: LineSegment StartX=-49.19 StartY=57.75 StartZ=0 EndX=-49.19 EndY=54.75 EndZ=0
    g3: LineSegment StartX=-49.19 StartY=52 StartZ=0 EndX=-49.19 EndY=49 EndZ=0
    g4: LineSegment StartX=-49.19 StartY=46.25 StartZ=0 EndX=-49.19 EndY=43.25 EndZ=0
    g5: LineSegment StartX=-49.19 StartY=40.5 StartZ=0 EndX=-49.19 EndY=37.5 EndZ=0
    g6: LineSegment StartX=-49.19 StartY=34.5 StartZ=0 EndX=-49.19 EndY=31.5 EndZ=0
    g7: LineSegment StartX=-49.19 StartY=28.75 StartZ=0 EndX=-49.19 EndY=25.75 EndZ=0
    g8: LineSegment StartX=-49.19 StartY=23 StartZ=0 EndX=-49.19 EndY=20 EndZ=0
    g9: LineSegment StartX=-49.19 StartY=17.25 StartZ=0 EndX=-49.19 EndY=14.25 EndZ=0
    g10: LineSegment StartX=-49.19 StartY=11.5 StartZ=0 EndX=-49.19 EndY=8.5 EndZ=0
    g11: LineSegment StartX=-49.19 StartY=5.75 StartZ=0 EndX=-49.19 EndY=2.75 EndZ=0
    g12: ArcOfCircle CenterX=-1.5 CenterY=67.75 CenterZ=0 NormalX=0 NormalY=0 NormalZ=1 AngleXU=0 Radius=1.5 StartAngle=4.71239 EndAngle=7.85398
    g13: ArcOfCircle CenterX=-1.5 CenterY=62 CenterZ=0 NormalX=0 NormalY=0 NormalZ=1 AngleXU=0 Radius=1.5 StartAngle=4.71239 EndAngle=7.85398
    g14: ArcOfCircle CenterX=-1.5 CenterY=56.25 CenterZ=0 NormalX=0 NormalY=0 NormalZ=1 AngleXU=0 Radius=1.5 StartAngle=4.71239 EndAngle=7.85398
    g15: ArcOfCircle CenterX=-11.49 CenterY=50.5 CenterZ=0 NormalX=0 NormalY=0 NormalZ=1 AngleXU=0 Radius=1.5 StartAngle=4.71239 EndAngle=7.85398
    g16: ArcOfCircle CenterX=-16.28 CenterY=44.75 CenterZ=0 NormalX=0 NormalY=0 NormalZ=1 AngleXU=0 Radius=1.5 StartAngle=4.71239 EndAngle=7.85398
    g17: ArcOfCircle CenterX=-18.2337 CenterY=39 CenterZ=0 NormalX=0 NormalY=0 NormalZ=1 AngleXU=0 Radius=1.5 StartAngle=4.71485 EndAngle=7.85398
    g18: ArcOfCircle CenterX=-16.2837 CenterY=27.25 CenterZ=0 NormalX=0 NormalY=0 NormalZ=1 AngleXU=0 Radius=1.5 StartAngle=4.71485 EndAngle=7.85398
    g19: ArcOfCircle CenterX=-18.2337 CenterY=33 CenterZ=0 NormalX=0 NormalY=0 NormalZ=1 AngleXU=0 Radius=1.5 StartAngle=4.71485 EndAngle=7.85398
    g20: ArcOfCircle CenterX=-11.49 CenterY=21.5 CenterZ=0 NormalX=0 NormalY=0 NormalZ=1 AngleXU=0 Radius=1.5 StartAngle=4.71239 EndAngle=7.85398
    g21: ArcOfCircle CenterX=-1.5 CenterY=4.25 CenterZ=0 NormalX=0 NormalY=0 NormalZ=1 AngleXU=0 Radius=1.5 StartAngle=4.71239 EndAngle=7.85398
    g22: ArcOfCircle CenterX=-1.5 CenterY=10 CenterZ=0 NormalX=0 NormalY=0 NormalZ=1 AngleXU=0 Radius=1.5 StartAngle=4.71239 EndAngle=7.85398
    g23: ArcOfCircle CenterX=-1.5 CenterY=15.75 CenterZ=0 NormalX=0 NormalY=0 NormalZ=1 AngleXU=0 Radius=1.5 StartAngle=4.71239 EndAngle=7.85398
    g24: LineSegment StartX=-49.19 StartY=69.25 StartZ=0 EndX=-1.5 EndY=69.25 EndZ=0
    g25: LineSegment StartX=-49.19 StartY=66.25 StartZ=0 EndX=-1.5 EndY=66.25 EndZ=0
    g26: LineSegment StartX=-49.19 StartY=63.5 StartZ=0 EndX=-1.5 EndY=63.5 EndZ=0
    g27: LineSegment StartX=-49.19 StartY=60.5 StartZ=0 EndX=-1.5 EndY=60.5 EndZ=0
    g28: LineSegment StartX=-49.19 StartY=57.75 StartZ=0 EndX=-1.5 EndY=57.75 EndZ=0
    g29: LineSegment StartX=-49.19 StartY=54.75 StartZ=0 EndX=-1.5 EndY=54.75 EndZ=0
    g30: LineSegment StartX=-49.19 StartY=52 StartZ=0 EndX=-11.49 EndY=52 EndZ=0
    g31: LineSegment StartX=-49.19 StartY=49 StartZ=0 EndX=-11.49 EndY=49 EndZ=0
    g32: LineSegment StartX=-49.19 StartY=46.25 StartZ=0 EndX=-16.28 EndY=46.25 EndZ=0
    g33: LineSegment StartX=-49.19 StartY=43.25 StartZ=0 EndX=-16.28 EndY=43.25 EndZ=0
    g34: LineSegment StartX=-49.19 StartY=40.5 StartZ=0 EndX=-18.2337 EndY=40.5 EndZ=0
    g35: LineSegment StartX=-49.19 StartY=37.5 StartZ=0 EndX=-18.23 EndY=37.5 EndZ=0
    g36: LineSegment StartX=-49.19 StartY=34.5 StartZ=0 EndX=-18.2337 EndY=34.5 EndZ=0
    g37: LineSegment StartX=-49.19 StartY=31.5 StartZ=0 EndX=-18.23 EndY=31.5 EndZ=0
    g38: LineSegment StartX=-49.19 StartY=28.75 StartZ=0 EndX=-16.2837 EndY=28.75 EndZ=0
    g39: LineSegment StartX=-49.19 StartY=25.75 StartZ=0 EndX=-16.28 EndY=25.75 EndZ=0
    g40: LineSegment StartX=-49.19 StartY=23 StartZ=0 EndX=-11.49 EndY=23 EndZ=0
    g41: LineSegment StartX=-49.19 StartY=20 StartZ=0 EndX=-11.49 EndY=20 EndZ=0
    g42: LineSegment StartX=-49.19 StartY=17.25 StartZ=0 EndX=-1.5 EndY=17.25 EndZ=0
    g43: LineSegment StartX=-49.19 StartY=14.25 StartZ=0 EndX=-1.5 EndY=14.25 EndZ=0
    g44: LineSegment StartX=-49.19 StartY=11.5 StartZ=0 EndX=-1.5 EndY=11.5 EndZ=0
    g45: LineSegment StartX=-49.19 StartY=8.5 StartZ=0 EndX=-1.5 EndY=8.5 EndZ=0
    g46: LineSegment StartX=-49.19 StartY=5.75 StartZ=0 EndX=-1.5 EndY=5.75 EndZ=0
    g47: LineSegment StartX=-49.19 StartY=2.75 StartZ=0 EndX=-1.5 EndY=2.75 EndZ=0
  constraints (120):
    c: Vertical(g0)
    c: Distance(g0) = 3
    c: Block(g0)
    c: Vertical(g1)
    c: Distance(g1) = 3
    c: Vertical(g2)
    c: Equal(g0,g2) = 3
    c: Block(g2)
    c: Vertical(g3)
    c: Equal(g1,g3) = 3
    c: Vertical(g4)
    c: Equal(g0,g4) = 3
    c: Block(g4)
    c: Vertical(g5)
    c: Equal(g1,g5) = 3
    c: Vertical(g6)
    c: Equal(g0,g6) = 3
    c: Block(g6)
    c: Vertical(g7)
    c: Equal(g1,g7) = 3
    c: Vertical(g8)
    c: Equal(g0,g8) = 3
    c: Block(g8)
    c: Vertical(g9)
    c: Equal(g1,g9) = 3
    c: Vertical(g10)
    c: Equal(g0,g10) = 3
    c: Block(g10)
    c: Vertical(g11)
    c: Equal(g1,g11) = 3
    c: Block(g12)
    c: Block(g13)
    c: Block(g14)
    c: Block(g15)
    c: Block(g16)
    c: Block(g17)
    c: Block(g18)
    c: Block(g19)
    c: Block(g20)
    c: Block(g21)
    c: Block(g22)
    c: Block(g23)
    c: Block(g11)
    c: Block(g9)
    c: Block(g7)
    c: Block(g5)
    c: Block(g3)
    c: Block(g1)
    c: Coincident(g24,g0)
    c: Coincident(g24,g12)
    c: Horizontal(g24)
    c: Coincident(g25,g0)
    c: Coincident(g25,g12)
    c: Horizontal(g25)
    c: Coincident(g26,g1)
    c: Coincident(g26,g13)
    c: Horizontal(g26)
    c: Coincident(g27,g1)
    c: Coincident(g27,g13)
    c: Horizontal(g27)
    c: Coincident(g28,g2)
    c: Coincident(g28,g14)
    c: Horizontal(g28)
    c: Coincident(g29,g2)
    c: Coincident(g29,g14)
    c: Horizontal(g29)
    c: Coincident(g30,g3)
    c: Coincident(g30,g15)
    c: Horizontal(g30)
    c: Coincident(g31,g3)
    c: Coincident(g31,g15)
    c: Horizontal(g31)
    c: Coincident(g32,g4)
    c: Coincident(g32,g16)
    c: Horizontal(g32)
    c: Coincident(g33,g4)
    c: Coincident(g33,g16)
    c: Horizontal(g33)
    c: Coincident(g34,g5)
    c: Coincident(g34,g17)
    c: Horizontal(g34)
    c: Coincident(g35,g5)
    c: Coincident(g35,g17)
    c: Horizontal(g35)
    c: Coincident(g36,g6)
    c: Coincident(g36,g19)
    c: Horizontal(g36)
    c: Coincident(g37,g6)
    c: Coincident(g37,g19)
    c: Horizontal(g37)
    c: Coincident(g38,g7)
    c: Coincident(g38,g18)
    c: Horizontal(g38)
    c: Coincident(g39,g7)
    c: Coincident(g39,g18)
    c: Horizontal(g39)
    c: Coincident(g40,g8)
    c: Coincident(g40,g20)
    c: Horizontal(g40)
    c: Coincident(g41,g8)
    c: Coincident(g41,g20)
    c: Horizontal(g41)
    c: Coincident(g42,g9)
    c: Coincident(g42,g23)
    c: Horizontal(g42)
    c: Coincident(g43,g9)
    c: Coincident(g43,g23)
    c: Horizontal(g43)
    c: Coincident(g44,g10)
    c: Coincident(g44,g22)
    c: Horizontal(g44)
    c: Coincident(g45,g10)
    c: Coincident(g45,g22)
    c: Horizontal(g45)
    c: Coincident(g46,g11)
    c: Coincident(g46,g21)
    c: Horizontal(g46)
    c: Coincident(g47,g11)
    c: Coincident(g47,g21)
    c: Horizontal(g47)
FEATURE [Part::Extrusion] Extrude065
  Base = -> Sketch074
  Dir = (1,0,0)
  DirMode = 2
  FaceMakerClass = Part::FaceMakerBullseye
  LengthFwd = 23
  LengthRev = 0
  Placement = pos=(-19,0,0) rot=(0,0,1;0rad)
  Solid = true
  Symmetric = false
FEATURE [Part::Fillet] Fillet056  label="removeToCreateVentalationHoles003"
  Base = -> Extrude065
  Edges = <same value as first occurrence — deduplicated (x6 in doc)>
  Placement = pos=(7,0.02,0) rot=(0,0,1;0rad)
FEATURE [Part::Revolution] Revolve158  label="removeToCreateScrewAndThreadedInsertHole065"
  Angle = 360
  Axis = (0,1,0)
  Base = (0,0,0)
  FaceMakerClass = Part::FaceMakerBullseye
  Placement = pos=(12.5,0,62) rot=(0,0,1;0rad)
  Solid = false
  Source = -> Face146
  Symmetric = false
FEATURE [Part::Revolution] Revolve159  label="removeToCreateScrewAndThreadedInsertHole066"
  Angle = 360
  Axis = (0,1,0)
  Base = (0,0,0)
  FaceMakerClass = Part::FaceMakerBullseye
  Placement = pos=(89.5,0,68.5) rot=(0,0,1;0rad)
  Solid = false
  Source = -> Face143
  Symmetric = false
FEATURE [Part::Revolution] Revolve160  label="removeToCreateScrewAndThreadedInsertHole067"
  Angle = 360
  Axis = (0,1,0)
  Base = (0,0,0)
  FaceMakerClass = Part::FaceMakerBullseye
  Placement = pos=(89.5,0,3.5) rot=(0,0,1;0rad)
  Solid = false
  Source = -> Face142
  Symmetric = false
FEATURE [Part::Revolution] Revolve161  label="removeToCreateScrewAndThreadedInsertHole068"
  Angle = 360
  Axis = (0,1,0)
  Base = (0,0,0)
  FaceMakerClass = Part::FaceMakerBullseye
  Placement = pos=(109.5,4.7,3.5) rot=(0,0,1;0rad)
  Solid = false
  Source = -> Face145
  Symmetric = false
FEATURE [Part::Revolution] Revolve162  label="removeToCreateScrewAndThreadedInsertHole069"
  Angle = 360
  Axis = (0,1,0)
  Base = (0,0,0)
  FaceMakerClass = Part::FaceMakerBullseye
  Placement = pos=(109.5,4.7,68.5) rot=(0,0,1;0rad)
  Solid = false
  Source = -> Face144
  Symmetric = false
FEATURE [Part::MultiFuse] Fusion141  label="removeToCreateScrewAndThreadedInsertHole064"
  Shapes = -> [Revolve162,Revolve161,Revolve160,Revolve159,Revolve158,Revolve157]
FEATURE [Part::Cylinder] Cylinder062
  Angle = 360
  AttacherType = Attacher::AttachEngine3D
  Height = 20
  Placement = pos=(0,0,36.15) rot=(0,0,1;0rad)
  Radius = 14
FEATURE [Part::Cylinder] Cylinder063
  Angle = 360
  AttacherType = Attacher::AttachEngine3D
  Height = 10
  Placement = pos=(0,0,36.15) rot=(0,0,1;0rad)
  Radius = 4
FEATURE [Part::MultiFuse] Fusion139  label="removeToCreteHoleForPlugHousing052"
  Placement = pos=(70,19,36) rot=(0,1,0;1.5708rad)
  Shapes = -> [Cylinder062,Cylinder063]
FEATURE [Part::Cut] Cut060  label="bottom017"
  Base = -> Extrude064
  Tool = -> Fusion139
FEATURE [Part::Cut] Cut061  label="bottom019"
  Base = -> Cut060
  Tool = -> Fusion141
FEATURE [Part::MultiFuse] Fusion140  label="bottom018"
  Shapes = -> [Cut061,Cut058]
FEATURE [Part::Cut] Cut059  label="bottom020"
  Base = -> Fusion140
  Tool = -> Fillet056
FEATURE [Part::Box] Box036  label="Cube021"
  AttacherType = Attacher::AttachEngine3D
  Height = 80
  Length = 26
  Placement = pos=(0,-1,-5) rot=(0,0,1;0rad)
  Width = 11
FEATURE [Part::Cut] Cut062  label="removeFromBottom002"
  Base = -> Cut057
  Tool = -> Box036
FEATURE [Part::Cut] Cut063
  Base = -> Cut059
  Tool = -> Cut062
FEATURE [Part::Cut] Cut064  label="pcbStands"
  Base = -> Fusion095
  Tool = -> Fusion127
FEATURE [Sketcher::SketchObject] Sketch075  label="topSketch022"
  FullyConstrained = true
  sketch-geometry (6):
    g0: LineSegment StartX=19 StartY=38 StartZ=0 EndX=117 EndY=38 EndZ=0
    g1: ArcOfCircle CenterX=19 CenterY=19 CenterZ=0 NormalX=0 NormalY=0 NormalZ=1 AngleXU=0 Radius=19 StartAngle=1.5708 EndAngle=3.14159
    g2: LineSegment StartX=117 StartY=38 StartZ=0 EndX=117 EndY=19 EndZ=0
    g3: LineSegment StartX=98 StartY=1.0161e-12 StartZ=0 EndX=5.22862e-06 EndY=1.0161e-12 EndZ=0
    g4: LineSegment StartX=5.22862e-06 StartY=19 StartZ=0 EndX=5.22862e-06 EndY=1.0161e-12 EndZ=0
    g5: ArcOfCircle CenterX=98 CenterY=19 CenterZ=0 NormalX=0 NormalY=0 NormalZ=1 AngleXU=0 Radius=19 StartAngle=4.71239 EndAngle=6.28319
  constraints (16):
    c: Horizontal(g0)
    c: Distance(g0) = 98
    c: Coincident(g1,g0)
    c: Block(g1)
    c: Coincident(g2,g0)
    c: Vertical(g2)
    c: Distance(g2) = 19
    c: Horizontal(g3)
    c: Coincident(g4,g1)
    c: Vertical(g4)
    c: Coincident(g3,g4)
    c: Block(g3)
    c: Coincident(g5,g2)
    c: Coincident(g5,g3)
    c: Block(g0)
    c: Block(g5)
FEATURE [Part::Extrusion] Extrude067  label="sideB003"
  Base = -> Sketch075
  Dir = (0,0,1)
  DirMode = 2
  FaceMakerClass = Part::FaceMakerBullseye
  LengthFwd = 3
  LengthRev = 0
  Placement = pos=(0,0,71.7) rot=(0,0,1;0rad)
  Solid = true
  Symmetric = false
FEATURE [Sketcher::SketchObject] Sketch076  label="topSketch023"
  FullyConstrained = true
  sketch-geometry (6):
    g0: LineSegment StartX=19 StartY=38 StartZ=0 EndX=117 EndY=38 EndZ=0
    g1: ArcOfCircle CenterX=19 CenterY=19 CenterZ=0 NormalX=0 NormalY=0 NormalZ=1 AngleXU=0 Radius=19 StartAngle=1.5708 EndAngle=3.14159
    g2: LineSegment StartX=117 StartY=38 StartZ=0 EndX=117 EndY=19 EndZ=0
    g3: LineSegment StartX=98 StartY=1.0161e-12 StartZ=0 EndX=5.22862e-06 EndY=1.0161e-12 EndZ=0
    g4: LineSegment StartX=5.22862e-06 StartY=19 StartZ=0 EndX=5.22862e-06 EndY=1.0161e-12 EndZ=0
    g5: ArcOfCircle CenterX=98 CenterY=19 CenterZ=0 NormalX=0 NormalY=0 NormalZ=1 AngleXU=0 Radius=19 StartAngle=4.71239 EndAngle=6.28319
  constraints (16):
    c: Horizontal(g0)
    c: Distance(g0) = 98
    c: Coincident(g1,g0)
    c: Block(g1)
    c: Coincident(g2,g0)
    c: Vertical(g2)
    c: Distance(g2) = 19
    c: Horizontal(g3)
    c: Coincident(g4,g1)
    c: Vertical(g4)
    c: Coincident(g3,g4)
    c: Block(g3)
    c: Coincident(g5,g2)
    c: Coincident(g5,g3)
    c: Block(g0)
    c: Block(g5)
FEATURE [Part::Extrusion] Extrude066  label="sideA003"
  Base = -> Sketch076
  Dir = (0,0,1)
  DirMode = 2
  FaceMakerClass = Part::FaceMakerBullseye
  LengthFwd = 3
  LengthRev = 0
  Placement = pos=(0,0,-2.7) rot=(0,0,1;0rad)
  Solid = true
  Symmetric = false
FEATURE [Part::MultiFuse] Fusion142  label="removeFromBottom003"
  Placement = pos=(2,0,0) rot=(0,0,1;0rad)
  Shapes = -> [Extrude066,Extrude067]
FEATURE [Part::Cut] Cut065  label="screwRetainers002"
  Base = -> Fusion096
  Tool = -> Fusion142
FEATURE [Sketcher::SketchObject] Sketch077
  FullyConstrained = true
  Placement = pos=(117,19,0) rot=(0.57735,0.57735,0.57735;2.0944rad)
  sketch-geometry (8):
    g0: LineSegment StartX=-49.19 StartY=63.5 StartZ=0 EndX=-49.19 EndY=60.5 EndZ=0
    g1: LineSegment StartX=-49.19 StartY=11.5 StartZ=0 EndX=-49.19 EndY=8.5 EndZ=0
    g2: ArcOfCircle CenterX=-1.5 CenterY=62 CenterZ=0 NormalX=0 NormalY=0 NormalZ=1 AngleXU=0 Radius=1.5 StartAngle=4.71239 EndAngle=7.85398
    g3: ArcOfCircle CenterX=-1.5 CenterY=10 CenterZ=0 NormalX=0 NormalY=0 NormalZ=1 AngleXU=0 Radius=1.5 StartAngle=4.71239 EndAngle=7.85398
    g4: LineSegment StartX=-49.19 StartY=63.5 StartZ=0 EndX=-1.5 EndY=63.5 EndZ=0
    g5: LineSegment StartX=-49.19 StartY=60.5 StartZ=0 EndX=-1.5 EndY=60.5 EndZ=0
    g6: LineSegment StartX=-49.19 StartY=11.5 StartZ=0 EndX=-1.5 EndY=11.5 EndZ=0
    g7: LineSegment StartX=-49.19 StartY=8.5 StartZ=0 EndX=-1.5 EndY=8.5 EndZ=0
  constraints (19):
    c: Vertical(g0)
    c: Distance(g0) = 3
    c: Vertical(g1)
    c: Block(g1)
    c: Block(g2)
    c: Block(g3)
    c: Block(g0)
    c: Coincident(g4,g0)
    c: Coincident(g4,g2)
    c: Horizontal(g4)
    c: Coincident(g5,g0)
    c: Coincident(g5,g2)
    c: Horizontal(g5)
    c: Coincident(g6,g1)
    c: Coincident(g6,g3)
    c: Horizontal(g6)
    c: Coincident(g7,g1)
    c: Coincident(g7,g3)
    c: Horizontal(g7)
FEATURE [Part::Extrusion] Extrude068
  Base = -> Sketch077
  Dir = (1,0,0)
  DirMode = 2
  FaceMakerClass = Part::FaceMakerBullseye
  LengthFwd = 10
  LengthRev = 0
  Solid = true
  Symmetric = false
FEATURE [Part::Fillet] Fillet057  label="removeFromtMoreFrontCaseScrewRetainers002"
  Base = -> Extrude068
  Edges = 4 edges r=1.49: [Edge6,Edge11,Edge18,Edge23]
  Placement = pos=(-12,0,0) rot=(0,0,1;0rad)
FEATURE [Sketcher::SketchObject] Sketch078
  FullyConstrained = true
  Placement = pos=(117,19,0) rot=(0.57735,0.57735,0.57735;2.0944rad)
  sketch-geometry (8):
    g0: LineSegment StartX=-49.19 StartY=69.25 StartZ=0 EndX=-49.19 EndY=66.25 EndZ=0
    g1: LineSegment StartX=-49.19 StartY=5.75 StartZ=0 EndX=-49.19 EndY=2.75 EndZ=0
    g2: ArcOfCircle CenterX=-1.5 CenterY=67.75 CenterZ=0 NormalX=0 NormalY=0 NormalZ=1 AngleXU=0 Radius=1.5 StartAngle=4.71239 EndAngle=7.85398
    g3: ArcOfCircle CenterX=-1.5 CenterY=4.25 CenterZ=0 NormalX=0 NormalY=0 NormalZ=1 AngleXU=0 Radius=1.5 StartAngle=4.71239 EndAngle=7.85398
    g4: LineSegment StartX=-49.19 StartY=69.25 StartZ=0 EndX=-1.5 EndY=69.25 EndZ=0
    g5: LineSegment StartX=-49.19 StartY=66.25 StartZ=0 EndX=-1.5 EndY=66.25 EndZ=0
    g6: LineSegment StartX=-49.19 StartY=5.75 StartZ=0 EndX=-1.5 EndY=5.75 EndZ=0
    g7: LineSegment StartX=-49.19 StartY=2.75 StartZ=0 EndX=-1.5 EndY=2.75 EndZ=0
  constraints (19):
    c: Vertical(g0)
    c: Distance(g0) = 3
    c: Block(g0)
    c: Vertical(g1)
    c: Block(g2)
    c: Block(g3)
    c: Block(g1)
    c: Coincident(g4,g0)
    c: Coincident(g4,g2)
    c: Horizontal(g4)
    c: Coincident(g5,g0)
    c: Coincident(g5,g2)
    c: Horizontal(g5)
    c: Coincident(g6,g1)
    c: Coincident(g6,g3)
    c: Horizontal(g6)
    c: Coincident(g7,g1)
    c: Coincident(g7,g3)
    c: Horizontal(g7)
FEATURE [Part::Extrusion] Extrude069
  Base = -> Sketch078
  Dir = (1,0,0)
  DirMode = 2
  FaceMakerClass = Part::FaceMakerBullseye
  LengthFwd = 10
  LengthRev = 0
  Solid = true
  Symmetric = false
FEATURE [Part::Fillet] Fillet058  label="removeFromtMoreFrontCaseScrewRetainers003"
  Base = -> Extrude069
  Edges = 4 edges r=1.49: [Edge6,Edge11,Edge18,Edge23]
  Placement = pos=(-4,0,0) rot=(0,0,1;0rad)
FEATURE [Part::Cut] Cut066
  Base = -> Cut065
  Tool = -> Fillet058
FEATURE [Part::Cut] Cut067  label="screwPillars"
  Base = -> Cut066
  Tool = -> Fillet057
FEATURE [Part::MultiFuse] Fusion143  label="bottom021"
  Shapes = -> [Cut031,Cut063]
FEATURE [Part::Cylinder] Cylinder
  Angle = 360
  AttacherType = Attacher::AttachEngine3D
  Height = 10
  Placement = pos=(20.65,12,4.68) rot=(1,0,0;1.5708rad)
  Radius = 2
FEATURE [Part::Cylinder] Cylinder064
  Angle = 360
  AttacherType = Attacher::AttachEngine3D
  Height = 10
  Placement = pos=(20.65,12,67.38) rot=(1,0,0;1.5708rad)
  Radius = 2
FEATURE [Part::Cylinder] Cylinder065
  Angle = 360
  AttacherType = Attacher::AttachEngine3D
  Height = 10
  Placement = pos=(77.15,12,67.38) rot=(1,0,0;1.5708rad)
  Radius = 2
FEATURE [Part::Cylinder] Cylinder066
  Angle = 360
  AttacherType = Attacher::AttachEngine3D
  Height = 10
  Placement = pos=(77.15,12,4.68) rot=(1,0,0;1.5708rad)
  Radius = 2
FEATURE [Part::MultiFuse] Fusion144  label="removeFromThreadedInsertHousing"
  Shapes = -> [Cylinder065,Cylinder064,Cylinder,Cylinder066]
FEATURE [Part::Cut] Cut068  label="pcbStands001"
  Base = -> Cut064
  Tool = -> Fusion144
FEATURE [Part::MultiFuse] Fusion145
  Shapes = -> [Cut068,Fusion143]
FEATURE [Part::MultiFuse] Fusion146
  Shapes = -> [Fusion145]
FEATURE [Part::MultiFuse] Fusion147  label="bottom022"
  Shapes = -> [Cut067,Fusion146]
FEATURE [Part::MultiFuse] Fusion148  label="casePillars005"
  Shapes = -> [Cut047,Fusion092]
FEATURE [Part::MultiFuse] Fusion149  label="bottom023"
  Shapes = -> [Fusion124,Fusion113,Fusion147]
FEATURE [Part::MultiFuse] Fusion150  label="topBits"
  Shapes = -> [Cut025,Fusion148,Cut030,Fillet034]
FEATURE [Part::Feature] Face149 .. Face152  x4 (patterned run collapsed; names and placements below)
  shape: bbox 3.2 x 1.5 x 2e-07 mm, 1 faces, 0 solids (baked)
FEATURE [Part::Feature] Face153
  shape: bbox 3.6 x 3.2 x 2e-07 mm, 1 faces, 0 solids (baked)
FEATURE [Part::Feature] Face154
  shape: bbox 3.6 x 3.2 x 2e-07 mm, 1 faces, 0 solids (baked)
FEATURE [Sketcher::SketchObject] Sketch079  label="topSketch024"
  FullyConstrained = true
  sketch-geometry (6):
    g0: LineSegment StartX=19 StartY=38 StartZ=0 EndX=117 EndY=38 EndZ=0
    g1: ArcOfCircle CenterX=19 CenterY=19 CenterZ=0 NormalX=0 NormalY=0 NormalZ=1 AngleXU=0 Radius=19 StartAngle=1.5708 EndAngle=3.14159
    g2: LineSegment StartX=117 StartY=38 StartZ=0 EndX=117 EndY=19 EndZ=0
    g3: LineSegment StartX=98 StartY=1.0161e-12 StartZ=0 EndX=5.22862e-06 EndY=1.0161e-12 EndZ=0
    g4: LineSegment StartX=5.22862e-06 StartY=19 StartZ=0 EndX=5.22862e-06 EndY=1.0161e-12 EndZ=0
    g5: ArcOfCircle CenterX=98 CenterY=19 CenterZ=0 NormalX=0 NormalY=0 NormalZ=1 AngleXU=0 Radius=19 StartAngle=4.71239 EndAngle=6.28319
  constraints (16):
    c: Horizontal(g0)
    c: Distance(g0) = 98
    c: Coincident(g1,g0)
    c: Block(g1)
    c: Coincident(g2,g0)
    c: Vertical(g2)
    c: Distance(g2) = 19
    c: Horizontal(g3)
    c: Coincident(g4,g1)
    c: Vertical(g4)
    c: Coincident(g3,g4)
    c: Block(g3)
    c: Coincident(g5,g2)
    c: Coincident(g5,g3)
    c: Block(g0)
    c: Block(g5)
FEATURE [Sketcher::SketchObject] Sketch080  label="topSketch025"
  FullyConstrained = true
  sketch-geometry (6):
    g0: LineSegment StartX=19 StartY=38 StartZ=0 EndX=117 EndY=38 EndZ=0
    g1: ArcOfCircle CenterX=19 CenterY=19 CenterZ=0 NormalX=0 NormalY=0 NormalZ=1 AngleXU=0 Radius=19 StartAngle=1.5708 EndAngle=3.14159
    g2: LineSegment StartX=117 StartY=38 StartZ=0 EndX=117 EndY=19 EndZ=0
    g3: LineSegment StartX=98 StartY=1.0161e-12 StartZ=0 EndX=5.22862e-06 EndY=1.0161e-12 EndZ=0
    g4: LineSegment StartX=5.22862e-06 StartY=19 StartZ=0 EndX=5.22862e-06 EndY=1.0161e-12 EndZ=0
    g5: ArcOfCircle CenterX=98 CenterY=19 CenterZ=0 NormalX=0 NormalY=0 NormalZ=1 AngleXU=0 Radius=19 StartAngle=4.71239 EndAngle=6.28319
  constraints (16):
    c: Horizontal(g0)
    c: Distance(g0) = 98
    c: Coincident(g1,g0)
    c: Block(g1)
    c: Coincident(g2,g0)
    c: Vertical(g2)
    c: Distance(g2) = 19
    c: Horizontal(g3)
    c: Coincident(g4,g1)
    c: Vertical(g4)
    c: Coincident(g3,g4)
    c: Block(g3)
    c: Coincident(g5,g2)
    c: Coincident(g5,g3)
    c: Block(g0)
    c: Block(g5)
FEATURE [Part::Extrusion] Extrude070  label="sideA004"
  Base = -> Sketch080
  Dir = (0,0,1)
  DirMode = 2
  FaceMakerClass = Part::FaceMakerBullseye
  LengthFwd = 3
  LengthRev = 0
  Placement = pos=(0,0,-2.7) rot=(0,0,1;0rad)
  Solid = true
  Symmetric = false
FEATURE [Sketcher::SketchObject] Sketch081
  FullyConstrained = true
  Placement = pos=(117,19,0) rot=(0.57735,0.57735,0.57735;2.0944rad)
  sketch-geometry (8):
    g0: LineSegment StartX=-49.19 StartY=63.5 StartZ=0 EndX=-49.19 EndY=60.5 EndZ=0
    g1: LineSegment StartX=-49.19 StartY=11.5 StartZ=0 EndX=-49.19 EndY=8.5 EndZ=0
    g2: ArcOfCircle CenterX=-1.5 CenterY=62 CenterZ=0 NormalX=0 NormalY=0 NormalZ=1 AngleXU=0 Radius=1.5 StartAngle=4.71239 EndAngle=7.85398
    g3: ArcOfCircle CenterX=-1.5 CenterY=10 CenterZ=0 NormalX=0 NormalY=0 NormalZ=1 AngleXU=0 Radius=1.5 StartAngle=4.71239 EndAngle=7.85398
    g4: LineSegment StartX=-49.19 StartY=63.5 StartZ=0 EndX=-1.5 EndY=63.5 EndZ=0
    g5: LineSegment StartX=-49.19 StartY=60.5 StartZ=0 EndX=-1.5 EndY=60.5 EndZ=0
    g6: LineSegment StartX=-49.19 StartY=11.5 StartZ=0 EndX=-1.5 EndY=11.5 EndZ=0
    g7: LineSegment StartX=-49.19 StartY=8.5 StartZ=0 EndX=-1.5 EndY=8.5 EndZ=0
  constraints (19):
    c: Vertical(g0)
    c: Distance(g0) = 3
    c: Vertical(g1)
    c: Block(g1)
    c: Block(g2)
    c: Block(g3)
    c: Block(g0)
    c: Coincident(g4,g0)
    c: Coincident(g4,g2)
    c: Horizontal(g4)
    c: Coincident(g5,g0)
    c: Coincident(g5,g2)
    c: Horizontal(g5)
    c: Coincident(g6,g1)
    c: Coincident(g6,g3)
    c: Horizontal(g6)
    c: Coincident(g7,g1)
    c: Coincident(g7,g3)
    c: Horizontal(g7)
FEATURE [Part::Extrusion] Extrude071  label="sideB004"
  Base = -> Sketch079
  Dir = (0,0,1)
  DirMode = 2
  FaceMakerClass = Part::FaceMakerBullseye
  LengthFwd = 3
  LengthRev = 0
  Placement = pos=(0,0,71.7) rot=(0,0,1;0rad)
  Solid = true
  Symmetric = false
FEATURE [Part::MultiFuse] Fusion152  label="removeFromBottom004"
  Placement = pos=(2,0,0) rot=(0,0,1;0rad)
  Shapes = -> [Extrude070,Extrude071]
FEATURE [Part::Extrusion] Extrude072
  Base = -> Sketch081
  Dir = (1,0,0)
  DirMode = 2
  FaceMakerClass = Part::FaceMakerBullseye
  LengthFwd = 10
  LengthRev = 0
  Solid = true
  Symmetric = false
FEATURE [Part::Fillet] Fillet059  label="removeFromtMoreFrontCaseScrewRetainers004"
  Base = -> Extrude072
  Edges = 4 edges r=1.49: [Edge6,Edge11,Edge18,Edge23]
  Placement = pos=(-12,0,0) rot=(0,0,1;0rad)
FEATURE [Sketcher::SketchObject] Sketch082
  FullyConstrained = true
  Placement = pos=(117,19,0) rot=(0.57735,0.57735,0.57735;2.0944rad)
  sketch-geometry (8):
    g0: LineSegment StartX=-49.19 StartY=69.25 StartZ=0 EndX=-49.19 EndY=66.25 EndZ=0
    g1: LineSegment StartX=-49.19 StartY=5.75 StartZ=0 EndX=-49.19 EndY=2.75 EndZ=0
    g2: ArcOfCircle CenterX=-1.5 CenterY=67.75 CenterZ=0 NormalX=0 NormalY=0 NormalZ=1 AngleXU=0 Radius=1.5 StartAngle=4.71239 EndAngle=7.85398
    g3: ArcOfCircle CenterX=-1.5 CenterY=4.25 CenterZ=0 NormalX=0 NormalY=0 NormalZ=1 AngleXU=0 Radius=1.5 StartAngle=4.71239 EndAngle=7.85398
    g4: LineSegment StartX=-49.19 StartY=69.25 StartZ=0 EndX=-1.5 EndY=69.25 EndZ=0
    g5: LineSegment StartX=-49.19 StartY=66.25 StartZ=0 EndX=-1.5 EndY=66.25 EndZ=0
    g6: LineSegment StartX=-49.19 StartY=5.75 StartZ=0 EndX=-1.5 EndY=5.75 EndZ=0
    g7: LineSegment StartX=-49.19 StartY=2.75 StartZ=0 EndX=-1.5 EndY=2.75 EndZ=0
  constraints (19):
    c: Vertical(g0)
    c: Distance(g0) = 3
    c: Block(g0)
    c: Vertical(g1)
    c: Block(g2)
    c: Block(g3)
    c: Block(g1)
    c: Coincident(g4,g0)
    c: Coincident(g4,g2)
    c: Horizontal(g4)
    c: Coincident(g5,g0)
    c: Coincident(g5,g2)
    c: Horizontal(g5)
    c: Coincident(g6,g1)
    c: Coincident(g6,g3)
    c: Horizontal(g6)
    c: Coincident(g7,g1)
    c: Coincident(g7,g3)
    c: Horizontal(g7)
FEATURE [Part::Extrusion] Extrude073
  Base = -> Sketch082
  Dir = (1,0,0)
  DirMode = 2
  FaceMakerClass = Part::FaceMakerBullseye
  LengthFwd = 10
  LengthRev = 0
  Solid = true
  Symmetric = false
FEATURE [Part::Fillet] Fillet060  label="removeFromtMoreFrontCaseScrewRetainers005"
  Base = -> Extrude073
  Edges = 4 edges r=1.49: [Edge6,Edge11,Edge18,Edge23]
  Placement = pos=(-4,0,0) rot=(0,0,1;0rad)
FEATURE [Part::Revolution] Revolve163  label="backCaseScrewRetainer004"
  Angle = 360
  Axis = (0,1,0)
  Base = (0,0,0)
  FaceMakerClass = Part::FaceMakerBullseye
  Placement = pos=(12.5,3,62) rot=(0,0,1;0rad)
  Solid = false
  Source = -> Face149
  Symmetric = false
FEATURE [Part::Revolution] Revolve164  label="frontCaseScrewRetainer006"
  Angle = 360
  Axis = (0,1,0)
  Base = (0,0,0)
  FaceMakerClass = Part::FaceMakerBullseye
  Placement = pos=(89.5,3,68.5) rot=(0,0,1;0rad)
  Solid = false
  Source = -> Face151
  Symmetric = false
FEATURE [Part::Revolution] Revolve165  label="frontCaseScrewRetainer007"
  Angle = 360
  Axis = (0,1,0)
  Base = (0,0,0)
  FaceMakerClass = Part::FaceMakerBullseye
  Placement = pos=(89.5,3,3.5) rot=(0,0,1;0rad)
  Solid = false
  Source = -> Face152
  Symmetric = false
FEATURE [Part::Revolution] Revolve166  label="backCaseScrewRetainer005"
  Angle = 360
  Axis = (0,1,0)
  Base = (0,0,0)
  FaceMakerClass = Part::FaceMakerBullseye
  Placement = pos=(12.5,3,10) rot=(0,0,1;0rad)
  Solid = false
  Source = -> Face150
  Symmetric = false
FEATURE [Part::Revolution] Revolve167  label="moreFrontCaseScrewRetainer006"
  Angle = 360
  Axis = (0,1,0)
  Base = (0,0,0)
  FaceMakerClass = Part::FaceMakerBullseye
  Placement = pos=(109.5,4.5,68.5) rot=(0,0,1;0rad)
  Solid = false
  Source = -> Face153
  Symmetric = false
FEATURE [Part::Revolution] Revolve168  label="moreFrontCaseScrewRetainer007"
  Angle = 360
  Axis = (0,1,0)
  Base = (0,0,0)
  FaceMakerClass = Part::FaceMakerBullseye
  Placement = pos=(109.5,4.5,3.5) rot=(0,0,1;0rad)
  Solid = false
  Source = -> Face154
  Symmetric = false
FEATURE [Part::MultiFuse] Fusion151  label="screwRetainers003"
  Shapes = -> [Revolve168,Revolve167,Revolve166,Revolve165,Revolve164,Revolve163]
FEATURE [Part::Cut] Cut069  label="screwRetainers004"
  Base = -> Fusion151
  Tool = -> Fusion152
FEATURE [Part::Cut] Cut070
  Base = -> Cut069
  Tool = -> Fillet060
FEATURE [Part::Cut] Cut071  label="screwPillars001"
  Base = -> Cut070
  Tool = -> Fillet059
FEATURE [Part::MultiFuse] Fusion153  label="bottom024"
  Shapes = -> [Fusion149,Cut071]
FEATURE [Part::Cylinder] Cylinder067
  Angle = 360
  AttacherType = Attacher::AttachEngine3D
  Height = 10
  Placement = pos=(20.65,12,4.68) rot=(1,0,0;1.5708rad)
  Radius = 2
FEATURE [Part::Cylinder] Cylinder068
  Angle = 360
  AttacherType = Attacher::AttachEngine3D
  Height = 10
  Placement = pos=(20.65,12,67.38) rot=(1,0,0;1.5708rad)
  Radius = 2
FEATURE [Part::Cylinder] Cylinder069
  Angle = 360
  AttacherType = Attacher::AttachEngine3D
  Height = 10
  Placement = pos=(77.15,12,67.38) rot=(1,0,0;1.5708rad)
  Radius = 2
FEATURE [Part::Cylinder] Cylinder070
  Angle = 360
  AttacherType = Attacher::AttachEngine3D
  Height = 10
  Placement = pos=(77.15,12,4.68) rot=(1,0,0;1.5708rad)
  Radius = 2
FEATURE [Part::MultiFuse] Fusion154  label="removeFromThreadedInsertHousing001"
  Shapes = -> [Cylinder069,Cylinder068,Cylinder067,Cylinder070]
FEATURE [Part::Cut] Cut072  label="bottom025"
  Base = -> Fusion153
  Tool = -> Fusion154
FEATURE [Image::ImagePlane] ImagePlane
  XSize = 339
  YSize = 72
FEATURE [Sketcher::SketchObject] Sketch083
  FullyConstrained = true
  MapMode = 5
  Support = -> [XY_Plane]
  sketch-geometry (242):
    g0: LineSegment StartX=-151.619 StartY=28.8932 StartZ=0 EndX=-140.819 EndY=28.8932 EndZ=0
    g1: LineSegment StartX=-151.619 StartY=24.0313 StartZ=0 EndX=-151.619 EndY=28.8932 EndZ=0
    g2: LineSegment StartX=-140.819 StartY=17.7713 StartZ=0 EndX=-151.619 EndY=17.7713 EndZ=0
    g3: LineSegment StartX=-151.619 StartY=17.7713 StartZ=0 EndX=-151.619 EndY=22.6313 EndZ=0
    g4: LineSegment StartX=-151.619 StartY=22.6313 StartZ=0 EndX=-145.128 EndY=22.6313 EndZ=0
    g5: LineSegment StartX=-145.128 StartY=24.0313 StartZ=0 EndX=-140.819 EndY=28.8932 EndZ=0
    g6: LineSegment StartX=-145.128 StartY=22.6313 StartZ=0 EndX=-140.819 EndY=17.7713 EndZ=0
    g7: ArcOfCircle CenterX=-155.157 CenterY=23.3323 CenterZ=0 NormalX=0 NormalY=0 NormalZ=1 AngleXU=0 Radius=6.92354 StartAngle=1.03434 EndAngle=5.24885
    g8: ArcOfCircle CenterX=-155.157 CenterY=23.3323 CenterZ=0 NormalX=0 NormalY=0 NormalZ=1 AngleXU=0 Radius=12.6269 StartAngle=1.28675 EndAngle=4.99643
    g9: LineSegment StartX=-151.619 StartY=35.4532 StartZ=0 EndX=-151.619 EndY=29.2832 EndZ=0
    g10: LineSegment StartX=-151.619 StartY=17.3813 StartZ=0 EndX=-151.619 EndY=11.2113 EndZ=0
    g11-g21: Circle x11 (B-spline internal-alignment scaffolding for g22; pole/knot coordinates omitted)
    g22: BSplineCurve PolesCount=11 KnotsCount=9 Degree=3 IsPeriodic=0
    g23-g31: GeomPoint x9 (B-spline internal-alignment scaffolding for g22; pole/knot coordinates omitted)
    g32-g49: Circle x18 (B-spline internal-alignment scaffolding for g50; pole/knot coordinates omitted)
    g50: BSplineCurve PolesCount=18 KnotsCount=16 Degree=3 IsPeriodic=0
    g51-g66: GeomPoint x16 (B-spline internal-alignment scaffolding for g50; pole/knot coordinates omitted)
    g67: LineSegment StartX=-117.124 StartY=30.093 StartZ=0 EndX=-117.603 EndY=26.5272 EndZ=0
    g68: LineSegment StartX=-117.603 StartY=17.8472 StartZ=0 EndX=-117.124 EndY=14.2659 EndZ=0
    g69: Ellipse CenterX=-109.671 CenterY=20.025 CenterZ=0 NormalX=0 NormalY=0 NormalZ=1 MajorRadius=3.34798 MinorRadius=2.71052 AngleXU=-1.56793
    g70: GeomPoint X=-109.666 Y=18.0598 Z=0
    g71: GeomPoint X=-109.677 Y=21.9902 Z=0
    g72: Ellipse CenterX=-109.671 CenterY=20.0123 CenterZ=0 NormalX=0 NormalY=0 NormalZ=1 MajorRadius=6.93002 MinorRadius=6.36273 AngleXU=-3.13976
    g73: GeomPoint X=-112.417 Y=20.0073 Z=0
    g74: GeomPoint X=-106.925 Y=20.0173 Z=0
    g75: Ellipse CenterX=-51.7682 CenterY=20.1463 CenterZ=0 NormalX=0 NormalY=0 NormalZ=1 MajorRadius=3.19279 MinorRadius=2.71052 AngleXU=-1.52774
    g76: GeomPoint X=-51.6955 Y=18.4606 Z=0
    g77: GeomPoint X=-51.8408 Y=21.832 Z=0
    g78: GeomPoint X=-54.5142 Y=20.1413 Z=0
    g79: GeomPoint X=-49.0221 Y=20.1513 Z=0
    g80: Ellipse CenterX=-51.7682 CenterY=20.1463 CenterZ=0 NormalX=0 NormalY=0 NormalZ=1 MajorRadius=6.93002 MinorRadius=6.36273 AngleXU=-3.13976
    g81: Ellipse CenterX=-22.8436 CenterY=20.1783 CenterZ=0 NormalX=0 NormalY=0 NormalZ=1 MajorRadius=3.31512 MinorRadius=2.71052 AngleXU=-1.60214
    g82: GeomPoint X=-22.9034 Y=18.2706 Z=0
    g83: GeomPoint X=-22.7838 Y=22.0861 Z=0
    g84: GeomPoint X=-25.5897 Y=20.1733 Z=0
    g85: GeomPoint X=-20.0976 Y=20.1833 Z=0
    g86: Ellipse CenterX=-22.8436 CenterY=20.1783 CenterZ=0 NormalX=0 NormalY=0 NormalZ=1 MajorRadius=6.93002 MinorRadius=6.36273 AngleXU=-3.13976
    g87: LineSegment StartX=-101.889 StartY=14.1107 StartZ=0 EndX=-97.7455 EndY=14.1107 EndZ=0
    g88: LineSegment StartX=-93.8155 StartY=14.1107 StartZ=0 EndX=-89.6755 EndY=14.1107 EndZ=0
    g89: LineSegment StartX=-85.7455 StartY=14.1107 StartZ=0 EndX=-81.6055 EndY=14.1107 EndZ=0
    g90: LineSegment StartX=-101.889 StartY=14.1107 StartZ=0 EndX=-101.889 EndY=25.9907 EndZ=0
    g91: LineSegment StartX=-101.889 StartY=25.9907 StartZ=0 EndX=-97.8594 EndY=25.9907 EndZ=0
    g92: LineSegment StartX=-97.8594 StartY=25.9907 StartZ=0 EndX=-97.8594 EndY=24.0907 EndZ=0
    g93: LineSegment StartX=-97.7455 StartY=14.1107 StartZ=0 EndX=-97.7455 EndY=19.9107 EndZ=0
    g94: LineSegment StartX=-89.6755 StartY=14.1107 StartZ=0 EndX=-89.6755 EndY=19.9107 EndZ=0
    g95: LineSegment StartX=-93.8155 StartY=14.1107 StartZ=0 EndX=-93.8155 EndY=21.0107 EndZ=0
    g96-g106: Circle x11 (B-spline internal-alignment scaffolding for g107; pole/knot coordinates omitted)
    g107: BSplineCurve PolesCount=11 KnotsCount=9 Degree=3 IsPeriodic=0
    g108-g116: GeomPoint x9 (B-spline internal-alignment scaffolding for g107; pole/knot coordinates omitted)
    g117: BSplineCurve PolesCount=11 KnotsCount=9 Degree=3 IsPeriodic=0
    g118-g125: Circle x8 (B-spline internal-alignment scaffolding for g126; pole/knot coordinates omitted)
    g126: BSplineCurve PolesCount=8 KnotsCount=6 Degree=3 IsPeriodic=0
    g127-g132: GeomPoint x6 (B-spline internal-alignment scaffolding for g126; pole/knot coordinates omitted)
    g133: BSplineCurve PolesCount=8 KnotsCount=6 Degree=3 IsPeriodic=0
    g134: LineSegment StartX=-85.7455 StartY=21.0107 StartZ=0 EndX=-85.7455 EndY=14.1107 EndZ=0
    g135: LineSegment StartX=-80.0879 StartY=14.1107 StartZ=0 EndX=-75.944 EndY=14.1107 EndZ=0
    g136: LineSegment StartX=-72.014 StartY=14.1107 StartZ=0 EndX=-67.874 EndY=14.1107 EndZ=0
    g137: LineSegment StartX=-63.944 StartY=14.1107 StartZ=0 EndX=-59.804 EndY=14.1107 EndZ=0
    g138: LineSegment StartX=-80.0879 StartY=14.1107 StartZ=0 EndX=-80.0879 EndY=25.9907 EndZ=0
    g139: LineSegment StartX=-80.0879 StartY=25.9907 StartZ=0 EndX=-76.0579 EndY=25.9907 EndZ=0
    g140: LineSegment StartX=-76.0579 StartY=25.9907 StartZ=0 EndX=-76.0579 EndY=24.0907 EndZ=0
    g141: LineSegment StartX=-75.944 StartY=14.1107 StartZ=0 EndX=-75.944 EndY=19.9107 EndZ=0
    g142: LineSegment StartX=-67.874 StartY=14.1107 StartZ=0 EndX=-67.874 EndY=19.9107 EndZ=0
    g143: LineSegment StartX=-72.014 StartY=14.1107 StartZ=0 EndX=-72.014 EndY=21.0107 EndZ=0
    g144-g148: Circle x5 (B-spline internal-alignment scaffolding for g149; pole/knot coordinates omitted)
    g149: BSplineCurve PolesCount=11 KnotsCount=9 Degree=3 IsPeriodic=0
    g150-g158: GeomPoint x9 (B-spline internal-alignment scaffolding for g149; pole/knot coordinates omitted)
    g159: BSplineCurve PolesCount=11 KnotsCount=9 Degree=3 IsPeriodic=0
    g160-g167: Circle x8 (B-spline internal-alignment scaffolding for g168; pole/knot coordinates omitted)
    g168: BSplineCurve PolesCount=8 KnotsCount=6 Degree=3 IsPeriodic=0
    g169-g174: GeomPoint x6 (B-spline internal-alignment scaffolding for g168; pole/knot coordinates omitted)
    g175: BSplineCurve PolesCount=8 KnotsCount=6 Degree=3 IsPeriodic=0
    g176: LineSegment StartX=-63.944 StartY=21.0107 StartZ=0 EndX=-63.944 EndY=14.1107 EndZ=0
    g177: LineSegment StartX=-59.804 StartY=14.1107 StartZ=0 EndX=-59.804 EndY=21.5868 EndZ=0
    g178: BSplineCurve PolesCount=4 KnotsCount=2 Degree=3 IsPeriodic=0
    g179: GeomPoint X=-59.804 Y=21.5868 Z=0
    g180: GeomPoint X=-60.2379 Y=24.0907 Z=0
    g181: LineSegment StartX=-81.6055 StartY=14.1107 StartZ=0 EndX=-81.6055 EndY=21.5868 EndZ=0
    g182: LineSegment StartX=-151.619 StartY=24.0313 StartZ=0 EndX=-145.128 EndY=24.0313 EndZ=0
    g183: Circle CenterX=-82.0394 CenterY=24.0907 CenterZ=0 NormalX=0 NormalY=0 NormalZ=1 AngleXU=0 Radius=1
    g184: Circle CenterX=-81.7131 CenterY=23.2736 CenterZ=0 NormalX=0 NormalY=0 NormalZ=1 AngleXU=0 Radius=1
    g185: Circle CenterX=-81.6055 CenterY=21.5868 CenterZ=0 NormalX=0 NormalY=0 NormalZ=1 AngleXU=0 Radius=1
    g186: BSplineCurve PolesCount=3 KnotsCount=2 Degree=2 IsPeriodic=0
    g187: GeomPoint X=-82.0394 Y=24.0907 Z=0
    g188: GeomPoint X=-81.6055 Y=21.5868 Z=0
    g189: Ellipse CenterX=-37.3522 CenterY=19.9515 CenterZ=0 NormalX=0 NormalY=0 NormalZ=1 MajorRadius=2.99755 MinorRadius=2.49 AngleXU=1.5708
    g190: GeomPoint X=-37.3522 Y=21.6203 Z=0
    g191: GeomPoint X=-37.3522 Y=18.2826 Z=0
    g192: ArcOfEllipse CenterX=-38.7647 CenterY=20.06 CenterZ=0 NormalX=0 NormalY=0 NormalZ=1 MajorRadius=6.30025 MinorRadius=5.3849 AngleXU=1.57276 StartAngle=5.50632 EndAngle=10.3035
    g193: GeomPoint X=-38.7711 Y=23.3304 Z=0
    g194: GeomPoint X=-38.7583 Y=16.7895 Z=0
    g195: LineSegment StartX=-34.6109 StartY=14.1107 StartZ=0 EndX=-30.8984 EndY=14.1107 EndZ=0
    g196: LineSegment StartX=-30.8984 StartY=14.1107 StartZ=0 EndX=-30.8984 EndY=31.1784 EndZ=0
    g197: LineSegment StartX=-30.8984 StartY=31.1784 StartZ=0 EndX=-34.9984 EndY=31.1784 EndZ=0
    g198: LineSegment StartX=-34.9984 StartY=24.5602 StartZ=0 EndX=-34.9984 EndY=31.1784 EndZ=0
    g199: LineSegment StartX=-34.6109 StartY=16.0476 StartZ=0 EndX=-34.6109 EndY=14.1107 EndZ=0
    g200: LineSegment StartX=-14.8781 StartY=14.1107 StartZ=0 EndX=-10.5106 EndY=14.1107 EndZ=0
    g201: LineSegment StartX=-14.8781 StartY=14.1107 StartZ=0 EndX=-14.8781 EndY=25.8504 EndZ=0
    g202: LineSegment StartX=-14.8781 StartY=25.8504 StartZ=0 EndX=-10.8534 EndY=25.8504 EndZ=0
    g203: LineSegment StartX=-10.8534 StartY=25.8504 StartZ=0 EndX=-10.8534 EndY=24.0923 EndZ=0
    g204: LineSegment StartX=-10.5106 StartY=14.1107 StartZ=0 EndX=-10.5106 EndY=19.7752 EndZ=0
    g205: LineSegment StartX=-5.96397 StartY=25.9304 StartZ=0 EndX=-5.96397 EndY=22.574 EndZ=0
    g206-g214: Circle x9 (B-spline internal-alignment scaffolding for g215; pole/knot coordinates omitted)
    g215: BSplineCurve PolesCount=9 KnotsCount=7 Degree=3 IsPeriodic=0
    g216-g222: GeomPoint x7 (B-spline internal-alignment scaffolding for g215; pole/knot coordinates omitted)
    g223-g232: Circle x10 (B-spline internal-alignment scaffolding for g233; pole/knot coordinates omitted)
    g233: BSplineCurve PolesCount=10 KnotsCount=8 Degree=3 IsPeriodic=0
    g234-g241: GeomPoint x8 (B-spline internal-alignment scaffolding for g233; pole/knot coordinates omitted)
  constraints (225):
    c: Coincident(g1,g0)
    c: Horizontal(g0)
    c: Vertical(g1)
    c: Coincident(g2,g3)
    c: Coincident(g3,g4)
    c: Horizontal(g4)
    c: Horizontal(g2)
    c: Vertical(g3)
    c: Block(g1)
    c: Distance(g3) = 4.86
    c: Block(g4)
    c: Distance(g0) = 10.8
    c: Distance(g2) = 10.8
    c: Coincident(g5,g0)
    c: Coincident(g6,g4)
    c: Coincident(g6,g2)
    c: Block(g8)
    c: Block(g7)
    c: Coincident(g9,g8)
    c: Coincident(g9,g7)
    c: Vertical(g9)
    c: Coincident(g10,g7)
    c: Coincident(g10,g8)
    c: Vertical(g10)
    c: Weight(g11) = 1
    c: Equal(g11, g12-g21) x10
    c: InternalAlignment(g11-g21 -> g22) x11
    c: InternalAlignment(g23-g31 -> g22) x9
    c: Block(g22)
    c: Weight(g32) = 1
    c: Equal(g32, g33-g49) x17
    c: InternalAlignment(g32-g49 -> g50) x18
    c: InternalAlignment(g51-g66 -> g50) x16
    c: Block(g50)
    c: Coincident(g67,g50)
    c: Coincident(g67,g22)
    c: Coincident(g68,g22)
    c: Coincident(g68,g50)
    c: InternalAlignment(g70,g69)
    c: InternalAlignment(g71,g69)
    c: Block(g69)
    c: InternalAlignment(g73,g72)
    c: InternalAlignment(g74,g72)
    c: Block(g72)
    c: InternalAlignment(g76,g75)
    c: InternalAlignment(g77,g75)
    c: InternalAlignment(g78,g80)
    c: InternalAlignment(g79,g80)
    c: Block(g80)
    c: Coincident(g75,g80)
    c: Block(g75)
    c: InternalAlignment(g82,g81)
    c: InternalAlignment(g83,g81)
    c: InternalAlignment(g84,g86)
    c: InternalAlignment(g85,g86)
    c: Block(g86)
    c: Coincident(g81,g86)
    c: Block(g81)
    c: Horizontal(g87)
    c: Block(g87)
    c: Horizontal(g88)
    c: Distance(g88) = 4.14
    c: Horizontal(g89)
    c: Equal(g88,g89) = 4.14
    c: Block(g89)
    c: Block(g88)
    c: Coincident(g90,g87)
    c: Vertical(g90)
    c: Distance(g90) = 11.88
    c: Coincident(g91,g90)
    c: Horizontal(g91)
    c: Coincident(g92,g91)
    c: Vertical(g92)
    c: Distance(g91) = 4.03
    c: Distance(g92) = 1.9
    c: Coincident(g93,g87)
    c: Vertical(g93)
    c: Vertical(g94)
    c: Coincident(g94,g88)
    c: Distance(g93) = 5.8
    c: Distance(g94) = 5.8
    c: Vertical(g95)
    c: Coincident(g95,g88)
    c: Distance(g95) = 6.9
    c: Coincident(g107,g92)
    c: Weight(g96) = 1
    c: Equal(g96, g97-g106) x10
    c: InternalAlignment(g96-g106 -> g107) x11
    c: InternalAlignment(g108-g116 -> g107) x9
    c: Block(g107)
    c: Block(g117)
    c: Coincident(g126,g93)
    c: Weight(g118) = 1
    c: Equal(g118, g119-g125) x7
    c: Coincident(g126,g95)
    c: InternalAlignment(g118-g125 -> g126) x8
    c: InternalAlignment(g127-g132 -> g126) x6
    c: Coincident(g133,g94)
    c: Block(g126)
    c: Block(g133)
    c: Coincident(g134,g133)
    c: Coincident(g134,g89)
    c: Vertical(g134)
    c: Horizontal(g135)
    c: Block(g135)
    c: Horizontal(g136)
    c: Equal(g88,g136) = 4.14
    c: Horizontal(g137)
    c: Equal(g136,g137) = 4.14
    c: Block(g137)
    c: Block(g136)
    c: Coincident(g138,g135)
    c: Vertical(g138)
    c: Equal(g90,g138) = 11.88
    c: Coincident(g139,g138)
    c: Horizontal(g139)
    c: Coincident(g140,g139)
    c: Vertical(g140)
    c: Equal(g91,g139) = 4.03
    c: Equal(g92,g140) = 1.9
    c: Coincident(g141,g135)
    c: Vertical(g141)
    c: Vertical(g142)
    c: Coincident(g142,g136)
    c: Equal(g93,g141) = 5.8
    c: Equal(g94,g142) = 5.8
    c: Vertical(g143)
    c: Coincident(g143,g136)
    c: Equal(g95,g143) = 6.9
    c: Coincident(g149,g140)
    c: Equal(g96,g144) = 1
    c: Equal(g144, g145-g148) x4
    c: InternalAlignment(g144-g148 -> g149) x5
    c: InternalAlignment(g150-g158 -> g149) x9
    c: Block(g149)
    c: Block(g159)
    c: Coincident(g168,g141)
    c: Equal(g118,g160) = 1
    c: Equal(g160, g161-g167) x7
    c: Coincident(g168,g143)
    c: InternalAlignment(g160-g167 -> g168) x8
    c: InternalAlignment(g169-g174 -> g168) x6
    c: Coincident(g175,g142)
    c: Block(g168)
    c: Block(g175)
    c: Coincident(g176,g175)
    c: Coincident(g176,g137)
    c: Vertical(g176)
    c: Coincident(g177,g137)
    c: Vertical(g177)
    c: Coincident(g178,g177)
    c: Coincident(g178,g159)
    c: InternalAlignment(g179,g178)
    c: InternalAlignment(g180,g178)
    c: Block(g178)
    c: Vertical(g181)
    c: Coincident(g181,g89)
    c: Block(g5)
    c: Coincident(g182,g1)
    c: Coincident(g182,g5)
    c: Horizontal(g182)
    c: Coincident(g186,g117)
    c: Weight(g183) = 1
    c: Equal(g183,g184)
    c: Equal(g183,g185)
    c: Coincident(g186,g181)
    c: InternalAlignment(g183,g186)
    c: InternalAlignment(g184,g186)
    c: InternalAlignment(g185,g186)
    c: InternalAlignment(g187,g186)
    c: InternalAlignment(g188,g186)
    c: Block(g186)
    c: InternalAlignment(g190,g189)
    c: InternalAlignment(g191,g189)
    c: Block(g189)
    c: InternalAlignment(g193,g192)
    c: InternalAlignment(g194,g192)
    c: Block(g192)
    c: Horizontal(g195)
    c: Block(g195)
    c: Coincident(g196,g195)
    c: Vertical(g196)
    c: Block(g196)
    c: Distance(g195) = 3.71244
    c: Coincident(g197,g196)
    c: Horizontal(g197)
    c: Distance(g197) = 4.1
    c: Coincident(g198,g192)
    c: Coincident(g198,g197)
    c: Vertical(g198)
    c: Block(g198)
    c: Coincident(g199,g192)
    c: Coincident(g199,g195)
    c: Vertical(g199)
    c: Block(g199)
    c: Horizontal(g200)
    c: Block(g200)
    c: Coincident(g201,g200)
    c: Vertical(g201)
    c: Block(g201)
    c: Coincident(g202,g201)
    c: Horizontal(g202)
    c: Block(g202)
    c: Coincident(g203,g202)
    c: Vertical(g203)
    c: Block(g203)
    c: Coincident(g204,g200)
    c: Vertical(g204)
    c: Block(g204)
    c: Coincident(g215,g203)
    c: Weight(g206) = 1
    c: Equal(g206, g207-g214) x8
    c: Coincident(g215,g205)
    c: InternalAlignment(g206-g214 -> g215) x9
    c: InternalAlignment(g216-g222 -> g215) x7
    c: Coincident(g233,g204)
    c: Weight(g223) = 1
    c: Equal(g223, g224-g232) x9
    c: Coincident(g233,g205)
    c: InternalAlignment(g223-g232 -> g233) x10
    c: InternalAlignment(g234-g241 -> g233) x8
    c: Vertical(g205)
    c: Block(g205)
    c: Block(g215)
    c: Block(g233)
FEATURE [PartDesign::Body] Body
  Group = -> [Sketch083]
  Origin = -> Origin
FEATURE [Sketcher::SketchObject] Sketch084
  FullyConstrained = true
  MapMode = 5
  Support = -> [XY_Plane001]
FEATURE [PartDesign::Body] Body001
  Group = -> [Sketch084]
  Origin = -> Origin001
